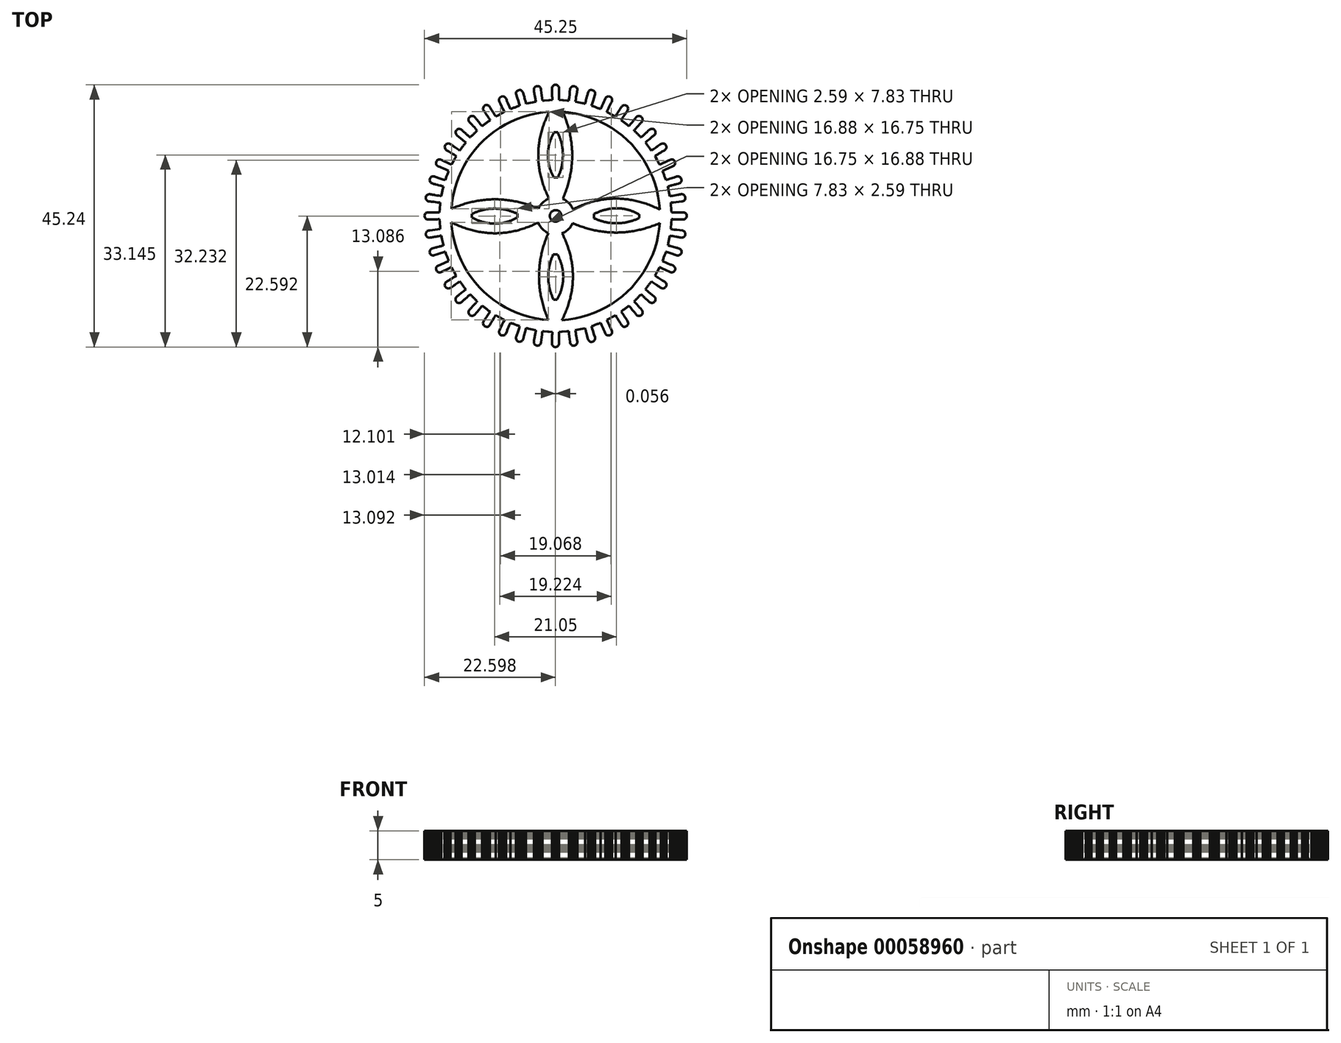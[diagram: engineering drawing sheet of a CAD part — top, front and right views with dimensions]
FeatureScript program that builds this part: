
annotation { "Feature Type Name" : "Feature", "Feature Type Description" : "" }
export const myFeature = defineFeature(function(context is Context, id is Id, definition is map)
    precondition{}
    {
        {
            var Q0;
            Q0=qCreatedBy(makeId("Top.planeOp"),FACE);
            var sketch = newSketch(context, id + "F0", { "sketchPlane" : qUnion([Q0])});
            skLineSegment(sketch, "E0", {"start": v(19.24, -0.57) * mm, "end": v(19.37, -0.57) * mm});
            skLineSegment(sketch, "E1", {"start": v(19.37, -0.57) * mm, "end": v(19.52, -0.58) * mm});
            skLineSegment(sketch, "E2", {"start": v(19.52, -0.58) * mm, "end": v(19.68, -0.58) * mm});
            skLineSegment(sketch, "E3", {"start": v(19.68, -0.58) * mm, "end": v(19.83, -0.59) * mm});
            skLineSegment(sketch, "E4", {"start": v(19.83, -0.59) * mm, "end": v(19.99, -0.6) * mm});
            skLineSegment(sketch, "E5", {"start": v(19.99, -0.6) * mm, "end": v(20.14, -0.6) * mm});
            skLineSegment(sketch, "E6", {"start": v(20.14, -0.6) * mm, "end": v(20.3, -0.6) * mm});
            skLineSegment(sketch, "E7", {"start": v(20.3, -0.6) * mm, "end": v(20.45, -0.6) * mm});
            skLineSegment(sketch, "E8", {"start": v(20.45, -0.6) * mm, "end": v(20.6, -0.6) * mm});
            skLineSegment(sketch, "E9", {"start": v(20.6, -0.6) * mm, "end": v(20.76, -0.61) * mm});
            skLineSegment(sketch, "E10", {"start": v(20.76, -0.61) * mm, "end": v(20.9, -0.62) * mm});
            skLineSegment(sketch, "E11", {"start": v(20.9, -0.62) * mm, "end": v(21.06, -0.62) * mm});
            skLineSegment(sketch, "E12", {"start": v(21.06, -0.62) * mm, "end": v(21.22, -0.63) * mm});
            skLineSegment(sketch, "E13", {"start": v(21.22, -0.63) * mm, "end": v(21.38, -0.6) * mm});
            skLineSegment(sketch, "E14", {"start": v(21.38, -0.6) * mm, "end": v(21.53, -0.54) * mm});
            skLineSegment(sketch, "E15", {"start": v(21.53, -0.54) * mm, "end": v(21.66, -0.45) * mm});
            skLineSegment(sketch, "E16", {"start": v(21.66, -0.45) * mm, "end": v(21.77, -0.32) * mm});
            skLineSegment(sketch, "E17", {"start": v(21.77, -0.32) * mm, "end": v(21.83, -0.16) * mm});
            skLineSegment(sketch, "E18", {"start": v(21.83, -0.16) * mm, "end": v(21.85, 0) * mm});
            skLineSegment(sketch, "E19", {"start": v(21.85, 0) * mm, "end": v(21.83, 0.16) * mm});
            skLineSegment(sketch, "E20", {"start": v(21.83, 0.16) * mm, "end": v(21.77, 0.31) * mm});
            skLineSegment(sketch, "E21", {"start": v(21.77, 0.31) * mm, "end": v(21.66, 0.44) * mm});
            skLineSegment(sketch, "E22", {"start": v(21.66, 0.44) * mm, "end": v(21.53, 0.54) * mm});
            skLineSegment(sketch, "E23", {"start": v(21.53, 0.54) * mm, "end": v(21.38, 0.6) * mm});
            skLineSegment(sketch, "E24", {"start": v(21.38, 0.6) * mm, "end": v(21.22, 0.62) * mm});
            skLineSegment(sketch, "E25", {"start": v(21.22, 0.62) * mm, "end": v(21.06, 0.62) * mm});
            skLineSegment(sketch, "E26", {"start": v(21.06, 0.62) * mm, "end": v(20.91, 0.62) * mm});
            skLineSegment(sketch, "E27", {"start": v(20.91, 0.62) * mm, "end": v(20.76, 0.61) * mm});
            skLineSegment(sketch, "E28", {"start": v(20.76, 0.61) * mm, "end": v(20.6, 0.6) * mm});
            skLineSegment(sketch, "E29", {"start": v(20.6, 0.6) * mm, "end": v(20.45, 0.6) * mm});
            skLineSegment(sketch, "E30", {"start": v(20.45, 0.6) * mm, "end": v(20.3, 0.6) * mm});
            skLineSegment(sketch, "E31", {"start": v(20.3, 0.6) * mm, "end": v(20.14, 0.6) * mm});
            skLineSegment(sketch, "E32", {"start": v(20.14, 0.6) * mm, "end": v(19.99, 0.59) * mm});
            skLineSegment(sketch, "E33", {"start": v(19.99, 0.59) * mm, "end": v(19.83, 0.59) * mm});
            skLineSegment(sketch, "E34", {"start": v(19.83, 0.59) * mm, "end": v(19.68, 0.58) * mm});
            skLineSegment(sketch, "E35", {"start": v(19.68, 0.58) * mm, "end": v(19.53, 0.58) * mm});
            skLineSegment(sketch, "E36", {"start": v(19.53, 0.58) * mm, "end": v(19.37, 0.57) * mm});
            skLineSegment(sketch, "E37", {"start": v(19.37, 0.57) * mm, "end": v(19.24, 0.57) * mm});
            skLineSegment(sketch, "E38", {"start": v(19.24, 0.57) * mm, "end": v(19.23, 0.72) * mm});
            skLineSegment(sketch, "E39", {"start": v(19.23, 0.72) * mm, "end": v(19.22, 0.87) * mm});
            skLineSegment(sketch, "E40", {"start": v(19.22, 0.87) * mm, "end": v(19.2, 1.03) * mm});
            skLineSegment(sketch, "E41", {"start": v(19.2, 1.03) * mm, "end": v(19.2, 1.18) * mm});
            skLineSegment(sketch, "E42", {"start": v(19.2, 1.18) * mm, "end": v(19.19, 1.33) * mm});
            skLineSegment(sketch, "E43", {"start": v(19.19, 1.33) * mm, "end": v(19.17, 1.49) * mm});
            skLineSegment(sketch, "E44", {"start": v(19.17, 1.49) * mm, "end": v(19.16, 1.64) * mm});
            skLineSegment(sketch, "E45", {"start": v(19.16, 1.64) * mm, "end": v(19.15, 1.8) * mm});
            skLineSegment(sketch, "E46", {"start": v(19.15, 1.8) * mm, "end": v(19.14, 1.94) * mm});
            skLineSegment(sketch, "E47", {"start": v(19.14, 1.94) * mm, "end": v(19.13, 2.1) * mm});
            skLineSegment(sketch, "E48", {"start": v(19.13, 2.1) * mm, "end": v(19.12, 2.25) * mm});
            skLineSegment(sketch, "E49", {"start": v(19.12, 2.25) * mm, "end": v(19.12, 2.28) * mm});
            skLineSegment(sketch, "E50", {"start": v(19.12, 2.28) * mm, "end": v(19.27, 2.3) * mm});
            skLineSegment(sketch, "E51", {"start": v(19.27, 2.3) * mm, "end": v(19.42, 2.32) * mm});
            skLineSegment(sketch, "E52", {"start": v(19.42, 2.32) * mm, "end": v(19.58, 2.34) * mm});
            skLineSegment(sketch, "E53", {"start": v(19.58, 2.34) * mm, "end": v(19.73, 2.35) * mm});
            skLineSegment(sketch, "E54", {"start": v(19.73, 2.35) * mm, "end": v(19.88, 2.37) * mm});
            skLineSegment(sketch, "E55", {"start": v(19.88, 2.37) * mm, "end": v(20.03, 2.39) * mm});
            skLineSegment(sketch, "E56", {"start": v(20.03, 2.39) * mm, "end": v(20.19, 2.4) * mm});
            skLineSegment(sketch, "E57", {"start": v(20.19, 2.4) * mm, "end": v(20.34, 2.42) * mm});
            skLineSegment(sketch, "E58", {"start": v(20.34, 2.42) * mm, "end": v(20.5, 2.44) * mm});
            skLineSegment(sketch, "E59", {"start": v(20.5, 2.44) * mm, "end": v(20.64, 2.46) * mm});
            skLineSegment(sketch, "E60", {"start": v(20.64, 2.46) * mm, "end": v(20.8, 2.48) * mm});
            skLineSegment(sketch, "E61", {"start": v(20.8, 2.48) * mm, "end": v(20.95, 2.5) * mm});
            skLineSegment(sketch, "E62", {"start": v(20.95, 2.5) * mm, "end": v(21.11, 2.52) * mm});
            skLineSegment(sketch, "E63", {"start": v(21.11, 2.52) * mm, "end": v(21.27, 2.57) * mm});
            skLineSegment(sketch, "E64", {"start": v(21.27, 2.57) * mm, "end": v(21.4, 2.66) * mm});
            skLineSegment(sketch, "E65", {"start": v(21.4, 2.66) * mm, "end": v(21.52, 2.78) * mm});
            skLineSegment(sketch, "E66", {"start": v(21.52, 2.78) * mm, "end": v(21.6, 2.93) * mm});
            skLineSegment(sketch, "E67", {"start": v(21.6, 2.93) * mm, "end": v(21.63, 3.09) * mm});
            skLineSegment(sketch, "E68", {"start": v(21.63, 3.09) * mm, "end": v(21.62, 3.25) * mm});
            skLineSegment(sketch, "E69", {"start": v(21.62, 3.25) * mm, "end": v(21.56, 3.4) * mm});
            skLineSegment(sketch, "E70", {"start": v(21.56, 3.4) * mm, "end": v(21.47, 3.54) * mm});
            skLineSegment(sketch, "E71", {"start": v(21.47, 3.54) * mm, "end": v(21.35, 3.65) * mm});
            skLineSegment(sketch, "E72", {"start": v(21.35, 3.65) * mm, "end": v(21.2, 3.72) * mm});
            skLineSegment(sketch, "E73", {"start": v(21.2, 3.72) * mm, "end": v(21.04, 3.75) * mm});
            skLineSegment(sketch, "E74", {"start": v(21.04, 3.75) * mm, "end": v(21, 3.76) * mm});
            skLineSegment(sketch, "E75", {"start": v(21, 3.76) * mm, "end": v(20.9, 3.75) * mm});
            skLineSegment(sketch, "E76", {"start": v(20.9, 3.75) * mm, "end": v(20.75, 3.72) * mm});
            skLineSegment(sketch, "E77", {"start": v(20.75, 3.72) * mm, "end": v(20.6, 3.7) * mm});
            skLineSegment(sketch, "E78", {"start": v(20.6, 3.7) * mm, "end": v(20.45, 3.67) * mm});
            skLineSegment(sketch, "E79", {"start": v(20.45, 3.67) * mm, "end": v(20.3, 3.64) * mm});
            skLineSegment(sketch, "E80", {"start": v(20.3, 3.64) * mm, "end": v(20.15, 3.62) * mm});
            skLineSegment(sketch, "E81", {"start": v(20.15, 3.62) * mm, "end": v(20, 3.6) * mm});
            skLineSegment(sketch, "E82", {"start": v(20, 3.6) * mm, "end": v(19.84, 3.56) * mm});
            skLineSegment(sketch, "E83", {"start": v(19.84, 3.56) * mm, "end": v(19.7, 3.54) * mm});
            skLineSegment(sketch, "E84", {"start": v(19.7, 3.54) * mm, "end": v(19.54, 3.51) * mm});
            skLineSegment(sketch, "E85", {"start": v(19.54, 3.51) * mm, "end": v(19.39, 3.49) * mm});
            skLineSegment(sketch, "E86", {"start": v(19.39, 3.49) * mm, "end": v(19.24, 3.46) * mm});
            skLineSegment(sketch, "E87", {"start": v(19.24, 3.46) * mm, "end": v(19.09, 3.43) * mm});
            skLineSegment(sketch, "E88", {"start": v(19.09, 3.43) * mm, "end": v(18.96, 3.41) * mm});
            skLineSegment(sketch, "E89", {"start": v(18.96, 3.41) * mm, "end": v(18.92, 3.56) * mm});
            skLineSegment(sketch, "E90", {"start": v(18.92, 3.56) * mm, "end": v(18.9, 3.71) * mm});
            skLineSegment(sketch, "E91", {"start": v(18.9, 3.71) * mm, "end": v(18.86, 3.86) * mm});
            skLineSegment(sketch, "E92", {"start": v(18.86, 3.86) * mm, "end": v(18.83, 4) * mm});
            skLineSegment(sketch, "E93", {"start": v(18.83, 4) * mm, "end": v(18.8, 4.16) * mm});
            skLineSegment(sketch, "E94", {"start": v(18.8, 4.16) * mm, "end": v(18.76, 4.3) * mm});
            skLineSegment(sketch, "E95", {"start": v(18.76, 4.3) * mm, "end": v(18.73, 4.46) * mm});
            skLineSegment(sketch, "E96", {"start": v(18.73, 4.46) * mm, "end": v(18.7, 4.6) * mm});
            skLineSegment(sketch, "E97", {"start": v(18.7, 4.6) * mm, "end": v(18.66, 4.76) * mm});
            skLineSegment(sketch, "E98", {"start": v(18.66, 4.76) * mm, "end": v(18.63, 4.9) * mm});
            skLineSegment(sketch, "E99", {"start": v(18.63, 4.9) * mm, "end": v(18.6, 5.06) * mm});
            skLineSegment(sketch, "E100", {"start": v(18.6, 5.06) * mm, "end": v(18.59, 5.1) * mm});
            skLineSegment(sketch, "E101", {"start": v(18.59, 5.1) * mm, "end": v(18.74, 5.13) * mm});
            skLineSegment(sketch, "E102", {"start": v(18.74, 5.13) * mm, "end": v(18.89, 5.17) * mm});
            skLineSegment(sketch, "E103", {"start": v(18.89, 5.17) * mm, "end": v(19.04, 5.2) * mm});
            skLineSegment(sketch, "E104", {"start": v(19.04, 5.2) * mm, "end": v(19.18, 5.25) * mm});
            skLineSegment(sketch, "E105", {"start": v(19.18, 5.25) * mm, "end": v(19.33, 5.29) * mm});
            skLineSegment(sketch, "E106", {"start": v(19.33, 5.29) * mm, "end": v(19.48, 5.33) * mm});
            skLineSegment(sketch, "E107", {"start": v(19.48, 5.33) * mm, "end": v(19.63, 5.37) * mm});
            skLineSegment(sketch, "E108", {"start": v(19.63, 5.37) * mm, "end": v(19.78, 5.4) * mm});
            skLineSegment(sketch, "E109", {"start": v(19.78, 5.4) * mm, "end": v(19.93, 5.44) * mm});
            skLineSegment(sketch, "E110", {"start": v(19.93, 5.44) * mm, "end": v(20.08, 5.48) * mm});
            skLineSegment(sketch, "E111", {"start": v(20.08, 5.48) * mm, "end": v(20.22, 5.52) * mm});
            skLineSegment(sketch, "E112", {"start": v(20.22, 5.52) * mm, "end": v(20.37, 5.56) * mm});
            skLineSegment(sketch, "E113", {"start": v(20.37, 5.56) * mm, "end": v(20.53, 5.6) * mm});
            skLineSegment(sketch, "E114", {"start": v(20.53, 5.6) * mm, "end": v(20.68, 5.68) * mm});
            skLineSegment(sketch, "E115", {"start": v(20.68, 5.68) * mm, "end": v(20.8, 5.79) * mm});
            skLineSegment(sketch, "E116", {"start": v(20.8, 5.79) * mm, "end": v(20.9, 5.92) * mm});
            skLineSegment(sketch, "E117", {"start": v(20.9, 5.92) * mm, "end": v(20.95, 6.08) * mm});
            skLineSegment(sketch, "E118", {"start": v(20.95, 6.08) * mm, "end": v(20.96, 6.24) * mm});
            skLineSegment(sketch, "E119", {"start": v(20.96, 6.24) * mm, "end": v(20.92, 6.4) * mm});
            skLineSegment(sketch, "E120", {"start": v(20.92, 6.4) * mm, "end": v(20.85, 6.55) * mm});
            skLineSegment(sketch, "E121", {"start": v(20.85, 6.55) * mm, "end": v(20.74, 6.67) * mm});
            skLineSegment(sketch, "E122", {"start": v(20.74, 6.67) * mm, "end": v(20.6, 6.76) * mm});
            skLineSegment(sketch, "E123", {"start": v(20.6, 6.76) * mm, "end": v(20.44, 6.81) * mm});
            skLineSegment(sketch, "E124", {"start": v(20.44, 6.81) * mm, "end": v(20.35, 6.82) * mm});
            skLineSegment(sketch, "E125", {"start": v(20.35, 6.82) * mm, "end": v(20.18, 6.8) * mm});
            skLineSegment(sketch, "E126", {"start": v(20.18, 6.8) * mm, "end": v(20.15, 6.8) * mm});
            skLineSegment(sketch, "E127", {"start": v(20.15, 6.8) * mm, "end": v(20, 6.75) * mm});
            skLineSegment(sketch, "E128", {"start": v(20, 6.75) * mm, "end": v(19.86, 6.7) * mm});
            skLineSegment(sketch, "E129", {"start": v(19.86, 6.7) * mm, "end": v(19.71, 6.65) * mm});
            skLineSegment(sketch, "E130", {"start": v(19.71, 6.65) * mm, "end": v(19.57, 6.6) * mm});
            skLineSegment(sketch, "E131", {"start": v(19.57, 6.6) * mm, "end": v(19.42, 6.56) * mm});
            skLineSegment(sketch, "E132", {"start": v(19.42, 6.56) * mm, "end": v(19.27, 6.5) * mm});
            skLineSegment(sketch, "E133", {"start": v(19.27, 6.5) * mm, "end": v(19.13, 6.46) * mm});
            skLineSegment(sketch, "E134", {"start": v(19.13, 6.46) * mm, "end": v(18.98, 6.42) * mm});
            skLineSegment(sketch, "E135", {"start": v(18.98, 6.42) * mm, "end": v(18.83, 6.37) * mm});
            skLineSegment(sketch, "E136", {"start": v(18.83, 6.37) * mm, "end": v(18.69, 6.32) * mm});
            skLineSegment(sketch, "E137", {"start": v(18.69, 6.32) * mm, "end": v(18.54, 6.27) * mm});
            skLineSegment(sketch, "E138", {"start": v(18.54, 6.27) * mm, "end": v(18.4, 6.22) * mm});
            skLineSegment(sketch, "E139", {"start": v(18.4, 6.22) * mm, "end": v(18.27, 6.18) * mm});
            skLineSegment(sketch, "E140", {"start": v(18.27, 6.18) * mm, "end": v(18.22, 6.33) * mm});
            skLineSegment(sketch, "E141", {"start": v(18.22, 6.33) * mm, "end": v(18.16, 6.47) * mm});
            skLineSegment(sketch, "E142", {"start": v(18.16, 6.47) * mm, "end": v(18.1, 6.61) * mm});
            skLineSegment(sketch, "E143", {"start": v(18.1, 6.61) * mm, "end": v(18.05, 6.76) * mm});
            skLineSegment(sketch, "E144", {"start": v(18.05, 6.76) * mm, "end": v(18, 6.9) * mm});
            skLineSegment(sketch, "E145", {"start": v(18, 6.9) * mm, "end": v(17.95, 7.05) * mm});
            skLineSegment(sketch, "E146", {"start": v(17.95, 7.05) * mm, "end": v(17.9, 7.19) * mm});
            skLineSegment(sketch, "E147", {"start": v(17.9, 7.19) * mm, "end": v(17.84, 7.33) * mm});
            skLineSegment(sketch, "E148", {"start": v(17.84, 7.33) * mm, "end": v(17.79, 7.48) * mm});
            skLineSegment(sketch, "E149", {"start": v(17.79, 7.48) * mm, "end": v(17.73, 7.62) * mm});
            skLineSegment(sketch, "E150", {"start": v(17.73, 7.62) * mm, "end": v(17.68, 7.76) * mm});
            skLineSegment(sketch, "E151", {"start": v(17.68, 7.76) * mm, "end": v(17.67, 7.8) * mm});
            skLineSegment(sketch, "E152", {"start": v(17.67, 7.8) * mm, "end": v(17.8, 7.86) * mm});
            skLineSegment(sketch, "E153", {"start": v(17.8, 7.86) * mm, "end": v(17.95, 7.92) * mm});
            skLineSegment(sketch, "E154", {"start": v(17.95, 7.92) * mm, "end": v(18.1, 7.98) * mm});
            skLineSegment(sketch, "E155", {"start": v(18.1, 7.98) * mm, "end": v(18.23, 8.04) * mm});
            skLineSegment(sketch, "E156", {"start": v(18.23, 8.04) * mm, "end": v(18.38, 8.1) * mm});
            skLineSegment(sketch, "E157", {"start": v(18.38, 8.1) * mm, "end": v(18.52, 8.16) * mm});
            skLineSegment(sketch, "E158", {"start": v(18.52, 8.16) * mm, "end": v(18.66, 8.22) * mm});
            skLineSegment(sketch, "E159", {"start": v(18.66, 8.22) * mm, "end": v(18.8, 8.27) * mm});
            skLineSegment(sketch, "E160", {"start": v(18.8, 8.27) * mm, "end": v(18.94, 8.34) * mm});
            skLineSegment(sketch, "E161", {"start": v(18.94, 8.34) * mm, "end": v(19.08, 8.4) * mm});
            skLineSegment(sketch, "E162", {"start": v(19.08, 8.4) * mm, "end": v(19.23, 8.45) * mm});
            skLineSegment(sketch, "E163", {"start": v(19.23, 8.45) * mm, "end": v(19.37, 8.51) * mm});
            skLineSegment(sketch, "E164", {"start": v(19.37, 8.51) * mm, "end": v(19.52, 8.58) * mm});
            skLineSegment(sketch, "E165", {"start": v(19.52, 8.58) * mm, "end": v(19.66, 8.67) * mm});
            skLineSegment(sketch, "E166", {"start": v(19.66, 8.67) * mm, "end": v(19.76, 8.8) * mm});
            skLineSegment(sketch, "E167", {"start": v(19.76, 8.8) * mm, "end": v(19.83, 8.95) * mm});
            skLineSegment(sketch, "E168", {"start": v(19.83, 8.95) * mm, "end": v(19.86, 9.1) * mm});
            skLineSegment(sketch, "E169", {"start": v(19.86, 9.1) * mm, "end": v(19.85, 9.27) * mm});
            skLineSegment(sketch, "E170", {"start": v(19.85, 9.27) * mm, "end": v(19.8, 9.4) * mm});
            skLineSegment(sketch, "E171", {"start": v(19.8, 9.4) * mm, "end": v(19.72, 9.54) * mm});
            skLineSegment(sketch, "E172", {"start": v(19.72, 9.54) * mm, "end": v(19.6, 9.65) * mm});
            skLineSegment(sketch, "E173", {"start": v(19.6, 9.65) * mm, "end": v(19.45, 9.73) * mm});
            skLineSegment(sketch, "E174", {"start": v(19.45, 9.73) * mm, "end": v(19.3, 9.76) * mm});
            skLineSegment(sketch, "E175", {"start": v(19.3, 9.76) * mm, "end": v(19.23, 9.76) * mm});
            skLineSegment(sketch, "E176", {"start": v(19.23, 9.76) * mm, "end": v(19.06, 9.74) * mm});
            skLineSegment(sketch, "E177", {"start": v(19.06, 9.74) * mm, "end": v(18.97, 9.7) * mm});
            skLineSegment(sketch, "E178", {"start": v(18.97, 9.7) * mm, "end": v(18.83, 9.64) * mm});
            skLineSegment(sketch, "E179", {"start": v(18.83, 9.64) * mm, "end": v(18.7, 9.57) * mm});
            skLineSegment(sketch, "E180", {"start": v(18.7, 9.57) * mm, "end": v(18.56, 9.5) * mm});
            skLineSegment(sketch, "E181", {"start": v(18.56, 9.5) * mm, "end": v(18.42, 9.43) * mm});
            skLineSegment(sketch, "E182", {"start": v(18.42, 9.43) * mm, "end": v(18.28, 9.37) * mm});
            skLineSegment(sketch, "E183", {"start": v(18.28, 9.37) * mm, "end": v(18.14, 9.3) * mm});
            skLineSegment(sketch, "E184", {"start": v(18.14, 9.3) * mm, "end": v(18, 9.23) * mm});
            skLineSegment(sketch, "E185", {"start": v(18, 9.23) * mm, "end": v(17.87, 9.16) * mm});
            skLineSegment(sketch, "E186", {"start": v(17.87, 9.16) * mm, "end": v(17.73, 9.1) * mm});
            skLineSegment(sketch, "E187", {"start": v(17.73, 9.1) * mm, "end": v(17.6, 9.03) * mm});
            skLineSegment(sketch, "E188", {"start": v(17.6, 9.03) * mm, "end": v(17.45, 8.96) * mm});
            skLineSegment(sketch, "E189", {"start": v(17.45, 8.96) * mm, "end": v(17.31, 8.89) * mm});
            skLineSegment(sketch, "E190", {"start": v(17.31, 8.89) * mm, "end": v(17.2, 8.83) * mm});
            skLineSegment(sketch, "E191", {"start": v(17.2, 8.83) * mm, "end": v(17.12, 8.97) * mm});
            skLineSegment(sketch, "E192", {"start": v(17.12, 8.97) * mm, "end": v(17.05, 9.1) * mm});
            skLineSegment(sketch, "E193", {"start": v(17.05, 9.1) * mm, "end": v(16.97, 9.23) * mm});
            skLineSegment(sketch, "E194", {"start": v(16.97, 9.23) * mm, "end": v(16.9, 9.37) * mm});
            skLineSegment(sketch, "E195", {"start": v(16.9, 9.37) * mm, "end": v(16.83, 9.5) * mm});
            skLineSegment(sketch, "E196", {"start": v(16.83, 9.5) * mm, "end": v(16.75, 9.64) * mm});
            skLineSegment(sketch, "E197", {"start": v(16.75, 9.64) * mm, "end": v(16.68, 9.77) * mm});
            skLineSegment(sketch, "E198", {"start": v(16.68, 9.77) * mm, "end": v(16.6, 9.9) * mm});
            skLineSegment(sketch, "E199", {"start": v(16.6, 9.9) * mm, "end": v(16.53, 10.04) * mm});
            skLineSegment(sketch, "E200", {"start": v(16.53, 10.04) * mm, "end": v(16.46, 10.18) * mm});
            skLineSegment(sketch, "E201", {"start": v(16.46, 10.18) * mm, "end": v(16.39, 10.3) * mm});
            skLineSegment(sketch, "E202", {"start": v(16.39, 10.3) * mm, "end": v(16.37, 10.34) * mm});
            skLineSegment(sketch, "E203", {"start": v(16.37, 10.34) * mm, "end": v(16.5, 10.42) * mm});
            skLineSegment(sketch, "E204", {"start": v(16.5, 10.42) * mm, "end": v(16.63, 10.5) * mm});
            skLineSegment(sketch, "E205", {"start": v(16.63, 10.5) * mm, "end": v(16.77, 10.58) * mm});
            skLineSegment(sketch, "E206", {"start": v(16.77, 10.58) * mm, "end": v(16.9, 10.66) * mm});
            skLineSegment(sketch, "E207", {"start": v(16.9, 10.66) * mm, "end": v(17.03, 10.74) * mm});
            skLineSegment(sketch, "E208", {"start": v(17.03, 10.74) * mm, "end": v(17.16, 10.82) * mm});
            skLineSegment(sketch, "E209", {"start": v(17.16, 10.82) * mm, "end": v(17.3, 10.9) * mm});
            skLineSegment(sketch, "E210", {"start": v(17.3, 10.9) * mm, "end": v(17.42, 10.98) * mm});
            skLineSegment(sketch, "E211", {"start": v(17.42, 10.98) * mm, "end": v(17.56, 11.06) * mm});
            skLineSegment(sketch, "E212", {"start": v(17.56, 11.06) * mm, "end": v(17.69, 11.14) * mm});
            skLineSegment(sketch, "E213", {"start": v(17.69, 11.14) * mm, "end": v(17.82, 11.21) * mm});
            skLineSegment(sketch, "E214", {"start": v(17.82, 11.21) * mm, "end": v(17.95, 11.3) * mm});
            skLineSegment(sketch, "E215", {"start": v(17.95, 11.3) * mm, "end": v(18.1, 11.38) * mm});
            skLineSegment(sketch, "E216", {"start": v(18.1, 11.38) * mm, "end": v(18.21, 11.5) * mm});
            skLineSegment(sketch, "E217", {"start": v(18.21, 11.5) * mm, "end": v(18.3, 11.63) * mm});
            skLineSegment(sketch, "E218", {"start": v(18.3, 11.63) * mm, "end": v(18.35, 11.79) * mm});
            skLineSegment(sketch, "E219", {"start": v(18.35, 11.79) * mm, "end": v(18.36, 11.95) * mm});
            skLineSegment(sketch, "E220", {"start": v(18.36, 11.95) * mm, "end": v(18.32, 12.11) * mm});
            skLineSegment(sketch, "E221", {"start": v(18.32, 12.11) * mm, "end": v(18.26, 12.23) * mm});
            skLineSegment(sketch, "E222", {"start": v(18.26, 12.23) * mm, "end": v(18.15, 12.36) * mm});
            skLineSegment(sketch, "E223", {"start": v(18.15, 12.36) * mm, "end": v(18.02, 12.45) * mm});
            skLineSegment(sketch, "E224", {"start": v(18.02, 12.45) * mm, "end": v(17.86, 12.5) * mm});
            skLineSegment(sketch, "E225", {"start": v(17.86, 12.5) * mm, "end": v(17.73, 12.52) * mm});
            skLineSegment(sketch, "E226", {"start": v(17.73, 12.52) * mm, "end": v(17.57, 12.5) * mm});
            skLineSegment(sketch, "E227", {"start": v(17.57, 12.5) * mm, "end": v(17.42, 12.43) * mm});
            skLineSegment(sketch, "E228", {"start": v(17.42, 12.43) * mm, "end": v(17.39, 12.41) * mm});
            skLineSegment(sketch, "E229", {"start": v(17.39, 12.41) * mm, "end": v(17.26, 12.33) * mm});
            skLineSegment(sketch, "E230", {"start": v(17.26, 12.33) * mm, "end": v(17.14, 12.24) * mm});
            skLineSegment(sketch, "E231", {"start": v(17.14, 12.24) * mm, "end": v(17, 12.15) * mm});
            skLineSegment(sketch, "E232", {"start": v(17, 12.15) * mm, "end": v(16.88, 12.07) * mm});
            skLineSegment(sketch, "E233", {"start": v(16.88, 12.07) * mm, "end": v(16.75, 11.98) * mm});
            skLineSegment(sketch, "E234", {"start": v(16.75, 11.98) * mm, "end": v(16.63, 11.9) * mm});
            skLineSegment(sketch, "E235", {"start": v(16.63, 11.9) * mm, "end": v(16.5, 11.8) * mm});
            skLineSegment(sketch, "E236", {"start": v(16.5, 11.8) * mm, "end": v(16.37, 11.72) * mm});
            skLineSegment(sketch, "E237", {"start": v(16.37, 11.72) * mm, "end": v(16.25, 11.63) * mm});
            skLineSegment(sketch, "E238", {"start": v(16.25, 11.63) * mm, "end": v(16.12, 11.55) * mm});
            skLineSegment(sketch, "E239", {"start": v(16.12, 11.55) * mm, "end": v(16, 11.46) * mm});
            skLineSegment(sketch, "E240", {"start": v(16, 11.46) * mm, "end": v(15.86, 11.37) * mm});
            skLineSegment(sketch, "E241", {"start": v(15.86, 11.37) * mm, "end": v(15.76, 11.3) * mm});
            skLineSegment(sketch, "E242", {"start": v(15.76, 11.3) * mm, "end": v(15.66, 11.42) * mm});
            skLineSegment(sketch, "E243", {"start": v(15.66, 11.42) * mm, "end": v(15.57, 11.54) * mm});
            skLineSegment(sketch, "E244", {"start": v(15.57, 11.54) * mm, "end": v(15.48, 11.67) * mm});
            skLineSegment(sketch, "E245", {"start": v(15.48, 11.67) * mm, "end": v(15.39, 11.79) * mm});
            skLineSegment(sketch, "E246", {"start": v(15.39, 11.79) * mm, "end": v(15.3, 11.91) * mm});
            skLineSegment(sketch, "E247", {"start": v(15.3, 11.91) * mm, "end": v(15.2, 12.03) * mm});
            skLineSegment(sketch, "E248", {"start": v(15.2, 12.03) * mm, "end": v(15.11, 12.16) * mm});
            skLineSegment(sketch, "E249", {"start": v(15.11, 12.16) * mm, "end": v(15.02, 12.28) * mm});
            skLineSegment(sketch, "E250", {"start": v(15.02, 12.28) * mm, "end": v(14.93, 12.4) * mm});
            skLineSegment(sketch, "E251", {"start": v(14.93, 12.4) * mm, "end": v(14.84, 12.52) * mm});
            skLineSegment(sketch, "E252", {"start": v(14.84, 12.52) * mm, "end": v(14.75, 12.65) * mm});
            skLineSegment(sketch, "E253", {"start": v(14.75, 12.65) * mm, "end": v(14.72, 12.68) * mm});
            skLineSegment(sketch, "E254", {"start": v(14.72, 12.68) * mm, "end": v(14.84, 12.77) * mm});
            skLineSegment(sketch, "E255", {"start": v(14.84, 12.77) * mm, "end": v(14.96, 12.87) * mm});
            skLineSegment(sketch, "E256", {"start": v(14.96, 12.87) * mm, "end": v(15.08, 12.97) * mm});
            skLineSegment(sketch, "E257", {"start": v(15.08, 12.97) * mm, "end": v(15.2, 13.07) * mm});
            skLineSegment(sketch, "E258", {"start": v(15.2, 13.07) * mm, "end": v(15.32, 13.16) * mm});
            skLineSegment(sketch, "E259", {"start": v(15.32, 13.16) * mm, "end": v(15.44, 13.26) * mm});
            skLineSegment(sketch, "E260", {"start": v(15.44, 13.26) * mm, "end": v(15.56, 13.36) * mm});
            skLineSegment(sketch, "E261", {"start": v(15.56, 13.36) * mm, "end": v(15.68, 13.45) * mm});
            skLineSegment(sketch, "E262", {"start": v(15.68, 13.45) * mm, "end": v(15.8, 13.55) * mm});
            skLineSegment(sketch, "E263", {"start": v(15.8, 13.55) * mm, "end": v(15.91, 13.65) * mm});
            skLineSegment(sketch, "E264", {"start": v(15.91, 13.65) * mm, "end": v(16.03, 13.75) * mm});
            skLineSegment(sketch, "E265", {"start": v(16.03, 13.75) * mm, "end": v(16.15, 13.84) * mm});
            skLineSegment(sketch, "E266", {"start": v(16.15, 13.84) * mm, "end": v(16.28, 13.95) * mm});
            skLineSegment(sketch, "E267", {"start": v(16.28, 13.95) * mm, "end": v(16.38, 14.08) * mm});
            skLineSegment(sketch, "E268", {"start": v(16.38, 14.08) * mm, "end": v(16.45, 14.23) * mm});
            skLineSegment(sketch, "E269", {"start": v(16.45, 14.23) * mm, "end": v(16.48, 14.4) * mm});
            skLineSegment(sketch, "E270", {"start": v(16.48, 14.4) * mm, "end": v(16.46, 14.55) * mm});
            skLineSegment(sketch, "E271", {"start": v(16.46, 14.55) * mm, "end": v(16.4, 14.7) * mm});
            skLineSegment(sketch, "E272", {"start": v(16.4, 14.7) * mm, "end": v(16.32, 14.82) * mm});
            skLineSegment(sketch, "E273", {"start": v(16.32, 14.82) * mm, "end": v(16.2, 14.93) * mm});
            skLineSegment(sketch, "E274", {"start": v(16.2, 14.93) * mm, "end": v(16.05, 15) * mm});
            skLineSegment(sketch, "E275", {"start": v(16.05, 15) * mm, "end": v(15.9, 15.03) * mm});
            skLineSegment(sketch, "E276", {"start": v(15.9, 15.03) * mm, "end": v(15.86, 15.03) * mm});
            skLineSegment(sketch, "E277", {"start": v(15.86, 15.03) * mm, "end": v(15.7, 15.01) * mm});
            skLineSegment(sketch, "E278", {"start": v(15.7, 15.01) * mm, "end": v(15.54, 14.95) * mm});
            skLineSegment(sketch, "E279", {"start": v(15.54, 14.95) * mm, "end": v(15.44, 14.87) * mm});
            skLineSegment(sketch, "E280", {"start": v(15.44, 14.87) * mm, "end": v(15.32, 14.77) * mm});
            skLineSegment(sketch, "E281", {"start": v(15.32, 14.77) * mm, "end": v(15.21, 14.67) * mm});
            skLineSegment(sketch, "E282", {"start": v(15.21, 14.67) * mm, "end": v(15.1, 14.56) * mm});
            skLineSegment(sketch, "E283", {"start": v(15.1, 14.56) * mm, "end": v(14.98, 14.46) * mm});
            skLineSegment(sketch, "E284", {"start": v(14.98, 14.46) * mm, "end": v(14.87, 14.35) * mm});
            skLineSegment(sketch, "E285", {"start": v(14.87, 14.35) * mm, "end": v(14.76, 14.25) * mm});
            skLineSegment(sketch, "E286", {"start": v(14.76, 14.25) * mm, "end": v(14.64, 14.15) * mm});
            skLineSegment(sketch, "E287", {"start": v(14.64, 14.15) * mm, "end": v(14.53, 14.04) * mm});
            skLineSegment(sketch, "E288", {"start": v(14.53, 14.04) * mm, "end": v(14.42, 13.94) * mm});
            skLineSegment(sketch, "E289", {"start": v(14.42, 13.94) * mm, "end": v(14.3, 13.83) * mm});
            skLineSegment(sketch, "E290", {"start": v(14.3, 13.83) * mm, "end": v(14.2, 13.73) * mm});
            skLineSegment(sketch, "E291", {"start": v(14.2, 13.73) * mm, "end": v(14.08, 13.63) * mm});
            skLineSegment(sketch, "E292", {"start": v(14.08, 13.63) * mm, "end": v(13.98, 13.54) * mm});
            skLineSegment(sketch, "E293", {"start": v(13.98, 13.54) * mm, "end": v(13.87, 13.64) * mm});
            skLineSegment(sketch, "E294", {"start": v(13.87, 13.64) * mm, "end": v(13.76, 13.75) * mm});
            skLineSegment(sketch, "E295", {"start": v(13.76, 13.75) * mm, "end": v(13.65, 13.86) * mm});
            skLineSegment(sketch, "E296", {"start": v(13.65, 13.86) * mm, "end": v(13.55, 13.97) * mm});
            skLineSegment(sketch, "E297", {"start": v(13.55, 13.97) * mm, "end": v(13.44, 14.08) * mm});
            skLineSegment(sketch, "E298", {"start": v(13.44, 14.08) * mm, "end": v(13.33, 14.19) * mm});
            skLineSegment(sketch, "E299", {"start": v(13.33, 14.19) * mm, "end": v(13.22, 14.3) * mm});
            skLineSegment(sketch, "E300", {"start": v(13.22, 14.3) * mm, "end": v(13.11, 14.4) * mm});
            skLineSegment(sketch, "E301", {"start": v(13.11, 14.4) * mm, "end": v(13, 14.51) * mm});
            skLineSegment(sketch, "E302", {"start": v(13, 14.51) * mm, "end": v(12.9, 14.62) * mm});
            skLineSegment(sketch, "E303", {"start": v(12.9, 14.62) * mm, "end": v(12.79, 14.73) * mm});
            skLineSegment(sketch, "E304", {"start": v(12.79, 14.73) * mm, "end": v(12.76, 14.75) * mm});
            skLineSegment(sketch, "E305", {"start": v(12.76, 14.75) * mm, "end": v(12.87, 14.87) * mm});
            skLineSegment(sketch, "E306", {"start": v(12.87, 14.87) * mm, "end": v(12.97, 14.98) * mm});
            skLineSegment(sketch, "E307", {"start": v(12.97, 14.98) * mm, "end": v(13.07, 15.1) * mm});
            skLineSegment(sketch, "E308", {"start": v(13.07, 15.1) * mm, "end": v(13.18, 15.2) * mm});
            skLineSegment(sketch, "E309", {"start": v(13.18, 15.2) * mm, "end": v(13.28, 15.32) * mm});
            skLineSegment(sketch, "E310", {"start": v(13.28, 15.32) * mm, "end": v(13.39, 15.43) * mm});
            skLineSegment(sketch, "E311", {"start": v(13.39, 15.43) * mm, "end": v(13.5, 15.55) * mm});
            skLineSegment(sketch, "E312", {"start": v(13.5, 15.55) * mm, "end": v(13.6, 15.66) * mm});
            skLineSegment(sketch, "E313", {"start": v(13.6, 15.66) * mm, "end": v(13.7, 15.77) * mm});
            skLineSegment(sketch, "E314", {"start": v(13.7, 15.77) * mm, "end": v(13.8, 15.89) * mm});
            skLineSegment(sketch, "E315", {"start": v(13.8, 15.89) * mm, "end": v(13.9, 16) * mm});
            skLineSegment(sketch, "E316", {"start": v(13.9, 16) * mm, "end": v(14.01, 16.11) * mm});
            skLineSegment(sketch, "E317", {"start": v(14.01, 16.11) * mm, "end": v(14.12, 16.24) * mm});
            skLineSegment(sketch, "E318", {"start": v(14.12, 16.24) * mm, "end": v(14.2, 16.38) * mm});
            skLineSegment(sketch, "E319", {"start": v(14.2, 16.38) * mm, "end": v(14.25, 16.53) * mm});
            skLineSegment(sketch, "E320", {"start": v(14.25, 16.53) * mm, "end": v(14.25, 16.7) * mm});
            skLineSegment(sketch, "E321", {"start": v(14.25, 16.7) * mm, "end": v(14.21, 16.86) * mm});
            skLineSegment(sketch, "E322", {"start": v(14.21, 16.86) * mm, "end": v(14.13, 17) * mm});
            skLineSegment(sketch, "E323", {"start": v(14.13, 17) * mm, "end": v(14.04, 17.1) * mm});
            skLineSegment(sketch, "E324", {"start": v(14.04, 17.1) * mm, "end": v(13.9, 17.19) * mm});
            skLineSegment(sketch, "E325", {"start": v(13.9, 17.19) * mm, "end": v(13.75, 17.24) * mm});
            skLineSegment(sketch, "E326", {"start": v(13.75, 17.24) * mm, "end": v(13.62, 17.25) * mm});
            skLineSegment(sketch, "E327", {"start": v(13.62, 17.25) * mm, "end": v(13.45, 17.23) * mm});
            skLineSegment(sketch, "E328", {"start": v(13.45, 17.23) * mm, "end": v(13.3, 17.16) * mm});
            skLineSegment(sketch, "E329", {"start": v(13.3, 17.16) * mm, "end": v(13.18, 17.05) * mm});
            skLineSegment(sketch, "E330", {"start": v(13.18, 17.05) * mm, "end": v(13.15, 17.03) * mm});
            skLineSegment(sketch, "E331", {"start": v(13.15, 17.03) * mm, "end": v(13.06, 16.91) * mm});
            skLineSegment(sketch, "E332", {"start": v(13.06, 16.91) * mm, "end": v(12.96, 16.8) * mm});
            skLineSegment(sketch, "E333", {"start": v(12.96, 16.8) * mm, "end": v(12.86, 16.67) * mm});
            skLineSegment(sketch, "E334", {"start": v(12.86, 16.67) * mm, "end": v(12.77, 16.55) * mm});
            skLineSegment(sketch, "E335", {"start": v(12.77, 16.55) * mm, "end": v(12.67, 16.43) * mm});
            skLineSegment(sketch, "E336", {"start": v(12.67, 16.43) * mm, "end": v(12.57, 16.31) * mm});
            skLineSegment(sketch, "E337", {"start": v(12.57, 16.31) * mm, "end": v(12.47, 16.2) * mm});
            skLineSegment(sketch, "E338", {"start": v(12.47, 16.2) * mm, "end": v(12.38, 16.08) * mm});
            skLineSegment(sketch, "E339", {"start": v(12.38, 16.08) * mm, "end": v(12.28, 15.96) * mm});
            skLineSegment(sketch, "E340", {"start": v(12.28, 15.96) * mm, "end": v(12.18, 15.84) * mm});
            skLineSegment(sketch, "E341", {"start": v(12.18, 15.84) * mm, "end": v(12.08, 15.72) * mm});
            skLineSegment(sketch, "E342", {"start": v(12.08, 15.72) * mm, "end": v(11.99, 15.6) * mm});
            skLineSegment(sketch, "E343", {"start": v(11.99, 15.6) * mm, "end": v(11.9, 15.5) * mm});
            skLineSegment(sketch, "E344", {"start": v(11.9, 15.5) * mm, "end": v(11.78, 15.59) * mm});
            skLineSegment(sketch, "E345", {"start": v(11.78, 15.59) * mm, "end": v(11.66, 15.68) * mm});
            skLineSegment(sketch, "E346", {"start": v(11.66, 15.68) * mm, "end": v(11.53, 15.77) * mm});
            skLineSegment(sketch, "E347", {"start": v(11.53, 15.77) * mm, "end": v(11.41, 15.86) * mm});
            skLineSegment(sketch, "E348", {"start": v(11.41, 15.86) * mm, "end": v(11.29, 15.96) * mm});
            skLineSegment(sketch, "E349", {"start": v(11.29, 15.96) * mm, "end": v(11.17, 16.05) * mm});
            skLineSegment(sketch, "E350", {"start": v(11.17, 16.05) * mm, "end": v(11.04, 16.14) * mm});
            skLineSegment(sketch, "E351", {"start": v(11.04, 16.14) * mm, "end": v(10.92, 16.23) * mm});
            skLineSegment(sketch, "E352", {"start": v(10.92, 16.23) * mm, "end": v(10.8, 16.32) * mm});
            skLineSegment(sketch, "E353", {"start": v(10.8, 16.32) * mm, "end": v(10.68, 16.42) * mm});
            skLineSegment(sketch, "E354", {"start": v(10.68, 16.42) * mm, "end": v(10.55, 16.5) * mm});
            skLineSegment(sketch, "E355", {"start": v(10.55, 16.5) * mm, "end": v(10.53, 16.53) * mm});
            skLineSegment(sketch, "E356", {"start": v(10.53, 16.53) * mm, "end": v(10.61, 16.66) * mm});
            skLineSegment(sketch, "E357", {"start": v(10.61, 16.66) * mm, "end": v(10.7, 16.78) * mm});
            skLineSegment(sketch, "E358", {"start": v(10.7, 16.78) * mm, "end": v(10.79, 16.9) * mm});
            skLineSegment(sketch, "E359", {"start": v(10.79, 16.9) * mm, "end": v(10.87, 17.04) * mm});
            skLineSegment(sketch, "E360", {"start": v(10.87, 17.04) * mm, "end": v(10.96, 17.16) * mm});
            skLineSegment(sketch, "E361", {"start": v(10.96, 17.16) * mm, "end": v(11.05, 17.3) * mm});
            skLineSegment(sketch, "E362", {"start": v(11.05, 17.3) * mm, "end": v(11.13, 17.42) * mm});
            skLineSegment(sketch, "E363", {"start": v(11.13, 17.42) * mm, "end": v(11.22, 17.54) * mm});
            skLineSegment(sketch, "E364", {"start": v(11.22, 17.54) * mm, "end": v(11.3, 17.67) * mm});
            skLineSegment(sketch, "E365", {"start": v(11.3, 17.67) * mm, "end": v(11.4, 17.8) * mm});
            skLineSegment(sketch, "E366", {"start": v(11.4, 17.8) * mm, "end": v(11.48, 17.92) * mm});
            skLineSegment(sketch, "E367", {"start": v(11.48, 17.92) * mm, "end": v(11.57, 18.05) * mm});
            skLineSegment(sketch, "E368", {"start": v(11.57, 18.05) * mm, "end": v(11.66, 18.19) * mm});
            skLineSegment(sketch, "E369", {"start": v(11.66, 18.19) * mm, "end": v(11.72, 18.34) * mm});
            skLineSegment(sketch, "E370", {"start": v(11.72, 18.34) * mm, "end": v(11.75, 18.5) * mm});
            skLineSegment(sketch, "E371", {"start": v(11.75, 18.5) * mm, "end": v(11.72, 18.67) * mm});
            skLineSegment(sketch, "E372", {"start": v(11.72, 18.67) * mm, "end": v(11.66, 18.82) * mm});
            skLineSegment(sketch, "E373", {"start": v(11.66, 18.82) * mm, "end": v(11.56, 18.95) * mm});
            skLineSegment(sketch, "E374", {"start": v(11.56, 18.95) * mm, "end": v(11.46, 19.03) * mm});
            skLineSegment(sketch, "E375", {"start": v(11.46, 19.03) * mm, "end": v(11.3, 19.1) * mm});
            skLineSegment(sketch, "E376", {"start": v(11.3, 19.1) * mm, "end": v(11.15, 19.13) * mm});
            skLineSegment(sketch, "E377", {"start": v(11.15, 19.13) * mm, "end": v(11.11, 19.13) * mm});
            skLineSegment(sketch, "E378", {"start": v(11.11, 19.13) * mm, "end": v(10.95, 19.1) * mm});
            skLineSegment(sketch, "E379", {"start": v(10.95, 19.1) * mm, "end": v(10.8, 19.04) * mm});
            skLineSegment(sketch, "E380", {"start": v(10.8, 19.04) * mm, "end": v(10.67, 18.94) * mm});
            skLineSegment(sketch, "E381", {"start": v(10.67, 18.94) * mm, "end": v(10.59, 18.84) * mm});
            skLineSegment(sketch, "E382", {"start": v(10.59, 18.84) * mm, "end": v(10.51, 18.7) * mm});
            skLineSegment(sketch, "E383", {"start": v(10.51, 18.7) * mm, "end": v(10.43, 18.58) * mm});
            skLineSegment(sketch, "E384", {"start": v(10.43, 18.58) * mm, "end": v(10.35, 18.44) * mm});
            skLineSegment(sketch, "E385", {"start": v(10.35, 18.44) * mm, "end": v(10.27, 18.31) * mm});
            skLineSegment(sketch, "E386", {"start": v(10.27, 18.31) * mm, "end": v(10.2, 18.18) * mm});
            skLineSegment(sketch, "E387", {"start": v(10.2, 18.18) * mm, "end": v(10.11, 18.05) * mm});
            skLineSegment(sketch, "E388", {"start": v(10.11, 18.05) * mm, "end": v(10.03, 17.92) * mm});
            skLineSegment(sketch, "E389", {"start": v(10.03, 17.92) * mm, "end": v(9.95, 17.79) * mm});
            skLineSegment(sketch, "E390", {"start": v(9.95, 17.79) * mm, "end": v(9.87, 17.65) * mm});
            skLineSegment(sketch, "E391", {"start": v(9.87, 17.65) * mm, "end": v(9.8, 17.52) * mm});
            skLineSegment(sketch, "E392", {"start": v(9.8, 17.52) * mm, "end": v(9.72, 17.39) * mm});
            skLineSegment(sketch, "E393", {"start": v(9.72, 17.39) * mm, "end": v(9.64, 17.26) * mm});
            skLineSegment(sketch, "E394", {"start": v(9.64, 17.26) * mm, "end": v(9.57, 17.14) * mm});
            skLineSegment(sketch, "E395", {"start": v(9.57, 17.14) * mm, "end": v(9.43, 17.22) * mm});
            skLineSegment(sketch, "E396", {"start": v(9.43, 17.22) * mm, "end": v(9.3, 17.3) * mm});
            skLineSegment(sketch, "E397", {"start": v(9.3, 17.3) * mm, "end": v(9.16, 17.36) * mm});
            skLineSegment(sketch, "E398", {"start": v(9.16, 17.36) * mm, "end": v(9.03, 17.44) * mm});
            skLineSegment(sketch, "E399", {"start": v(9.03, 17.44) * mm, "end": v(8.9, 17.51) * mm});
            skLineSegment(sketch, "E400", {"start": v(8.9, 17.51) * mm, "end": v(8.76, 17.58) * mm});
            skLineSegment(sketch, "E401", {"start": v(8.76, 17.58) * mm, "end": v(8.63, 17.66) * mm});
            skLineSegment(sketch, "E402", {"start": v(8.63, 17.66) * mm, "end": v(8.5, 17.73) * mm});
            skLineSegment(sketch, "E403", {"start": v(8.5, 17.73) * mm, "end": v(8.36, 17.8) * mm});
            skLineSegment(sketch, "E404", {"start": v(8.36, 17.8) * mm, "end": v(8.22, 17.88) * mm});
            skLineSegment(sketch, "E405", {"start": v(8.22, 17.88) * mm, "end": v(8.09, 17.95) * mm});
            skLineSegment(sketch, "E406", {"start": v(8.09, 17.95) * mm, "end": v(8.06, 17.97) * mm});
            skLineSegment(sketch, "E407", {"start": v(8.06, 17.97) * mm, "end": v(8.13, 18.1) * mm});
            skLineSegment(sketch, "E408", {"start": v(8.13, 18.1) * mm, "end": v(8.2, 18.24) * mm});
            skLineSegment(sketch, "E409", {"start": v(8.2, 18.24) * mm, "end": v(8.26, 18.38) * mm});
            skLineSegment(sketch, "E410", {"start": v(8.26, 18.38) * mm, "end": v(8.33, 18.52) * mm});
            skLineSegment(sketch, "E411", {"start": v(8.33, 18.52) * mm, "end": v(8.4, 18.66) * mm});
            skLineSegment(sketch, "E412", {"start": v(8.4, 18.66) * mm, "end": v(8.46, 18.8) * mm});
            skLineSegment(sketch, "E413", {"start": v(8.46, 18.8) * mm, "end": v(8.53, 18.93) * mm});
            skLineSegment(sketch, "E414", {"start": v(8.53, 18.93) * mm, "end": v(8.6, 19.07) * mm});
            skLineSegment(sketch, "E415", {"start": v(8.6, 19.07) * mm, "end": v(8.67, 19.21) * mm});
            skLineSegment(sketch, "E416", {"start": v(8.67, 19.21) * mm, "end": v(8.74, 19.35) * mm});
            skLineSegment(sketch, "E417", {"start": v(8.74, 19.35) * mm, "end": v(8.8, 19.49) * mm});
            skLineSegment(sketch, "E418", {"start": v(8.8, 19.49) * mm, "end": v(8.87, 19.63) * mm});
            skLineSegment(sketch, "E419", {"start": v(8.87, 19.63) * mm, "end": v(8.94, 19.77) * mm});
            skLineSegment(sketch, "E420", {"start": v(8.94, 19.77) * mm, "end": v(8.99, 19.93) * mm});
            skLineSegment(sketch, "E421", {"start": v(8.99, 19.93) * mm, "end": v(8.98, 20.1) * mm});
            skLineSegment(sketch, "E422", {"start": v(8.98, 20.1) * mm, "end": v(8.94, 20.26) * mm});
            skLineSegment(sketch, "E423", {"start": v(8.94, 20.26) * mm, "end": v(8.86, 20.4) * mm});
            skLineSegment(sketch, "E424", {"start": v(8.86, 20.4) * mm, "end": v(8.74, 20.51) * mm});
            skLineSegment(sketch, "E425", {"start": v(8.74, 20.51) * mm, "end": v(8.62, 20.58) * mm});
            skLineSegment(sketch, "E426", {"start": v(8.62, 20.58) * mm, "end": v(8.47, 20.63) * mm});
            skLineSegment(sketch, "E427", {"start": v(8.47, 20.63) * mm, "end": v(8.37, 20.64) * mm});
            skLineSegment(sketch, "E428", {"start": v(8.37, 20.64) * mm, "end": v(8.2, 20.62) * mm});
            skLineSegment(sketch, "E429", {"start": v(8.2, 20.62) * mm, "end": v(8.05, 20.55) * mm});
            skLineSegment(sketch, "E430", {"start": v(8.05, 20.55) * mm, "end": v(7.92, 20.45) * mm});
            skLineSegment(sketch, "E431", {"start": v(7.92, 20.45) * mm, "end": v(7.82, 20.32) * mm});
            skLineSegment(sketch, "E432", {"start": v(7.82, 20.32) * mm, "end": v(7.8, 20.26) * mm});
            skLineSegment(sketch, "E433", {"start": v(7.8, 20.26) * mm, "end": v(7.73, 20.12) * mm});
            skLineSegment(sketch, "E434", {"start": v(7.73, 20.12) * mm, "end": v(7.67, 19.98) * mm});
            skLineSegment(sketch, "E435", {"start": v(7.67, 19.98) * mm, "end": v(7.61, 19.84) * mm});
            skLineSegment(sketch, "E436", {"start": v(7.61, 19.84) * mm, "end": v(7.55, 19.7) * mm});
            skLineSegment(sketch, "E437", {"start": v(7.55, 19.7) * mm, "end": v(7.5, 19.56) * mm});
            skLineSegment(sketch, "E438", {"start": v(7.5, 19.56) * mm, "end": v(7.43, 19.41) * mm});
            skLineSegment(sketch, "E439", {"start": v(7.43, 19.41) * mm, "end": v(7.37, 19.27) * mm});
            skLineSegment(sketch, "E440", {"start": v(7.37, 19.27) * mm, "end": v(7.31, 19.13) * mm});
            skLineSegment(sketch, "E441", {"start": v(7.31, 19.13) * mm, "end": v(7.25, 18.99) * mm});
            skLineSegment(sketch, "E442", {"start": v(7.25, 18.99) * mm, "end": v(7.2, 18.85) * mm});
            skLineSegment(sketch, "E443", {"start": v(7.2, 18.85) * mm, "end": v(7.13, 18.7) * mm});
            skLineSegment(sketch, "E444", {"start": v(7.13, 18.7) * mm, "end": v(7.07, 18.56) * mm});
            skLineSegment(sketch, "E445", {"start": v(7.07, 18.56) * mm, "end": v(7.02, 18.44) * mm});
            skLineSegment(sketch, "E446", {"start": v(7.02, 18.44) * mm, "end": v(6.88, 18.5) * mm});
            skLineSegment(sketch, "E447", {"start": v(6.88, 18.5) * mm, "end": v(6.74, 18.55) * mm});
            skLineSegment(sketch, "E448", {"start": v(6.74, 18.55) * mm, "end": v(6.6, 18.6) * mm});
            skLineSegment(sketch, "E449", {"start": v(6.6, 18.6) * mm, "end": v(6.45, 18.66) * mm});
            skLineSegment(sketch, "E450", {"start": v(6.45, 18.66) * mm, "end": v(6.3, 18.7) * mm});
            skLineSegment(sketch, "E451", {"start": v(6.3, 18.7) * mm, "end": v(6.16, 18.76) * mm});
            skLineSegment(sketch, "E452", {"start": v(6.16, 18.76) * mm, "end": v(6.02, 18.82) * mm});
            skLineSegment(sketch, "E453", {"start": v(6.02, 18.82) * mm, "end": v(5.87, 18.87) * mm});
            skLineSegment(sketch, "E454", {"start": v(5.87, 18.87) * mm, "end": v(5.73, 18.92) * mm});
            skLineSegment(sketch, "E455", {"start": v(5.73, 18.92) * mm, "end": v(5.59, 18.98) * mm});
            skLineSegment(sketch, "E456", {"start": v(5.59, 18.98) * mm, "end": v(5.44, 19.03) * mm});
            skLineSegment(sketch, "E457", {"start": v(5.44, 19.03) * mm, "end": v(5.41, 19.04) * mm});
            skLineSegment(sketch, "E458", {"start": v(5.41, 19.04) * mm, "end": v(5.46, 19.19) * mm});
            skLineSegment(sketch, "E459", {"start": v(5.46, 19.19) * mm, "end": v(5.5, 19.33) * mm});
            skLineSegment(sketch, "E460", {"start": v(5.5, 19.33) * mm, "end": v(5.55, 19.48) * mm});
            skLineSegment(sketch, "E461", {"start": v(5.55, 19.48) * mm, "end": v(5.6, 19.63) * mm});
            skLineSegment(sketch, "E462", {"start": v(5.6, 19.63) * mm, "end": v(5.65, 19.77) * mm});
            skLineSegment(sketch, "E463", {"start": v(5.65, 19.77) * mm, "end": v(5.7, 19.92) * mm});
            skLineSegment(sketch, "E464", {"start": v(5.7, 19.92) * mm, "end": v(5.74, 20.07) * mm});
            skLineSegment(sketch, "E465", {"start": v(5.74, 20.07) * mm, "end": v(5.8, 20.21) * mm});
            skLineSegment(sketch, "E466", {"start": v(5.8, 20.21) * mm, "end": v(5.84, 20.36) * mm});
            skLineSegment(sketch, "E467", {"start": v(5.84, 20.36) * mm, "end": v(5.89, 20.5) * mm});
            skLineSegment(sketch, "E468", {"start": v(5.89, 20.5) * mm, "end": v(5.93, 20.65) * mm});
            skLineSegment(sketch, "E469", {"start": v(5.93, 20.65) * mm, "end": v(5.98, 20.8) * mm});
            skLineSegment(sketch, "E470", {"start": v(5.98, 20.8) * mm, "end": v(6.03, 20.96) * mm});
            skLineSegment(sketch, "E471", {"start": v(6.03, 20.96) * mm, "end": v(6.05, 21.12) * mm});
            skLineSegment(sketch, "E472", {"start": v(6.05, 21.12) * mm, "end": v(6.02, 21.28) * mm});
            skLineSegment(sketch, "E473", {"start": v(6.02, 21.28) * mm, "end": v(5.96, 21.43) * mm});
            skLineSegment(sketch, "E474", {"start": v(5.96, 21.43) * mm, "end": v(5.86, 21.56) * mm});
            skLineSegment(sketch, "E475", {"start": v(5.86, 21.56) * mm, "end": v(5.72, 21.66) * mm});
            skLineSegment(sketch, "E476", {"start": v(5.72, 21.66) * mm, "end": v(5.6, 21.7) * mm});
            skLineSegment(sketch, "E477", {"start": v(5.6, 21.7) * mm, "end": v(5.44, 21.73) * mm});
            skLineSegment(sketch, "E478", {"start": v(5.44, 21.73) * mm, "end": v(5.27, 21.72) * mm});
            skLineSegment(sketch, "E479", {"start": v(5.27, 21.72) * mm, "end": v(5.12, 21.65) * mm});
            skLineSegment(sketch, "E480", {"start": v(5.12, 21.65) * mm, "end": v(4.99, 21.56) * mm});
            skLineSegment(sketch, "E481", {"start": v(4.99, 21.56) * mm, "end": v(4.89, 21.43) * mm});
            skLineSegment(sketch, "E482", {"start": v(4.89, 21.43) * mm, "end": v(4.82, 21.28) * mm});
            skLineSegment(sketch, "E483", {"start": v(4.82, 21.28) * mm, "end": v(4.78, 21.13) * mm});
            skLineSegment(sketch, "E484", {"start": v(4.78, 21.13) * mm, "end": v(4.74, 20.98) * mm});
            skLineSegment(sketch, "E485", {"start": v(4.74, 20.98) * mm, "end": v(4.7, 20.83) * mm});
            skLineSegment(sketch, "E486", {"start": v(4.7, 20.83) * mm, "end": v(4.67, 20.68) * mm});
            skLineSegment(sketch, "E487", {"start": v(4.67, 20.68) * mm, "end": v(4.63, 20.53) * mm});
            skLineSegment(sketch, "E488", {"start": v(4.63, 20.53) * mm, "end": v(4.59, 20.38) * mm});
            skLineSegment(sketch, "E489", {"start": v(4.59, 20.38) * mm, "end": v(4.55, 20.24) * mm});
            skLineSegment(sketch, "E490", {"start": v(4.55, 20.24) * mm, "end": v(4.5, 20.09) * mm});
            skLineSegment(sketch, "E491", {"start": v(4.5, 20.09) * mm, "end": v(4.47, 19.94) * mm});
            skLineSegment(sketch, "E492", {"start": v(4.47, 19.94) * mm, "end": v(4.43, 19.79) * mm});
            skLineSegment(sketch, "E493", {"start": v(4.43, 19.79) * mm, "end": v(4.4, 19.64) * mm});
            skLineSegment(sketch, "E494", {"start": v(4.4, 19.64) * mm, "end": v(4.35, 19.5) * mm});
            skLineSegment(sketch, "E495", {"start": v(4.35, 19.5) * mm, "end": v(4.32, 19.36) * mm});
            skLineSegment(sketch, "E496", {"start": v(4.32, 19.36) * mm, "end": v(4.17, 19.4) * mm});
            skLineSegment(sketch, "E497", {"start": v(4.17, 19.4) * mm, "end": v(4.02, 19.43) * mm});
            skLineSegment(sketch, "E498", {"start": v(4.02, 19.43) * mm, "end": v(3.87, 19.46) * mm});
            skLineSegment(sketch, "E499", {"start": v(3.87, 19.46) * mm, "end": v(3.72, 19.5) * mm});
            skLineSegment(sketch, "E500", {"start": v(3.72, 19.5) * mm, "end": v(3.57, 19.53) * mm});
            skLineSegment(sketch, "E501", {"start": v(3.57, 19.53) * mm, "end": v(3.42, 19.56) * mm});
            skLineSegment(sketch, "E502", {"start": v(3.42, 19.56) * mm, "end": v(3.27, 19.6) * mm});
            skLineSegment(sketch, "E503", {"start": v(3.27, 19.6) * mm, "end": v(3.12, 19.62) * mm});
            skLineSegment(sketch, "E504", {"start": v(3.12, 19.62) * mm, "end": v(2.97, 19.66) * mm});
            skLineSegment(sketch, "E505", {"start": v(2.97, 19.66) * mm, "end": v(2.82, 19.69) * mm});
            skLineSegment(sketch, "E506", {"start": v(2.82, 19.69) * mm, "end": v(2.67, 19.72) * mm});
            skLineSegment(sketch, "E507", {"start": v(2.67, 19.72) * mm, "end": v(2.64, 19.73) * mm});
            skLineSegment(sketch, "E508", {"start": v(2.64, 19.73) * mm, "end": v(2.66, 19.88) * mm});
            skLineSegment(sketch, "E509", {"start": v(2.66, 19.88) * mm, "end": v(2.69, 20.03) * mm});
            skLineSegment(sketch, "E510", {"start": v(2.69, 20.03) * mm, "end": v(2.72, 20.18) * mm});
            skLineSegment(sketch, "E511", {"start": v(2.72, 20.18) * mm, "end": v(2.74, 20.33) * mm});
            skLineSegment(sketch, "E512", {"start": v(2.74, 20.33) * mm, "end": v(2.77, 20.49) * mm});
            skLineSegment(sketch, "E513", {"start": v(2.77, 20.49) * mm, "end": v(2.8, 20.64) * mm});
            skLineSegment(sketch, "E514", {"start": v(2.8, 20.64) * mm, "end": v(2.82, 20.79) * mm});
            skLineSegment(sketch, "E515", {"start": v(2.82, 20.79) * mm, "end": v(2.85, 20.94) * mm});
            skLineSegment(sketch, "E516", {"start": v(2.85, 20.94) * mm, "end": v(2.87, 21.1) * mm});
            skLineSegment(sketch, "E517", {"start": v(2.87, 21.1) * mm, "end": v(2.9, 21.24) * mm});
            skLineSegment(sketch, "E518", {"start": v(2.9, 21.24) * mm, "end": v(2.93, 21.4) * mm});
            skLineSegment(sketch, "E519", {"start": v(2.93, 21.4) * mm, "end": v(2.95, 21.55) * mm});
            skLineSegment(sketch, "E520", {"start": v(2.95, 21.55) * mm, "end": v(2.98, 21.71) * mm});
            skLineSegment(sketch, "E521", {"start": v(2.98, 21.71) * mm, "end": v(2.97, 21.88) * mm});
            skLineSegment(sketch, "E522", {"start": v(2.97, 21.88) * mm, "end": v(2.93, 22.03) * mm});
            skLineSegment(sketch, "E523", {"start": v(2.93, 22.03) * mm, "end": v(2.84, 22.17) * mm});
            skLineSegment(sketch, "E524", {"start": v(2.84, 22.17) * mm, "end": v(2.72, 22.29) * mm});
            skLineSegment(sketch, "E525", {"start": v(2.72, 22.29) * mm, "end": v(2.57, 22.36) * mm});
            skLineSegment(sketch, "E526", {"start": v(2.57, 22.36) * mm, "end": v(2.41, 22.4) * mm});
            skLineSegment(sketch, "E527", {"start": v(2.41, 22.4) * mm, "end": v(2.35, 22.4) * mm});
            skLineSegment(sketch, "E528", {"start": v(2.35, 22.4) * mm, "end": v(2.18, 22.38) * mm});
            skLineSegment(sketch, "E529", {"start": v(2.18, 22.38) * mm, "end": v(2.03, 22.31) * mm});
            skLineSegment(sketch, "E530", {"start": v(2.03, 22.31) * mm, "end": v(1.9, 22.2) * mm});
            skLineSegment(sketch, "E531", {"start": v(1.9, 22.2) * mm, "end": v(1.8, 22.07) * mm});
            skLineSegment(sketch, "E532", {"start": v(1.8, 22.07) * mm, "end": v(1.75, 21.92) * mm});
            skLineSegment(sketch, "E533", {"start": v(1.75, 21.92) * mm, "end": v(1.74, 21.86) * mm});
            skLineSegment(sketch, "E534", {"start": v(1.74, 21.86) * mm, "end": v(1.72, 21.7) * mm});
            skLineSegment(sketch, "E535", {"start": v(1.72, 21.7) * mm, "end": v(1.7, 21.55) * mm});
            skLineSegment(sketch, "E536", {"start": v(1.7, 21.55) * mm, "end": v(1.68, 21.4) * mm});
            skLineSegment(sketch, "E537", {"start": v(1.68, 21.4) * mm, "end": v(1.67, 21.25) * mm});
            skLineSegment(sketch, "E538", {"start": v(1.67, 21.25) * mm, "end": v(1.65, 21.1) * mm});
            skLineSegment(sketch, "E539", {"start": v(1.65, 21.1) * mm, "end": v(1.63, 20.94) * mm});
            skLineSegment(sketch, "E540", {"start": v(1.63, 20.94) * mm, "end": v(1.61, 20.79) * mm});
            skLineSegment(sketch, "E541", {"start": v(1.61, 20.79) * mm, "end": v(1.6, 20.63) * mm});
            skLineSegment(sketch, "E542", {"start": v(1.6, 20.63) * mm, "end": v(1.58, 20.48) * mm});
            skLineSegment(sketch, "E543", {"start": v(1.58, 20.48) * mm, "end": v(1.56, 20.33) * mm});
            skLineSegment(sketch, "E544", {"start": v(1.56, 20.33) * mm, "end": v(1.54, 20.18) * mm});
            skLineSegment(sketch, "E545", {"start": v(1.54, 20.18) * mm, "end": v(1.53, 20.02) * mm});
            skLineSegment(sketch, "E546", {"start": v(1.53, 20.02) * mm, "end": v(1.51, 19.9) * mm});
            skLineSegment(sketch, "E547", {"start": v(1.51, 19.9) * mm, "end": v(1.36, 19.9) * mm});
            skLineSegment(sketch, "E548", {"start": v(1.36, 19.9) * mm, "end": v(1.2, 19.91) * mm});
            skLineSegment(sketch, "E549", {"start": v(1.2, 19.91) * mm, "end": v(1.05, 19.92) * mm});
            skLineSegment(sketch, "E550", {"start": v(1.05, 19.92) * mm, "end": v(0.9, 19.93) * mm});
            skLineSegment(sketch, "E551", {"start": v(0.9, 19.93) * mm, "end": v(0.75, 19.95) * mm});
            skLineSegment(sketch, "E552", {"start": v(0.75, 19.95) * mm, "end": v(0.6, 19.96) * mm});
            skLineSegment(sketch, "E553", {"start": v(0.6, 19.96) * mm, "end": v(0.44, 19.97) * mm});
            skLineSegment(sketch, "E554", {"start": v(0.44, 19.97) * mm, "end": v(0.29, 19.98) * mm});
            skLineSegment(sketch, "E555", {"start": v(0.29, 19.98) * mm, "end": v(0.14, 19.99) * mm});
            skLineSegment(sketch, "E556", {"start": v(0.14, 19.99) * mm, "end": v(-0.02, 20) * mm});
            skLineSegment(sketch, "E557", {"start": v(-0.02, 20) * mm, "end": v(-0.17, 20.01) * mm});
            skLineSegment(sketch, "E558", {"start": v(-0.17, 20.01) * mm, "end": v(-0.2, 20.01) * mm});
            skLineSegment(sketch, "E559", {"start": v(-0.2, 20.01) * mm, "end": v(-0.2, 20.17) * mm});
            skLineSegment(sketch, "E560", {"start": v(-0.2, 20.17) * mm, "end": v(-0.2, 20.32) * mm});
            skLineSegment(sketch, "E561", {"start": v(-0.2, 20.32) * mm, "end": v(-0.2, 20.47) * mm});
            skLineSegment(sketch, "E562", {"start": v(-0.2, 20.47) * mm, "end": v(-0.19, 20.63) * mm});
            skLineSegment(sketch, "E563", {"start": v(-0.19, 20.63) * mm, "end": v(-0.18, 20.78) * mm});
            skLineSegment(sketch, "E564", {"start": v(-0.18, 20.78) * mm, "end": v(-0.18, 20.94) * mm});
            skLineSegment(sketch, "E565", {"start": v(-0.18, 20.94) * mm, "end": v(-0.17, 21.09) * mm});
            skLineSegment(sketch, "E566", {"start": v(-0.17, 21.09) * mm, "end": v(-0.17, 21.24) * mm});
            skLineSegment(sketch, "E567", {"start": v(-0.17, 21.24) * mm, "end": v(-0.17, 21.4) * mm});
            skLineSegment(sketch, "E568", {"start": v(-0.17, 21.4) * mm, "end": v(-0.16, 21.55) * mm});
            skLineSegment(sketch, "E569", {"start": v(-0.16, 21.55) * mm, "end": v(-0.16, 21.7) * mm});
            skLineSegment(sketch, "E570", {"start": v(-0.16, 21.7) * mm, "end": v(-0.15, 21.86) * mm});
            skLineSegment(sketch, "E571", {"start": v(-0.15, 21.86) * mm, "end": v(-0.15, 22.02) * mm});
            skLineSegment(sketch, "E572", {"start": v(-0.15, 22.02) * mm, "end": v(-0.18, 22.19) * mm});
            skLineSegment(sketch, "E573", {"start": v(-0.18, 22.19) * mm, "end": v(-0.25, 22.34) * mm});
            skLineSegment(sketch, "E574", {"start": v(-0.25, 22.34) * mm, "end": v(-0.35, 22.46) * mm});
            skLineSegment(sketch, "E575", {"start": v(-0.35, 22.46) * mm, "end": v(-0.49, 22.56) * mm});
            skLineSegment(sketch, "E576", {"start": v(-0.49, 22.56) * mm, "end": v(-0.64, 22.61) * mm});
            skLineSegment(sketch, "E577", {"start": v(-0.64, 22.61) * mm, "end": v(-0.77, 22.62) * mm});
            skLineSegment(sketch, "E578", {"start": v(-0.77, 22.62) * mm, "end": v(-0.94, 22.6) * mm});
            skLineSegment(sketch, "E579", {"start": v(-0.94, 22.6) * mm, "end": v(-1.09, 22.54) * mm});
            skLineSegment(sketch, "E580", {"start": v(-1.09, 22.54) * mm, "end": v(-1.22, 22.44) * mm});
            skLineSegment(sketch, "E581", {"start": v(-1.22, 22.44) * mm, "end": v(-1.32, 22.3) * mm});
            skLineSegment(sketch, "E582", {"start": v(-1.32, 22.3) * mm, "end": v(-1.38, 22.15) * mm});
            skLineSegment(sketch, "E583", {"start": v(-1.38, 22.15) * mm, "end": v(-1.4, 22) * mm});
            skLineSegment(sketch, "E584", {"start": v(-1.4, 22) * mm, "end": v(-1.4, 21.84) * mm});
            skLineSegment(sketch, "E585", {"start": v(-1.4, 21.84) * mm, "end": v(-1.4, 21.68) * mm});
            skLineSegment(sketch, "E586", {"start": v(-1.4, 21.68) * mm, "end": v(-1.39, 21.53) * mm});
            skLineSegment(sketch, "E587", {"start": v(-1.39, 21.53) * mm, "end": v(-1.38, 21.38) * mm});
            skLineSegment(sketch, "E588", {"start": v(-1.38, 21.38) * mm, "end": v(-1.38, 21.22) * mm});
            skLineSegment(sketch, "E589", {"start": v(-1.38, 21.22) * mm, "end": v(-1.37, 21.07) * mm});
            skLineSegment(sketch, "E590", {"start": v(-1.37, 21.07) * mm, "end": v(-1.37, 20.91) * mm});
            skLineSegment(sketch, "E591", {"start": v(-1.37, 20.91) * mm, "end": v(-1.36, 20.76) * mm});
            skLineSegment(sketch, "E592", {"start": v(-1.36, 20.76) * mm, "end": v(-1.36, 20.6) * mm});
            skLineSegment(sketch, "E593", {"start": v(-1.36, 20.6) * mm, "end": v(-1.36, 20.45) * mm});
            skLineSegment(sketch, "E594", {"start": v(-1.36, 20.45) * mm, "end": v(-1.35, 20.3) * mm});
            skLineSegment(sketch, "E595", {"start": v(-1.35, 20.3) * mm, "end": v(-1.35, 20.15) * mm});
            skLineSegment(sketch, "E596", {"start": v(-1.35, 20.15) * mm, "end": v(-1.34, 20.01) * mm});
            skLineSegment(sketch, "E597", {"start": v(-1.34, 20.01) * mm, "end": v(-1.5, 20) * mm});
            skLineSegment(sketch, "E598", {"start": v(-1.5, 20) * mm, "end": v(-1.65, 20) * mm});
            skLineSegment(sketch, "E599", {"start": v(-1.65, 20) * mm, "end": v(-1.8, 19.98) * mm});
            skLineSegment(sketch, "E600", {"start": v(-1.8, 19.98) * mm, "end": v(-1.95, 19.97) * mm});
            skLineSegment(sketch, "E601", {"start": v(-1.95, 19.97) * mm, "end": v(-2.1, 19.96) * mm});
            skLineSegment(sketch, "E602", {"start": v(-2.1, 19.96) * mm, "end": v(-2.26, 19.95) * mm});
            skLineSegment(sketch, "E603", {"start": v(-2.26, 19.95) * mm, "end": v(-2.41, 19.94) * mm});
            skLineSegment(sketch, "E604", {"start": v(-2.41, 19.94) * mm, "end": v(-2.57, 19.93) * mm});
            skLineSegment(sketch, "E605", {"start": v(-2.57, 19.93) * mm, "end": v(-2.72, 19.92) * mm});
            skLineSegment(sketch, "E606", {"start": v(-2.72, 19.92) * mm, "end": v(-2.87, 19.9) * mm});
            skLineSegment(sketch, "E607", {"start": v(-2.87, 19.9) * mm, "end": v(-3.02, 19.9) * mm});
            skLineSegment(sketch, "E608", {"start": v(-3.02, 19.9) * mm, "end": v(-3.06, 19.9) * mm});
            skLineSegment(sketch, "E609", {"start": v(-3.06, 19.9) * mm, "end": v(-3.08, 20.04) * mm});
            skLineSegment(sketch, "E610", {"start": v(-3.08, 20.04) * mm, "end": v(-3.1, 20.2) * mm});
            skLineSegment(sketch, "E611", {"start": v(-3.1, 20.2) * mm, "end": v(-3.11, 20.35) * mm});
            skLineSegment(sketch, "E612", {"start": v(-3.11, 20.35) * mm, "end": v(-3.13, 20.5) * mm});
            skLineSegment(sketch, "E613", {"start": v(-3.13, 20.5) * mm, "end": v(-3.15, 20.65) * mm});
            skLineSegment(sketch, "E614", {"start": v(-3.15, 20.65) * mm, "end": v(-3.16, 20.8) * mm});
            skLineSegment(sketch, "E615", {"start": v(-3.16, 20.8) * mm, "end": v(-3.18, 20.96) * mm});
            skLineSegment(sketch, "E616", {"start": v(-3.18, 20.96) * mm, "end": v(-3.2, 21.11) * mm});
            skLineSegment(sketch, "E617", {"start": v(-3.2, 21.11) * mm, "end": v(-3.22, 21.27) * mm});
            skLineSegment(sketch, "E618", {"start": v(-3.22, 21.27) * mm, "end": v(-3.23, 21.42) * mm});
            skLineSegment(sketch, "E619", {"start": v(-3.23, 21.42) * mm, "end": v(-3.25, 21.57) * mm});
            skLineSegment(sketch, "E620", {"start": v(-3.25, 21.57) * mm, "end": v(-3.27, 21.72) * mm});
            skLineSegment(sketch, "E621", {"start": v(-3.27, 21.72) * mm, "end": v(-3.29, 21.89) * mm});
            skLineSegment(sketch, "E622", {"start": v(-3.29, 21.89) * mm, "end": v(-3.34, 22.05) * mm});
            skLineSegment(sketch, "E623", {"start": v(-3.34, 22.05) * mm, "end": v(-3.43, 22.18) * mm});
            skLineSegment(sketch, "E624", {"start": v(-3.43, 22.18) * mm, "end": v(-3.55, 22.3) * mm});
            skLineSegment(sketch, "E625", {"start": v(-3.55, 22.3) * mm, "end": v(-3.7, 22.37) * mm});
            skLineSegment(sketch, "E626", {"start": v(-3.7, 22.37) * mm, "end": v(-3.86, 22.4) * mm});
            skLineSegment(sketch, "E627", {"start": v(-3.86, 22.4) * mm, "end": v(-3.9, 22.4) * mm});
            skLineSegment(sketch, "E628", {"start": v(-3.9, 22.4) * mm, "end": v(-4, 22.4) * mm});
            skLineSegment(sketch, "E629", {"start": v(-4, 22.4) * mm, "end": v(-4.15, 22.35) * mm});
            skLineSegment(sketch, "E630", {"start": v(-4.15, 22.35) * mm, "end": v(-4.3, 22.27) * mm});
            skLineSegment(sketch, "E631", {"start": v(-4.3, 22.27) * mm, "end": v(-4.4, 22.15) * mm});
            skLineSegment(sketch, "E632", {"start": v(-4.4, 22.15) * mm, "end": v(-4.49, 22) * mm});
            skLineSegment(sketch, "E633", {"start": v(-4.49, 22) * mm, "end": v(-4.53, 21.84) * mm});
            skLineSegment(sketch, "E634", {"start": v(-4.53, 21.84) * mm, "end": v(-4.52, 21.68) * mm});
            skLineSegment(sketch, "E635", {"start": v(-4.52, 21.68) * mm, "end": v(-4.5, 21.53) * mm});
            skLineSegment(sketch, "E636", {"start": v(-4.5, 21.53) * mm, "end": v(-4.47, 21.38) * mm});
            skLineSegment(sketch, "E637", {"start": v(-4.47, 21.38) * mm, "end": v(-4.44, 21.22) * mm});
            skLineSegment(sketch, "E638", {"start": v(-4.44, 21.22) * mm, "end": v(-4.42, 21.07) * mm});
            skLineSegment(sketch, "E639", {"start": v(-4.42, 21.07) * mm, "end": v(-4.4, 20.92) * mm});
            skLineSegment(sketch, "E640", {"start": v(-4.4, 20.92) * mm, "end": v(-4.37, 20.77) * mm});
            skLineSegment(sketch, "E641", {"start": v(-4.37, 20.77) * mm, "end": v(-4.34, 20.62) * mm});
            skLineSegment(sketch, "E642", {"start": v(-4.34, 20.62) * mm, "end": v(-4.31, 20.47) * mm});
            skLineSegment(sketch, "E643", {"start": v(-4.31, 20.47) * mm, "end": v(-4.29, 20.31) * mm});
            skLineSegment(sketch, "E644", {"start": v(-4.29, 20.31) * mm, "end": v(-4.26, 20.16) * mm});
            skLineSegment(sketch, "E645", {"start": v(-4.26, 20.16) * mm, "end": v(-4.23, 20.01) * mm});
            skLineSegment(sketch, "E646", {"start": v(-4.23, 20.01) * mm, "end": v(-4.2, 19.86) * mm});
            skLineSegment(sketch, "E647", {"start": v(-4.2, 19.86) * mm, "end": v(-4.19, 19.73) * mm});
            skLineSegment(sketch, "E648", {"start": v(-4.19, 19.73) * mm, "end": v(-4.34, 19.7) * mm});
            skLineSegment(sketch, "E649", {"start": v(-4.34, 19.7) * mm, "end": v(-4.48, 19.66) * mm});
            skLineSegment(sketch, "E650", {"start": v(-4.48, 19.66) * mm, "end": v(-4.63, 19.63) * mm});
            skLineSegment(sketch, "E651", {"start": v(-4.63, 19.63) * mm, "end": v(-4.78, 19.6) * mm});
            skLineSegment(sketch, "E652", {"start": v(-4.78, 19.6) * mm, "end": v(-4.93, 19.57) * mm});
            skLineSegment(sketch, "E653", {"start": v(-4.93, 19.57) * mm, "end": v(-5.08, 19.53) * mm});
            skLineSegment(sketch, "E654", {"start": v(-5.08, 19.53) * mm, "end": v(-5.23, 19.5) * mm});
            skLineSegment(sketch, "E655", {"start": v(-5.23, 19.5) * mm, "end": v(-5.38, 19.47) * mm});
            skLineSegment(sketch, "E656", {"start": v(-5.38, 19.47) * mm, "end": v(-5.53, 19.44) * mm});
            skLineSegment(sketch, "E657", {"start": v(-5.53, 19.44) * mm, "end": v(-5.68, 19.4) * mm});
            skLineSegment(sketch, "E658", {"start": v(-5.68, 19.4) * mm, "end": v(-5.83, 19.37) * mm});
            skLineSegment(sketch, "E659", {"start": v(-5.83, 19.37) * mm, "end": v(-5.87, 19.36) * mm});
            skLineSegment(sketch, "E660", {"start": v(-5.87, 19.36) * mm, "end": v(-5.9, 19.51) * mm});
            skLineSegment(sketch, "E661", {"start": v(-5.9, 19.51) * mm, "end": v(-5.94, 19.66) * mm});
            skLineSegment(sketch, "E662", {"start": v(-5.94, 19.66) * mm, "end": v(-5.98, 19.8) * mm});
            skLineSegment(sketch, "E663", {"start": v(-5.98, 19.8) * mm, "end": v(-6.02, 19.96) * mm});
            skLineSegment(sketch, "E664", {"start": v(-6.02, 19.96) * mm, "end": v(-6.06, 20.1) * mm});
            skLineSegment(sketch, "E665", {"start": v(-6.06, 20.1) * mm, "end": v(-6.1, 20.26) * mm});
            skLineSegment(sketch, "E666", {"start": v(-6.1, 20.26) * mm, "end": v(-6.14, 20.4) * mm});
            skLineSegment(sketch, "E667", {"start": v(-6.14, 20.4) * mm, "end": v(-6.18, 20.55) * mm});
            skLineSegment(sketch, "E668", {"start": v(-6.18, 20.55) * mm, "end": v(-6.22, 20.7) * mm});
            skLineSegment(sketch, "E669", {"start": v(-6.22, 20.7) * mm, "end": v(-6.26, 20.85) * mm});
            skLineSegment(sketch, "E670", {"start": v(-6.26, 20.85) * mm, "end": v(-6.3, 21) * mm});
            skLineSegment(sketch, "E671", {"start": v(-6.3, 21) * mm, "end": v(-6.34, 21.15) * mm});
            skLineSegment(sketch, "E672", {"start": v(-6.34, 21.15) * mm, "end": v(-6.38, 21.3) * mm});
            skLineSegment(sketch, "E673", {"start": v(-6.38, 21.3) * mm, "end": v(-6.45, 21.46) * mm});
            skLineSegment(sketch, "E674", {"start": v(-6.45, 21.46) * mm, "end": v(-6.56, 21.58) * mm});
            skLineSegment(sketch, "E675", {"start": v(-6.56, 21.58) * mm, "end": v(-6.7, 21.67) * mm});
            skLineSegment(sketch, "E676", {"start": v(-6.7, 21.67) * mm, "end": v(-6.85, 21.72) * mm});
            skLineSegment(sketch, "E677", {"start": v(-6.85, 21.72) * mm, "end": v(-6.99, 21.73) * mm});
            skLineSegment(sketch, "E678", {"start": v(-6.99, 21.73) * mm, "end": v(-7.15, 21.7) * mm});
            skLineSegment(sketch, "E679", {"start": v(-7.15, 21.7) * mm, "end": v(-7.3, 21.64) * mm});
            skLineSegment(sketch, "E680", {"start": v(-7.3, 21.64) * mm, "end": v(-7.43, 21.54) * mm});
            skLineSegment(sketch, "E681", {"start": v(-7.43, 21.54) * mm, "end": v(-7.52, 21.4) * mm});
            skLineSegment(sketch, "E682", {"start": v(-7.52, 21.4) * mm, "end": v(-7.58, 21.25) * mm});
            skLineSegment(sketch, "E683", {"start": v(-7.58, 21.25) * mm, "end": v(-7.6, 21.09) * mm});
            skLineSegment(sketch, "E684", {"start": v(-7.6, 21.09) * mm, "end": v(-7.57, 20.92) * mm});
            skLineSegment(sketch, "E685", {"start": v(-7.57, 20.92) * mm, "end": v(-7.52, 20.78) * mm});
            skLineSegment(sketch, "E686", {"start": v(-7.52, 20.78) * mm, "end": v(-7.47, 20.63) * mm});
            skLineSegment(sketch, "E687", {"start": v(-7.47, 20.63) * mm, "end": v(-7.43, 20.48) * mm});
            skLineSegment(sketch, "E688", {"start": v(-7.43, 20.48) * mm, "end": v(-7.38, 20.34) * mm});
            skLineSegment(sketch, "E689", {"start": v(-7.38, 20.34) * mm, "end": v(-7.33, 20.2) * mm});
            skLineSegment(sketch, "E690", {"start": v(-7.33, 20.2) * mm, "end": v(-7.28, 20.05) * mm});
            skLineSegment(sketch, "E691", {"start": v(-7.28, 20.05) * mm, "end": v(-7.24, 19.9) * mm});
            skLineSegment(sketch, "E692", {"start": v(-7.24, 19.9) * mm, "end": v(-7.19, 19.75) * mm});
            skLineSegment(sketch, "E693", {"start": v(-7.19, 19.75) * mm, "end": v(-7.14, 19.6) * mm});
            skLineSegment(sketch, "E694", {"start": v(-7.14, 19.6) * mm, "end": v(-7.1, 19.46) * mm});
            skLineSegment(sketch, "E695", {"start": v(-7.1, 19.46) * mm, "end": v(-7.05, 19.32) * mm});
            skLineSegment(sketch, "E696", {"start": v(-7.05, 19.32) * mm, "end": v(-7, 19.17) * mm});
            skLineSegment(sketch, "E697", {"start": v(-7, 19.17) * mm, "end": v(-6.96, 19.04) * mm});
            skLineSegment(sketch, "E698", {"start": v(-6.96, 19.04) * mm, "end": v(-7.1, 18.99) * mm});
            skLineSegment(sketch, "E699", {"start": v(-7.1, 18.99) * mm, "end": v(-7.25, 18.94) * mm});
            skLineSegment(sketch, "E700", {"start": v(-7.25, 18.94) * mm, "end": v(-7.39, 18.88) * mm});
            skLineSegment(sketch, "E701", {"start": v(-7.39, 18.88) * mm, "end": v(-7.53, 18.83) * mm});
            skLineSegment(sketch, "E702", {"start": v(-7.53, 18.83) * mm, "end": v(-7.68, 18.78) * mm});
            skLineSegment(sketch, "E703", {"start": v(-7.68, 18.78) * mm, "end": v(-7.82, 18.72) * mm});
            skLineSegment(sketch, "E704", {"start": v(-7.82, 18.72) * mm, "end": v(-7.96, 18.67) * mm});
            skLineSegment(sketch, "E705", {"start": v(-7.96, 18.67) * mm, "end": v(-8.1, 18.61) * mm});
            skLineSegment(sketch, "E706", {"start": v(-8.1, 18.61) * mm, "end": v(-8.25, 18.56) * mm});
            skLineSegment(sketch, "E707", {"start": v(-8.25, 18.56) * mm, "end": v(-8.4, 18.5) * mm});
            skLineSegment(sketch, "E708", {"start": v(-8.4, 18.5) * mm, "end": v(-8.54, 18.45) * mm});
            skLineSegment(sketch, "E709", {"start": v(-8.54, 18.45) * mm, "end": v(-8.57, 18.44) * mm});
            skLineSegment(sketch, "E710", {"start": v(-8.57, 18.44) * mm, "end": v(-8.63, 18.58) * mm});
            skLineSegment(sketch, "E711", {"start": v(-8.63, 18.58) * mm, "end": v(-8.69, 18.72) * mm});
            skLineSegment(sketch, "E712", {"start": v(-8.69, 18.72) * mm, "end": v(-8.75, 18.87) * mm});
            skLineSegment(sketch, "E713", {"start": v(-8.75, 18.87) * mm, "end": v(-8.8, 19) * mm});
            skLineSegment(sketch, "E714", {"start": v(-8.8, 19) * mm, "end": v(-8.87, 19.15) * mm});
            skLineSegment(sketch, "E715", {"start": v(-8.87, 19.15) * mm, "end": v(-8.93, 19.3) * mm});
            skLineSegment(sketch, "E716", {"start": v(-8.93, 19.3) * mm, "end": v(-8.99, 19.43) * mm});
            skLineSegment(sketch, "E717", {"start": v(-8.99, 19.43) * mm, "end": v(-9.05, 19.57) * mm});
            skLineSegment(sketch, "E718", {"start": v(-9.05, 19.57) * mm, "end": v(-9.1, 19.72) * mm});
            skLineSegment(sketch, "E719", {"start": v(-9.1, 19.72) * mm, "end": v(-9.17, 19.86) * mm});
            skLineSegment(sketch, "E720", {"start": v(-9.17, 19.86) * mm, "end": v(-9.23, 20) * mm});
            skLineSegment(sketch, "E721", {"start": v(-9.23, 20) * mm, "end": v(-9.29, 20.14) * mm});
            skLineSegment(sketch, "E722", {"start": v(-9.29, 20.14) * mm, "end": v(-9.35, 20.3) * mm});
            skLineSegment(sketch, "E723", {"start": v(-9.35, 20.3) * mm, "end": v(-9.45, 20.43) * mm});
            skLineSegment(sketch, "E724", {"start": v(-9.45, 20.43) * mm, "end": v(-9.57, 20.54) * mm});
            skLineSegment(sketch, "E725", {"start": v(-9.57, 20.54) * mm, "end": v(-9.72, 20.6) * mm});
            skLineSegment(sketch, "E726", {"start": v(-9.72, 20.6) * mm, "end": v(-9.88, 20.64) * mm});
            skLineSegment(sketch, "E727", {"start": v(-9.88, 20.64) * mm, "end": v(-9.92, 20.64) * mm});
            skLineSegment(sketch, "E728", {"start": v(-9.92, 20.64) * mm, "end": v(-10.08, 20.61) * mm});
            skLineSegment(sketch, "E729", {"start": v(-10.08, 20.61) * mm, "end": v(-10.17, 20.58) * mm});
            skLineSegment(sketch, "E730", {"start": v(-10.17, 20.58) * mm, "end": v(-10.31, 20.5) * mm});
            skLineSegment(sketch, "E731", {"start": v(-10.31, 20.5) * mm, "end": v(-10.42, 20.37) * mm});
            skLineSegment(sketch, "E732", {"start": v(-10.42, 20.37) * mm, "end": v(-10.5, 20.23) * mm});
            skLineSegment(sketch, "E733", {"start": v(-10.5, 20.23) * mm, "end": v(-10.54, 20.06) * mm});
            skLineSegment(sketch, "E734", {"start": v(-10.54, 20.06) * mm, "end": v(-10.53, 19.9) * mm});
            skLineSegment(sketch, "E735", {"start": v(-10.53, 19.9) * mm, "end": v(-10.48, 19.74) * mm});
            skLineSegment(sketch, "E736", {"start": v(-10.48, 19.74) * mm, "end": v(-10.41, 19.6) * mm});
            skLineSegment(sketch, "E737", {"start": v(-10.41, 19.6) * mm, "end": v(-10.34, 19.47) * mm});
            skLineSegment(sketch, "E738", {"start": v(-10.34, 19.47) * mm, "end": v(-10.27, 19.33) * mm});
            skLineSegment(sketch, "E739", {"start": v(-10.27, 19.33) * mm, "end": v(-10.2, 19.2) * mm});
            skLineSegment(sketch, "E740", {"start": v(-10.2, 19.2) * mm, "end": v(-10.14, 19.05) * mm});
            skLineSegment(sketch, "E741", {"start": v(-10.14, 19.05) * mm, "end": v(-10.07, 18.92) * mm});
            skLineSegment(sketch, "E742", {"start": v(-10.07, 18.92) * mm, "end": v(-10, 18.78) * mm});
            skLineSegment(sketch, "E743", {"start": v(-10, 18.78) * mm, "end": v(-9.94, 18.64) * mm});
            skLineSegment(sketch, "E744", {"start": v(-9.94, 18.64) * mm, "end": v(-9.87, 18.5) * mm});
            skLineSegment(sketch, "E745", {"start": v(-9.87, 18.5) * mm, "end": v(-9.8, 18.36) * mm});
            skLineSegment(sketch, "E746", {"start": v(-9.8, 18.36) * mm, "end": v(-9.73, 18.23) * mm});
            skLineSegment(sketch, "E747", {"start": v(-9.73, 18.23) * mm, "end": v(-9.66, 18.09) * mm});
            skLineSegment(sketch, "E748", {"start": v(-9.66, 18.09) * mm, "end": v(-9.6, 17.97) * mm});
            skLineSegment(sketch, "E749", {"start": v(-9.6, 17.97) * mm, "end": v(-9.74, 17.9) * mm});
            skLineSegment(sketch, "E750", {"start": v(-9.74, 17.9) * mm, "end": v(-9.87, 17.82) * mm});
            skLineSegment(sketch, "E751", {"start": v(-9.87, 17.82) * mm, "end": v(-10, 17.75) * mm});
            skLineSegment(sketch, "E752", {"start": v(-10, 17.75) * mm, "end": v(-10.14, 17.68) * mm});
            skLineSegment(sketch, "E753", {"start": v(-10.14, 17.68) * mm, "end": v(-10.28, 17.6) * mm});
            skLineSegment(sketch, "E754", {"start": v(-10.28, 17.6) * mm, "end": v(-10.41, 17.53) * mm});
            skLineSegment(sketch, "E755", {"start": v(-10.41, 17.53) * mm, "end": v(-10.55, 17.45) * mm});
            skLineSegment(sketch, "E756", {"start": v(-10.55, 17.45) * mm, "end": v(-10.68, 17.38) * mm});
            skLineSegment(sketch, "E757", {"start": v(-10.68, 17.38) * mm, "end": v(-10.82, 17.3) * mm});
            skLineSegment(sketch, "E758", {"start": v(-10.82, 17.3) * mm, "end": v(-10.95, 17.23) * mm});
            skLineSegment(sketch, "E759", {"start": v(-10.95, 17.23) * mm, "end": v(-11.08, 17.16) * mm});
            skLineSegment(sketch, "E760", {"start": v(-11.08, 17.16) * mm, "end": v(-11.12, 17.14) * mm});
            skLineSegment(sketch, "E761", {"start": v(-11.12, 17.14) * mm, "end": v(-11.2, 17.28) * mm});
            skLineSegment(sketch, "E762", {"start": v(-11.2, 17.28) * mm, "end": v(-11.27, 17.4) * mm});
            skLineSegment(sketch, "E763", {"start": v(-11.27, 17.4) * mm, "end": v(-11.35, 17.54) * mm});
            skLineSegment(sketch, "E764", {"start": v(-11.35, 17.54) * mm, "end": v(-11.43, 17.67) * mm});
            skLineSegment(sketch, "E765", {"start": v(-11.43, 17.67) * mm, "end": v(-11.51, 17.8) * mm});
            skLineSegment(sketch, "E766", {"start": v(-11.51, 17.8) * mm, "end": v(-11.6, 17.93) * mm});
            skLineSegment(sketch, "E767", {"start": v(-11.6, 17.93) * mm, "end": v(-11.67, 18.07) * mm});
            skLineSegment(sketch, "E768", {"start": v(-11.67, 18.07) * mm, "end": v(-11.75, 18.2) * mm});
            skLineSegment(sketch, "E769", {"start": v(-11.75, 18.2) * mm, "end": v(-11.83, 18.33) * mm});
            skLineSegment(sketch, "E770", {"start": v(-11.83, 18.33) * mm, "end": v(-11.9, 18.46) * mm});
            skLineSegment(sketch, "E771", {"start": v(-11.9, 18.46) * mm, "end": v(-11.99, 18.6) * mm});
            skLineSegment(sketch, "E772", {"start": v(-11.99, 18.6) * mm, "end": v(-12.07, 18.72) * mm});
            skLineSegment(sketch, "E773", {"start": v(-12.07, 18.72) * mm, "end": v(-12.16, 18.87) * mm});
            skLineSegment(sketch, "E774", {"start": v(-12.16, 18.87) * mm, "end": v(-12.27, 18.99) * mm});
            skLineSegment(sketch, "E775", {"start": v(-12.27, 18.99) * mm, "end": v(-12.4, 19.07) * mm});
            skLineSegment(sketch, "E776", {"start": v(-12.4, 19.07) * mm, "end": v(-12.56, 19.12) * mm});
            skLineSegment(sketch, "E777", {"start": v(-12.56, 19.12) * mm, "end": v(-12.66, 19.13) * mm});
            skLineSegment(sketch, "E778", {"start": v(-12.66, 19.13) * mm, "end": v(-12.83, 19.11) * mm});
            skLineSegment(sketch, "E779", {"start": v(-12.83, 19.11) * mm, "end": v(-12.98, 19.05) * mm});
            skLineSegment(sketch, "E780", {"start": v(-12.98, 19.05) * mm, "end": v(-13, 19.03) * mm});
            skLineSegment(sketch, "E781", {"start": v(-13, 19.03) * mm, "end": v(-13.13, 18.93) * mm});
            skLineSegment(sketch, "E782", {"start": v(-13.13, 18.93) * mm, "end": v(-13.23, 18.8) * mm});
            skLineSegment(sketch, "E783", {"start": v(-13.23, 18.8) * mm, "end": v(-13.28, 18.64) * mm});
            skLineSegment(sketch, "E784", {"start": v(-13.28, 18.64) * mm, "end": v(-13.3, 18.47) * mm});
            skLineSegment(sketch, "E785", {"start": v(-13.3, 18.47) * mm, "end": v(-13.26, 18.3) * mm});
            skLineSegment(sketch, "E786", {"start": v(-13.26, 18.3) * mm, "end": v(-13.19, 18.16) * mm});
            skLineSegment(sketch, "E787", {"start": v(-13.19, 18.16) * mm, "end": v(-13.1, 18.04) * mm});
            skLineSegment(sketch, "E788", {"start": v(-13.1, 18.04) * mm, "end": v(-13.02, 17.9) * mm});
            skLineSegment(sketch, "E789", {"start": v(-13.02, 17.9) * mm, "end": v(-12.93, 17.78) * mm});
            skLineSegment(sketch, "E790", {"start": v(-12.93, 17.78) * mm, "end": v(-12.84, 17.65) * mm});
            skLineSegment(sketch, "E791", {"start": v(-12.84, 17.65) * mm, "end": v(-12.76, 17.53) * mm});
            skLineSegment(sketch, "E792", {"start": v(-12.76, 17.53) * mm, "end": v(-12.67, 17.4) * mm});
            skLineSegment(sketch, "E793", {"start": v(-12.67, 17.4) * mm, "end": v(-12.58, 17.27) * mm});
            skLineSegment(sketch, "E794", {"start": v(-12.58, 17.27) * mm, "end": v(-12.5, 17.15) * mm});
            skLineSegment(sketch, "E795", {"start": v(-12.5, 17.15) * mm, "end": v(-12.4, 17.02) * mm});
            skLineSegment(sketch, "E796", {"start": v(-12.4, 17.02) * mm, "end": v(-12.32, 16.9) * mm});
            skLineSegment(sketch, "E797", {"start": v(-12.32, 16.9) * mm, "end": v(-12.24, 16.77) * mm});
            skLineSegment(sketch, "E798", {"start": v(-12.24, 16.77) * mm, "end": v(-12.15, 16.64) * mm});
            skLineSegment(sketch, "E799", {"start": v(-12.15, 16.64) * mm, "end": v(-12.07, 16.53) * mm});
            skLineSegment(sketch, "E800", {"start": v(-12.07, 16.53) * mm, "end": v(-12.2, 16.44) * mm});
            skLineSegment(sketch, "E801", {"start": v(-12.2, 16.44) * mm, "end": v(-12.32, 16.35) * mm});
            skLineSegment(sketch, "E802", {"start": v(-12.32, 16.35) * mm, "end": v(-12.44, 16.25) * mm});
            skLineSegment(sketch, "E803", {"start": v(-12.44, 16.25) * mm, "end": v(-12.56, 16.16) * mm});
            skLineSegment(sketch, "E804", {"start": v(-12.56, 16.16) * mm, "end": v(-12.69, 16.07) * mm});
            skLineSegment(sketch, "E805", {"start": v(-12.69, 16.07) * mm, "end": v(-12.8, 15.98) * mm});
            skLineSegment(sketch, "E806", {"start": v(-12.8, 15.98) * mm, "end": v(-12.93, 15.89) * mm});
            skLineSegment(sketch, "E807", {"start": v(-12.93, 15.89) * mm, "end": v(-13.05, 15.8) * mm});
            skLineSegment(sketch, "E808", {"start": v(-13.05, 15.8) * mm, "end": v(-13.18, 15.7) * mm});
            skLineSegment(sketch, "E809", {"start": v(-13.18, 15.7) * mm, "end": v(-13.3, 15.61) * mm});
            skLineSegment(sketch, "E810", {"start": v(-13.3, 15.61) * mm, "end": v(-13.42, 15.52) * mm});
            skLineSegment(sketch, "E811", {"start": v(-13.42, 15.52) * mm, "end": v(-13.45, 15.5) * mm});
            skLineSegment(sketch, "E812", {"start": v(-13.45, 15.5) * mm, "end": v(-13.55, 15.62) * mm});
            skLineSegment(sketch, "E813", {"start": v(-13.55, 15.62) * mm, "end": v(-13.64, 15.73) * mm});
            skLineSegment(sketch, "E814", {"start": v(-13.64, 15.73) * mm, "end": v(-13.74, 15.86) * mm});
            skLineSegment(sketch, "E815", {"start": v(-13.74, 15.86) * mm, "end": v(-13.84, 15.97) * mm});
            skLineSegment(sketch, "E816", {"start": v(-13.84, 15.97) * mm, "end": v(-13.94, 16.1) * mm});
            skLineSegment(sketch, "E817", {"start": v(-13.94, 16.1) * mm, "end": v(-14.03, 16.21) * mm});
            skLineSegment(sketch, "E818", {"start": v(-14.03, 16.21) * mm, "end": v(-14.13, 16.33) * mm});
            skLineSegment(sketch, "E819", {"start": v(-14.13, 16.33) * mm, "end": v(-14.23, 16.45) * mm});
            skLineSegment(sketch, "E820", {"start": v(-14.23, 16.45) * mm, "end": v(-14.33, 16.57) * mm});
            skLineSegment(sketch, "E821", {"start": v(-14.33, 16.57) * mm, "end": v(-14.42, 16.69) * mm});
            skLineSegment(sketch, "E822", {"start": v(-14.42, 16.69) * mm, "end": v(-14.52, 16.8) * mm});
            skLineSegment(sketch, "E823", {"start": v(-14.52, 16.8) * mm, "end": v(-14.62, 16.93) * mm});
            skLineSegment(sketch, "E824", {"start": v(-14.62, 16.93) * mm, "end": v(-14.72, 17.05) * mm});
            skLineSegment(sketch, "E825", {"start": v(-14.72, 17.05) * mm, "end": v(-14.85, 17.16) * mm});
            skLineSegment(sketch, "E826", {"start": v(-14.85, 17.16) * mm, "end": v(-15, 17.23) * mm});
            skLineSegment(sketch, "E827", {"start": v(-15, 17.23) * mm, "end": v(-15.16, 17.25) * mm});
            skLineSegment(sketch, "E828", {"start": v(-15.16, 17.25) * mm, "end": v(-15.33, 17.23) * mm});
            skLineSegment(sketch, "E829", {"start": v(-15.33, 17.23) * mm, "end": v(-15.48, 17.17) * mm});
            skLineSegment(sketch, "E830", {"start": v(-15.48, 17.17) * mm, "end": v(-15.6, 17.1) * mm});
            skLineSegment(sketch, "E831", {"start": v(-15.6, 17.1) * mm, "end": v(-15.7, 16.98) * mm});
            skLineSegment(sketch, "E832", {"start": v(-15.7, 16.98) * mm, "end": v(-15.77, 16.83) * mm});
            skLineSegment(sketch, "E833", {"start": v(-15.77, 16.83) * mm, "end": v(-15.8, 16.67) * mm});
            skLineSegment(sketch, "E834", {"start": v(-15.8, 16.67) * mm, "end": v(-15.8, 16.5) * mm});
            skLineSegment(sketch, "E835", {"start": v(-15.8, 16.5) * mm, "end": v(-15.74, 16.35) * mm});
            skLineSegment(sketch, "E836", {"start": v(-15.74, 16.35) * mm, "end": v(-15.65, 16.2) * mm});
            skLineSegment(sketch, "E837", {"start": v(-15.65, 16.2) * mm, "end": v(-15.54, 16.1) * mm});
            skLineSegment(sketch, "E838", {"start": v(-15.54, 16.1) * mm, "end": v(-15.44, 15.98) * mm});
            skLineSegment(sketch, "E839", {"start": v(-15.44, 15.98) * mm, "end": v(-15.34, 15.87) * mm});
            skLineSegment(sketch, "E840", {"start": v(-15.34, 15.87) * mm, "end": v(-15.23, 15.76) * mm});
            skLineSegment(sketch, "E841", {"start": v(-15.23, 15.76) * mm, "end": v(-15.13, 15.64) * mm});
            skLineSegment(sketch, "E842", {"start": v(-15.13, 15.64) * mm, "end": v(-15.02, 15.53) * mm});
            skLineSegment(sketch, "E843", {"start": v(-15.02, 15.53) * mm, "end": v(-14.92, 15.42) * mm});
            skLineSegment(sketch, "E844", {"start": v(-14.92, 15.42) * mm, "end": v(-14.82, 15.3) * mm});
            skLineSegment(sketch, "E845", {"start": v(-14.82, 15.3) * mm, "end": v(-14.71, 15.19) * mm});
            skLineSegment(sketch, "E846", {"start": v(-14.71, 15.19) * mm, "end": v(-14.6, 15.08) * mm});
            skLineSegment(sketch, "E847", {"start": v(-14.6, 15.08) * mm, "end": v(-14.5, 14.96) * mm});
            skLineSegment(sketch, "E848", {"start": v(-14.5, 14.96) * mm, "end": v(-14.4, 14.85) * mm});
            skLineSegment(sketch, "E849", {"start": v(-14.4, 14.85) * mm, "end": v(-14.31, 14.75) * mm});
            skLineSegment(sketch, "E850", {"start": v(-14.31, 14.75) * mm, "end": v(-14.42, 14.64) * mm});
            skLineSegment(sketch, "E851", {"start": v(-14.42, 14.64) * mm, "end": v(-14.53, 14.54) * mm});
            skLineSegment(sketch, "E852", {"start": v(-14.53, 14.54) * mm, "end": v(-14.64, 14.43) * mm});
            skLineSegment(sketch, "E853", {"start": v(-14.64, 14.43) * mm, "end": v(-14.74, 14.32) * mm});
            skLineSegment(sketch, "E854", {"start": v(-14.74, 14.32) * mm, "end": v(-14.85, 14.21) * mm});
            skLineSegment(sketch, "E855", {"start": v(-14.85, 14.21) * mm, "end": v(-14.96, 14.1) * mm});
            skLineSegment(sketch, "E856", {"start": v(-14.96, 14.1) * mm, "end": v(-15.07, 14) * mm});
            skLineSegment(sketch, "E857", {"start": v(-15.07, 14) * mm, "end": v(-15.18, 13.89) * mm});
            skLineSegment(sketch, "E858", {"start": v(-15.18, 13.89) * mm, "end": v(-15.29, 13.78) * mm});
            skLineSegment(sketch, "E859", {"start": v(-15.29, 13.78) * mm, "end": v(-15.4, 13.67) * mm});
            skLineSegment(sketch, "E860", {"start": v(-15.4, 13.67) * mm, "end": v(-15.5, 13.56) * mm});
            skLineSegment(sketch, "E861", {"start": v(-15.5, 13.56) * mm, "end": v(-15.53, 13.54) * mm});
            skLineSegment(sketch, "E862", {"start": v(-15.53, 13.54) * mm, "end": v(-15.64, 13.64) * mm});
            skLineSegment(sketch, "E863", {"start": v(-15.64, 13.64) * mm, "end": v(-15.75, 13.74) * mm});
            skLineSegment(sketch, "E864", {"start": v(-15.75, 13.74) * mm, "end": v(-15.87, 13.85) * mm});
            skLineSegment(sketch, "E865", {"start": v(-15.87, 13.85) * mm, "end": v(-15.98, 13.95) * mm});
            skLineSegment(sketch, "E866", {"start": v(-15.98, 13.95) * mm, "end": v(-16.1, 14.06) * mm});
            skLineSegment(sketch, "E867", {"start": v(-16.1, 14.06) * mm, "end": v(-16.2, 14.16) * mm});
            skLineSegment(sketch, "E868", {"start": v(-16.2, 14.16) * mm, "end": v(-16.32, 14.26) * mm});
            skLineSegment(sketch, "E869", {"start": v(-16.32, 14.26) * mm, "end": v(-16.43, 14.37) * mm});
            skLineSegment(sketch, "E870", {"start": v(-16.43, 14.37) * mm, "end": v(-16.55, 14.47) * mm});
            skLineSegment(sketch, "E871", {"start": v(-16.55, 14.47) * mm, "end": v(-16.66, 14.58) * mm});
            skLineSegment(sketch, "E872", {"start": v(-16.66, 14.58) * mm, "end": v(-16.77, 14.68) * mm});
            skLineSegment(sketch, "E873", {"start": v(-16.77, 14.68) * mm, "end": v(-16.89, 14.78) * mm});
            skLineSegment(sketch, "E874", {"start": v(-16.89, 14.78) * mm, "end": v(-17, 14.9) * mm});
            skLineSegment(sketch, "E875", {"start": v(-17, 14.9) * mm, "end": v(-17.15, 14.98) * mm});
            skLineSegment(sketch, "E876", {"start": v(-17.15, 14.98) * mm, "end": v(-17.3, 15.03) * mm});
            skLineSegment(sketch, "E877", {"start": v(-17.3, 15.03) * mm, "end": v(-17.4, 15.03) * mm});
            skLineSegment(sketch, "E878", {"start": v(-17.4, 15.03) * mm, "end": v(-17.57, 15) * mm});
            skLineSegment(sketch, "E879", {"start": v(-17.57, 15) * mm, "end": v(-17.72, 14.94) * mm});
            skLineSegment(sketch, "E880", {"start": v(-17.72, 14.94) * mm, "end": v(-17.85, 14.84) * mm});
            skLineSegment(sketch, "E881", {"start": v(-17.85, 14.84) * mm, "end": v(-17.87, 14.82) * mm});
            skLineSegment(sketch, "E882", {"start": v(-17.87, 14.82) * mm, "end": v(-17.96, 14.68) * mm});
            skLineSegment(sketch, "E883", {"start": v(-17.96, 14.68) * mm, "end": v(-18.01, 14.52) * mm});
            skLineSegment(sketch, "E884", {"start": v(-18.01, 14.52) * mm, "end": v(-18.02, 14.36) * mm});
            skLineSegment(sketch, "E885", {"start": v(-18.02, 14.36) * mm, "end": v(-17.99, 14.2) * mm});
            skLineSegment(sketch, "E886", {"start": v(-17.99, 14.2) * mm, "end": v(-17.91, 14.05) * mm});
            skLineSegment(sketch, "E887", {"start": v(-17.91, 14.05) * mm, "end": v(-17.8, 13.93) * mm});
            skLineSegment(sketch, "E888", {"start": v(-17.8, 13.93) * mm, "end": v(-17.68, 13.83) * mm});
            skLineSegment(sketch, "E889", {"start": v(-17.68, 13.83) * mm, "end": v(-17.57, 13.73) * mm});
            skLineSegment(sketch, "E890", {"start": v(-17.57, 13.73) * mm, "end": v(-17.45, 13.64) * mm});
            skLineSegment(sketch, "E891", {"start": v(-17.45, 13.64) * mm, "end": v(-17.33, 13.54) * mm});
            skLineSegment(sketch, "E892", {"start": v(-17.33, 13.54) * mm, "end": v(-17.2, 13.44) * mm});
            skLineSegment(sketch, "E893", {"start": v(-17.2, 13.44) * mm, "end": v(-17.09, 13.34) * mm});
            skLineSegment(sketch, "E894", {"start": v(-17.09, 13.34) * mm, "end": v(-16.97, 13.25) * mm});
            skLineSegment(sketch, "E895", {"start": v(-16.97, 13.25) * mm, "end": v(-16.85, 13.15) * mm});
            skLineSegment(sketch, "E896", {"start": v(-16.85, 13.15) * mm, "end": v(-16.73, 13.05) * mm});
            skLineSegment(sketch, "E897", {"start": v(-16.73, 13.05) * mm, "end": v(-16.61, 12.95) * mm});
            skLineSegment(sketch, "E898", {"start": v(-16.61, 12.95) * mm, "end": v(-16.5, 12.86) * mm});
            skLineSegment(sketch, "E899", {"start": v(-16.5, 12.86) * mm, "end": v(-16.37, 12.76) * mm});
            skLineSegment(sketch, "E900", {"start": v(-16.37, 12.76) * mm, "end": v(-16.27, 12.68) * mm});
            skLineSegment(sketch, "E901", {"start": v(-16.27, 12.68) * mm, "end": v(-16.36, 12.55) * mm});
            skLineSegment(sketch, "E902", {"start": v(-16.36, 12.55) * mm, "end": v(-16.46, 12.43) * mm});
            skLineSegment(sketch, "E903", {"start": v(-16.46, 12.43) * mm, "end": v(-16.55, 12.3) * mm});
            skLineSegment(sketch, "E904", {"start": v(-16.55, 12.3) * mm, "end": v(-16.64, 12.19) * mm});
            skLineSegment(sketch, "E905", {"start": v(-16.64, 12.19) * mm, "end": v(-16.73, 12.06) * mm});
            skLineSegment(sketch, "E906", {"start": v(-16.73, 12.06) * mm, "end": v(-16.82, 11.94) * mm});
            skLineSegment(sketch, "E907", {"start": v(-16.82, 11.94) * mm, "end": v(-16.91, 11.82) * mm});
            skLineSegment(sketch, "E908", {"start": v(-16.91, 11.82) * mm, "end": v(-17, 11.7) * mm});
            skLineSegment(sketch, "E909", {"start": v(-17, 11.7) * mm, "end": v(-17.1, 11.57) * mm});
            skLineSegment(sketch, "E910", {"start": v(-17.1, 11.57) * mm, "end": v(-17.2, 11.45) * mm});
            skLineSegment(sketch, "E911", {"start": v(-17.2, 11.45) * mm, "end": v(-17.28, 11.33) * mm});
            skLineSegment(sketch, "E912", {"start": v(-17.28, 11.33) * mm, "end": v(-17.3, 11.3) * mm});
            skLineSegment(sketch, "E913", {"start": v(-17.3, 11.3) * mm, "end": v(-17.43, 11.39) * mm});
            skLineSegment(sketch, "E914", {"start": v(-17.43, 11.39) * mm, "end": v(-17.56, 11.47) * mm});
            skLineSegment(sketch, "E915", {"start": v(-17.56, 11.47) * mm, "end": v(-17.68, 11.56) * mm});
            skLineSegment(sketch, "E916", {"start": v(-17.68, 11.56) * mm, "end": v(-17.81, 11.65) * mm});
            skLineSegment(sketch, "E917", {"start": v(-17.81, 11.65) * mm, "end": v(-17.94, 11.73) * mm});
            skLineSegment(sketch, "E918", {"start": v(-17.94, 11.73) * mm, "end": v(-18.07, 11.82) * mm});
            skLineSegment(sketch, "E919", {"start": v(-18.07, 11.82) * mm, "end": v(-18.2, 11.9) * mm});
            skLineSegment(sketch, "E920", {"start": v(-18.2, 11.9) * mm, "end": v(-18.32, 12) * mm});
            skLineSegment(sketch, "E921", {"start": v(-18.32, 12) * mm, "end": v(-18.45, 12.08) * mm});
            skLineSegment(sketch, "E922", {"start": v(-18.45, 12.08) * mm, "end": v(-18.57, 12.17) * mm});
            skLineSegment(sketch, "E923", {"start": v(-18.57, 12.17) * mm, "end": v(-18.7, 12.25) * mm});
            skLineSegment(sketch, "E924", {"start": v(-18.7, 12.25) * mm, "end": v(-18.83, 12.34) * mm});
            skLineSegment(sketch, "E925", {"start": v(-18.83, 12.34) * mm, "end": v(-18.96, 12.43) * mm});
            skLineSegment(sketch, "E926", {"start": v(-18.96, 12.43) * mm, "end": v(-19.12, 12.5) * mm});
            skLineSegment(sketch, "E927", {"start": v(-19.12, 12.5) * mm, "end": v(-19.28, 12.52) * mm});
            skLineSegment(sketch, "E928", {"start": v(-19.28, 12.52) * mm, "end": v(-19.44, 12.5) * mm});
            skLineSegment(sketch, "E929", {"start": v(-19.44, 12.5) * mm, "end": v(-19.6, 12.43) * mm});
            skLineSegment(sketch, "E930", {"start": v(-19.6, 12.43) * mm, "end": v(-19.72, 12.33) * mm});
            skLineSegment(sketch, "E931", {"start": v(-19.72, 12.33) * mm, "end": v(-19.8, 12.23) * mm});
            skLineSegment(sketch, "E932", {"start": v(-19.8, 12.23) * mm, "end": v(-19.88, 12.08) * mm});
            skLineSegment(sketch, "E933", {"start": v(-19.88, 12.08) * mm, "end": v(-19.9, 11.92) * mm});
            skLineSegment(sketch, "E934", {"start": v(-19.9, 11.92) * mm, "end": v(-19.9, 11.76) * mm});
            skLineSegment(sketch, "E935", {"start": v(-19.9, 11.76) * mm, "end": v(-19.83, 11.6) * mm});
            skLineSegment(sketch, "E936", {"start": v(-19.83, 11.6) * mm, "end": v(-19.74, 11.47) * mm});
            skLineSegment(sketch, "E937", {"start": v(-19.74, 11.47) * mm, "end": v(-19.61, 11.36) * mm});
            skLineSegment(sketch, "E938", {"start": v(-19.61, 11.36) * mm, "end": v(-19.48, 11.28) * mm});
            skLineSegment(sketch, "E939", {"start": v(-19.48, 11.28) * mm, "end": v(-19.35, 11.2) * mm});
            skLineSegment(sketch, "E940", {"start": v(-19.35, 11.2) * mm, "end": v(-19.22, 11.12) * mm});
            skLineSegment(sketch, "E941", {"start": v(-19.22, 11.12) * mm, "end": v(-19.09, 11.05) * mm});
            skLineSegment(sketch, "E942", {"start": v(-19.09, 11.05) * mm, "end": v(-18.95, 10.97) * mm});
            skLineSegment(sketch, "E943", {"start": v(-18.95, 10.97) * mm, "end": v(-18.82, 10.89) * mm});
            skLineSegment(sketch, "E944", {"start": v(-18.82, 10.89) * mm, "end": v(-18.7, 10.8) * mm});
            skLineSegment(sketch, "E945", {"start": v(-18.7, 10.8) * mm, "end": v(-18.56, 10.73) * mm});
            skLineSegment(sketch, "E946", {"start": v(-18.56, 10.73) * mm, "end": v(-18.43, 10.65) * mm});
            skLineSegment(sketch, "E947", {"start": v(-18.43, 10.65) * mm, "end": v(-18.3, 10.57) * mm});
            skLineSegment(sketch, "E948", {"start": v(-18.3, 10.57) * mm, "end": v(-18.16, 10.49) * mm});
            skLineSegment(sketch, "E949", {"start": v(-18.16, 10.49) * mm, "end": v(-18.03, 10.4) * mm});
            skLineSegment(sketch, "E950", {"start": v(-18.03, 10.4) * mm, "end": v(-17.92, 10.34) * mm});
            skLineSegment(sketch, "E951", {"start": v(-17.92, 10.34) * mm, "end": v(-18, 10.2) * mm});
            skLineSegment(sketch, "E952", {"start": v(-18, 10.2) * mm, "end": v(-18.07, 10.07) * mm});
            skLineSegment(sketch, "E953", {"start": v(-18.07, 10.07) * mm, "end": v(-18.14, 9.94) * mm});
            skLineSegment(sketch, "E954", {"start": v(-18.14, 9.94) * mm, "end": v(-18.21, 9.8) * mm});
            skLineSegment(sketch, "E955", {"start": v(-18.21, 9.8) * mm, "end": v(-18.29, 9.67) * mm});
            skLineSegment(sketch, "E956", {"start": v(-18.29, 9.67) * mm, "end": v(-18.36, 9.53) * mm});
            skLineSegment(sketch, "E957", {"start": v(-18.36, 9.53) * mm, "end": v(-18.43, 9.4) * mm});
            skLineSegment(sketch, "E958", {"start": v(-18.43, 9.4) * mm, "end": v(-18.5, 9.27) * mm});
            skLineSegment(sketch, "E959", {"start": v(-18.5, 9.27) * mm, "end": v(-18.58, 9.13) * mm});
            skLineSegment(sketch, "E960", {"start": v(-18.58, 9.13) * mm, "end": v(-18.65, 9) * mm});
            skLineSegment(sketch, "E961", {"start": v(-18.65, 9) * mm, "end": v(-18.73, 8.86) * mm});
            skLineSegment(sketch, "E962", {"start": v(-18.73, 8.86) * mm, "end": v(-18.74, 8.83) * mm});
            skLineSegment(sketch, "E963", {"start": v(-18.74, 8.83) * mm, "end": v(-18.88, 8.9) * mm});
            skLineSegment(sketch, "E964", {"start": v(-18.88, 8.9) * mm, "end": v(-19.02, 8.97) * mm});
            skLineSegment(sketch, "E965", {"start": v(-19.02, 8.97) * mm, "end": v(-19.16, 9.03) * mm});
            skLineSegment(sketch, "E966", {"start": v(-19.16, 9.03) * mm, "end": v(-19.3, 9.1) * mm});
            skLineSegment(sketch, "E967", {"start": v(-19.3, 9.1) * mm, "end": v(-19.43, 9.17) * mm});
            skLineSegment(sketch, "E968", {"start": v(-19.43, 9.17) * mm, "end": v(-19.57, 9.24) * mm});
            skLineSegment(sketch, "E969", {"start": v(-19.57, 9.24) * mm, "end": v(-19.7, 9.3) * mm});
            skLineSegment(sketch, "E970", {"start": v(-19.7, 9.3) * mm, "end": v(-19.85, 9.37) * mm});
            skLineSegment(sketch, "E971", {"start": v(-19.85, 9.37) * mm, "end": v(-19.99, 9.44) * mm});
            skLineSegment(sketch, "E972", {"start": v(-19.99, 9.44) * mm, "end": v(-20.12, 9.5) * mm});
            skLineSegment(sketch, "E973", {"start": v(-20.12, 9.5) * mm, "end": v(-20.26, 9.58) * mm});
            skLineSegment(sketch, "E974", {"start": v(-20.26, 9.58) * mm, "end": v(-20.4, 9.65) * mm});
            skLineSegment(sketch, "E975", {"start": v(-20.4, 9.65) * mm, "end": v(-20.55, 9.72) * mm});
            skLineSegment(sketch, "E976", {"start": v(-20.55, 9.72) * mm, "end": v(-20.7, 9.76) * mm});
            skLineSegment(sketch, "E977", {"start": v(-20.7, 9.76) * mm, "end": v(-20.77, 9.76) * mm});
            skLineSegment(sketch, "E978", {"start": v(-20.77, 9.76) * mm, "end": v(-20.94, 9.75) * mm});
            skLineSegment(sketch, "E979", {"start": v(-20.94, 9.75) * mm, "end": v(-21.1, 9.68) * mm});
            skLineSegment(sketch, "E980", {"start": v(-21.1, 9.68) * mm, "end": v(-21.22, 9.59) * mm});
            skLineSegment(sketch, "E981", {"start": v(-21.22, 9.59) * mm, "end": v(-21.32, 9.46) * mm});
            skLineSegment(sketch, "E982", {"start": v(-21.32, 9.46) * mm, "end": v(-21.35, 9.4) * mm});
            skLineSegment(sketch, "E983", {"start": v(-21.35, 9.4) * mm, "end": v(-21.4, 9.24) * mm});
            skLineSegment(sketch, "E984", {"start": v(-21.4, 9.24) * mm, "end": v(-21.4, 9.08) * mm});
            skLineSegment(sketch, "E985", {"start": v(-21.4, 9.08) * mm, "end": v(-21.37, 8.92) * mm});
            skLineSegment(sketch, "E986", {"start": v(-21.37, 8.92) * mm, "end": v(-21.3, 8.77) * mm});
            skLineSegment(sketch, "E987", {"start": v(-21.3, 8.77) * mm, "end": v(-21.18, 8.65) * mm});
            skLineSegment(sketch, "E988", {"start": v(-21.18, 8.65) * mm, "end": v(-21.04, 8.57) * mm});
            skLineSegment(sketch, "E989", {"start": v(-21.04, 8.57) * mm, "end": v(-20.9, 8.5) * mm});
            skLineSegment(sketch, "E990", {"start": v(-20.9, 8.5) * mm, "end": v(-20.76, 8.45) * mm});
            skLineSegment(sketch, "E991", {"start": v(-20.76, 8.45) * mm, "end": v(-20.61, 8.39) * mm});
            skLineSegment(sketch, "E992", {"start": v(-20.61, 8.39) * mm, "end": v(-20.47, 8.33) * mm});
            skLineSegment(sketch, "E993", {"start": v(-20.47, 8.33) * mm, "end": v(-20.33, 8.27) * mm});
            skLineSegment(sketch, "E994", {"start": v(-20.33, 8.27) * mm, "end": v(-20.19, 8.2) * mm});
            skLineSegment(sketch, "E995", {"start": v(-20.19, 8.2) * mm, "end": v(-20.05, 8.15) * mm});
            skLineSegment(sketch, "E996", {"start": v(-20.05, 8.15) * mm, "end": v(-19.9, 8.09) * mm});
            skLineSegment(sketch, "E997", {"start": v(-19.9, 8.09) * mm, "end": v(-19.76, 8.03) * mm});
            skLineSegment(sketch, "E998", {"start": v(-19.76, 8.03) * mm, "end": v(-19.62, 7.97) * mm});
            skLineSegment(sketch, "E999", {"start": v(-19.62, 7.97) * mm, "end": v(-19.48, 7.9) * mm});
            skLineSegment(sketch, "E1000", {"start": v(-19.48, 7.9) * mm, "end": v(-19.34, 7.85) * mm});
            skLineSegment(sketch, "E1001", {"start": v(-19.34, 7.85) * mm, "end": v(-19.22, 7.8) * mm});
            skLineSegment(sketch, "E1002", {"start": v(-19.22, 7.8) * mm, "end": v(-19.27, 7.65) * mm});
            skLineSegment(sketch, "E1003", {"start": v(-19.27, 7.65) * mm, "end": v(-19.32, 7.5) * mm});
            skLineSegment(sketch, "E1004", {"start": v(-19.32, 7.5) * mm, "end": v(-19.38, 7.37) * mm});
            skLineSegment(sketch, "E1005", {"start": v(-19.38, 7.37) * mm, "end": v(-19.43, 7.22) * mm});
            skLineSegment(sketch, "E1006", {"start": v(-19.43, 7.22) * mm, "end": v(-19.48, 7.08) * mm});
            skLineSegment(sketch, "E1007", {"start": v(-19.48, 7.08) * mm, "end": v(-19.54, 6.94) * mm});
            skLineSegment(sketch, "E1008", {"start": v(-19.54, 6.94) * mm, "end": v(-19.6, 6.8) * mm});
            skLineSegment(sketch, "E1009", {"start": v(-19.6, 6.8) * mm, "end": v(-19.64, 6.65) * mm});
            skLineSegment(sketch, "E1010", {"start": v(-19.64, 6.65) * mm, "end": v(-19.7, 6.5) * mm});
            skLineSegment(sketch, "E1011", {"start": v(-19.7, 6.5) * mm, "end": v(-19.75, 6.36) * mm});
            skLineSegment(sketch, "E1012", {"start": v(-19.75, 6.36) * mm, "end": v(-19.8, 6.22) * mm});
            skLineSegment(sketch, "E1013", {"start": v(-19.8, 6.22) * mm, "end": v(-19.82, 6.18) * mm});
            skLineSegment(sketch, "E1014", {"start": v(-19.82, 6.18) * mm, "end": v(-19.96, 6.23) * mm});
            skLineSegment(sketch, "E1015", {"start": v(-19.96, 6.23) * mm, "end": v(-20.1, 6.28) * mm});
            skLineSegment(sketch, "E1016", {"start": v(-20.1, 6.28) * mm, "end": v(-20.26, 6.33) * mm});
            skLineSegment(sketch, "E1017", {"start": v(-20.26, 6.33) * mm, "end": v(-20.4, 6.37) * mm});
            skLineSegment(sketch, "E1018", {"start": v(-20.4, 6.37) * mm, "end": v(-20.55, 6.42) * mm});
            skLineSegment(sketch, "E1019", {"start": v(-20.55, 6.42) * mm, "end": v(-20.7, 6.47) * mm});
            skLineSegment(sketch, "E1020", {"start": v(-20.7, 6.47) * mm, "end": v(-20.84, 6.52) * mm});
            skLineSegment(sketch, "E1021", {"start": v(-20.84, 6.52) * mm, "end": v(-20.99, 6.56) * mm});
            skLineSegment(sketch, "E1022", {"start": v(-20.99, 6.56) * mm, "end": v(-21.13, 6.61) * mm});
            skLineSegment(sketch, "E1023", {"start": v(-21.13, 6.61) * mm, "end": v(-21.28, 6.66) * mm});
            skLineSegment(sketch, "E1024", {"start": v(-21.28, 6.66) * mm, "end": v(-21.43, 6.7) * mm});
            skLineSegment(sketch, "E1025", {"start": v(-21.43, 6.7) * mm, "end": v(-21.57, 6.75) * mm});
            skLineSegment(sketch, "E1026", {"start": v(-21.57, 6.75) * mm, "end": v(-21.73, 6.8) * mm});
            skLineSegment(sketch, "E1027", {"start": v(-21.73, 6.8) * mm, "end": v(-21.9, 6.82) * mm});
            skLineSegment(sketch, "E1028", {"start": v(-21.9, 6.82) * mm, "end": v(-22.06, 6.8) * mm});
            skLineSegment(sketch, "E1029", {"start": v(-22.06, 6.8) * mm, "end": v(-22.2, 6.73) * mm});
            skLineSegment(sketch, "E1030", {"start": v(-22.2, 6.73) * mm, "end": v(-22.34, 6.63) * mm});
            skLineSegment(sketch, "E1031", {"start": v(-22.34, 6.63) * mm, "end": v(-22.43, 6.5) * mm});
            skLineSegment(sketch, "E1032", {"start": v(-22.43, 6.5) * mm, "end": v(-22.48, 6.37) * mm});
            skLineSegment(sketch, "E1033", {"start": v(-22.48, 6.37) * mm, "end": v(-22.5, 6.21) * mm});
            skLineSegment(sketch, "E1034", {"start": v(-22.5, 6.21) * mm, "end": v(-22.49, 6.05) * mm});
            skLineSegment(sketch, "E1035", {"start": v(-22.49, 6.05) * mm, "end": v(-22.43, 5.9) * mm});
            skLineSegment(sketch, "E1036", {"start": v(-22.43, 5.9) * mm, "end": v(-22.33, 5.76) * mm});
            skLineSegment(sketch, "E1037", {"start": v(-22.33, 5.76) * mm, "end": v(-22.2, 5.66) * mm});
            skLineSegment(sketch, "E1038", {"start": v(-22.2, 5.66) * mm, "end": v(-22.05, 5.6) * mm});
            skLineSegment(sketch, "E1039", {"start": v(-22.05, 5.6) * mm, "end": v(-21.9, 5.56) * mm});
            skLineSegment(sketch, "E1040", {"start": v(-21.9, 5.56) * mm, "end": v(-21.75, 5.52) * mm});
            skLineSegment(sketch, "E1041", {"start": v(-21.75, 5.52) * mm, "end": v(-21.6, 5.48) * mm});
            skLineSegment(sketch, "E1042", {"start": v(-21.6, 5.48) * mm, "end": v(-21.46, 5.44) * mm});
            skLineSegment(sketch, "E1043", {"start": v(-21.46, 5.44) * mm, "end": v(-21.3, 5.4) * mm});
            skLineSegment(sketch, "E1044", {"start": v(-21.3, 5.4) * mm, "end": v(-21.16, 5.36) * mm});
            skLineSegment(sketch, "E1045", {"start": v(-21.16, 5.36) * mm, "end": v(-21, 5.32) * mm});
            skLineSegment(sketch, "E1046", {"start": v(-21, 5.32) * mm, "end": v(-20.86, 5.28) * mm});
            skLineSegment(sketch, "E1047", {"start": v(-20.86, 5.28) * mm, "end": v(-20.71, 5.24) * mm});
            skLineSegment(sketch, "E1048", {"start": v(-20.71, 5.24) * mm, "end": v(-20.56, 5.2) * mm});
            skLineSegment(sketch, "E1049", {"start": v(-20.56, 5.2) * mm, "end": v(-20.42, 5.17) * mm});
            skLineSegment(sketch, "E1050", {"start": v(-20.42, 5.17) * mm, "end": v(-20.27, 5.13) * mm});
            skLineSegment(sketch, "E1051", {"start": v(-20.27, 5.13) * mm, "end": v(-20.14, 5.1) * mm});
            skLineSegment(sketch, "E1052", {"start": v(-20.14, 5.1) * mm, "end": v(-20.17, 4.94) * mm});
            skLineSegment(sketch, "E1053", {"start": v(-20.17, 4.94) * mm, "end": v(-20.2, 4.8) * mm});
            skLineSegment(sketch, "E1054", {"start": v(-20.2, 4.8) * mm, "end": v(-20.24, 4.64) * mm});
            skLineSegment(sketch, "E1055", {"start": v(-20.24, 4.64) * mm, "end": v(-20.27, 4.5) * mm});
            skLineSegment(sketch, "E1056", {"start": v(-20.27, 4.5) * mm, "end": v(-20.3, 4.34) * mm});
            skLineSegment(sketch, "E1057", {"start": v(-20.3, 4.34) * mm, "end": v(-20.33, 4.2) * mm});
            skLineSegment(sketch, "E1058", {"start": v(-20.33, 4.2) * mm, "end": v(-20.37, 4.04) * mm});
            skLineSegment(sketch, "E1059", {"start": v(-20.37, 4.04) * mm, "end": v(-20.4, 3.9) * mm});
            skLineSegment(sketch, "E1060", {"start": v(-20.4, 3.9) * mm, "end": v(-20.43, 3.75) * mm});
            skLineSegment(sketch, "E1061", {"start": v(-20.43, 3.75) * mm, "end": v(-20.46, 3.6) * mm});
            skLineSegment(sketch, "E1062", {"start": v(-20.46, 3.6) * mm, "end": v(-20.5, 3.45) * mm});
            skLineSegment(sketch, "E1063", {"start": v(-20.5, 3.45) * mm, "end": v(-20.5, 3.41) * mm});
            skLineSegment(sketch, "E1064", {"start": v(-20.5, 3.41) * mm, "end": v(-20.65, 3.44) * mm});
            skLineSegment(sketch, "E1065", {"start": v(-20.65, 3.44) * mm, "end": v(-20.8, 3.46) * mm});
            skLineSegment(sketch, "E1066", {"start": v(-20.8, 3.46) * mm, "end": v(-20.96, 3.49) * mm});
            skLineSegment(sketch, "E1067", {"start": v(-20.96, 3.49) * mm, "end": v(-21.1, 3.52) * mm});
            skLineSegment(sketch, "E1068", {"start": v(-21.1, 3.52) * mm, "end": v(-21.26, 3.54) * mm});
            skLineSegment(sketch, "E1069", {"start": v(-21.26, 3.54) * mm, "end": v(-21.41, 3.57) * mm});
            skLineSegment(sketch, "E1070", {"start": v(-21.41, 3.57) * mm, "end": v(-21.56, 3.6) * mm});
            skLineSegment(sketch, "E1071", {"start": v(-21.56, 3.6) * mm, "end": v(-21.71, 3.62) * mm});
            skLineSegment(sketch, "E1072", {"start": v(-21.71, 3.62) * mm, "end": v(-21.87, 3.65) * mm});
            skLineSegment(sketch, "E1073", {"start": v(-21.87, 3.65) * mm, "end": v(-22.02, 3.67) * mm});
            skLineSegment(sketch, "E1074", {"start": v(-22.02, 3.67) * mm, "end": v(-22.17, 3.7) * mm});
            skLineSegment(sketch, "E1075", {"start": v(-22.17, 3.7) * mm, "end": v(-22.32, 3.73) * mm});
            skLineSegment(sketch, "E1076", {"start": v(-22.32, 3.73) * mm, "end": v(-22.49, 3.75) * mm});
            skLineSegment(sketch, "E1077", {"start": v(-22.49, 3.75) * mm, "end": v(-22.55, 3.76) * mm});
            skLineSegment(sketch, "E1078", {"start": v(-22.55, 3.76) * mm, "end": v(-22.71, 3.73) * mm});
            skLineSegment(sketch, "E1079", {"start": v(-22.71, 3.73) * mm, "end": v(-22.87, 3.67) * mm});
            skLineSegment(sketch, "E1080", {"start": v(-22.87, 3.67) * mm, "end": v(-23, 3.57) * mm});
            skLineSegment(sketch, "E1081", {"start": v(-23, 3.57) * mm, "end": v(-23.1, 3.44) * mm});
            skLineSegment(sketch, "E1082", {"start": v(-23.1, 3.44) * mm, "end": v(-23.16, 3.28) * mm});
            skLineSegment(sketch, "E1083", {"start": v(-23.16, 3.28) * mm, "end": v(-23.18, 3.12) * mm});
            skLineSegment(sketch, "E1084", {"start": v(-23.18, 3.12) * mm, "end": v(-23.15, 2.96) * mm});
            skLineSegment(sketch, "E1085", {"start": v(-23.15, 2.96) * mm, "end": v(-23.08, 2.8) * mm});
            skLineSegment(sketch, "E1086", {"start": v(-23.08, 2.8) * mm, "end": v(-22.98, 2.68) * mm});
            skLineSegment(sketch, "E1087", {"start": v(-22.98, 2.68) * mm, "end": v(-22.85, 2.58) * mm});
            skLineSegment(sketch, "E1088", {"start": v(-22.85, 2.58) * mm, "end": v(-22.7, 2.52) * mm});
            skLineSegment(sketch, "E1089", {"start": v(-22.7, 2.52) * mm, "end": v(-22.54, 2.5) * mm});
            skLineSegment(sketch, "E1090", {"start": v(-22.54, 2.5) * mm, "end": v(-22.4, 2.48) * mm});
            skLineSegment(sketch, "E1091", {"start": v(-22.4, 2.48) * mm, "end": v(-22.24, 2.47) * mm});
            skLineSegment(sketch, "E1092", {"start": v(-22.24, 2.47) * mm, "end": v(-22.09, 2.45) * mm});
            skLineSegment(sketch, "E1093", {"start": v(-22.09, 2.45) * mm, "end": v(-21.93, 2.43) * mm});
            skLineSegment(sketch, "E1094", {"start": v(-21.93, 2.43) * mm, "end": v(-21.78, 2.41) * mm});
            skLineSegment(sketch, "E1095", {"start": v(-21.78, 2.41) * mm, "end": v(-21.63, 2.4) * mm});
            skLineSegment(sketch, "E1096", {"start": v(-21.63, 2.4) * mm, "end": v(-21.47, 2.38) * mm});
            skLineSegment(sketch, "E1097", {"start": v(-21.47, 2.38) * mm, "end": v(-21.32, 2.36) * mm});
            skLineSegment(sketch, "E1098", {"start": v(-21.32, 2.36) * mm, "end": v(-21.17, 2.34) * mm});
            skLineSegment(sketch, "E1099", {"start": v(-21.17, 2.34) * mm, "end": v(-21.02, 2.32) * mm});
            skLineSegment(sketch, "E1100", {"start": v(-21.02, 2.32) * mm, "end": v(-20.86, 2.3) * mm});
            skLineSegment(sketch, "E1101", {"start": v(-20.86, 2.3) * mm, "end": v(-20.7, 2.29) * mm});
            skLineSegment(sketch, "E1102", {"start": v(-20.7, 2.29) * mm, "end": v(-20.67, 2.28) * mm});
            skLineSegment(sketch, "E1103", {"start": v(-20.67, 2.28) * mm, "end": v(-20.68, 2.13) * mm});
            skLineSegment(sketch, "E1104", {"start": v(-20.68, 2.13) * mm, "end": v(-20.69, 1.98) * mm});
            skLineSegment(sketch, "E1105", {"start": v(-20.69, 1.98) * mm, "end": v(-20.7, 1.83) * mm});
            skLineSegment(sketch, "E1106", {"start": v(-20.7, 1.83) * mm, "end": v(-20.7, 1.67) * mm});
            skLineSegment(sketch, "E1107", {"start": v(-20.7, 1.67) * mm, "end": v(-20.72, 1.52) * mm});
            skLineSegment(sketch, "E1108", {"start": v(-20.72, 1.52) * mm, "end": v(-20.73, 1.37) * mm});
            skLineSegment(sketch, "E1109", {"start": v(-20.73, 1.37) * mm, "end": v(-20.74, 1.22) * mm});
            skLineSegment(sketch, "E1110", {"start": v(-20.74, 1.22) * mm, "end": v(-20.75, 1.06) * mm});
            skLineSegment(sketch, "E1111", {"start": v(-20.75, 1.06) * mm, "end": v(-20.76, 0.9) * mm});
            skLineSegment(sketch, "E1112", {"start": v(-20.76, 0.9) * mm, "end": v(-20.77, 0.76) * mm});
            skLineSegment(sketch, "E1113", {"start": v(-20.77, 0.76) * mm, "end": v(-20.79, 0.6) * mm});
            skLineSegment(sketch, "E1114", {"start": v(-20.79, 0.6) * mm, "end": v(-20.79, 0.57) * mm});
            skLineSegment(sketch, "E1115", {"start": v(-20.79, 0.57) * mm, "end": v(-20.94, 0.57) * mm});
            skLineSegment(sketch, "E1116", {"start": v(-20.94, 0.57) * mm, "end": v(-21.1, 0.58) * mm});
            skLineSegment(sketch, "E1117", {"start": v(-21.1, 0.58) * mm, "end": v(-21.25, 0.58) * mm});
            skLineSegment(sketch, "E1118", {"start": v(-21.25, 0.58) * mm, "end": v(-21.4, 0.59) * mm});
            skLineSegment(sketch, "E1119", {"start": v(-21.4, 0.59) * mm, "end": v(-21.56, 0.6) * mm});
            skLineSegment(sketch, "E1120", {"start": v(-21.56, 0.6) * mm, "end": v(-21.71, 0.6) * mm});
            skLineSegment(sketch, "E1121", {"start": v(-21.71, 0.6) * mm, "end": v(-21.86, 0.6) * mm});
            skLineSegment(sketch, "E1122", {"start": v(-21.86, 0.6) * mm, "end": v(-22.02, 0.6) * mm});
            skLineSegment(sketch, "E1123", {"start": v(-22.02, 0.6) * mm, "end": v(-22.17, 0.6) * mm});
            skLineSegment(sketch, "E1124", {"start": v(-22.17, 0.6) * mm, "end": v(-22.33, 0.61) * mm});
            skLineSegment(sketch, "E1125", {"start": v(-22.33, 0.61) * mm, "end": v(-22.48, 0.62) * mm});
            skLineSegment(sketch, "E1126", {"start": v(-22.48, 0.62) * mm, "end": v(-22.63, 0.62) * mm});
            skLineSegment(sketch, "E1127", {"start": v(-22.63, 0.62) * mm, "end": v(-22.77, 0.62) * mm});
            skLineSegment(sketch, "E1128", {"start": v(-22.77, 0.62) * mm, "end": v(-22.93, 0.6) * mm});
            skLineSegment(sketch, "E1129", {"start": v(-22.93, 0.6) * mm, "end": v(-23.08, 0.54) * mm});
            skLineSegment(sketch, "E1130", {"start": v(-23.08, 0.54) * mm, "end": v(-23.21, 0.44) * mm});
            skLineSegment(sketch, "E1131", {"start": v(-23.21, 0.44) * mm, "end": v(-23.31, 0.31) * mm});
            skLineSegment(sketch, "E1132", {"start": v(-23.31, 0.31) * mm, "end": v(-23.38, 0.16) * mm});
            skLineSegment(sketch, "E1133", {"start": v(-23.38, 0.16) * mm, "end": v(-23.4, 0) * mm});
            skLineSegment(sketch, "E1134", {"start": v(-23.4, 0) * mm, "end": v(-23.38, -0.16) * mm});
            skLineSegment(sketch, "E1135", {"start": v(-23.38, -0.16) * mm, "end": v(-23.31, -0.32) * mm});
            skLineSegment(sketch, "E1136", {"start": v(-23.31, -0.32) * mm, "end": v(-23.21, -0.45) * mm});
            skLineSegment(sketch, "E1137", {"start": v(-23.21, -0.45) * mm, "end": v(-23.08, -0.54) * mm});
            skLineSegment(sketch, "E1138", {"start": v(-23.08, -0.54) * mm, "end": v(-22.93, -0.6) * mm});
            skLineSegment(sketch, "E1139", {"start": v(-22.93, -0.6) * mm, "end": v(-22.77, -0.63) * mm});
            skLineSegment(sketch, "E1140", {"start": v(-22.77, -0.63) * mm, "end": v(-22.61, -0.62) * mm});
            skLineSegment(sketch, "E1141", {"start": v(-22.61, -0.62) * mm, "end": v(-22.46, -0.62) * mm});
            skLineSegment(sketch, "E1142", {"start": v(-22.46, -0.62) * mm, "end": v(-22.3, -0.61) * mm});
            skLineSegment(sketch, "E1143", {"start": v(-22.3, -0.61) * mm, "end": v(-22.15, -0.6) * mm});
            skLineSegment(sketch, "E1144", {"start": v(-22.15, -0.6) * mm, "end": v(-22, -0.6) * mm});
            skLineSegment(sketch, "E1145", {"start": v(-22, -0.6) * mm, "end": v(-21.84, -0.6) * mm});
            skLineSegment(sketch, "E1146", {"start": v(-21.84, -0.6) * mm, "end": v(-21.69, -0.6) * mm});
            skLineSegment(sketch, "E1147", {"start": v(-21.69, -0.6) * mm, "end": v(-21.54, -0.6) * mm});
            skLineSegment(sketch, "E1148", {"start": v(-21.54, -0.6) * mm, "end": v(-21.38, -0.59) * mm});
            skLineSegment(sketch, "E1149", {"start": v(-21.38, -0.59) * mm, "end": v(-21.23, -0.58) * mm});
            skLineSegment(sketch, "E1150", {"start": v(-21.23, -0.58) * mm, "end": v(-21.08, -0.58) * mm});
            skLineSegment(sketch, "E1151", {"start": v(-21.08, -0.58) * mm, "end": v(-20.92, -0.57) * mm});
            skLineSegment(sketch, "E1152", {"start": v(-20.92, -0.57) * mm, "end": v(-20.79, -0.57) * mm});
            skLineSegment(sketch, "E1153", {"start": v(-20.79, -0.57) * mm, "end": v(-20.78, -0.72) * mm});
            skLineSegment(sketch, "E1154", {"start": v(-20.78, -0.72) * mm, "end": v(-20.77, -0.87) * mm});
            skLineSegment(sketch, "E1155", {"start": v(-20.77, -0.87) * mm, "end": v(-20.76, -1.03) * mm});
            skLineSegment(sketch, "E1156", {"start": v(-20.76, -1.03) * mm, "end": v(-20.74, -1.18) * mm});
            skLineSegment(sketch, "E1157", {"start": v(-20.74, -1.18) * mm, "end": v(-20.73, -1.33) * mm});
            skLineSegment(sketch, "E1158", {"start": v(-20.73, -1.33) * mm, "end": v(-20.72, -1.49) * mm});
            skLineSegment(sketch, "E1159", {"start": v(-20.72, -1.49) * mm, "end": v(-20.71, -1.64) * mm});
            skLineSegment(sketch, "E1160", {"start": v(-20.71, -1.64) * mm, "end": v(-20.7, -1.8) * mm});
            skLineSegment(sketch, "E1161", {"start": v(-20.7, -1.8) * mm, "end": v(-20.69, -1.94) * mm});
            skLineSegment(sketch, "E1162", {"start": v(-20.69, -1.94) * mm, "end": v(-20.68, -2.1) * mm});
            skLineSegment(sketch, "E1163", {"start": v(-20.68, -2.1) * mm, "end": v(-20.67, -2.25) * mm});
            skLineSegment(sketch, "E1164", {"start": v(-20.67, -2.25) * mm, "end": v(-20.67, -2.29) * mm});
            skLineSegment(sketch, "E1165", {"start": v(-20.67, -2.29) * mm, "end": v(-20.82, -2.3) * mm});
            skLineSegment(sketch, "E1166", {"start": v(-20.82, -2.3) * mm, "end": v(-20.97, -2.32) * mm});
            skLineSegment(sketch, "E1167", {"start": v(-20.97, -2.32) * mm, "end": v(-21.12, -2.34) * mm});
            skLineSegment(sketch, "E1168", {"start": v(-21.12, -2.34) * mm, "end": v(-21.28, -2.36) * mm});
            skLineSegment(sketch, "E1169", {"start": v(-21.28, -2.36) * mm, "end": v(-21.43, -2.37) * mm});
            skLineSegment(sketch, "E1170", {"start": v(-21.43, -2.37) * mm, "end": v(-21.58, -2.4) * mm});
            skLineSegment(sketch, "E1171", {"start": v(-21.58, -2.4) * mm, "end": v(-21.73, -2.4) * mm});
            skLineSegment(sketch, "E1172", {"start": v(-21.73, -2.4) * mm, "end": v(-21.89, -2.43) * mm});
            skLineSegment(sketch, "E1173", {"start": v(-21.89, -2.43) * mm, "end": v(-22.04, -2.44) * mm});
            skLineSegment(sketch, "E1174", {"start": v(-22.04, -2.44) * mm, "end": v(-22.2, -2.46) * mm});
            skLineSegment(sketch, "E1175", {"start": v(-22.2, -2.46) * mm, "end": v(-22.35, -2.48) * mm});
            skLineSegment(sketch, "E1176", {"start": v(-22.35, -2.48) * mm, "end": v(-22.5, -2.5) * mm});
            skLineSegment(sketch, "E1177", {"start": v(-22.5, -2.5) * mm, "end": v(-22.66, -2.52) * mm});
            skLineSegment(sketch, "E1178", {"start": v(-22.66, -2.52) * mm, "end": v(-22.82, -2.57) * mm});
            skLineSegment(sketch, "E1179", {"start": v(-22.82, -2.57) * mm, "end": v(-22.96, -2.66) * mm});
            skLineSegment(sketch, "E1180", {"start": v(-22.96, -2.66) * mm, "end": v(-23.07, -2.78) * mm});
            skLineSegment(sketch, "E1181", {"start": v(-23.07, -2.78) * mm, "end": v(-23.14, -2.93) * mm});
            skLineSegment(sketch, "E1182", {"start": v(-23.14, -2.93) * mm, "end": v(-23.17, -3.09) * mm});
            skLineSegment(sketch, "E1183", {"start": v(-23.17, -3.09) * mm, "end": v(-23.16, -3.25) * mm});
            skLineSegment(sketch, "E1184", {"start": v(-23.16, -3.25) * mm, "end": v(-23.11, -3.4) * mm});
            skLineSegment(sketch, "E1185", {"start": v(-23.11, -3.4) * mm, "end": v(-23.02, -3.55) * mm});
            skLineSegment(sketch, "E1186", {"start": v(-23.02, -3.55) * mm, "end": v(-22.9, -3.65) * mm});
            skLineSegment(sketch, "E1187", {"start": v(-22.9, -3.65) * mm, "end": v(-22.75, -3.73) * mm});
            skLineSegment(sketch, "E1188", {"start": v(-22.75, -3.73) * mm, "end": v(-22.58, -3.76) * mm});
            skLineSegment(sketch, "E1189", {"start": v(-22.58, -3.76) * mm, "end": v(-22.43, -3.74) * mm});
            skLineSegment(sketch, "E1190", {"start": v(-22.43, -3.74) * mm, "end": v(-22.28, -3.72) * mm});
            skLineSegment(sketch, "E1191", {"start": v(-22.28, -3.72) * mm, "end": v(-22.13, -3.7) * mm});
            skLineSegment(sketch, "E1192", {"start": v(-22.13, -3.7) * mm, "end": v(-21.98, -3.67) * mm});
            skLineSegment(sketch, "E1193", {"start": v(-21.98, -3.67) * mm, "end": v(-21.83, -3.64) * mm});
            skLineSegment(sketch, "E1194", {"start": v(-21.83, -3.64) * mm, "end": v(-21.67, -3.61) * mm});
            skLineSegment(sketch, "E1195", {"start": v(-21.67, -3.61) * mm, "end": v(-21.52, -3.59) * mm});
            skLineSegment(sketch, "E1196", {"start": v(-21.52, -3.59) * mm, "end": v(-21.37, -3.56) * mm});
            skLineSegment(sketch, "E1197", {"start": v(-21.37, -3.56) * mm, "end": v(-21.22, -3.54) * mm});
            skLineSegment(sketch, "E1198", {"start": v(-21.22, -3.54) * mm, "end": v(-21.07, -3.5) * mm});
            skLineSegment(sketch, "E1199", {"start": v(-21.07, -3.5) * mm, "end": v(-20.92, -3.48) * mm});
            skLineSegment(sketch, "E1200", {"start": v(-20.92, -3.48) * mm, "end": v(-20.76, -3.46) * mm});
            skLineSegment(sketch, "E1201", {"start": v(-20.76, -3.46) * mm, "end": v(-20.61, -3.43) * mm});
            skLineSegment(sketch, "E1202", {"start": v(-20.61, -3.43) * mm, "end": v(-20.5, -3.41) * mm});
            skLineSegment(sketch, "E1203", {"start": v(-20.5, -3.41) * mm, "end": v(-20.47, -3.56) * mm});
            skLineSegment(sketch, "E1204", {"start": v(-20.47, -3.56) * mm, "end": v(-20.44, -3.71) * mm});
            skLineSegment(sketch, "E1205", {"start": v(-20.44, -3.71) * mm, "end": v(-20.4, -3.86) * mm});
            skLineSegment(sketch, "E1206", {"start": v(-20.4, -3.86) * mm, "end": v(-20.37, -4.01) * mm});
            skLineSegment(sketch, "E1207", {"start": v(-20.37, -4.01) * mm, "end": v(-20.34, -4.16) * mm});
            skLineSegment(sketch, "E1208", {"start": v(-20.34, -4.16) * mm, "end": v(-20.3, -4.3) * mm});
            skLineSegment(sketch, "E1209", {"start": v(-20.3, -4.3) * mm, "end": v(-20.28, -4.46) * mm});
            skLineSegment(sketch, "E1210", {"start": v(-20.28, -4.46) * mm, "end": v(-20.24, -4.6) * mm});
            skLineSegment(sketch, "E1211", {"start": v(-20.24, -4.6) * mm, "end": v(-20.21, -4.76) * mm});
            skLineSegment(sketch, "E1212", {"start": v(-20.21, -4.76) * mm, "end": v(-20.18, -4.9) * mm});
            skLineSegment(sketch, "E1213", {"start": v(-20.18, -4.9) * mm, "end": v(-20.15, -5.06) * mm});
            skLineSegment(sketch, "E1214", {"start": v(-20.15, -5.06) * mm, "end": v(-20.14, -5.1) * mm});
            skLineSegment(sketch, "E1215", {"start": v(-20.14, -5.1) * mm, "end": v(-20.29, -5.13) * mm});
            skLineSegment(sketch, "E1216", {"start": v(-20.29, -5.13) * mm, "end": v(-20.43, -5.17) * mm});
            skLineSegment(sketch, "E1217", {"start": v(-20.43, -5.17) * mm, "end": v(-20.58, -5.21) * mm});
            skLineSegment(sketch, "E1218", {"start": v(-20.58, -5.21) * mm, "end": v(-20.73, -5.25) * mm});
            skLineSegment(sketch, "E1219", {"start": v(-20.73, -5.25) * mm, "end": v(-20.88, -5.29) * mm});
            skLineSegment(sketch, "E1220", {"start": v(-20.88, -5.29) * mm, "end": v(-21.03, -5.33) * mm});
            skLineSegment(sketch, "E1221", {"start": v(-21.03, -5.33) * mm, "end": v(-21.18, -5.37) * mm});
            skLineSegment(sketch, "E1222", {"start": v(-21.18, -5.37) * mm, "end": v(-21.33, -5.4) * mm});
            skLineSegment(sketch, "E1223", {"start": v(-21.33, -5.4) * mm, "end": v(-21.48, -5.45) * mm});
            skLineSegment(sketch, "E1224", {"start": v(-21.48, -5.45) * mm, "end": v(-21.62, -5.48) * mm});
            skLineSegment(sketch, "E1225", {"start": v(-21.62, -5.48) * mm, "end": v(-21.77, -5.52) * mm});
            skLineSegment(sketch, "E1226", {"start": v(-21.77, -5.52) * mm, "end": v(-21.92, -5.56) * mm});
            skLineSegment(sketch, "E1227", {"start": v(-21.92, -5.56) * mm, "end": v(-22.08, -5.6) * mm});
            skLineSegment(sketch, "E1228", {"start": v(-22.08, -5.6) * mm, "end": v(-22.23, -5.68) * mm});
            skLineSegment(sketch, "E1229", {"start": v(-22.23, -5.68) * mm, "end": v(-22.35, -5.79) * mm});
            skLineSegment(sketch, "E1230", {"start": v(-22.35, -5.79) * mm, "end": v(-22.44, -5.92) * mm});
            skLineSegment(sketch, "E1231", {"start": v(-22.44, -5.92) * mm, "end": v(-22.5, -6.08) * mm});
            skLineSegment(sketch, "E1232", {"start": v(-22.5, -6.08) * mm, "end": v(-22.5, -6.24) * mm});
            skLineSegment(sketch, "E1233", {"start": v(-22.5, -6.24) * mm, "end": v(-22.47, -6.4) * mm});
            skLineSegment(sketch, "E1234", {"start": v(-22.47, -6.4) * mm, "end": v(-22.4, -6.55) * mm});
            skLineSegment(sketch, "E1235", {"start": v(-22.4, -6.55) * mm, "end": v(-22.29, -6.68) * mm});
            skLineSegment(sketch, "E1236", {"start": v(-22.29, -6.68) * mm, "end": v(-22.15, -6.76) * mm});
            skLineSegment(sketch, "E1237", {"start": v(-22.15, -6.76) * mm, "end": v(-22, -6.81) * mm});
            skLineSegment(sketch, "E1238", {"start": v(-22, -6.81) * mm, "end": v(-21.83, -6.82) * mm});
            skLineSegment(sketch, "E1239", {"start": v(-21.83, -6.82) * mm, "end": v(-21.7, -6.8) * mm});
            skLineSegment(sketch, "E1240", {"start": v(-21.7, -6.8) * mm, "end": v(-21.55, -6.75) * mm});
            skLineSegment(sketch, "E1241", {"start": v(-21.55, -6.75) * mm, "end": v(-21.4, -6.7) * mm});
            skLineSegment(sketch, "E1242", {"start": v(-21.4, -6.7) * mm, "end": v(-21.26, -6.65) * mm});
            skLineSegment(sketch, "E1243", {"start": v(-21.26, -6.65) * mm, "end": v(-21.11, -6.6) * mm});
            skLineSegment(sketch, "E1244", {"start": v(-21.11, -6.6) * mm, "end": v(-20.97, -6.56) * mm});
            skLineSegment(sketch, "E1245", {"start": v(-20.97, -6.56) * mm, "end": v(-20.82, -6.51) * mm});
            skLineSegment(sketch, "E1246", {"start": v(-20.82, -6.51) * mm, "end": v(-20.67, -6.46) * mm});
            skLineSegment(sketch, "E1247", {"start": v(-20.67, -6.46) * mm, "end": v(-20.53, -6.42) * mm});
            skLineSegment(sketch, "E1248", {"start": v(-20.53, -6.42) * mm, "end": v(-20.38, -6.37) * mm});
            skLineSegment(sketch, "E1249", {"start": v(-20.38, -6.37) * mm, "end": v(-20.24, -6.32) * mm});
            skLineSegment(sketch, "E1250", {"start": v(-20.24, -6.32) * mm, "end": v(-20.1, -6.27) * mm});
            skLineSegment(sketch, "E1251", {"start": v(-20.1, -6.27) * mm, "end": v(-19.94, -6.23) * mm});
            skLineSegment(sketch, "E1252", {"start": v(-19.94, -6.23) * mm, "end": v(-19.82, -6.19) * mm});
            skLineSegment(sketch, "E1253", {"start": v(-19.82, -6.19) * mm, "end": v(-19.76, -6.33) * mm});
            skLineSegment(sketch, "E1254", {"start": v(-19.76, -6.33) * mm, "end": v(-19.71, -6.47) * mm});
            skLineSegment(sketch, "E1255", {"start": v(-19.71, -6.47) * mm, "end": v(-19.66, -6.62) * mm});
            skLineSegment(sketch, "E1256", {"start": v(-19.66, -6.62) * mm, "end": v(-19.6, -6.76) * mm});
            skLineSegment(sketch, "E1257", {"start": v(-19.6, -6.76) * mm, "end": v(-19.55, -6.9) * mm});
            skLineSegment(sketch, "E1258", {"start": v(-19.55, -6.9) * mm, "end": v(-19.5, -7.05) * mm});
            skLineSegment(sketch, "E1259", {"start": v(-19.5, -7.05) * mm, "end": v(-19.44, -7.19) * mm});
            skLineSegment(sketch, "E1260", {"start": v(-19.44, -7.19) * mm, "end": v(-19.39, -7.33) * mm});
            skLineSegment(sketch, "E1261", {"start": v(-19.39, -7.33) * mm, "end": v(-19.34, -7.48) * mm});
            skLineSegment(sketch, "E1262", {"start": v(-19.34, -7.48) * mm, "end": v(-19.28, -7.62) * mm});
            skLineSegment(sketch, "E1263", {"start": v(-19.28, -7.62) * mm, "end": v(-19.23, -7.76) * mm});
            skLineSegment(sketch, "E1264", {"start": v(-19.23, -7.76) * mm, "end": v(-19.22, -7.8) * mm});
            skLineSegment(sketch, "E1265", {"start": v(-19.22, -7.8) * mm, "end": v(-19.36, -7.86) * mm});
            skLineSegment(sketch, "E1266", {"start": v(-19.36, -7.86) * mm, "end": v(-19.5, -7.92) * mm});
            skLineSegment(sketch, "E1267", {"start": v(-19.5, -7.92) * mm, "end": v(-19.64, -7.98) * mm});
            skLineSegment(sketch, "E1268", {"start": v(-19.64, -7.98) * mm, "end": v(-19.78, -8.04) * mm});
            skLineSegment(sketch, "E1269", {"start": v(-19.78, -8.04) * mm, "end": v(-19.92, -8.1) * mm});
            skLineSegment(sketch, "E1270", {"start": v(-19.92, -8.1) * mm, "end": v(-20.07, -8.16) * mm});
            skLineSegment(sketch, "E1271", {"start": v(-20.07, -8.16) * mm, "end": v(-20.2, -8.22) * mm});
            skLineSegment(sketch, "E1272", {"start": v(-20.2, -8.22) * mm, "end": v(-20.35, -8.28) * mm});
            skLineSegment(sketch, "E1273", {"start": v(-20.35, -8.28) * mm, "end": v(-20.5, -8.34) * mm});
            skLineSegment(sketch, "E1274", {"start": v(-20.5, -8.34) * mm, "end": v(-20.63, -8.4) * mm});
            skLineSegment(sketch, "E1275", {"start": v(-20.63, -8.4) * mm, "end": v(-20.77, -8.46) * mm});
            skLineSegment(sketch, "E1276", {"start": v(-20.77, -8.46) * mm, "end": v(-20.92, -8.52) * mm});
            skLineSegment(sketch, "E1277", {"start": v(-20.92, -8.52) * mm, "end": v(-21.07, -8.58) * mm});
            skLineSegment(sketch, "E1278", {"start": v(-21.07, -8.58) * mm, "end": v(-21.2, -8.67) * mm});
            skLineSegment(sketch, "E1279", {"start": v(-21.2, -8.67) * mm, "end": v(-21.31, -8.8) * mm});
            skLineSegment(sketch, "E1280", {"start": v(-21.31, -8.8) * mm, "end": v(-21.38, -8.95) * mm});
            skLineSegment(sketch, "E1281", {"start": v(-21.38, -8.95) * mm, "end": v(-21.41, -9.11) * mm});
            skLineSegment(sketch, "E1282", {"start": v(-21.41, -9.11) * mm, "end": v(-21.4, -9.27) * mm});
            skLineSegment(sketch, "E1283", {"start": v(-21.4, -9.27) * mm, "end": v(-21.35, -9.4) * mm});
            skLineSegment(sketch, "E1284", {"start": v(-21.35, -9.4) * mm, "end": v(-21.27, -9.54) * mm});
            skLineSegment(sketch, "E1285", {"start": v(-21.27, -9.54) * mm, "end": v(-21.15, -9.65) * mm});
            skLineSegment(sketch, "E1286", {"start": v(-21.15, -9.65) * mm, "end": v(-21, -9.73) * mm});
            skLineSegment(sketch, "E1287", {"start": v(-21, -9.73) * mm, "end": v(-20.84, -9.76) * mm});
            skLineSegment(sketch, "E1288", {"start": v(-20.84, -9.76) * mm, "end": v(-20.67, -9.75) * mm});
            skLineSegment(sketch, "E1289", {"start": v(-20.67, -9.75) * mm, "end": v(-20.52, -9.7) * mm});
            skLineSegment(sketch, "E1290", {"start": v(-20.52, -9.7) * mm, "end": v(-20.38, -9.64) * mm});
            skLineSegment(sketch, "E1291", {"start": v(-20.38, -9.64) * mm, "end": v(-20.24, -9.57) * mm});
            skLineSegment(sketch, "E1292", {"start": v(-20.24, -9.57) * mm, "end": v(-20.1, -9.5) * mm});
            skLineSegment(sketch, "E1293", {"start": v(-20.1, -9.5) * mm, "end": v(-19.97, -9.43) * mm});
            skLineSegment(sketch, "E1294", {"start": v(-19.97, -9.43) * mm, "end": v(-19.83, -9.37) * mm});
            skLineSegment(sketch, "E1295", {"start": v(-19.83, -9.37) * mm, "end": v(-19.69, -9.3) * mm});
            skLineSegment(sketch, "E1296", {"start": v(-19.69, -9.3) * mm, "end": v(-19.55, -9.23) * mm});
            skLineSegment(sketch, "E1297", {"start": v(-19.55, -9.23) * mm, "end": v(-19.41, -9.16) * mm});
            skLineSegment(sketch, "E1298", {"start": v(-19.41, -9.16) * mm, "end": v(-19.28, -9.1) * mm});
            skLineSegment(sketch, "E1299", {"start": v(-19.28, -9.1) * mm, "end": v(-19.14, -9.03) * mm});
            skLineSegment(sketch, "E1300", {"start": v(-19.14, -9.03) * mm, "end": v(-19, -8.96) * mm});
            skLineSegment(sketch, "E1301", {"start": v(-19, -8.96) * mm, "end": v(-18.86, -8.9) * mm});
            skLineSegment(sketch, "E1302", {"start": v(-18.86, -8.9) * mm, "end": v(-18.74, -8.83) * mm});
            skLineSegment(sketch, "E1303", {"start": v(-18.74, -8.83) * mm, "end": v(-18.67, -8.97) * mm});
            skLineSegment(sketch, "E1304", {"start": v(-18.67, -8.97) * mm, "end": v(-18.6, -9.1) * mm});
            skLineSegment(sketch, "E1305", {"start": v(-18.6, -9.1) * mm, "end": v(-18.52, -9.24) * mm});
            skLineSegment(sketch, "E1306", {"start": v(-18.52, -9.24) * mm, "end": v(-18.45, -9.37) * mm});
            skLineSegment(sketch, "E1307", {"start": v(-18.45, -9.37) * mm, "end": v(-18.38, -9.5) * mm});
            skLineSegment(sketch, "E1308", {"start": v(-18.38, -9.5) * mm, "end": v(-18.3, -9.64) * mm});
            skLineSegment(sketch, "E1309", {"start": v(-18.3, -9.64) * mm, "end": v(-18.23, -9.77) * mm});
            skLineSegment(sketch, "E1310", {"start": v(-18.23, -9.77) * mm, "end": v(-18.16, -9.9) * mm});
            skLineSegment(sketch, "E1311", {"start": v(-18.16, -9.9) * mm, "end": v(-18.08, -10.04) * mm});
            skLineSegment(sketch, "E1312", {"start": v(-18.08, -10.04) * mm, "end": v(-18, -10.18) * mm});
            skLineSegment(sketch, "E1313", {"start": v(-18, -10.18) * mm, "end": v(-17.94, -10.31) * mm});
            skLineSegment(sketch, "E1314", {"start": v(-17.94, -10.31) * mm, "end": v(-17.92, -10.34) * mm});
            skLineSegment(sketch, "E1315", {"start": v(-17.92, -10.34) * mm, "end": v(-18.05, -10.42) * mm});
            skLineSegment(sketch, "E1316", {"start": v(-18.05, -10.42) * mm, "end": v(-18.18, -10.5) * mm});
            skLineSegment(sketch, "E1317", {"start": v(-18.18, -10.5) * mm, "end": v(-18.31, -10.58) * mm});
            skLineSegment(sketch, "E1318", {"start": v(-18.31, -10.58) * mm, "end": v(-18.44, -10.66) * mm});
            skLineSegment(sketch, "E1319", {"start": v(-18.44, -10.66) * mm, "end": v(-18.58, -10.74) * mm});
            skLineSegment(sketch, "E1320", {"start": v(-18.58, -10.74) * mm, "end": v(-18.7, -10.82) * mm});
            skLineSegment(sketch, "E1321", {"start": v(-18.7, -10.82) * mm, "end": v(-18.84, -10.9) * mm});
            skLineSegment(sketch, "E1322", {"start": v(-18.84, -10.9) * mm, "end": v(-18.97, -10.98) * mm});
            skLineSegment(sketch, "E1323", {"start": v(-18.97, -10.98) * mm, "end": v(-19.1, -11.06) * mm});
            skLineSegment(sketch, "E1324", {"start": v(-19.1, -11.06) * mm, "end": v(-19.24, -11.14) * mm});
            skLineSegment(sketch, "E1325", {"start": v(-19.24, -11.14) * mm, "end": v(-19.37, -11.22) * mm});
            skLineSegment(sketch, "E1326", {"start": v(-19.37, -11.22) * mm, "end": v(-19.5, -11.3) * mm});
            skLineSegment(sketch, "E1327", {"start": v(-19.5, -11.3) * mm, "end": v(-19.64, -11.38) * mm});
            skLineSegment(sketch, "E1328", {"start": v(-19.64, -11.38) * mm, "end": v(-19.76, -11.5) * mm});
            skLineSegment(sketch, "E1329", {"start": v(-19.76, -11.5) * mm, "end": v(-19.85, -11.63) * mm});
            skLineSegment(sketch, "E1330", {"start": v(-19.85, -11.63) * mm, "end": v(-19.9, -11.79) * mm});
            skLineSegment(sketch, "E1331", {"start": v(-19.9, -11.79) * mm, "end": v(-19.9, -11.95) * mm});
            skLineSegment(sketch, "E1332", {"start": v(-19.9, -11.95) * mm, "end": v(-19.87, -12.11) * mm});
            skLineSegment(sketch, "E1333", {"start": v(-19.87, -12.11) * mm, "end": v(-19.8, -12.23) * mm});
            skLineSegment(sketch, "E1334", {"start": v(-19.8, -12.23) * mm, "end": v(-19.7, -12.36) * mm});
            skLineSegment(sketch, "E1335", {"start": v(-19.7, -12.36) * mm, "end": v(-19.57, -12.45) * mm});
            skLineSegment(sketch, "E1336", {"start": v(-19.57, -12.45) * mm, "end": v(-19.41, -12.5) * mm});
            skLineSegment(sketch, "E1337", {"start": v(-19.41, -12.5) * mm, "end": v(-19.25, -12.52) * mm});
            skLineSegment(sketch, "E1338", {"start": v(-19.25, -12.52) * mm, "end": v(-19.08, -12.49) * mm});
            skLineSegment(sketch, "E1339", {"start": v(-19.08, -12.49) * mm, "end": v(-18.94, -12.42) * mm});
            skLineSegment(sketch, "E1340", {"start": v(-18.94, -12.42) * mm, "end": v(-18.8, -12.33) * mm});
            skLineSegment(sketch, "E1341", {"start": v(-18.8, -12.33) * mm, "end": v(-18.68, -12.24) * mm});
            skLineSegment(sketch, "E1342", {"start": v(-18.68, -12.24) * mm, "end": v(-18.56, -12.16) * mm});
            skLineSegment(sketch, "E1343", {"start": v(-18.56, -12.16) * mm, "end": v(-18.43, -12.07) * mm});
            skLineSegment(sketch, "E1344", {"start": v(-18.43, -12.07) * mm, "end": v(-18.3, -11.98) * mm});
            skLineSegment(sketch, "E1345", {"start": v(-18.3, -11.98) * mm, "end": v(-18.17, -11.9) * mm});
            skLineSegment(sketch, "E1346", {"start": v(-18.17, -11.9) * mm, "end": v(-18.05, -11.8) * mm});
            skLineSegment(sketch, "E1347", {"start": v(-18.05, -11.8) * mm, "end": v(-17.92, -11.72) * mm});
            skLineSegment(sketch, "E1348", {"start": v(-17.92, -11.72) * mm, "end": v(-17.8, -11.63) * mm});
            skLineSegment(sketch, "E1349", {"start": v(-17.8, -11.63) * mm, "end": v(-17.67, -11.55) * mm});
            skLineSegment(sketch, "E1350", {"start": v(-17.67, -11.55) * mm, "end": v(-17.54, -11.46) * mm});
            skLineSegment(sketch, "E1351", {"start": v(-17.54, -11.46) * mm, "end": v(-17.41, -11.37) * mm});
            skLineSegment(sketch, "E1352", {"start": v(-17.41, -11.37) * mm, "end": v(-17.3, -11.3) * mm});
            skLineSegment(sketch, "E1353", {"start": v(-17.3, -11.3) * mm, "end": v(-17.21, -11.42) * mm});
            skLineSegment(sketch, "E1354", {"start": v(-17.21, -11.42) * mm, "end": v(-17.12, -11.54) * mm});
            skLineSegment(sketch, "E1355", {"start": v(-17.12, -11.54) * mm, "end": v(-17.03, -11.67) * mm});
            skLineSegment(sketch, "E1356", {"start": v(-17.03, -11.67) * mm, "end": v(-16.94, -11.79) * mm});
            skLineSegment(sketch, "E1357", {"start": v(-16.94, -11.79) * mm, "end": v(-16.84, -11.91) * mm});
            skLineSegment(sketch, "E1358", {"start": v(-16.84, -11.91) * mm, "end": v(-16.75, -12.04) * mm});
            skLineSegment(sketch, "E1359", {"start": v(-16.75, -12.04) * mm, "end": v(-16.66, -12.16) * mm});
            skLineSegment(sketch, "E1360", {"start": v(-16.66, -12.16) * mm, "end": v(-16.57, -12.28) * mm});
            skLineSegment(sketch, "E1361", {"start": v(-16.57, -12.28) * mm, "end": v(-16.48, -12.4) * mm});
            skLineSegment(sketch, "E1362", {"start": v(-16.48, -12.4) * mm, "end": v(-16.39, -12.53) * mm});
            skLineSegment(sketch, "E1363", {"start": v(-16.39, -12.53) * mm, "end": v(-16.3, -12.65) * mm});
            skLineSegment(sketch, "E1364", {"start": v(-16.3, -12.65) * mm, "end": v(-16.27, -12.68) * mm});
            skLineSegment(sketch, "E1365", {"start": v(-16.27, -12.68) * mm, "end": v(-16.4, -12.77) * mm});
            skLineSegment(sketch, "E1366", {"start": v(-16.4, -12.77) * mm, "end": v(-16.5, -12.87) * mm});
            skLineSegment(sketch, "E1367", {"start": v(-16.5, -12.87) * mm, "end": v(-16.63, -12.97) * mm});
            skLineSegment(sketch, "E1368", {"start": v(-16.63, -12.97) * mm, "end": v(-16.75, -13.07) * mm});
            skLineSegment(sketch, "E1369", {"start": v(-16.75, -13.07) * mm, "end": v(-16.87, -13.16) * mm});
            skLineSegment(sketch, "E1370", {"start": v(-16.87, -13.16) * mm, "end": v(-16.99, -13.26) * mm});
            skLineSegment(sketch, "E1371", {"start": v(-16.99, -13.26) * mm, "end": v(-17.1, -13.36) * mm});
            skLineSegment(sketch, "E1372", {"start": v(-17.1, -13.36) * mm, "end": v(-17.22, -13.46) * mm});
            skLineSegment(sketch, "E1373", {"start": v(-17.22, -13.46) * mm, "end": v(-17.34, -13.55) * mm});
            skLineSegment(sketch, "E1374", {"start": v(-17.34, -13.55) * mm, "end": v(-17.46, -13.65) * mm});
            skLineSegment(sketch, "E1375", {"start": v(-17.46, -13.65) * mm, "end": v(-17.58, -13.75) * mm});
            skLineSegment(sketch, "E1376", {"start": v(-17.58, -13.75) * mm, "end": v(-17.7, -13.85) * mm});
            skLineSegment(sketch, "E1377", {"start": v(-17.7, -13.85) * mm, "end": v(-17.83, -13.95) * mm});
            skLineSegment(sketch, "E1378", {"start": v(-17.83, -13.95) * mm, "end": v(-17.93, -14.08) * mm});
            skLineSegment(sketch, "E1379", {"start": v(-17.93, -14.08) * mm, "end": v(-18, -14.23) * mm});
            skLineSegment(sketch, "E1380", {"start": v(-18, -14.23) * mm, "end": v(-18.03, -14.4) * mm});
            skLineSegment(sketch, "E1381", {"start": v(-18.03, -14.4) * mm, "end": v(-18, -14.55) * mm});
            skLineSegment(sketch, "E1382", {"start": v(-18, -14.55) * mm, "end": v(-17.95, -14.7) * mm});
            skLineSegment(sketch, "E1383", {"start": v(-17.95, -14.7) * mm, "end": v(-17.87, -14.82) * mm});
            skLineSegment(sketch, "E1384", {"start": v(-17.87, -14.82) * mm, "end": v(-17.75, -14.93) * mm});
            skLineSegment(sketch, "E1385", {"start": v(-17.75, -14.93) * mm, "end": v(-17.6, -15) * mm});
            skLineSegment(sketch, "E1386", {"start": v(-17.6, -15) * mm, "end": v(-17.44, -15.03) * mm});
            skLineSegment(sketch, "E1387", {"start": v(-17.44, -15.03) * mm, "end": v(-17.28, -15.02) * mm});
            skLineSegment(sketch, "E1388", {"start": v(-17.28, -15.02) * mm, "end": v(-17.12, -14.97) * mm});
            skLineSegment(sketch, "E1389", {"start": v(-17.12, -14.97) * mm, "end": v(-16.98, -14.87) * mm});
            skLineSegment(sketch, "E1390", {"start": v(-16.98, -14.87) * mm, "end": v(-16.87, -14.77) * mm});
            skLineSegment(sketch, "E1391", {"start": v(-16.87, -14.77) * mm, "end": v(-16.76, -14.67) * mm});
            skLineSegment(sketch, "E1392", {"start": v(-16.76, -14.67) * mm, "end": v(-16.64, -14.56) * mm});
            skLineSegment(sketch, "E1393", {"start": v(-16.64, -14.56) * mm, "end": v(-16.53, -14.46) * mm});
            skLineSegment(sketch, "E1394", {"start": v(-16.53, -14.46) * mm, "end": v(-16.42, -14.35) * mm});
            skLineSegment(sketch, "E1395", {"start": v(-16.42, -14.35) * mm, "end": v(-16.3, -14.25) * mm});
            skLineSegment(sketch, "E1396", {"start": v(-16.3, -14.25) * mm, "end": v(-16.2, -14.15) * mm});
            skLineSegment(sketch, "E1397", {"start": v(-16.2, -14.15) * mm, "end": v(-16.08, -14.04) * mm});
            skLineSegment(sketch, "E1398", {"start": v(-16.08, -14.04) * mm, "end": v(-15.96, -13.94) * mm});
            skLineSegment(sketch, "E1399", {"start": v(-15.96, -13.94) * mm, "end": v(-15.85, -13.83) * mm});
            skLineSegment(sketch, "E1400", {"start": v(-15.85, -13.83) * mm, "end": v(-15.74, -13.73) * mm});
            skLineSegment(sketch, "E1401", {"start": v(-15.74, -13.73) * mm, "end": v(-15.62, -13.63) * mm});
            skLineSegment(sketch, "E1402", {"start": v(-15.62, -13.63) * mm, "end": v(-15.53, -13.54) * mm});
            skLineSegment(sketch, "E1403", {"start": v(-15.53, -13.54) * mm, "end": v(-15.42, -13.65) * mm});
            skLineSegment(sketch, "E1404", {"start": v(-15.42, -13.65) * mm, "end": v(-15.31, -13.75) * mm});
            skLineSegment(sketch, "E1405", {"start": v(-15.31, -13.75) * mm, "end": v(-15.2, -13.86) * mm});
            skLineSegment(sketch, "E1406", {"start": v(-15.2, -13.86) * mm, "end": v(-15.1, -13.97) * mm});
            skLineSegment(sketch, "E1407", {"start": v(-15.1, -13.97) * mm, "end": v(-14.99, -14.08) * mm});
            skLineSegment(sketch, "E1408", {"start": v(-14.99, -14.08) * mm, "end": v(-14.88, -14.19) * mm});
            skLineSegment(sketch, "E1409", {"start": v(-14.88, -14.19) * mm, "end": v(-14.77, -14.3) * mm});
            skLineSegment(sketch, "E1410", {"start": v(-14.77, -14.3) * mm, "end": v(-14.66, -14.4) * mm});
            skLineSegment(sketch, "E1411", {"start": v(-14.66, -14.4) * mm, "end": v(-14.55, -14.51) * mm});
            skLineSegment(sketch, "E1412", {"start": v(-14.55, -14.51) * mm, "end": v(-14.44, -14.62) * mm});
            skLineSegment(sketch, "E1413", {"start": v(-14.44, -14.62) * mm, "end": v(-14.34, -14.73) * mm});
            skLineSegment(sketch, "E1414", {"start": v(-14.34, -14.73) * mm, "end": v(-14.31, -14.75) * mm});
            skLineSegment(sketch, "E1415", {"start": v(-14.31, -14.75) * mm, "end": v(-14.41, -14.87) * mm});
            skLineSegment(sketch, "E1416", {"start": v(-14.41, -14.87) * mm, "end": v(-14.52, -14.98) * mm});
            skLineSegment(sketch, "E1417", {"start": v(-14.52, -14.98) * mm, "end": v(-14.62, -15.1) * mm});
            skLineSegment(sketch, "E1418", {"start": v(-14.62, -15.1) * mm, "end": v(-14.73, -15.2) * mm});
            skLineSegment(sketch, "E1419", {"start": v(-14.73, -15.2) * mm, "end": v(-14.83, -15.32) * mm});
            skLineSegment(sketch, "E1420", {"start": v(-14.83, -15.32) * mm, "end": v(-14.93, -15.43) * mm});
            skLineSegment(sketch, "E1421", {"start": v(-14.93, -15.43) * mm, "end": v(-15.04, -15.55) * mm});
            skLineSegment(sketch, "E1422", {"start": v(-15.04, -15.55) * mm, "end": v(-15.14, -15.66) * mm});
            skLineSegment(sketch, "E1423", {"start": v(-15.14, -15.66) * mm, "end": v(-15.25, -15.77) * mm});
            skLineSegment(sketch, "E1424", {"start": v(-15.25, -15.77) * mm, "end": v(-15.35, -15.89) * mm});
            skLineSegment(sketch, "E1425", {"start": v(-15.35, -15.89) * mm, "end": v(-15.45, -16) * mm});
            skLineSegment(sketch, "E1426", {"start": v(-15.45, -16) * mm, "end": v(-15.56, -16.11) * mm});
            skLineSegment(sketch, "E1427", {"start": v(-15.56, -16.11) * mm, "end": v(-15.67, -16.24) * mm});
            skLineSegment(sketch, "E1428", {"start": v(-15.67, -16.24) * mm, "end": v(-15.75, -16.38) * mm});
            skLineSegment(sketch, "E1429", {"start": v(-15.75, -16.38) * mm, "end": v(-15.8, -16.54) * mm});
            skLineSegment(sketch, "E1430", {"start": v(-15.8, -16.54) * mm, "end": v(-15.8, -16.7) * mm});
            skLineSegment(sketch, "E1431", {"start": v(-15.8, -16.7) * mm, "end": v(-15.76, -16.86) * mm});
            skLineSegment(sketch, "E1432", {"start": v(-15.76, -16.86) * mm, "end": v(-15.68, -17) * mm});
            skLineSegment(sketch, "E1433", {"start": v(-15.68, -17) * mm, "end": v(-15.6, -17.1) * mm});
            skLineSegment(sketch, "E1434", {"start": v(-15.6, -17.1) * mm, "end": v(-15.45, -17.19) * mm});
            skLineSegment(sketch, "E1435", {"start": v(-15.45, -17.19) * mm, "end": v(-15.3, -17.24) * mm});
            skLineSegment(sketch, "E1436", {"start": v(-15.3, -17.24) * mm, "end": v(-15.13, -17.25) * mm});
            skLineSegment(sketch, "E1437", {"start": v(-15.13, -17.25) * mm, "end": v(-14.97, -17.22) * mm});
            skLineSegment(sketch, "E1438", {"start": v(-14.97, -17.22) * mm, "end": v(-14.82, -17.14) * mm});
            skLineSegment(sketch, "E1439", {"start": v(-14.82, -17.14) * mm, "end": v(-14.7, -17.03) * mm});
            skLineSegment(sketch, "E1440", {"start": v(-14.7, -17.03) * mm, "end": v(-14.6, -16.91) * mm});
            skLineSegment(sketch, "E1441", {"start": v(-14.6, -16.91) * mm, "end": v(-14.5, -16.8) * mm});
            skLineSegment(sketch, "E1442", {"start": v(-14.5, -16.8) * mm, "end": v(-14.41, -16.67) * mm});
            skLineSegment(sketch, "E1443", {"start": v(-14.41, -16.67) * mm, "end": v(-14.31, -16.55) * mm});
            skLineSegment(sketch, "E1444", {"start": v(-14.31, -16.55) * mm, "end": v(-14.22, -16.44) * mm});
            skLineSegment(sketch, "E1445", {"start": v(-14.22, -16.44) * mm, "end": v(-14.12, -16.32) * mm});
            skLineSegment(sketch, "E1446", {"start": v(-14.12, -16.32) * mm, "end": v(-14.02, -16.2) * mm});
            skLineSegment(sketch, "E1447", {"start": v(-14.02, -16.2) * mm, "end": v(-13.92, -16.08) * mm});
            skLineSegment(sketch, "E1448", {"start": v(-13.92, -16.08) * mm, "end": v(-13.83, -15.96) * mm});
            skLineSegment(sketch, "E1449", {"start": v(-13.83, -15.96) * mm, "end": v(-13.73, -15.84) * mm});
            skLineSegment(sketch, "E1450", {"start": v(-13.73, -15.84) * mm, "end": v(-13.63, -15.72) * mm});
            skLineSegment(sketch, "E1451", {"start": v(-13.63, -15.72) * mm, "end": v(-13.53, -15.6) * mm});
            skLineSegment(sketch, "E1452", {"start": v(-13.53, -15.6) * mm, "end": v(-13.45, -15.5) * mm});
            skLineSegment(sketch, "E1453", {"start": v(-13.45, -15.5) * mm, "end": v(-13.33, -15.6) * mm});
            skLineSegment(sketch, "E1454", {"start": v(-13.33, -15.6) * mm, "end": v(-13.2, -15.68) * mm});
            skLineSegment(sketch, "E1455", {"start": v(-13.2, -15.68) * mm, "end": v(-13.08, -15.77) * mm});
            skLineSegment(sketch, "E1456", {"start": v(-13.08, -15.77) * mm, "end": v(-12.96, -15.87) * mm});
            skLineSegment(sketch, "E1457", {"start": v(-12.96, -15.87) * mm, "end": v(-12.84, -15.96) * mm});
            skLineSegment(sketch, "E1458", {"start": v(-12.84, -15.96) * mm, "end": v(-12.71, -16.05) * mm});
            skLineSegment(sketch, "E1459", {"start": v(-12.71, -16.05) * mm, "end": v(-12.6, -16.14) * mm});
            skLineSegment(sketch, "E1460", {"start": v(-12.6, -16.14) * mm, "end": v(-12.47, -16.23) * mm});
            skLineSegment(sketch, "E1461", {"start": v(-12.47, -16.23) * mm, "end": v(-12.35, -16.32) * mm});
            skLineSegment(sketch, "E1462", {"start": v(-12.35, -16.32) * mm, "end": v(-12.22, -16.42) * mm});
            skLineSegment(sketch, "E1463", {"start": v(-12.22, -16.42) * mm, "end": v(-12.1, -16.5) * mm});
            skLineSegment(sketch, "E1464", {"start": v(-12.1, -16.5) * mm, "end": v(-12.07, -16.53) * mm});
            skLineSegment(sketch, "E1465", {"start": v(-12.07, -16.53) * mm, "end": v(-12.16, -16.66) * mm});
            skLineSegment(sketch, "E1466", {"start": v(-12.16, -16.66) * mm, "end": v(-12.25, -16.78) * mm});
            skLineSegment(sketch, "E1467", {"start": v(-12.25, -16.78) * mm, "end": v(-12.33, -16.91) * mm});
            skLineSegment(sketch, "E1468", {"start": v(-12.33, -16.91) * mm, "end": v(-12.42, -17.04) * mm});
            skLineSegment(sketch, "E1469", {"start": v(-12.42, -17.04) * mm, "end": v(-12.5, -17.16) * mm});
            skLineSegment(sketch, "E1470", {"start": v(-12.5, -17.16) * mm, "end": v(-12.6, -17.3) * mm});
            skLineSegment(sketch, "E1471", {"start": v(-12.6, -17.3) * mm, "end": v(-12.68, -17.42) * mm});
            skLineSegment(sketch, "E1472", {"start": v(-12.68, -17.42) * mm, "end": v(-12.77, -17.54) * mm});
            skLineSegment(sketch, "E1473", {"start": v(-12.77, -17.54) * mm, "end": v(-12.85, -17.67) * mm});
            skLineSegment(sketch, "E1474", {"start": v(-12.85, -17.67) * mm, "end": v(-12.94, -17.8) * mm});
            skLineSegment(sketch, "E1475", {"start": v(-12.94, -17.8) * mm, "end": v(-13.03, -17.93) * mm});
            skLineSegment(sketch, "E1476", {"start": v(-13.03, -17.93) * mm, "end": v(-13.11, -18.05) * mm});
            skLineSegment(sketch, "E1477", {"start": v(-13.11, -18.05) * mm, "end": v(-13.2, -18.2) * mm});
            skLineSegment(sketch, "E1478", {"start": v(-13.2, -18.2) * mm, "end": v(-13.27, -18.34) * mm});
            skLineSegment(sketch, "E1479", {"start": v(-13.27, -18.34) * mm, "end": v(-13.3, -18.5) * mm});
            skLineSegment(sketch, "E1480", {"start": v(-13.3, -18.5) * mm, "end": v(-13.27, -18.67) * mm});
            skLineSegment(sketch, "E1481", {"start": v(-13.27, -18.67) * mm, "end": v(-13.2, -18.82) * mm});
            skLineSegment(sketch, "E1482", {"start": v(-13.2, -18.82) * mm, "end": v(-13.1, -18.95) * mm});
            skLineSegment(sketch, "E1483", {"start": v(-13.1, -18.95) * mm, "end": v(-13, -19.03) * mm});
            skLineSegment(sketch, "E1484", {"start": v(-13, -19.03) * mm, "end": v(-12.86, -19.1) * mm});
            skLineSegment(sketch, "E1485", {"start": v(-12.86, -19.1) * mm, "end": v(-12.7, -19.13) * mm});
            skLineSegment(sketch, "E1486", {"start": v(-12.7, -19.13) * mm, "end": v(-12.53, -19.12) * mm});
            skLineSegment(sketch, "E1487", {"start": v(-12.53, -19.12) * mm, "end": v(-12.38, -19.06) * mm});
            skLineSegment(sketch, "E1488", {"start": v(-12.38, -19.06) * mm, "end": v(-12.24, -18.97) * mm});
            skLineSegment(sketch, "E1489", {"start": v(-12.24, -18.97) * mm, "end": v(-12.14, -18.84) * mm});
            skLineSegment(sketch, "E1490", {"start": v(-12.14, -18.84) * mm, "end": v(-12.06, -18.7) * mm});
            skLineSegment(sketch, "E1491", {"start": v(-12.06, -18.7) * mm, "end": v(-11.98, -18.58) * mm});
            skLineSegment(sketch, "E1492", {"start": v(-11.98, -18.58) * mm, "end": v(-11.9, -18.44) * mm});
            skLineSegment(sketch, "E1493", {"start": v(-11.9, -18.44) * mm, "end": v(-11.82, -18.31) * mm});
            skLineSegment(sketch, "E1494", {"start": v(-11.82, -18.31) * mm, "end": v(-11.74, -18.18) * mm});
            skLineSegment(sketch, "E1495", {"start": v(-11.74, -18.18) * mm, "end": v(-11.66, -18.05) * mm});
            skLineSegment(sketch, "E1496", {"start": v(-11.66, -18.05) * mm, "end": v(-11.58, -17.92) * mm});
            skLineSegment(sketch, "E1497", {"start": v(-11.58, -17.92) * mm, "end": v(-11.5, -17.79) * mm});
            skLineSegment(sketch, "E1498", {"start": v(-11.5, -17.79) * mm, "end": v(-11.42, -17.65) * mm});
            skLineSegment(sketch, "E1499", {"start": v(-11.42, -17.65) * mm, "end": v(-11.34, -17.52) * mm});
            skLineSegment(sketch, "E1500", {"start": v(-11.34, -17.52) * mm, "end": v(-11.26, -17.4) * mm});
            skLineSegment(sketch, "E1501", {"start": v(-11.26, -17.4) * mm, "end": v(-11.18, -17.26) * mm});
            skLineSegment(sketch, "E1502", {"start": v(-11.18, -17.26) * mm, "end": v(-11.12, -17.15) * mm});
            skLineSegment(sketch, "E1503", {"start": v(-11.12, -17.15) * mm, "end": v(-10.98, -17.22) * mm});
            skLineSegment(sketch, "E1504", {"start": v(-10.98, -17.22) * mm, "end": v(-10.85, -17.3) * mm});
            skLineSegment(sketch, "E1505", {"start": v(-10.85, -17.3) * mm, "end": v(-10.71, -17.37) * mm});
            skLineSegment(sketch, "E1506", {"start": v(-10.71, -17.37) * mm, "end": v(-10.58, -17.44) * mm});
            skLineSegment(sketch, "E1507", {"start": v(-10.58, -17.44) * mm, "end": v(-10.44, -17.51) * mm});
            skLineSegment(sketch, "E1508", {"start": v(-10.44, -17.51) * mm, "end": v(-10.3, -17.59) * mm});
            skLineSegment(sketch, "E1509", {"start": v(-10.3, -17.59) * mm, "end": v(-10.17, -17.66) * mm});
            skLineSegment(sketch, "E1510", {"start": v(-10.17, -17.66) * mm, "end": v(-10.04, -17.73) * mm});
            skLineSegment(sketch, "E1511", {"start": v(-10.04, -17.73) * mm, "end": v(-9.9, -17.8) * mm});
            skLineSegment(sketch, "E1512", {"start": v(-9.9, -17.8) * mm, "end": v(-9.77, -17.88) * mm});
            skLineSegment(sketch, "E1513", {"start": v(-9.77, -17.88) * mm, "end": v(-9.64, -17.95) * mm});
            skLineSegment(sketch, "E1514", {"start": v(-9.64, -17.95) * mm, "end": v(-9.6, -17.97) * mm});
            skLineSegment(sketch, "E1515", {"start": v(-9.6, -17.97) * mm, "end": v(-9.67, -18.1) * mm});
            skLineSegment(sketch, "E1516", {"start": v(-9.67, -18.1) * mm, "end": v(-9.74, -18.24) * mm});
            skLineSegment(sketch, "E1517", {"start": v(-9.74, -18.24) * mm, "end": v(-9.8, -18.38) * mm});
            skLineSegment(sketch, "E1518", {"start": v(-9.8, -18.38) * mm, "end": v(-9.88, -18.52) * mm});
            skLineSegment(sketch, "E1519", {"start": v(-9.88, -18.52) * mm, "end": v(-9.94, -18.66) * mm});
            skLineSegment(sketch, "E1520", {"start": v(-9.94, -18.66) * mm, "end": v(-10.01, -18.8) * mm});
            skLineSegment(sketch, "E1521", {"start": v(-10.01, -18.8) * mm, "end": v(-10.08, -18.94) * mm});
            skLineSegment(sketch, "E1522", {"start": v(-10.08, -18.94) * mm, "end": v(-10.15, -19.07) * mm});
            skLineSegment(sketch, "E1523", {"start": v(-10.15, -19.07) * mm, "end": v(-10.22, -19.21) * mm});
            skLineSegment(sketch, "E1524", {"start": v(-10.22, -19.21) * mm, "end": v(-10.28, -19.35) * mm});
            skLineSegment(sketch, "E1525", {"start": v(-10.28, -19.35) * mm, "end": v(-10.35, -19.49) * mm});
            skLineSegment(sketch, "E1526", {"start": v(-10.35, -19.49) * mm, "end": v(-10.42, -19.63) * mm});
            skLineSegment(sketch, "E1527", {"start": v(-10.42, -19.63) * mm, "end": v(-10.5, -19.77) * mm});
            skLineSegment(sketch, "E1528", {"start": v(-10.5, -19.77) * mm, "end": v(-10.53, -19.93) * mm});
            skLineSegment(sketch, "E1529", {"start": v(-10.53, -19.93) * mm, "end": v(-10.53, -20.1) * mm});
            skLineSegment(sketch, "E1530", {"start": v(-10.53, -20.1) * mm, "end": v(-10.49, -20.26) * mm});
            skLineSegment(sketch, "E1531", {"start": v(-10.49, -20.26) * mm, "end": v(-10.4, -20.4) * mm});
            skLineSegment(sketch, "E1532", {"start": v(-10.4, -20.4) * mm, "end": v(-10.29, -20.51) * mm});
            skLineSegment(sketch, "E1533", {"start": v(-10.29, -20.51) * mm, "end": v(-10.17, -20.58) * mm});
            skLineSegment(sketch, "E1534", {"start": v(-10.17, -20.58) * mm, "end": v(-10.02, -20.63) * mm});
            skLineSegment(sketch, "E1535", {"start": v(-10.02, -20.63) * mm, "end": v(-9.85, -20.63) * mm});
            skLineSegment(sketch, "E1536", {"start": v(-9.85, -20.63) * mm, "end": v(-9.7, -20.6) * mm});
            skLineSegment(sketch, "E1537", {"start": v(-9.7, -20.6) * mm, "end": v(-9.55, -20.52) * mm});
            skLineSegment(sketch, "E1538", {"start": v(-9.55, -20.52) * mm, "end": v(-9.43, -20.4) * mm});
            skLineSegment(sketch, "E1539", {"start": v(-9.43, -20.4) * mm, "end": v(-9.34, -20.26) * mm});
            skLineSegment(sketch, "E1540", {"start": v(-9.34, -20.26) * mm, "end": v(-9.28, -20.12) * mm});
            skLineSegment(sketch, "E1541", {"start": v(-9.28, -20.12) * mm, "end": v(-9.22, -19.98) * mm});
            skLineSegment(sketch, "E1542", {"start": v(-9.22, -19.98) * mm, "end": v(-9.16, -19.84) * mm});
            skLineSegment(sketch, "E1543", {"start": v(-9.16, -19.84) * mm, "end": v(-9.1, -19.7) * mm});
            skLineSegment(sketch, "E1544", {"start": v(-9.1, -19.7) * mm, "end": v(-9.04, -19.56) * mm});
            skLineSegment(sketch, "E1545", {"start": v(-9.04, -19.56) * mm, "end": v(-8.98, -19.41) * mm});
            skLineSegment(sketch, "E1546", {"start": v(-8.98, -19.41) * mm, "end": v(-8.92, -19.27) * mm});
            skLineSegment(sketch, "E1547", {"start": v(-8.92, -19.27) * mm, "end": v(-8.86, -19.13) * mm});
            skLineSegment(sketch, "E1548", {"start": v(-8.86, -19.13) * mm, "end": v(-8.8, -18.99) * mm});
            skLineSegment(sketch, "E1549", {"start": v(-8.8, -18.99) * mm, "end": v(-8.74, -18.85) * mm});
            skLineSegment(sketch, "E1550", {"start": v(-8.74, -18.85) * mm, "end": v(-8.68, -18.7) * mm});
            skLineSegment(sketch, "E1551", {"start": v(-8.68, -18.7) * mm, "end": v(-8.62, -18.56) * mm});
            skLineSegment(sketch, "E1552", {"start": v(-8.62, -18.56) * mm, "end": v(-8.57, -18.44) * mm});
            skLineSegment(sketch, "E1553", {"start": v(-8.57, -18.44) * mm, "end": v(-8.43, -18.5) * mm});
            skLineSegment(sketch, "E1554", {"start": v(-8.43, -18.5) * mm, "end": v(-8.28, -18.55) * mm});
            skLineSegment(sketch, "E1555", {"start": v(-8.28, -18.55) * mm, "end": v(-8.14, -18.6) * mm});
            skLineSegment(sketch, "E1556", {"start": v(-8.14, -18.6) * mm, "end": v(-8, -18.66) * mm});
            skLineSegment(sketch, "E1557", {"start": v(-8, -18.66) * mm, "end": v(-7.85, -18.7) * mm});
            skLineSegment(sketch, "E1558", {"start": v(-7.85, -18.7) * mm, "end": v(-7.7, -18.76) * mm});
            skLineSegment(sketch, "E1559", {"start": v(-7.7, -18.76) * mm, "end": v(-7.57, -18.82) * mm});
            skLineSegment(sketch, "E1560", {"start": v(-7.57, -18.82) * mm, "end": v(-7.42, -18.87) * mm});
            skLineSegment(sketch, "E1561", {"start": v(-7.42, -18.87) * mm, "end": v(-7.28, -18.92) * mm});
            skLineSegment(sketch, "E1562", {"start": v(-7.28, -18.92) * mm, "end": v(-7.14, -18.98) * mm});
            skLineSegment(sketch, "E1563", {"start": v(-7.14, -18.98) * mm, "end": v(-7, -19.03) * mm});
            skLineSegment(sketch, "E1564", {"start": v(-7, -19.03) * mm, "end": v(-6.96, -19.04) * mm});
            skLineSegment(sketch, "E1565", {"start": v(-6.96, -19.04) * mm, "end": v(-7, -19.19) * mm});
            skLineSegment(sketch, "E1566", {"start": v(-7, -19.19) * mm, "end": v(-7.05, -19.33) * mm});
            skLineSegment(sketch, "E1567", {"start": v(-7.05, -19.33) * mm, "end": v(-7.1, -19.48) * mm});
            skLineSegment(sketch, "E1568", {"start": v(-7.1, -19.48) * mm, "end": v(-7.15, -19.63) * mm});
            skLineSegment(sketch, "E1569", {"start": v(-7.15, -19.63) * mm, "end": v(-7.2, -19.77) * mm});
            skLineSegment(sketch, "E1570", {"start": v(-7.2, -19.77) * mm, "end": v(-7.24, -19.92) * mm});
            skLineSegment(sketch, "E1571", {"start": v(-7.24, -19.92) * mm, "end": v(-7.3, -20.07) * mm});
            skLineSegment(sketch, "E1572", {"start": v(-7.3, -20.07) * mm, "end": v(-7.34, -20.21) * mm});
            skLineSegment(sketch, "E1573", {"start": v(-7.34, -20.21) * mm, "end": v(-7.39, -20.36) * mm});
            skLineSegment(sketch, "E1574", {"start": v(-7.39, -20.36) * mm, "end": v(-7.43, -20.5) * mm});
            skLineSegment(sketch, "E1575", {"start": v(-7.43, -20.5) * mm, "end": v(-7.48, -20.65) * mm});
            skLineSegment(sketch, "E1576", {"start": v(-7.48, -20.65) * mm, "end": v(-7.53, -20.8) * mm});
            skLineSegment(sketch, "E1577", {"start": v(-7.53, -20.8) * mm, "end": v(-7.58, -20.96) * mm});
            skLineSegment(sketch, "E1578", {"start": v(-7.58, -20.96) * mm, "end": v(-7.6, -21.12) * mm});
            skLineSegment(sketch, "E1579", {"start": v(-7.6, -21.12) * mm, "end": v(-7.57, -21.28) * mm});
            skLineSegment(sketch, "E1580", {"start": v(-7.57, -21.28) * mm, "end": v(-7.5, -21.43) * mm});
            skLineSegment(sketch, "E1581", {"start": v(-7.5, -21.43) * mm, "end": v(-7.4, -21.56) * mm});
            skLineSegment(sketch, "E1582", {"start": v(-7.4, -21.56) * mm, "end": v(-7.27, -21.66) * mm});
            skLineSegment(sketch, "E1583", {"start": v(-7.27, -21.66) * mm, "end": v(-7.15, -21.7) * mm});
            skLineSegment(sketch, "E1584", {"start": v(-7.15, -21.7) * mm, "end": v(-6.99, -21.73) * mm});
            skLineSegment(sketch, "E1585", {"start": v(-6.99, -21.73) * mm, "end": v(-6.82, -21.72) * mm});
            skLineSegment(sketch, "E1586", {"start": v(-6.82, -21.72) * mm, "end": v(-6.67, -21.66) * mm});
            skLineSegment(sketch, "E1587", {"start": v(-6.67, -21.66) * mm, "end": v(-6.54, -21.56) * mm});
            skLineSegment(sketch, "E1588", {"start": v(-6.54, -21.56) * mm, "end": v(-6.43, -21.43) * mm});
            skLineSegment(sketch, "E1589", {"start": v(-6.43, -21.43) * mm, "end": v(-6.37, -21.28) * mm});
            skLineSegment(sketch, "E1590", {"start": v(-6.37, -21.28) * mm, "end": v(-6.33, -21.13) * mm});
            skLineSegment(sketch, "E1591", {"start": v(-6.33, -21.13) * mm, "end": v(-6.3, -20.98) * mm});
            skLineSegment(sketch, "E1592", {"start": v(-6.3, -20.98) * mm, "end": v(-6.25, -20.83) * mm});
            skLineSegment(sketch, "E1593", {"start": v(-6.25, -20.83) * mm, "end": v(-6.21, -20.68) * mm});
            skLineSegment(sketch, "E1594", {"start": v(-6.21, -20.68) * mm, "end": v(-6.17, -20.53) * mm});
            skLineSegment(sketch, "E1595", {"start": v(-6.17, -20.53) * mm, "end": v(-6.13, -20.38) * mm});
            skLineSegment(sketch, "E1596", {"start": v(-6.13, -20.38) * mm, "end": v(-6.1, -20.24) * mm});
            skLineSegment(sketch, "E1597", {"start": v(-6.1, -20.24) * mm, "end": v(-6.06, -20.09) * mm});
            skLineSegment(sketch, "E1598", {"start": v(-6.06, -20.09) * mm, "end": v(-6.02, -19.94) * mm});
            skLineSegment(sketch, "E1599", {"start": v(-6.02, -19.94) * mm, "end": v(-5.98, -19.79) * mm});
            skLineSegment(sketch, "E1600", {"start": v(-5.98, -19.79) * mm, "end": v(-5.94, -19.64) * mm});
            skLineSegment(sketch, "E1601", {"start": v(-5.94, -19.64) * mm, "end": v(-5.9, -19.5) * mm});
            skLineSegment(sketch, "E1602", {"start": v(-5.9, -19.5) * mm, "end": v(-5.87, -19.36) * mm});
            skLineSegment(sketch, "E1603", {"start": v(-5.87, -19.36) * mm, "end": v(-5.72, -19.4) * mm});
            skLineSegment(sketch, "E1604", {"start": v(-5.72, -19.4) * mm, "end": v(-5.57, -19.43) * mm});
            skLineSegment(sketch, "E1605", {"start": v(-5.57, -19.43) * mm, "end": v(-5.42, -19.46) * mm});
            skLineSegment(sketch, "E1606", {"start": v(-5.42, -19.46) * mm, "end": v(-5.27, -19.5) * mm});
            skLineSegment(sketch, "E1607", {"start": v(-5.27, -19.5) * mm, "end": v(-5.12, -19.53) * mm});
            skLineSegment(sketch, "E1608", {"start": v(-5.12, -19.53) * mm, "end": v(-4.97, -19.56) * mm});
            skLineSegment(sketch, "E1609", {"start": v(-4.97, -19.56) * mm, "end": v(-4.82, -19.6) * mm});
            skLineSegment(sketch, "E1610", {"start": v(-4.82, -19.6) * mm, "end": v(-4.67, -19.62) * mm});
            skLineSegment(sketch, "E1611", {"start": v(-4.67, -19.62) * mm, "end": v(-4.52, -19.66) * mm});
            skLineSegment(sketch, "E1612", {"start": v(-4.52, -19.66) * mm, "end": v(-4.37, -19.69) * mm});
            skLineSegment(sketch, "E1613", {"start": v(-4.37, -19.69) * mm, "end": v(-4.22, -19.72) * mm});
            skLineSegment(sketch, "E1614", {"start": v(-4.22, -19.72) * mm, "end": v(-4.19, -19.73) * mm});
            skLineSegment(sketch, "E1615", {"start": v(-4.19, -19.73) * mm, "end": v(-4.21, -19.88) * mm});
            skLineSegment(sketch, "E1616", {"start": v(-4.21, -19.88) * mm, "end": v(-4.24, -20.03) * mm});
            skLineSegment(sketch, "E1617", {"start": v(-4.24, -20.03) * mm, "end": v(-4.26, -20.18) * mm});
            skLineSegment(sketch, "E1618", {"start": v(-4.26, -20.18) * mm, "end": v(-4.3, -20.34) * mm});
            skLineSegment(sketch, "E1619", {"start": v(-4.3, -20.34) * mm, "end": v(-4.32, -20.49) * mm});
            skLineSegment(sketch, "E1620", {"start": v(-4.32, -20.49) * mm, "end": v(-4.34, -20.64) * mm});
            skLineSegment(sketch, "E1621", {"start": v(-4.34, -20.64) * mm, "end": v(-4.37, -20.8) * mm});
            skLineSegment(sketch, "E1622", {"start": v(-4.37, -20.8) * mm, "end": v(-4.4, -20.94) * mm});
            skLineSegment(sketch, "E1623", {"start": v(-4.4, -20.94) * mm, "end": v(-4.42, -21.1) * mm});
            skLineSegment(sketch, "E1624", {"start": v(-4.42, -21.1) * mm, "end": v(-4.45, -21.24) * mm});
            skLineSegment(sketch, "E1625", {"start": v(-4.45, -21.24) * mm, "end": v(-4.47, -21.4) * mm});
            skLineSegment(sketch, "E1626", {"start": v(-4.47, -21.4) * mm, "end": v(-4.5, -21.55) * mm});
            skLineSegment(sketch, "E1627", {"start": v(-4.5, -21.55) * mm, "end": v(-4.53, -21.71) * mm});
            skLineSegment(sketch, "E1628", {"start": v(-4.53, -21.71) * mm, "end": v(-4.52, -21.88) * mm});
            skLineSegment(sketch, "E1629", {"start": v(-4.52, -21.88) * mm, "end": v(-4.47, -22.03) * mm});
            skLineSegment(sketch, "E1630", {"start": v(-4.47, -22.03) * mm, "end": v(-4.39, -22.17) * mm});
            skLineSegment(sketch, "E1631", {"start": v(-4.39, -22.17) * mm, "end": v(-4.27, -22.29) * mm});
            skLineSegment(sketch, "E1632", {"start": v(-4.27, -22.29) * mm, "end": v(-4.12, -22.36) * mm});
            skLineSegment(sketch, "E1633", {"start": v(-4.12, -22.36) * mm, "end": v(-3.96, -22.4) * mm});
            skLineSegment(sketch, "E1634", {"start": v(-3.96, -22.4) * mm, "end": v(-3.8, -22.4) * mm});
            skLineSegment(sketch, "E1635", {"start": v(-3.8, -22.4) * mm, "end": v(-3.64, -22.34) * mm});
            skLineSegment(sketch, "E1636", {"start": v(-3.64, -22.34) * mm, "end": v(-3.5, -22.25) * mm});
            skLineSegment(sketch, "E1637", {"start": v(-3.5, -22.25) * mm, "end": v(-3.4, -22.13) * mm});
            skLineSegment(sketch, "E1638", {"start": v(-3.4, -22.13) * mm, "end": v(-3.32, -21.98) * mm});
            skLineSegment(sketch, "E1639", {"start": v(-3.32, -21.98) * mm, "end": v(-3.28, -21.86) * mm});
            skLineSegment(sketch, "E1640", {"start": v(-3.28, -21.86) * mm, "end": v(-3.27, -21.7) * mm});
            skLineSegment(sketch, "E1641", {"start": v(-3.27, -21.7) * mm, "end": v(-3.25, -21.55) * mm});
            skLineSegment(sketch, "E1642", {"start": v(-3.25, -21.55) * mm, "end": v(-3.23, -21.4) * mm});
            skLineSegment(sketch, "E1643", {"start": v(-3.23, -21.4) * mm, "end": v(-3.21, -21.25) * mm});
            skLineSegment(sketch, "E1644", {"start": v(-3.21, -21.25) * mm, "end": v(-3.2, -21.1) * mm});
            skLineSegment(sketch, "E1645", {"start": v(-3.2, -21.1) * mm, "end": v(-3.18, -20.94) * mm});
            skLineSegment(sketch, "E1646", {"start": v(-3.18, -20.94) * mm, "end": v(-3.16, -20.79) * mm});
            skLineSegment(sketch, "E1647", {"start": v(-3.16, -20.79) * mm, "end": v(-3.14, -20.64) * mm});
            skLineSegment(sketch, "E1648", {"start": v(-3.14, -20.64) * mm, "end": v(-3.13, -20.48) * mm});
            skLineSegment(sketch, "E1649", {"start": v(-3.13, -20.48) * mm, "end": v(-3.1, -20.33) * mm});
            skLineSegment(sketch, "E1650", {"start": v(-3.1, -20.33) * mm, "end": v(-3.1, -20.18) * mm});
            skLineSegment(sketch, "E1651", {"start": v(-3.1, -20.18) * mm, "end": v(-3.07, -20.02) * mm});
            skLineSegment(sketch, "E1652", {"start": v(-3.07, -20.02) * mm, "end": v(-3.06, -19.9) * mm});
            skLineSegment(sketch, "E1653", {"start": v(-3.06, -19.9) * mm, "end": v(-2.9, -19.9) * mm});
            skLineSegment(sketch, "E1654", {"start": v(-2.9, -19.9) * mm, "end": v(-2.75, -19.91) * mm});
            skLineSegment(sketch, "E1655", {"start": v(-2.75, -19.91) * mm, "end": v(-2.6, -19.92) * mm});
            skLineSegment(sketch, "E1656", {"start": v(-2.6, -19.92) * mm, "end": v(-2.45, -19.94) * mm});
            skLineSegment(sketch, "E1657", {"start": v(-2.45, -19.94) * mm, "end": v(-2.3, -19.95) * mm});
            skLineSegment(sketch, "E1658", {"start": v(-2.3, -19.95) * mm, "end": v(-2.14, -19.96) * mm});
            skLineSegment(sketch, "E1659", {"start": v(-2.14, -19.96) * mm, "end": v(-1.99, -19.97) * mm});
            skLineSegment(sketch, "E1660", {"start": v(-1.99, -19.97) * mm, "end": v(-1.84, -19.98) * mm});
            skLineSegment(sketch, "E1661", {"start": v(-1.84, -19.98) * mm, "end": v(-1.68, -20) * mm});
            skLineSegment(sketch, "E1662", {"start": v(-1.68, -20) * mm, "end": v(-1.53, -20) * mm});
            skLineSegment(sketch, "E1663", {"start": v(-1.53, -20) * mm, "end": v(-1.38, -20.01) * mm});
            skLineSegment(sketch, "E1664", {"start": v(-1.38, -20.01) * mm, "end": v(-1.34, -20.01) * mm});
            skLineSegment(sketch, "E1665", {"start": v(-1.34, -20.01) * mm, "end": v(-1.35, -20.17) * mm});
            skLineSegment(sketch, "E1666", {"start": v(-1.35, -20.17) * mm, "end": v(-1.35, -20.32) * mm});
            skLineSegment(sketch, "E1667", {"start": v(-1.35, -20.32) * mm, "end": v(-1.36, -20.48) * mm});
            skLineSegment(sketch, "E1668", {"start": v(-1.36, -20.48) * mm, "end": v(-1.36, -20.63) * mm});
            skLineSegment(sketch, "E1669", {"start": v(-1.36, -20.63) * mm, "end": v(-1.36, -20.78) * mm});
            skLineSegment(sketch, "E1670", {"start": v(-1.36, -20.78) * mm, "end": v(-1.37, -20.94) * mm});
            skLineSegment(sketch, "E1671", {"start": v(-1.37, -20.94) * mm, "end": v(-1.37, -21.1) * mm});
            skLineSegment(sketch, "E1672", {"start": v(-1.37, -21.1) * mm, "end": v(-1.38, -21.24) * mm});
            skLineSegment(sketch, "E1673", {"start": v(-1.38, -21.24) * mm, "end": v(-1.38, -21.4) * mm});
            skLineSegment(sketch, "E1674", {"start": v(-1.38, -21.4) * mm, "end": v(-1.39, -21.55) * mm});
            skLineSegment(sketch, "E1675", {"start": v(-1.39, -21.55) * mm, "end": v(-1.4, -21.7) * mm});
            skLineSegment(sketch, "E1676", {"start": v(-1.4, -21.7) * mm, "end": v(-1.4, -21.86) * mm});
            skLineSegment(sketch, "E1677", {"start": v(-1.4, -21.86) * mm, "end": v(-1.4, -22.02) * mm});
            skLineSegment(sketch, "E1678", {"start": v(-1.4, -22.02) * mm, "end": v(-1.37, -22.19) * mm});
            skLineSegment(sketch, "E1679", {"start": v(-1.37, -22.19) * mm, "end": v(-1.3, -22.34) * mm});
            skLineSegment(sketch, "E1680", {"start": v(-1.3, -22.34) * mm, "end": v(-1.2, -22.46) * mm});
            skLineSegment(sketch, "E1681", {"start": v(-1.2, -22.46) * mm, "end": v(-1.06, -22.56) * mm});
            skLineSegment(sketch, "E1682", {"start": v(-1.06, -22.56) * mm, "end": v(-0.9, -22.61) * mm});
            skLineSegment(sketch, "E1683", {"start": v(-0.9, -22.61) * mm, "end": v(-0.74, -22.62) * mm});
            skLineSegment(sketch, "E1684", {"start": v(-0.74, -22.62) * mm, "end": v(-0.58, -22.6) * mm});
            skLineSegment(sketch, "E1685", {"start": v(-0.58, -22.6) * mm, "end": v(-0.43, -22.52) * mm});
            skLineSegment(sketch, "E1686", {"start": v(-0.43, -22.52) * mm, "end": v(-0.3, -22.42) * mm});
            skLineSegment(sketch, "E1687", {"start": v(-0.3, -22.42) * mm, "end": v(-0.21, -22.28) * mm});
            skLineSegment(sketch, "E1688", {"start": v(-0.21, -22.28) * mm, "end": v(-0.16, -22.12) * mm});
            skLineSegment(sketch, "E1689", {"start": v(-0.16, -22.12) * mm, "end": v(-0.15, -22) * mm});
            skLineSegment(sketch, "E1690", {"start": v(-0.15, -22) * mm, "end": v(-0.15, -21.84) * mm});
            skLineSegment(sketch, "E1691", {"start": v(-0.15, -21.84) * mm, "end": v(-0.16, -21.69) * mm});
            skLineSegment(sketch, "E1692", {"start": v(-0.16, -21.69) * mm, "end": v(-0.16, -21.53) * mm});
            skLineSegment(sketch, "E1693", {"start": v(-0.16, -21.53) * mm, "end": v(-0.17, -21.38) * mm});
            skLineSegment(sketch, "E1694", {"start": v(-0.17, -21.38) * mm, "end": v(-0.17, -21.22) * mm});
            skLineSegment(sketch, "E1695", {"start": v(-0.17, -21.22) * mm, "end": v(-0.18, -21.07) * mm});
            skLineSegment(sketch, "E1696", {"start": v(-0.18, -21.07) * mm, "end": v(-0.18, -20.92) * mm});
            skLineSegment(sketch, "E1697", {"start": v(-0.18, -20.92) * mm, "end": v(-0.18, -20.76) * mm});
            skLineSegment(sketch, "E1698", {"start": v(-0.18, -20.76) * mm, "end": v(-0.19, -20.6) * mm});
            skLineSegment(sketch, "E1699", {"start": v(-0.19, -20.6) * mm, "end": v(-0.2, -20.45) * mm});
            skLineSegment(sketch, "E1700", {"start": v(-0.2, -20.45) * mm, "end": v(-0.2, -20.3) * mm});
            skLineSegment(sketch, "E1701", {"start": v(-0.2, -20.3) * mm, "end": v(-0.2, -20.15) * mm});
            skLineSegment(sketch, "E1702", {"start": v(-0.2, -20.15) * mm, "end": v(-0.2, -20.01) * mm});
            skLineSegment(sketch, "E1703", {"start": v(-0.2, -20.01) * mm, "end": v(-0.05, -20) * mm});
            skLineSegment(sketch, "E1704", {"start": v(-0.05, -20) * mm, "end": v(0.1, -20) * mm});
            skLineSegment(sketch, "E1705", {"start": v(0.1, -20) * mm, "end": v(0.25, -19.98) * mm});
            skLineSegment(sketch, "E1706", {"start": v(0.25, -19.98) * mm, "end": v(0.4, -19.97) * mm});
            skLineSegment(sketch, "E1707", {"start": v(0.4, -19.97) * mm, "end": v(0.56, -19.96) * mm});
            skLineSegment(sketch, "E1708", {"start": v(0.56, -19.96) * mm, "end": v(0.71, -19.95) * mm});
            skLineSegment(sketch, "E1709", {"start": v(0.71, -19.95) * mm, "end": v(0.86, -19.94) * mm});
            skLineSegment(sketch, "E1710", {"start": v(0.86, -19.94) * mm, "end": v(1.02, -19.93) * mm});
            skLineSegment(sketch, "E1711", {"start": v(1.02, -19.93) * mm, "end": v(1.17, -19.92) * mm});
            skLineSegment(sketch, "E1712", {"start": v(1.17, -19.92) * mm, "end": v(1.32, -19.9) * mm});
            skLineSegment(sketch, "E1713", {"start": v(1.32, -19.9) * mm, "end": v(1.48, -19.9) * mm});
            skLineSegment(sketch, "E1714", {"start": v(1.48, -19.9) * mm, "end": v(1.51, -19.9) * mm});
            skLineSegment(sketch, "E1715", {"start": v(1.51, -19.9) * mm, "end": v(1.53, -20.04) * mm});
            skLineSegment(sketch, "E1716", {"start": v(1.53, -20.04) * mm, "end": v(1.55, -20.2) * mm});
            skLineSegment(sketch, "E1717", {"start": v(1.55, -20.2) * mm, "end": v(1.56, -20.35) * mm});
            skLineSegment(sketch, "E1718", {"start": v(1.56, -20.35) * mm, "end": v(1.58, -20.5) * mm});
            skLineSegment(sketch, "E1719", {"start": v(1.58, -20.5) * mm, "end": v(1.6, -20.65) * mm});
            skLineSegment(sketch, "E1720", {"start": v(1.6, -20.65) * mm, "end": v(1.62, -20.8) * mm});
            skLineSegment(sketch, "E1721", {"start": v(1.62, -20.8) * mm, "end": v(1.63, -20.96) * mm});
            skLineSegment(sketch, "E1722", {"start": v(1.63, -20.96) * mm, "end": v(1.65, -21.11) * mm});
            skLineSegment(sketch, "E1723", {"start": v(1.65, -21.11) * mm, "end": v(1.67, -21.27) * mm});
            skLineSegment(sketch, "E1724", {"start": v(1.67, -21.27) * mm, "end": v(1.69, -21.42) * mm});
            skLineSegment(sketch, "E1725", {"start": v(1.69, -21.42) * mm, "end": v(1.7, -21.57) * mm});
            skLineSegment(sketch, "E1726", {"start": v(1.7, -21.57) * mm, "end": v(1.72, -21.73) * mm});
            skLineSegment(sketch, "E1727", {"start": v(1.72, -21.73) * mm, "end": v(1.74, -21.89) * mm});
            skLineSegment(sketch, "E1728", {"start": v(1.74, -21.89) * mm, "end": v(1.8, -22.05) * mm});
            skLineSegment(sketch, "E1729", {"start": v(1.8, -22.05) * mm, "end": v(1.88, -22.18) * mm});
            skLineSegment(sketch, "E1730", {"start": v(1.88, -22.18) * mm, "end": v(2, -22.3) * mm});
            skLineSegment(sketch, "E1731", {"start": v(2, -22.3) * mm, "end": v(2.15, -22.37) * mm});
            skLineSegment(sketch, "E1732", {"start": v(2.15, -22.37) * mm, "end": v(2.31, -22.4) * mm});
            skLineSegment(sketch, "E1733", {"start": v(2.31, -22.4) * mm, "end": v(2.48, -22.39) * mm});
            skLineSegment(sketch, "E1734", {"start": v(2.48, -22.39) * mm, "end": v(2.63, -22.34) * mm});
            skLineSegment(sketch, "E1735", {"start": v(2.63, -22.34) * mm, "end": v(2.77, -22.24) * mm});
            skLineSegment(sketch, "E1736", {"start": v(2.77, -22.24) * mm, "end": v(2.88, -22.12) * mm});
            skLineSegment(sketch, "E1737", {"start": v(2.88, -22.12) * mm, "end": v(2.95, -21.97) * mm});
            skLineSegment(sketch, "E1738", {"start": v(2.95, -21.97) * mm, "end": v(2.98, -21.81) * mm});
            skLineSegment(sketch, "E1739", {"start": v(2.98, -21.81) * mm, "end": v(2.97, -21.68) * mm});
            skLineSegment(sketch, "E1740", {"start": v(2.97, -21.68) * mm, "end": v(2.95, -21.53) * mm});
            skLineSegment(sketch, "E1741", {"start": v(2.95, -21.53) * mm, "end": v(2.92, -21.38) * mm});
            skLineSegment(sketch, "E1742", {"start": v(2.92, -21.38) * mm, "end": v(2.9, -21.22) * mm});
            skLineSegment(sketch, "E1743", {"start": v(2.9, -21.22) * mm, "end": v(2.87, -21.07) * mm});
            skLineSegment(sketch, "E1744", {"start": v(2.87, -21.07) * mm, "end": v(2.84, -20.92) * mm});
            skLineSegment(sketch, "E1745", {"start": v(2.84, -20.92) * mm, "end": v(2.82, -20.77) * mm});
            skLineSegment(sketch, "E1746", {"start": v(2.82, -20.77) * mm, "end": v(2.8, -20.62) * mm});
            skLineSegment(sketch, "E1747", {"start": v(2.8, -20.62) * mm, "end": v(2.77, -20.47) * mm});
            skLineSegment(sketch, "E1748", {"start": v(2.77, -20.47) * mm, "end": v(2.74, -20.31) * mm});
            skLineSegment(sketch, "E1749", {"start": v(2.74, -20.31) * mm, "end": v(2.71, -20.16) * mm});
            skLineSegment(sketch, "E1750", {"start": v(2.71, -20.16) * mm, "end": v(2.69, -20.01) * mm});
            skLineSegment(sketch, "E1751", {"start": v(2.69, -20.01) * mm, "end": v(2.66, -19.86) * mm});
            skLineSegment(sketch, "E1752", {"start": v(2.66, -19.86) * mm, "end": v(2.64, -19.73) * mm});
            skLineSegment(sketch, "E1753", {"start": v(2.64, -19.73) * mm, "end": v(2.79, -19.7) * mm});
            skLineSegment(sketch, "E1754", {"start": v(2.79, -19.7) * mm, "end": v(2.94, -19.66) * mm});
            skLineSegment(sketch, "E1755", {"start": v(2.94, -19.66) * mm, "end": v(3.09, -19.63) * mm});
            skLineSegment(sketch, "E1756", {"start": v(3.09, -19.63) * mm, "end": v(3.24, -19.6) * mm});
            skLineSegment(sketch, "E1757", {"start": v(3.24, -19.6) * mm, "end": v(3.39, -19.57) * mm});
            skLineSegment(sketch, "E1758", {"start": v(3.39, -19.57) * mm, "end": v(3.54, -19.53) * mm});
            skLineSegment(sketch, "E1759", {"start": v(3.54, -19.53) * mm, "end": v(3.69, -19.5) * mm});
            skLineSegment(sketch, "E1760", {"start": v(3.69, -19.5) * mm, "end": v(3.83, -19.47) * mm});
            skLineSegment(sketch, "E1761", {"start": v(3.83, -19.47) * mm, "end": v(3.98, -19.44) * mm});
            skLineSegment(sketch, "E1762", {"start": v(3.98, -19.44) * mm, "end": v(4.13, -19.4) * mm});
            skLineSegment(sketch, "E1763", {"start": v(4.13, -19.4) * mm, "end": v(4.28, -19.37) * mm});
            skLineSegment(sketch, "E1764", {"start": v(4.28, -19.37) * mm, "end": v(4.32, -19.36) * mm});
            skLineSegment(sketch, "E1765", {"start": v(4.32, -19.36) * mm, "end": v(4.36, -19.51) * mm});
            skLineSegment(sketch, "E1766", {"start": v(4.36, -19.51) * mm, "end": v(4.4, -19.66) * mm});
            skLineSegment(sketch, "E1767", {"start": v(4.4, -19.66) * mm, "end": v(4.44, -19.81) * mm});
            skLineSegment(sketch, "E1768", {"start": v(4.44, -19.81) * mm, "end": v(4.47, -19.96) * mm});
            skLineSegment(sketch, "E1769", {"start": v(4.47, -19.96) * mm, "end": v(4.51, -20.1) * mm});
            skLineSegment(sketch, "E1770", {"start": v(4.51, -20.1) * mm, "end": v(4.55, -20.26) * mm});
            skLineSegment(sketch, "E1771", {"start": v(4.55, -20.26) * mm, "end": v(4.6, -20.4) * mm});
            skLineSegment(sketch, "E1772", {"start": v(4.6, -20.4) * mm, "end": v(4.63, -20.55) * mm});
            skLineSegment(sketch, "E1773", {"start": v(4.63, -20.55) * mm, "end": v(4.67, -20.7) * mm});
            skLineSegment(sketch, "E1774", {"start": v(4.67, -20.7) * mm, "end": v(4.7, -20.85) * mm});
            skLineSegment(sketch, "E1775", {"start": v(4.7, -20.85) * mm, "end": v(4.75, -21) * mm});
            skLineSegment(sketch, "E1776", {"start": v(4.75, -21) * mm, "end": v(4.79, -21.15) * mm});
            skLineSegment(sketch, "E1777", {"start": v(4.79, -21.15) * mm, "end": v(4.83, -21.3) * mm});
            skLineSegment(sketch, "E1778", {"start": v(4.83, -21.3) * mm, "end": v(4.9, -21.46) * mm});
            skLineSegment(sketch, "E1779", {"start": v(4.9, -21.46) * mm, "end": v(5.01, -21.58) * mm});
            skLineSegment(sketch, "E1780", {"start": v(5.01, -21.58) * mm, "end": v(5.15, -21.67) * mm});
            skLineSegment(sketch, "E1781", {"start": v(5.15, -21.67) * mm, "end": v(5.3, -21.72) * mm});
            skLineSegment(sketch, "E1782", {"start": v(5.3, -21.72) * mm, "end": v(5.47, -21.73) * mm});
            skLineSegment(sketch, "E1783", {"start": v(5.47, -21.73) * mm, "end": v(5.63, -21.7) * mm});
            skLineSegment(sketch, "E1784", {"start": v(5.63, -21.7) * mm, "end": v(5.78, -21.62) * mm});
            skLineSegment(sketch, "E1785", {"start": v(5.78, -21.62) * mm, "end": v(5.9, -21.51) * mm});
            skLineSegment(sketch, "E1786", {"start": v(5.9, -21.51) * mm, "end": v(5.99, -21.38) * mm});
            skLineSegment(sketch, "E1787", {"start": v(5.99, -21.38) * mm, "end": v(6.04, -21.22) * mm});
            skLineSegment(sketch, "E1788", {"start": v(6.04, -21.22) * mm, "end": v(6.05, -21.05) * mm});
            skLineSegment(sketch, "E1789", {"start": v(6.05, -21.05) * mm, "end": v(6.02, -20.92) * mm});
            skLineSegment(sketch, "E1790", {"start": v(6.02, -20.92) * mm, "end": v(5.97, -20.78) * mm});
            skLineSegment(sketch, "E1791", {"start": v(5.97, -20.78) * mm, "end": v(5.93, -20.63) * mm});
            skLineSegment(sketch, "E1792", {"start": v(5.93, -20.63) * mm, "end": v(5.88, -20.49) * mm});
            skLineSegment(sketch, "E1793", {"start": v(5.88, -20.49) * mm, "end": v(5.83, -20.34) * mm});
            skLineSegment(sketch, "E1794", {"start": v(5.83, -20.34) * mm, "end": v(5.78, -20.2) * mm});
            skLineSegment(sketch, "E1795", {"start": v(5.78, -20.2) * mm, "end": v(5.74, -20.05) * mm});
            skLineSegment(sketch, "E1796", {"start": v(5.74, -20.05) * mm, "end": v(5.69, -19.9) * mm});
            skLineSegment(sketch, "E1797", {"start": v(5.69, -19.9) * mm, "end": v(5.64, -19.76) * mm});
            skLineSegment(sketch, "E1798", {"start": v(5.64, -19.76) * mm, "end": v(5.6, -19.6) * mm});
            skLineSegment(sketch, "E1799", {"start": v(5.6, -19.6) * mm, "end": v(5.55, -19.46) * mm});
            skLineSegment(sketch, "E1800", {"start": v(5.55, -19.46) * mm, "end": v(5.5, -19.32) * mm});
            skLineSegment(sketch, "E1801", {"start": v(5.5, -19.32) * mm, "end": v(5.45, -19.17) * mm});
            skLineSegment(sketch, "E1802", {"start": v(5.45, -19.17) * mm, "end": v(5.41, -19.04) * mm});
            skLineSegment(sketch, "E1803", {"start": v(5.41, -19.04) * mm, "end": v(5.55, -18.99) * mm});
            skLineSegment(sketch, "E1804", {"start": v(5.55, -18.99) * mm, "end": v(5.7, -18.94) * mm});
            skLineSegment(sketch, "E1805", {"start": v(5.7, -18.94) * mm, "end": v(5.84, -18.88) * mm});
            skLineSegment(sketch, "E1806", {"start": v(5.84, -18.88) * mm, "end": v(5.98, -18.83) * mm});
            skLineSegment(sketch, "E1807", {"start": v(5.98, -18.83) * mm, "end": v(6.13, -18.78) * mm});
            skLineSegment(sketch, "E1808", {"start": v(6.13, -18.78) * mm, "end": v(6.27, -18.72) * mm});
            skLineSegment(sketch, "E1809", {"start": v(6.27, -18.72) * mm, "end": v(6.42, -18.67) * mm});
            skLineSegment(sketch, "E1810", {"start": v(6.42, -18.67) * mm, "end": v(6.56, -18.62) * mm});
            skLineSegment(sketch, "E1811", {"start": v(6.56, -18.62) * mm, "end": v(6.7, -18.56) * mm});
            skLineSegment(sketch, "E1812", {"start": v(6.7, -18.56) * mm, "end": v(6.85, -18.5) * mm});
            skLineSegment(sketch, "E1813", {"start": v(6.85, -18.5) * mm, "end": v(6.99, -18.45) * mm});
            skLineSegment(sketch, "E1814", {"start": v(6.99, -18.45) * mm, "end": v(7.02, -18.44) * mm});
            skLineSegment(sketch, "E1815", {"start": v(7.02, -18.44) * mm, "end": v(7.08, -18.58) * mm});
            skLineSegment(sketch, "E1816", {"start": v(7.08, -18.58) * mm, "end": v(7.14, -18.72) * mm});
            skLineSegment(sketch, "E1817", {"start": v(7.14, -18.72) * mm, "end": v(7.2, -18.87) * mm});
            skLineSegment(sketch, "E1818", {"start": v(7.2, -18.87) * mm, "end": v(7.26, -19) * mm});
            skLineSegment(sketch, "E1819", {"start": v(7.26, -19) * mm, "end": v(7.32, -19.15) * mm});
            skLineSegment(sketch, "E1820", {"start": v(7.32, -19.15) * mm, "end": v(7.38, -19.3) * mm});
            skLineSegment(sketch, "E1821", {"start": v(7.38, -19.3) * mm, "end": v(7.44, -19.43) * mm});
            skLineSegment(sketch, "E1822", {"start": v(7.44, -19.43) * mm, "end": v(7.5, -19.57) * mm});
            skLineSegment(sketch, "E1823", {"start": v(7.5, -19.57) * mm, "end": v(7.56, -19.72) * mm});
            skLineSegment(sketch, "E1824", {"start": v(7.56, -19.72) * mm, "end": v(7.62, -19.86) * mm});
            skLineSegment(sketch, "E1825", {"start": v(7.62, -19.86) * mm, "end": v(7.68, -20) * mm});
            skLineSegment(sketch, "E1826", {"start": v(7.68, -20) * mm, "end": v(7.74, -20.14) * mm});
            skLineSegment(sketch, "E1827", {"start": v(7.74, -20.14) * mm, "end": v(7.8, -20.3) * mm});
            skLineSegment(sketch, "E1828", {"start": v(7.8, -20.3) * mm, "end": v(7.9, -20.43) * mm});
            skLineSegment(sketch, "E1829", {"start": v(7.9, -20.43) * mm, "end": v(8.02, -20.54) * mm});
            skLineSegment(sketch, "E1830", {"start": v(8.02, -20.54) * mm, "end": v(8.17, -20.6) * mm});
            skLineSegment(sketch, "E1831", {"start": v(8.17, -20.6) * mm, "end": v(8.34, -20.64) * mm});
            skLineSegment(sketch, "E1832", {"start": v(8.34, -20.64) * mm, "end": v(8.5, -20.62) * mm});
            skLineSegment(sketch, "E1833", {"start": v(8.5, -20.62) * mm, "end": v(8.62, -20.58) * mm});
            skLineSegment(sketch, "E1834", {"start": v(8.62, -20.58) * mm, "end": v(8.76, -20.5) * mm});
            skLineSegment(sketch, "E1835", {"start": v(8.76, -20.5) * mm, "end": v(8.88, -20.37) * mm});
            skLineSegment(sketch, "E1836", {"start": v(8.88, -20.37) * mm, "end": v(8.95, -20.23) * mm});
            skLineSegment(sketch, "E1837", {"start": v(8.95, -20.23) * mm, "end": v(8.99, -20.07) * mm});
            skLineSegment(sketch, "E1838", {"start": v(8.99, -20.07) * mm, "end": v(8.98, -19.9) * mm});
            skLineSegment(sketch, "E1839", {"start": v(8.98, -19.9) * mm, "end": v(8.93, -19.74) * mm});
            skLineSegment(sketch, "E1840", {"start": v(8.93, -19.74) * mm, "end": v(8.86, -19.6) * mm});
            skLineSegment(sketch, "E1841", {"start": v(8.86, -19.6) * mm, "end": v(8.8, -19.47) * mm});
            skLineSegment(sketch, "E1842", {"start": v(8.8, -19.47) * mm, "end": v(8.73, -19.33) * mm});
            skLineSegment(sketch, "E1843", {"start": v(8.73, -19.33) * mm, "end": v(8.66, -19.2) * mm});
            skLineSegment(sketch, "E1844", {"start": v(8.66, -19.2) * mm, "end": v(8.6, -19.06) * mm});
            skLineSegment(sketch, "E1845", {"start": v(8.6, -19.06) * mm, "end": v(8.52, -18.92) * mm});
            skLineSegment(sketch, "E1846", {"start": v(8.52, -18.92) * mm, "end": v(8.46, -18.78) * mm});
            skLineSegment(sketch, "E1847", {"start": v(8.46, -18.78) * mm, "end": v(8.39, -18.64) * mm});
            skLineSegment(sketch, "E1848", {"start": v(8.39, -18.64) * mm, "end": v(8.32, -18.5) * mm});
            skLineSegment(sketch, "E1849", {"start": v(8.32, -18.5) * mm, "end": v(8.25, -18.36) * mm});
            skLineSegment(sketch, "E1850", {"start": v(8.25, -18.36) * mm, "end": v(8.18, -18.23) * mm});
            skLineSegment(sketch, "E1851", {"start": v(8.18, -18.23) * mm, "end": v(8.12, -18.09) * mm});
            skLineSegment(sketch, "E1852", {"start": v(8.12, -18.09) * mm, "end": v(8.06, -17.97) * mm});
            skLineSegment(sketch, "E1853", {"start": v(8.06, -17.97) * mm, "end": v(8.2, -17.9) * mm});
            skLineSegment(sketch, "E1854", {"start": v(8.2, -17.9) * mm, "end": v(8.33, -17.82) * mm});
            skLineSegment(sketch, "E1855", {"start": v(8.33, -17.82) * mm, "end": v(8.46, -17.75) * mm});
            skLineSegment(sketch, "E1856", {"start": v(8.46, -17.75) * mm, "end": v(8.6, -17.68) * mm});
            skLineSegment(sketch, "E1857", {"start": v(8.6, -17.68) * mm, "end": v(8.73, -17.6) * mm});
            skLineSegment(sketch, "E1858", {"start": v(8.73, -17.6) * mm, "end": v(8.86, -17.53) * mm});
            skLineSegment(sketch, "E1859", {"start": v(8.86, -17.53) * mm, "end": v(9, -17.46) * mm});
            skLineSegment(sketch, "E1860", {"start": v(9, -17.46) * mm, "end": v(9.13, -17.38) * mm});
            skLineSegment(sketch, "E1861", {"start": v(9.13, -17.38) * mm, "end": v(9.27, -17.3) * mm});
            skLineSegment(sketch, "E1862", {"start": v(9.27, -17.3) * mm, "end": v(9.4, -17.24) * mm});
            skLineSegment(sketch, "E1863", {"start": v(9.4, -17.24) * mm, "end": v(9.54, -17.16) * mm});
            skLineSegment(sketch, "E1864", {"start": v(9.54, -17.16) * mm, "end": v(9.57, -17.15) * mm});
            skLineSegment(sketch, "E1865", {"start": v(9.57, -17.15) * mm, "end": v(9.65, -17.28) * mm});
            skLineSegment(sketch, "E1866", {"start": v(9.65, -17.28) * mm, "end": v(9.73, -17.4) * mm});
            skLineSegment(sketch, "E1867", {"start": v(9.73, -17.4) * mm, "end": v(9.8, -17.54) * mm});
            skLineSegment(sketch, "E1868", {"start": v(9.8, -17.54) * mm, "end": v(9.89, -17.67) * mm});
            skLineSegment(sketch, "E1869", {"start": v(9.89, -17.67) * mm, "end": v(9.96, -17.8) * mm});
            skLineSegment(sketch, "E1870", {"start": v(9.96, -17.8) * mm, "end": v(10.04, -17.94) * mm});
            skLineSegment(sketch, "E1871", {"start": v(10.04, -17.94) * mm, "end": v(10.12, -18.07) * mm});
            skLineSegment(sketch, "E1872", {"start": v(10.12, -18.07) * mm, "end": v(10.2, -18.2) * mm});
            skLineSegment(sketch, "E1873", {"start": v(10.2, -18.2) * mm, "end": v(10.28, -18.33) * mm});
            skLineSegment(sketch, "E1874", {"start": v(10.28, -18.33) * mm, "end": v(10.36, -18.46) * mm});
            skLineSegment(sketch, "E1875", {"start": v(10.36, -18.46) * mm, "end": v(10.44, -18.6) * mm});
            skLineSegment(sketch, "E1876", {"start": v(10.44, -18.6) * mm, "end": v(10.52, -18.73) * mm});
            skLineSegment(sketch, "E1877", {"start": v(10.52, -18.73) * mm, "end": v(10.6, -18.87) * mm});
            skLineSegment(sketch, "E1878", {"start": v(10.6, -18.87) * mm, "end": v(10.72, -18.99) * mm});
            skLineSegment(sketch, "E1879", {"start": v(10.72, -18.99) * mm, "end": v(10.86, -19.08) * mm});
            skLineSegment(sketch, "E1880", {"start": v(10.86, -19.08) * mm, "end": v(11.02, -19.12) * mm});
            skLineSegment(sketch, "E1881", {"start": v(11.02, -19.12) * mm, "end": v(11.18, -19.13) * mm});
            skLineSegment(sketch, "E1882", {"start": v(11.18, -19.13) * mm, "end": v(11.34, -19.1) * mm});
            skLineSegment(sketch, "E1883", {"start": v(11.34, -19.1) * mm, "end": v(11.46, -19.03) * mm});
            skLineSegment(sketch, "E1884", {"start": v(11.46, -19.03) * mm, "end": v(11.58, -18.93) * mm});
            skLineSegment(sketch, "E1885", {"start": v(11.58, -18.93) * mm, "end": v(11.68, -18.8) * mm});
            skLineSegment(sketch, "E1886", {"start": v(11.68, -18.8) * mm, "end": v(11.73, -18.64) * mm});
            skLineSegment(sketch, "E1887", {"start": v(11.73, -18.64) * mm, "end": v(11.74, -18.47) * mm});
            skLineSegment(sketch, "E1888", {"start": v(11.74, -18.47) * mm, "end": v(11.71, -18.31) * mm});
            skLineSegment(sketch, "E1889", {"start": v(11.71, -18.31) * mm, "end": v(11.64, -18.16) * mm});
            skLineSegment(sketch, "E1890", {"start": v(11.64, -18.16) * mm, "end": v(11.55, -18.04) * mm});
            skLineSegment(sketch, "E1891", {"start": v(11.55, -18.04) * mm, "end": v(11.47, -17.9) * mm});
            skLineSegment(sketch, "E1892", {"start": v(11.47, -17.9) * mm, "end": v(11.38, -17.78) * mm});
            skLineSegment(sketch, "E1893", {"start": v(11.38, -17.78) * mm, "end": v(11.3, -17.66) * mm});
            skLineSegment(sketch, "E1894", {"start": v(11.3, -17.66) * mm, "end": v(11.2, -17.53) * mm});
            skLineSegment(sketch, "E1895", {"start": v(11.2, -17.53) * mm, "end": v(11.12, -17.4) * mm});
            skLineSegment(sketch, "E1896", {"start": v(11.12, -17.4) * mm, "end": v(11.03, -17.27) * mm});
            skLineSegment(sketch, "E1897", {"start": v(11.03, -17.27) * mm, "end": v(10.95, -17.15) * mm});
            skLineSegment(sketch, "E1898", {"start": v(10.95, -17.15) * mm, "end": v(10.86, -17.02) * mm});
            skLineSegment(sketch, "E1899", {"start": v(10.86, -17.02) * mm, "end": v(10.77, -16.9) * mm});
            skLineSegment(sketch, "E1900", {"start": v(10.77, -16.9) * mm, "end": v(10.69, -16.77) * mm});
            skLineSegment(sketch, "E1901", {"start": v(10.69, -16.77) * mm, "end": v(10.6, -16.64) * mm});
            skLineSegment(sketch, "E1902", {"start": v(10.6, -16.64) * mm, "end": v(10.53, -16.53) * mm});
            skLineSegment(sketch, "E1903", {"start": v(10.53, -16.53) * mm, "end": v(10.65, -16.44) * mm});
            skLineSegment(sketch, "E1904", {"start": v(10.65, -16.44) * mm, "end": v(10.77, -16.35) * mm});
            skLineSegment(sketch, "E1905", {"start": v(10.77, -16.35) * mm, "end": v(10.9, -16.25) * mm});
            skLineSegment(sketch, "E1906", {"start": v(10.9, -16.25) * mm, "end": v(11.02, -16.16) * mm});
            skLineSegment(sketch, "E1907", {"start": v(11.02, -16.16) * mm, "end": v(11.14, -16.07) * mm});
            skLineSegment(sketch, "E1908", {"start": v(11.14, -16.07) * mm, "end": v(11.26, -15.98) * mm});
            skLineSegment(sketch, "E1909", {"start": v(11.26, -15.98) * mm, "end": v(11.38, -15.89) * mm});
            skLineSegment(sketch, "E1910", {"start": v(11.38, -15.89) * mm, "end": v(11.5, -15.8) * mm});
            skLineSegment(sketch, "E1911", {"start": v(11.5, -15.8) * mm, "end": v(11.63, -15.7) * mm});
            skLineSegment(sketch, "E1912", {"start": v(11.63, -15.7) * mm, "end": v(11.75, -15.61) * mm});
            skLineSegment(sketch, "E1913", {"start": v(11.75, -15.61) * mm, "end": v(11.87, -15.52) * mm});
            skLineSegment(sketch, "E1914", {"start": v(11.87, -15.52) * mm, "end": v(11.9, -15.5) * mm});
            skLineSegment(sketch, "E1915", {"start": v(11.9, -15.5) * mm, "end": v(12, -15.62) * mm});
            skLineSegment(sketch, "E1916", {"start": v(12, -15.62) * mm, "end": v(12.1, -15.74) * mm});
            skLineSegment(sketch, "E1917", {"start": v(12.1, -15.74) * mm, "end": v(12.2, -15.86) * mm});
            skLineSegment(sketch, "E1918", {"start": v(12.2, -15.86) * mm, "end": v(12.3, -15.97) * mm});
            skLineSegment(sketch, "E1919", {"start": v(12.3, -15.97) * mm, "end": v(12.39, -16.1) * mm});
            skLineSegment(sketch, "E1920", {"start": v(12.39, -16.1) * mm, "end": v(12.49, -16.21) * mm});
            skLineSegment(sketch, "E1921", {"start": v(12.49, -16.21) * mm, "end": v(12.58, -16.33) * mm});
            skLineSegment(sketch, "E1922", {"start": v(12.58, -16.33) * mm, "end": v(12.68, -16.45) * mm});
            skLineSegment(sketch, "E1923", {"start": v(12.68, -16.45) * mm, "end": v(12.78, -16.57) * mm});
            skLineSegment(sketch, "E1924", {"start": v(12.78, -16.57) * mm, "end": v(12.88, -16.69) * mm});
            skLineSegment(sketch, "E1925", {"start": v(12.88, -16.69) * mm, "end": v(12.97, -16.8) * mm});
            skLineSegment(sketch, "E1926", {"start": v(12.97, -16.8) * mm, "end": v(13.07, -16.93) * mm});
            skLineSegment(sketch, "E1927", {"start": v(13.07, -16.93) * mm, "end": v(13.18, -17.05) * mm});
            skLineSegment(sketch, "E1928", {"start": v(13.18, -17.05) * mm, "end": v(13.3, -17.16) * mm});
            skLineSegment(sketch, "E1929", {"start": v(13.3, -17.16) * mm, "end": v(13.45, -17.23) * mm});
            skLineSegment(sketch, "E1930", {"start": v(13.45, -17.23) * mm, "end": v(13.62, -17.25) * mm});
            skLineSegment(sketch, "E1931", {"start": v(13.62, -17.25) * mm, "end": v(13.78, -17.23) * mm});
            skLineSegment(sketch, "E1932", {"start": v(13.78, -17.23) * mm, "end": v(13.93, -17.17) * mm});
            skLineSegment(sketch, "E1933", {"start": v(13.93, -17.17) * mm, "end": v(14.04, -17.1) * mm});
            skLineSegment(sketch, "E1934", {"start": v(14.04, -17.1) * mm, "end": v(14.15, -16.98) * mm});
            skLineSegment(sketch, "E1935", {"start": v(14.15, -16.98) * mm, "end": v(14.22, -16.83) * mm});
            skLineSegment(sketch, "E1936", {"start": v(14.22, -16.83) * mm, "end": v(14.26, -16.67) * mm});
            skLineSegment(sketch, "E1937", {"start": v(14.26, -16.67) * mm, "end": v(14.25, -16.5) * mm});
            skLineSegment(sketch, "E1938", {"start": v(14.25, -16.5) * mm, "end": v(14.2, -16.35) * mm});
            skLineSegment(sketch, "E1939", {"start": v(14.2, -16.35) * mm, "end": v(14.1, -16.21) * mm});
            skLineSegment(sketch, "E1940", {"start": v(14.1, -16.21) * mm, "end": v(14, -16.1) * mm});
            skLineSegment(sketch, "E1941", {"start": v(14, -16.1) * mm, "end": v(13.9, -15.99) * mm});
            skLineSegment(sketch, "E1942", {"start": v(13.9, -15.99) * mm, "end": v(13.79, -15.87) * mm});
            skLineSegment(sketch, "E1943", {"start": v(13.79, -15.87) * mm, "end": v(13.68, -15.76) * mm});
            skLineSegment(sketch, "E1944", {"start": v(13.68, -15.76) * mm, "end": v(13.58, -15.65) * mm});
            skLineSegment(sketch, "E1945", {"start": v(13.58, -15.65) * mm, "end": v(13.48, -15.53) * mm});
            skLineSegment(sketch, "E1946", {"start": v(13.48, -15.53) * mm, "end": v(13.37, -15.42) * mm});
            skLineSegment(sketch, "E1947", {"start": v(13.37, -15.42) * mm, "end": v(13.27, -15.3) * mm});
            skLineSegment(sketch, "E1948", {"start": v(13.27, -15.3) * mm, "end": v(13.16, -15.2) * mm});
            skLineSegment(sketch, "E1949", {"start": v(13.16, -15.2) * mm, "end": v(13.06, -15.08) * mm});
            skLineSegment(sketch, "E1950", {"start": v(13.06, -15.08) * mm, "end": v(12.96, -14.96) * mm});
            skLineSegment(sketch, "E1951", {"start": v(12.96, -14.96) * mm, "end": v(12.85, -14.85) * mm});
            skLineSegment(sketch, "E1952", {"start": v(12.85, -14.85) * mm, "end": v(12.76, -14.75) * mm});
            skLineSegment(sketch, "E1953", {"start": v(12.76, -14.75) * mm, "end": v(12.87, -14.65) * mm});
            skLineSegment(sketch, "E1954", {"start": v(12.87, -14.65) * mm, "end": v(12.98, -14.54) * mm});
            skLineSegment(sketch, "E1955", {"start": v(12.98, -14.54) * mm, "end": v(13.09, -14.43) * mm});
            skLineSegment(sketch, "E1956", {"start": v(13.09, -14.43) * mm, "end": v(13.2, -14.32) * mm});
            skLineSegment(sketch, "E1957", {"start": v(13.2, -14.32) * mm, "end": v(13.3, -14.21) * mm});
            skLineSegment(sketch, "E1958", {"start": v(13.3, -14.21) * mm, "end": v(13.41, -14.1) * mm});
            skLineSegment(sketch, "E1959", {"start": v(13.41, -14.1) * mm, "end": v(13.52, -14) * mm});
            skLineSegment(sketch, "E1960", {"start": v(13.52, -14) * mm, "end": v(13.63, -13.89) * mm});
            skLineSegment(sketch, "E1961", {"start": v(13.63, -13.89) * mm, "end": v(13.74, -13.78) * mm});
            skLineSegment(sketch, "E1962", {"start": v(13.74, -13.78) * mm, "end": v(13.85, -13.67) * mm});
            skLineSegment(sketch, "E1963", {"start": v(13.85, -13.67) * mm, "end": v(13.95, -13.56) * mm});
            skLineSegment(sketch, "E1964", {"start": v(13.95, -13.56) * mm, "end": v(13.98, -13.54) * mm});
            skLineSegment(sketch, "E1965", {"start": v(13.98, -13.54) * mm, "end": v(14.1, -13.64) * mm});
            skLineSegment(sketch, "E1966", {"start": v(14.1, -13.64) * mm, "end": v(14.2, -13.74) * mm});
            skLineSegment(sketch, "E1967", {"start": v(14.2, -13.74) * mm, "end": v(14.32, -13.85) * mm});
            skLineSegment(sketch, "E1968", {"start": v(14.32, -13.85) * mm, "end": v(14.43, -13.95) * mm});
            skLineSegment(sketch, "E1969", {"start": v(14.43, -13.95) * mm, "end": v(14.54, -14.06) * mm});
            skLineSegment(sketch, "E1970", {"start": v(14.54, -14.06) * mm, "end": v(14.66, -14.16) * mm});
            skLineSegment(sketch, "E1971", {"start": v(14.66, -14.16) * mm, "end": v(14.77, -14.26) * mm});
            skLineSegment(sketch, "E1972", {"start": v(14.77, -14.26) * mm, "end": v(14.88, -14.37) * mm});
            skLineSegment(sketch, "E1973", {"start": v(14.88, -14.37) * mm, "end": v(15, -14.47) * mm});
            skLineSegment(sketch, "E1974", {"start": v(15, -14.47) * mm, "end": v(15.11, -14.58) * mm});
            skLineSegment(sketch, "E1975", {"start": v(15.11, -14.58) * mm, "end": v(15.22, -14.68) * mm});
            skLineSegment(sketch, "E1976", {"start": v(15.22, -14.68) * mm, "end": v(15.34, -14.78) * mm});
            skLineSegment(sketch, "E1977", {"start": v(15.34, -14.78) * mm, "end": v(15.46, -14.9) * mm});
            skLineSegment(sketch, "E1978", {"start": v(15.46, -14.9) * mm, "end": v(15.6, -14.98) * mm});
            skLineSegment(sketch, "E1979", {"start": v(15.6, -14.98) * mm, "end": v(15.76, -15.03) * mm});
            skLineSegment(sketch, "E1980", {"start": v(15.76, -15.03) * mm, "end": v(15.93, -15.03) * mm});
            skLineSegment(sketch, "E1981", {"start": v(15.93, -15.03) * mm, "end": v(16.09, -14.99) * mm});
            skLineSegment(sketch, "E1982", {"start": v(16.09, -14.99) * mm, "end": v(16.23, -14.9) * mm});
            skLineSegment(sketch, "E1983", {"start": v(16.23, -14.9) * mm, "end": v(16.32, -14.82) * mm});
            skLineSegment(sketch, "E1984", {"start": v(16.32, -14.82) * mm, "end": v(16.42, -14.68) * mm});
            skLineSegment(sketch, "E1985", {"start": v(16.42, -14.68) * mm, "end": v(16.47, -14.52) * mm});
            skLineSegment(sketch, "E1986", {"start": v(16.47, -14.52) * mm, "end": v(16.48, -14.36) * mm});
            skLineSegment(sketch, "E1987", {"start": v(16.48, -14.36) * mm, "end": v(16.44, -14.2) * mm});
            skLineSegment(sketch, "E1988", {"start": v(16.44, -14.2) * mm, "end": v(16.37, -14.05) * mm});
            skLineSegment(sketch, "E1989", {"start": v(16.37, -14.05) * mm, "end": v(16.26, -13.93) * mm});
            skLineSegment(sketch, "E1990", {"start": v(16.26, -13.93) * mm, "end": v(16.14, -13.83) * mm});
            skLineSegment(sketch, "E1991", {"start": v(16.14, -13.83) * mm, "end": v(16.02, -13.74) * mm});
            skLineSegment(sketch, "E1992", {"start": v(16.02, -13.74) * mm, "end": v(15.9, -13.64) * mm});
            skLineSegment(sketch, "E1993", {"start": v(15.9, -13.64) * mm, "end": v(15.78, -13.54) * mm});
            skLineSegment(sketch, "E1994", {"start": v(15.78, -13.54) * mm, "end": v(15.66, -13.44) * mm});
            skLineSegment(sketch, "E1995", {"start": v(15.66, -13.44) * mm, "end": v(15.54, -13.34) * mm});
            skLineSegment(sketch, "E1996", {"start": v(15.54, -13.34) * mm, "end": v(15.42, -13.25) * mm});
            skLineSegment(sketch, "E1997", {"start": v(15.42, -13.25) * mm, "end": v(15.3, -13.15) * mm});
            skLineSegment(sketch, "E1998", {"start": v(15.3, -13.15) * mm, "end": v(15.18, -13.05) * mm});
            skLineSegment(sketch, "E1999", {"start": v(15.18, -13.05) * mm, "end": v(15.07, -12.96) * mm});
            skLineSegment(sketch, "E2000", {"start": v(15.07, -12.96) * mm, "end": v(14.95, -12.86) * mm});
            skLineSegment(sketch, "E2001", {"start": v(14.95, -12.86) * mm, "end": v(14.83, -12.76) * mm});
            skLineSegment(sketch, "E2002", {"start": v(14.83, -12.76) * mm, "end": v(14.72, -12.68) * mm});
            skLineSegment(sketch, "E2003", {"start": v(14.72, -12.68) * mm, "end": v(14.82, -12.55) * mm});
            skLineSegment(sketch, "E2004", {"start": v(14.82, -12.55) * mm, "end": v(14.9, -12.43) * mm});
            skLineSegment(sketch, "E2005", {"start": v(14.9, -12.43) * mm, "end": v(15, -12.3) * mm});
            skLineSegment(sketch, "E2006", {"start": v(15, -12.3) * mm, "end": v(15.1, -12.19) * mm});
            skLineSegment(sketch, "E2007", {"start": v(15.1, -12.19) * mm, "end": v(15.18, -12.06) * mm});
            skLineSegment(sketch, "E2008", {"start": v(15.18, -12.06) * mm, "end": v(15.27, -11.94) * mm});
            skLineSegment(sketch, "E2009", {"start": v(15.27, -11.94) * mm, "end": v(15.37, -11.82) * mm});
            skLineSegment(sketch, "E2010", {"start": v(15.37, -11.82) * mm, "end": v(15.46, -11.7) * mm});
            skLineSegment(sketch, "E2011", {"start": v(15.46, -11.7) * mm, "end": v(15.55, -11.57) * mm});
            skLineSegment(sketch, "E2012", {"start": v(15.55, -11.57) * mm, "end": v(15.64, -11.45) * mm});
            skLineSegment(sketch, "E2013", {"start": v(15.64, -11.45) * mm, "end": v(15.73, -11.33) * mm});
            skLineSegment(sketch, "E2014", {"start": v(15.73, -11.33) * mm, "end": v(15.76, -11.3) * mm});
            skLineSegment(sketch, "E2015", {"start": v(15.76, -11.3) * mm, "end": v(15.88, -11.39) * mm});
            skLineSegment(sketch, "E2016", {"start": v(15.88, -11.39) * mm, "end": v(16, -11.47) * mm});
            skLineSegment(sketch, "E2017", {"start": v(16, -11.47) * mm, "end": v(16.14, -11.56) * mm});
            skLineSegment(sketch, "E2018", {"start": v(16.14, -11.56) * mm, "end": v(16.26, -11.65) * mm});
            skLineSegment(sketch, "E2019", {"start": v(16.26, -11.65) * mm, "end": v(16.39, -11.73) * mm});
            skLineSegment(sketch, "E2020", {"start": v(16.39, -11.73) * mm, "end": v(16.52, -11.82) * mm});
            skLineSegment(sketch, "E2021", {"start": v(16.52, -11.82) * mm, "end": v(16.64, -11.9) * mm});
            skLineSegment(sketch, "E2022", {"start": v(16.64, -11.9) * mm, "end": v(16.77, -12) * mm});
            skLineSegment(sketch, "E2023", {"start": v(16.77, -12) * mm, "end": v(16.9, -12.08) * mm});
            skLineSegment(sketch, "E2024", {"start": v(16.9, -12.08) * mm, "end": v(17.02, -12.17) * mm});
            skLineSegment(sketch, "E2025", {"start": v(17.02, -12.17) * mm, "end": v(17.15, -12.25) * mm});
            skLineSegment(sketch, "E2026", {"start": v(17.15, -12.25) * mm, "end": v(17.28, -12.34) * mm});
            skLineSegment(sketch, "E2027", {"start": v(17.28, -12.34) * mm, "end": v(17.42, -12.43) * mm});
            skLineSegment(sketch, "E2028", {"start": v(17.42, -12.43) * mm, "end": v(17.57, -12.5) * mm});
            skLineSegment(sketch, "E2029", {"start": v(17.57, -12.5) * mm, "end": v(17.73, -12.52) * mm});
            skLineSegment(sketch, "E2030", {"start": v(17.73, -12.52) * mm, "end": v(17.9, -12.5) * mm});
            skLineSegment(sketch, "E2031", {"start": v(17.9, -12.5) * mm, "end": v(18.05, -12.44) * mm});
            skLineSegment(sketch, "E2032", {"start": v(18.05, -12.44) * mm, "end": v(18.18, -12.34) * mm});
            skLineSegment(sketch, "E2033", {"start": v(18.18, -12.34) * mm, "end": v(18.26, -12.23) * mm});
            skLineSegment(sketch, "E2034", {"start": v(18.26, -12.23) * mm, "end": v(18.33, -12.08) * mm});
            skLineSegment(sketch, "E2035", {"start": v(18.33, -12.08) * mm, "end": v(18.36, -11.92) * mm});
            skLineSegment(sketch, "E2036", {"start": v(18.36, -11.92) * mm, "end": v(18.34, -11.76) * mm});
            skLineSegment(sketch, "E2037", {"start": v(18.34, -11.76) * mm, "end": v(18.29, -11.6) * mm});
            skLineSegment(sketch, "E2038", {"start": v(18.29, -11.6) * mm, "end": v(18.2, -11.47) * mm});
            skLineSegment(sketch, "E2039", {"start": v(18.2, -11.47) * mm, "end": v(18.06, -11.36) * mm});
            skLineSegment(sketch, "E2040", {"start": v(18.06, -11.36) * mm, "end": v(17.93, -11.28) * mm});
            skLineSegment(sketch, "E2041", {"start": v(17.93, -11.28) * mm, "end": v(17.8, -11.2) * mm});
            skLineSegment(sketch, "E2042", {"start": v(17.8, -11.2) * mm, "end": v(17.67, -11.13) * mm});
            skLineSegment(sketch, "E2043", {"start": v(17.67, -11.13) * mm, "end": v(17.54, -11.05) * mm});
            skLineSegment(sketch, "E2044", {"start": v(17.54, -11.05) * mm, "end": v(17.4, -10.97) * mm});
            skLineSegment(sketch, "E2045", {"start": v(17.4, -10.97) * mm, "end": v(17.27, -10.89) * mm});
            skLineSegment(sketch, "E2046", {"start": v(17.27, -10.89) * mm, "end": v(17.14, -10.8) * mm});
            skLineSegment(sketch, "E2047", {"start": v(17.14, -10.8) * mm, "end": v(17.01, -10.73) * mm});
            skLineSegment(sketch, "E2048", {"start": v(17.01, -10.73) * mm, "end": v(16.88, -10.65) * mm});
            skLineSegment(sketch, "E2049", {"start": v(16.88, -10.65) * mm, "end": v(16.75, -10.57) * mm});
            skLineSegment(sketch, "E2050", {"start": v(16.75, -10.57) * mm, "end": v(16.62, -10.5) * mm});
            skLineSegment(sketch, "E2051", {"start": v(16.62, -10.5) * mm, "end": v(16.48, -10.41) * mm});
            skLineSegment(sketch, "E2052", {"start": v(16.48, -10.41) * mm, "end": v(16.37, -10.34) * mm});
            skLineSegment(sketch, "E2053", {"start": v(16.37, -10.34) * mm, "end": v(16.44, -10.2) * mm});
            skLineSegment(sketch, "E2054", {"start": v(16.44, -10.2) * mm, "end": v(16.52, -10.07) * mm});
            skLineSegment(sketch, "E2055", {"start": v(16.52, -10.07) * mm, "end": v(16.6, -9.94) * mm});
            skLineSegment(sketch, "E2056", {"start": v(16.6, -9.94) * mm, "end": v(16.66, -9.8) * mm});
            skLineSegment(sketch, "E2057", {"start": v(16.66, -9.8) * mm, "end": v(16.74, -9.67) * mm});
            skLineSegment(sketch, "E2058", {"start": v(16.74, -9.67) * mm, "end": v(16.81, -9.54) * mm});
            skLineSegment(sketch, "E2059", {"start": v(16.81, -9.54) * mm, "end": v(16.88, -9.4) * mm});
            skLineSegment(sketch, "E2060", {"start": v(16.88, -9.4) * mm, "end": v(16.96, -9.27) * mm});
            skLineSegment(sketch, "E2061", {"start": v(16.96, -9.27) * mm, "end": v(17.03, -9.13) * mm});
            skLineSegment(sketch, "E2062", {"start": v(17.03, -9.13) * mm, "end": v(17.1, -9) * mm});
            skLineSegment(sketch, "E2063", {"start": v(17.1, -9) * mm, "end": v(17.18, -8.86) * mm});
            skLineSegment(sketch, "E2064", {"start": v(17.18, -8.86) * mm, "end": v(17.2, -8.83) * mm});
            skLineSegment(sketch, "E2065", {"start": v(17.2, -8.83) * mm, "end": v(17.33, -8.9) * mm});
            skLineSegment(sketch, "E2066", {"start": v(17.33, -8.9) * mm, "end": v(17.47, -8.97) * mm});
            skLineSegment(sketch, "E2067", {"start": v(17.47, -8.97) * mm, "end": v(17.6, -9.04) * mm});
            skLineSegment(sketch, "E2068", {"start": v(17.6, -9.04) * mm, "end": v(17.75, -9.1) * mm});
            skLineSegment(sketch, "E2069", {"start": v(17.75, -9.1) * mm, "end": v(17.88, -9.17) * mm});
            skLineSegment(sketch, "E2070", {"start": v(17.88, -9.17) * mm, "end": v(18.02, -9.24) * mm});
            skLineSegment(sketch, "E2071", {"start": v(18.02, -9.24) * mm, "end": v(18.16, -9.3) * mm});
            skLineSegment(sketch, "E2072", {"start": v(18.16, -9.3) * mm, "end": v(18.3, -9.37) * mm});
            skLineSegment(sketch, "E2073", {"start": v(18.3, -9.37) * mm, "end": v(18.44, -9.44) * mm});
            skLineSegment(sketch, "E2074", {"start": v(18.44, -9.44) * mm, "end": v(18.58, -9.51) * mm});
            skLineSegment(sketch, "E2075", {"start": v(18.58, -9.51) * mm, "end": v(18.71, -9.58) * mm});
            skLineSegment(sketch, "E2076", {"start": v(18.71, -9.58) * mm, "end": v(18.85, -9.65) * mm});
            skLineSegment(sketch, "E2077", {"start": v(18.85, -9.65) * mm, "end": v(19, -9.72) * mm});
            skLineSegment(sketch, "E2078", {"start": v(19, -9.72) * mm, "end": v(19.16, -9.76) * mm});
            skLineSegment(sketch, "E2079", {"start": v(19.16, -9.76) * mm, "end": v(19.32, -9.76) * mm});
            skLineSegment(sketch, "E2080", {"start": v(19.32, -9.76) * mm, "end": v(19.48, -9.71) * mm});
            skLineSegment(sketch, "E2081", {"start": v(19.48, -9.71) * mm, "end": v(19.62, -9.63) * mm});
            skLineSegment(sketch, "E2082", {"start": v(19.62, -9.63) * mm, "end": v(19.74, -9.51) * mm});
            skLineSegment(sketch, "E2083", {"start": v(19.74, -9.51) * mm, "end": v(19.8, -9.4) * mm});
            skLineSegment(sketch, "E2084", {"start": v(19.8, -9.4) * mm, "end": v(19.85, -9.24) * mm});
            skLineSegment(sketch, "E2085", {"start": v(19.85, -9.24) * mm, "end": v(19.86, -9.08) * mm});
            skLineSegment(sketch, "E2086", {"start": v(19.86, -9.08) * mm, "end": v(19.82, -8.92) * mm});
            skLineSegment(sketch, "E2087", {"start": v(19.82, -8.92) * mm, "end": v(19.74, -8.77) * mm});
            skLineSegment(sketch, "E2088", {"start": v(19.74, -8.77) * mm, "end": v(19.63, -8.65) * mm});
            skLineSegment(sketch, "E2089", {"start": v(19.63, -8.65) * mm, "end": v(19.49, -8.57) * mm});
            skLineSegment(sketch, "E2090", {"start": v(19.49, -8.57) * mm, "end": v(19.35, -8.5) * mm});
            skLineSegment(sketch, "E2091", {"start": v(19.35, -8.5) * mm, "end": v(19.2, -8.45) * mm});
            skLineSegment(sketch, "E2092", {"start": v(19.2, -8.45) * mm, "end": v(19.06, -8.39) * mm});
            skLineSegment(sketch, "E2093", {"start": v(19.06, -8.39) * mm, "end": v(18.92, -8.33) * mm});
            skLineSegment(sketch, "E2094", {"start": v(18.92, -8.33) * mm, "end": v(18.78, -8.27) * mm});
            skLineSegment(sketch, "E2095", {"start": v(18.78, -8.27) * mm, "end": v(18.64, -8.2) * mm});
            skLineSegment(sketch, "E2096", {"start": v(18.64, -8.2) * mm, "end": v(18.5, -8.15) * mm});
            skLineSegment(sketch, "E2097", {"start": v(18.5, -8.15) * mm, "end": v(18.36, -8.09) * mm});
            skLineSegment(sketch, "E2098", {"start": v(18.36, -8.09) * mm, "end": v(18.21, -8.03) * mm});
            skLineSegment(sketch, "E2099", {"start": v(18.21, -8.03) * mm, "end": v(18.07, -7.97) * mm});
            skLineSegment(sketch, "E2100", {"start": v(18.07, -7.97) * mm, "end": v(17.93, -7.9) * mm});
            skLineSegment(sketch, "E2101", {"start": v(17.93, -7.9) * mm, "end": v(17.79, -7.85) * mm});
            skLineSegment(sketch, "E2102", {"start": v(17.79, -7.85) * mm, "end": v(17.67, -7.8) * mm});
            skLineSegment(sketch, "E2103", {"start": v(17.67, -7.8) * mm, "end": v(17.72, -7.65) * mm});
            skLineSegment(sketch, "E2104", {"start": v(17.72, -7.65) * mm, "end": v(17.77, -7.5) * mm});
            skLineSegment(sketch, "E2105", {"start": v(17.77, -7.5) * mm, "end": v(17.83, -7.37) * mm});
            skLineSegment(sketch, "E2106", {"start": v(17.83, -7.37) * mm, "end": v(17.88, -7.22) * mm});
            skLineSegment(sketch, "E2107", {"start": v(17.88, -7.22) * mm, "end": v(17.94, -7.08) * mm});
            skLineSegment(sketch, "E2108", {"start": v(17.94, -7.08) * mm, "end": v(17.99, -6.94) * mm});
            skLineSegment(sketch, "E2109", {"start": v(17.99, -6.94) * mm, "end": v(18.04, -6.8) * mm});
            skLineSegment(sketch, "E2110", {"start": v(18.04, -6.8) * mm, "end": v(18.1, -6.65) * mm});
            skLineSegment(sketch, "E2111", {"start": v(18.1, -6.65) * mm, "end": v(18.15, -6.5) * mm});
            skLineSegment(sketch, "E2112", {"start": v(18.15, -6.5) * mm, "end": v(18.2, -6.36) * mm});
            skLineSegment(sketch, "E2113", {"start": v(18.2, -6.36) * mm, "end": v(18.26, -6.22) * mm});
            skLineSegment(sketch, "E2114", {"start": v(18.26, -6.22) * mm, "end": v(18.27, -6.19) * mm});
            skLineSegment(sketch, "E2115", {"start": v(18.27, -6.19) * mm, "end": v(18.41, -6.23) * mm});
            skLineSegment(sketch, "E2116", {"start": v(18.41, -6.23) * mm, "end": v(18.56, -6.28) * mm});
            skLineSegment(sketch, "E2117", {"start": v(18.56, -6.28) * mm, "end": v(18.7, -6.33) * mm});
            skLineSegment(sketch, "E2118", {"start": v(18.7, -6.33) * mm, "end": v(18.85, -6.37) * mm});
            skLineSegment(sketch, "E2119", {"start": v(18.85, -6.37) * mm, "end": v(19, -6.42) * mm});
            skLineSegment(sketch, "E2120", {"start": v(19, -6.42) * mm, "end": v(19.15, -6.47) * mm});
            skLineSegment(sketch, "E2121", {"start": v(19.15, -6.47) * mm, "end": v(19.3, -6.52) * mm});
            skLineSegment(sketch, "E2122", {"start": v(19.3, -6.52) * mm, "end": v(19.44, -6.56) * mm});
            skLineSegment(sketch, "E2123", {"start": v(19.44, -6.56) * mm, "end": v(19.59, -6.61) * mm});
            skLineSegment(sketch, "E2124", {"start": v(19.59, -6.61) * mm, "end": v(19.73, -6.66) * mm});
            skLineSegment(sketch, "E2125", {"start": v(19.73, -6.66) * mm, "end": v(19.88, -6.7) * mm});
            skLineSegment(sketch, "E2126", {"start": v(19.88, -6.7) * mm, "end": v(20.02, -6.76) * mm});
            skLineSegment(sketch, "E2127", {"start": v(20.02, -6.76) * mm, "end": v(20.18, -6.8) * mm});
            skLineSegment(sketch, "E2128", {"start": v(20.18, -6.8) * mm, "end": v(20.35, -6.82) * mm});
            skLineSegment(sketch, "E2129", {"start": v(20.35, -6.82) * mm, "end": v(20.5, -6.8) * mm});
            skLineSegment(sketch, "E2130", {"start": v(20.5, -6.8) * mm, "end": v(20.66, -6.73) * mm});
            skLineSegment(sketch, "E2131", {"start": v(20.66, -6.73) * mm, "end": v(20.79, -6.63) * mm});
            skLineSegment(sketch, "E2132", {"start": v(20.79, -6.63) * mm, "end": v(20.88, -6.5) * mm});
            skLineSegment(sketch, "E2133", {"start": v(20.88, -6.5) * mm, "end": v(20.93, -6.37) * mm});
            skLineSegment(sketch, "E2134", {"start": v(20.93, -6.37) * mm, "end": v(20.96, -6.21) * mm});
            skLineSegment(sketch, "E2135", {"start": v(20.96, -6.21) * mm, "end": v(20.94, -6.05) * mm});
            skLineSegment(sketch, "E2136", {"start": v(20.94, -6.05) * mm, "end": v(20.88, -5.9) * mm});
            skLineSegment(sketch, "E2137", {"start": v(20.88, -5.9) * mm, "end": v(20.78, -5.76) * mm});
            skLineSegment(sketch, "E2138", {"start": v(20.78, -5.76) * mm, "end": v(20.65, -5.66) * mm});
            skLineSegment(sketch, "E2139", {"start": v(20.65, -5.66) * mm, "end": v(20.5, -5.6) * mm});
            skLineSegment(sketch, "E2140", {"start": v(20.5, -5.6) * mm, "end": v(20.35, -5.56) * mm});
            skLineSegment(sketch, "E2141", {"start": v(20.35, -5.56) * mm, "end": v(20.2, -5.52) * mm});
            skLineSegment(sketch, "E2142", {"start": v(20.2, -5.52) * mm, "end": v(20.06, -5.48) * mm});
            skLineSegment(sketch, "E2143", {"start": v(20.06, -5.48) * mm, "end": v(19.9, -5.44) * mm});
            skLineSegment(sketch, "E2144", {"start": v(19.9, -5.44) * mm, "end": v(19.76, -5.4) * mm});
            skLineSegment(sketch, "E2145", {"start": v(19.76, -5.4) * mm, "end": v(19.6, -5.36) * mm});
            skLineSegment(sketch, "E2146", {"start": v(19.6, -5.36) * mm, "end": v(19.46, -5.32) * mm});
            skLineSegment(sketch, "E2147", {"start": v(19.46, -5.32) * mm, "end": v(19.31, -5.28) * mm});
            skLineSegment(sketch, "E2148", {"start": v(19.31, -5.28) * mm, "end": v(19.16, -5.24) * mm});
            skLineSegment(sketch, "E2149", {"start": v(19.16, -5.24) * mm, "end": v(19.02, -5.2) * mm});
            skLineSegment(sketch, "E2150", {"start": v(19.02, -5.2) * mm, "end": v(18.87, -5.17) * mm});
            skLineSegment(sketch, "E2151", {"start": v(18.87, -5.17) * mm, "end": v(18.72, -5.13) * mm});
            skLineSegment(sketch, "E2152", {"start": v(18.72, -5.13) * mm, "end": v(18.59, -5.1) * mm});
            skLineSegment(sketch, "E2153", {"start": v(18.59, -5.1) * mm, "end": v(18.62, -4.94) * mm});
            skLineSegment(sketch, "E2154", {"start": v(18.62, -4.94) * mm, "end": v(18.65, -4.8) * mm});
            skLineSegment(sketch, "E2155", {"start": v(18.65, -4.8) * mm, "end": v(18.69, -4.64) * mm});
            skLineSegment(sketch, "E2156", {"start": v(18.69, -4.64) * mm, "end": v(18.72, -4.5) * mm});
            skLineSegment(sketch, "E2157", {"start": v(18.72, -4.5) * mm, "end": v(18.75, -4.34) * mm});
            skLineSegment(sketch, "E2158", {"start": v(18.75, -4.34) * mm, "end": v(18.79, -4.2) * mm});
            skLineSegment(sketch, "E2159", {"start": v(18.79, -4.2) * mm, "end": v(18.82, -4.05) * mm});
            skLineSegment(sketch, "E2160", {"start": v(18.82, -4.05) * mm, "end": v(18.85, -3.9) * mm});
            skLineSegment(sketch, "E2161", {"start": v(18.85, -3.9) * mm, "end": v(18.88, -3.75) * mm});
            skLineSegment(sketch, "E2162", {"start": v(18.88, -3.75) * mm, "end": v(18.92, -3.6) * mm});
            skLineSegment(sketch, "E2163", {"start": v(18.92, -3.6) * mm, "end": v(18.95, -3.45) * mm});
            skLineSegment(sketch, "E2164", {"start": v(18.95, -3.45) * mm, "end": v(18.96, -3.41) * mm});
            skLineSegment(sketch, "E2165", {"start": v(18.96, -3.41) * mm, "end": v(19.1, -3.44) * mm});
            skLineSegment(sketch, "E2166", {"start": v(19.1, -3.44) * mm, "end": v(19.26, -3.46) * mm});
            skLineSegment(sketch, "E2167", {"start": v(19.26, -3.46) * mm, "end": v(19.41, -3.5) * mm});
            skLineSegment(sketch, "E2168", {"start": v(19.41, -3.5) * mm, "end": v(19.56, -3.52) * mm});
            skLineSegment(sketch, "E2169", {"start": v(19.56, -3.52) * mm, "end": v(19.71, -3.54) * mm});
            skLineSegment(sketch, "E2170", {"start": v(19.71, -3.54) * mm, "end": v(19.86, -3.57) * mm});
            skLineSegment(sketch, "E2171", {"start": v(19.86, -3.57) * mm, "end": v(20.02, -3.6) * mm});
            skLineSegment(sketch, "E2172", {"start": v(20.02, -3.6) * mm, "end": v(20.17, -3.62) * mm});
            skLineSegment(sketch, "E2173", {"start": v(20.17, -3.62) * mm, "end": v(20.32, -3.65) * mm});
            skLineSegment(sketch, "E2174", {"start": v(20.32, -3.65) * mm, "end": v(20.47, -3.67) * mm});
            skLineSegment(sketch, "E2175", {"start": v(20.47, -3.67) * mm, "end": v(20.62, -3.7) * mm});
            skLineSegment(sketch, "E2176", {"start": v(20.62, -3.7) * mm, "end": v(20.77, -3.73) * mm});
            skLineSegment(sketch, "E2177", {"start": v(20.77, -3.73) * mm, "end": v(20.94, -3.75) * mm});
            skLineSegment(sketch, "E2178", {"start": v(20.94, -3.75) * mm, "end": v(21.1, -3.75) * mm});
            skLineSegment(sketch, "E2179", {"start": v(21.1, -3.75) * mm, "end": v(21.26, -3.7) * mm});
            skLineSegment(sketch, "E2180", {"start": v(21.26, -3.7) * mm, "end": v(21.4, -3.61) * mm});
            skLineSegment(sketch, "E2181", {"start": v(21.4, -3.61) * mm, "end": v(21.51, -3.5) * mm});
            skLineSegment(sketch, "E2182", {"start": v(21.51, -3.5) * mm, "end": v(21.59, -3.35) * mm});
            skLineSegment(sketch, "E2183", {"start": v(21.59, -3.35) * mm, "end": v(21.62, -3.19) * mm});
            skLineSegment(sketch, "E2184", {"start": v(21.62, -3.19) * mm, "end": v(21.62, -3.02) * mm});
            skLineSegment(sketch, "E2185", {"start": v(21.62, -3.02) * mm, "end": v(21.57, -2.87) * mm});
            skLineSegment(sketch, "E2186", {"start": v(21.57, -2.87) * mm, "end": v(21.48, -2.73) * mm});
            skLineSegment(sketch, "E2187", {"start": v(21.48, -2.73) * mm, "end": v(21.36, -2.62) * mm});
            skLineSegment(sketch, "E2188", {"start": v(21.36, -2.62) * mm, "end": v(21.21, -2.54) * mm});
            skLineSegment(sketch, "E2189", {"start": v(21.21, -2.54) * mm, "end": v(21.08, -2.51) * mm});
            skLineSegment(sketch, "E2190", {"start": v(21.08, -2.51) * mm, "end": v(20.93, -2.5) * mm});
            skLineSegment(sketch, "E2191", {"start": v(20.93, -2.5) * mm, "end": v(20.78, -2.48) * mm});
            skLineSegment(sketch, "E2192", {"start": v(20.78, -2.48) * mm, "end": v(20.62, -2.46) * mm});
            skLineSegment(sketch, "E2193", {"start": v(20.62, -2.46) * mm, "end": v(20.47, -2.44) * mm});
            skLineSegment(sketch, "E2194", {"start": v(20.47, -2.44) * mm, "end": v(20.32, -2.42) * mm});
            skLineSegment(sketch, "E2195", {"start": v(20.32, -2.42) * mm, "end": v(20.17, -2.4) * mm});
            skLineSegment(sketch, "E2196", {"start": v(20.17, -2.4) * mm, "end": v(20.01, -2.39) * mm});
            skLineSegment(sketch, "E2197", {"start": v(20.01, -2.39) * mm, "end": v(19.86, -2.37) * mm});
            skLineSegment(sketch, "E2198", {"start": v(19.86, -2.37) * mm, "end": v(19.7, -2.35) * mm});
            skLineSegment(sketch, "E2199", {"start": v(19.7, -2.35) * mm, "end": v(19.55, -2.34) * mm});
            skLineSegment(sketch, "E2200", {"start": v(19.55, -2.34) * mm, "end": v(19.4, -2.32) * mm});
            skLineSegment(sketch, "E2201", {"start": v(19.4, -2.32) * mm, "end": v(19.25, -2.3) * mm});
            skLineSegment(sketch, "E2202", {"start": v(19.25, -2.3) * mm, "end": v(19.12, -2.29) * mm});
            skLineSegment(sketch, "E2203", {"start": v(19.12, -2.29) * mm, "end": v(19.13, -2.13) * mm});
            skLineSegment(sketch, "E2204", {"start": v(19.13, -2.13) * mm, "end": v(19.14, -1.98) * mm});
            skLineSegment(sketch, "E2205", {"start": v(19.14, -1.98) * mm, "end": v(19.15, -1.83) * mm});
            skLineSegment(sketch, "E2206", {"start": v(19.15, -1.83) * mm, "end": v(19.16, -1.67) * mm});
            skLineSegment(sketch, "E2207", {"start": v(19.16, -1.67) * mm, "end": v(19.17, -1.52) * mm});
            skLineSegment(sketch, "E2208", {"start": v(19.17, -1.52) * mm, "end": v(19.18, -1.37) * mm});
            skLineSegment(sketch, "E2209", {"start": v(19.18, -1.37) * mm, "end": v(19.2, -1.22) * mm});
            skLineSegment(sketch, "E2210", {"start": v(19.2, -1.22) * mm, "end": v(19.2, -1.06) * mm});
            skLineSegment(sketch, "E2211", {"start": v(19.2, -1.06) * mm, "end": v(19.22, -0.91) * mm});
            skLineSegment(sketch, "E2212", {"start": v(19.22, -0.91) * mm, "end": v(19.23, -0.76) * mm});
            skLineSegment(sketch, "E2213", {"start": v(19.23, -0.76) * mm, "end": v(19.24, -0.6) * mm});
            skLineSegment(sketch, "E2214", {"start": v(19.24, -0.6) * mm, "end": v(19.24, -0.57) * mm});
            skLineSegment(sketch, "E2215", {"start": v(-18.61, 1.3) * mm, "end": v(-18.37, 1.4) * mm});
            skLineSegment(sketch, "E2216", {"start": v(-18.37, 1.4) * mm, "end": v(-18.12, 1.5) * mm});
            skLineSegment(sketch, "E2217", {"start": v(-18.12, 1.5) * mm, "end": v(-17.88, 1.6) * mm});
            skLineSegment(sketch, "E2218", {"start": v(-17.88, 1.6) * mm, "end": v(-17.64, 1.69) * mm});
            skLineSegment(sketch, "E2219", {"start": v(-17.64, 1.69) * mm, "end": v(-17.4, 1.77) * mm});
            skLineSegment(sketch, "E2220", {"start": v(-17.4, 1.77) * mm, "end": v(-17.15, 1.86) * mm});
            skLineSegment(sketch, "E2221", {"start": v(-17.15, 1.86) * mm, "end": v(-16.9, 1.94) * mm});
            skLineSegment(sketch, "E2222", {"start": v(-16.9, 1.94) * mm, "end": v(-16.66, 2.02) * mm});
            skLineSegment(sketch, "E2223", {"start": v(-16.66, 2.02) * mm, "end": v(-16.42, 2.1) * mm});
            skLineSegment(sketch, "E2224", {"start": v(-16.42, 2.1) * mm, "end": v(-16.17, 2.16) * mm});
            skLineSegment(sketch, "E2225", {"start": v(-16.17, 2.16) * mm, "end": v(-15.93, 2.23) * mm});
            skLineSegment(sketch, "E2226", {"start": v(-15.93, 2.23) * mm, "end": v(-15.68, 2.3) * mm});
            skLineSegment(sketch, "E2227", {"start": v(-15.68, 2.3) * mm, "end": v(-15.44, 2.36) * mm});
            skLineSegment(sketch, "E2228", {"start": v(-15.44, 2.36) * mm, "end": v(-15.2, 2.41) * mm});
            skLineSegment(sketch, "E2229", {"start": v(-15.2, 2.41) * mm, "end": v(-14.94, 2.47) * mm});
            skLineSegment(sketch, "E2230", {"start": v(-14.94, 2.47) * mm, "end": v(-14.7, 2.52) * mm});
            skLineSegment(sketch, "E2231", {"start": v(-14.7, 2.52) * mm, "end": v(-14.45, 2.57) * mm});
            skLineSegment(sketch, "E2232", {"start": v(-14.45, 2.57) * mm, "end": v(-14.2, 2.61) * mm});
            skLineSegment(sketch, "E2233", {"start": v(-14.2, 2.61) * mm, "end": v(-13.96, 2.65) * mm});
            skLineSegment(sketch, "E2234", {"start": v(-13.96, 2.65) * mm, "end": v(-13.7, 2.69) * mm});
            skLineSegment(sketch, "E2235", {"start": v(-13.7, 2.69) * mm, "end": v(-13.46, 2.72) * mm});
            skLineSegment(sketch, "E2236", {"start": v(-13.46, 2.72) * mm, "end": v(-13.21, 2.75) * mm});
            skLineSegment(sketch, "E2237", {"start": v(-13.21, 2.75) * mm, "end": v(-12.97, 2.78) * mm});
            skLineSegment(sketch, "E2238", {"start": v(-12.97, 2.78) * mm, "end": v(-12.72, 2.8) * mm});
            skLineSegment(sketch, "E2239", {"start": v(-12.72, 2.8) * mm, "end": v(-12.47, 2.82) * mm});
            skLineSegment(sketch, "E2240", {"start": v(-12.47, 2.82) * mm, "end": v(-12.22, 2.83) * mm});
            skLineSegment(sketch, "E2241", {"start": v(-12.22, 2.83) * mm, "end": v(-11.97, 2.85) * mm});
            skLineSegment(sketch, "E2242", {"start": v(-11.97, 2.85) * mm, "end": v(-11.72, 2.86) * mm});
            skLineSegment(sketch, "E2243", {"start": v(-11.72, 2.86) * mm, "end": v(-11.47, 2.86) * mm});
            skLineSegment(sketch, "E2244", {"start": v(-11.47, 2.86) * mm, "end": v(-11.22, 2.86) * mm});
            skLineSegment(sketch, "E2245", {"start": v(-11.22, 2.86) * mm, "end": v(-10.98, 2.86) * mm});
            skLineSegment(sketch, "E2246", {"start": v(-10.98, 2.86) * mm, "end": v(-10.73, 2.86) * mm});
            skLineSegment(sketch, "E2247", {"start": v(-10.73, 2.86) * mm, "end": v(-10.49, 2.85) * mm});
            skLineSegment(sketch, "E2248", {"start": v(-10.49, 2.85) * mm, "end": v(-10.24, 2.84) * mm});
            skLineSegment(sketch, "E2249", {"start": v(-10.24, 2.84) * mm, "end": v(-10, 2.82) * mm});
            skLineSegment(sketch, "E2250", {"start": v(-10, 2.82) * mm, "end": v(-9.75, 2.8) * mm});
            skLineSegment(sketch, "E2251", {"start": v(-9.75, 2.8) * mm, "end": v(-9.5, 2.78) * mm});
            skLineSegment(sketch, "E2252", {"start": v(-9.5, 2.78) * mm, "end": v(-9.26, 2.75) * mm});
            skLineSegment(sketch, "E2253", {"start": v(-9.26, 2.75) * mm, "end": v(-9.02, 2.72) * mm});
            skLineSegment(sketch, "E2254", {"start": v(-9.02, 2.72) * mm, "end": v(-8.77, 2.7) * mm});
            skLineSegment(sketch, "E2255", {"start": v(-8.77, 2.7) * mm, "end": v(-8.53, 2.66) * mm});
            skLineSegment(sketch, "E2256", {"start": v(-8.53, 2.66) * mm, "end": v(-8.29, 2.62) * mm});
            skLineSegment(sketch, "E2257", {"start": v(-8.29, 2.62) * mm, "end": v(-8.04, 2.57) * mm});
            skLineSegment(sketch, "E2258", {"start": v(-8.04, 2.57) * mm, "end": v(-7.8, 2.53) * mm});
            skLineSegment(sketch, "E2259", {"start": v(-7.8, 2.53) * mm, "end": v(-7.56, 2.48) * mm});
            skLineSegment(sketch, "E2260", {"start": v(-7.56, 2.48) * mm, "end": v(-7.31, 2.43) * mm});
            skLineSegment(sketch, "E2261", {"start": v(-7.31, 2.43) * mm, "end": v(-7.07, 2.37) * mm});
            skLineSegment(sketch, "E2262", {"start": v(-7.07, 2.37) * mm, "end": v(-6.83, 2.31) * mm});
            skLineSegment(sketch, "E2263", {"start": v(-6.83, 2.31) * mm, "end": v(-6.59, 2.25) * mm});
            skLineSegment(sketch, "E2264", {"start": v(-6.59, 2.25) * mm, "end": v(-6.35, 2.18) * mm});
            skLineSegment(sketch, "E2265", {"start": v(-6.35, 2.18) * mm, "end": v(-6.1, 2.11) * mm});
            skLineSegment(sketch, "E2266", {"start": v(-6.1, 2.11) * mm, "end": v(-5.86, 2.04) * mm});
            skLineSegment(sketch, "E2267", {"start": v(-5.86, 2.04) * mm, "end": v(-5.62, 1.97) * mm});
            skLineSegment(sketch, "E2268", {"start": v(-5.62, 1.97) * mm, "end": v(-5.38, 1.89) * mm});
            skLineSegment(sketch, "E2269", {"start": v(-5.38, 1.89) * mm, "end": v(-5.14, 1.8) * mm});
            skLineSegment(sketch, "E2270", {"start": v(-5.14, 1.8) * mm, "end": v(-4.9, 1.72) * mm});
            skLineSegment(sketch, "E2271", {"start": v(-4.9, 1.72) * mm, "end": v(-4.66, 1.63) * mm});
            skLineSegment(sketch, "E2272", {"start": v(-4.66, 1.63) * mm, "end": v(-4.42, 1.54) * mm});
            skLineSegment(sketch, "E2273", {"start": v(-4.42, 1.54) * mm, "end": v(-4.18, 1.44) * mm});
            skLineSegment(sketch, "E2274", {"start": v(-4.18, 1.44) * mm, "end": v(-3.94, 1.34) * mm});
            skLineSegment(sketch, "E2275", {"start": v(-3.94, 1.34) * mm, "end": v(-3.72, 1.25) * mm});
            skLineSegment(sketch, "E2276", {"start": v(-3.72, 1.25) * mm, "end": v(-3.67, 1.36) * mm});
            skLineSegment(sketch, "E2277", {"start": v(-3.67, 1.36) * mm, "end": v(-3.58, 1.54) * mm});
            skLineSegment(sketch, "E2278", {"start": v(-3.58, 1.54) * mm, "end": v(-3.48, 1.72) * mm});
            skLineSegment(sketch, "E2279", {"start": v(-3.48, 1.72) * mm, "end": v(-3.36, 1.88) * mm});
            skLineSegment(sketch, "E2280", {"start": v(-3.36, 1.88) * mm, "end": v(-3.24, 2.04) * mm});
            skLineSegment(sketch, "E2281", {"start": v(-3.24, 2.04) * mm, "end": v(-3.1, 2.2) * mm});
            skLineSegment(sketch, "E2282", {"start": v(-3.1, 2.2) * mm, "end": v(-2.97, 2.33) * mm});
            skLineSegment(sketch, "E2283", {"start": v(-2.97, 2.33) * mm, "end": v(-2.82, 2.47) * mm});
            skLineSegment(sketch, "E2284", {"start": v(-2.82, 2.47) * mm, "end": v(-2.66, 2.6) * mm});
            skLineSegment(sketch, "E2285", {"start": v(-2.66, 2.6) * mm, "end": v(-2.49, 2.7) * mm});
            skLineSegment(sketch, "E2286", {"start": v(-2.49, 2.7) * mm, "end": v(-2.32, 2.8) * mm});
            skLineSegment(sketch, "E2287", {"start": v(-2.32, 2.8) * mm, "end": v(-2.14, 2.9) * mm});
            skLineSegment(sketch, "E2288", {"start": v(-2.14, 2.9) * mm, "end": v(-1.95, 2.98) * mm});
            skLineSegment(sketch, "E2289", {"start": v(-1.95, 2.98) * mm, "end": v(-1.9, 3) * mm});
            skLineSegment(sketch, "E2290", {"start": v(-1.9, 3) * mm, "end": v(-2, 3.17) * mm});
            skLineSegment(sketch, "E2291", {"start": v(-2, 3.17) * mm, "end": v(-2.1, 3.4) * mm});
            skLineSegment(sketch, "E2292", {"start": v(-2.1, 3.4) * mm, "end": v(-2.22, 3.65) * mm});
            skLineSegment(sketch, "E2293", {"start": v(-2.22, 3.65) * mm, "end": v(-2.33, 3.89) * mm});
            skLineSegment(sketch, "E2294", {"start": v(-2.33, 3.89) * mm, "end": v(-2.43, 4.13) * mm});
            skLineSegment(sketch, "E2295", {"start": v(-2.43, 4.13) * mm, "end": v(-2.53, 4.37) * mm});
            skLineSegment(sketch, "E2296", {"start": v(-2.53, 4.37) * mm, "end": v(-2.63, 4.6) * mm});
            skLineSegment(sketch, "E2297", {"start": v(-2.63, 4.6) * mm, "end": v(-2.72, 4.85) * mm});
            skLineSegment(sketch, "E2298", {"start": v(-2.72, 4.85) * mm, "end": v(-2.8, 5.09) * mm});
            skLineSegment(sketch, "E2299", {"start": v(-2.8, 5.09) * mm, "end": v(-2.9, 5.33) * mm});
            skLineSegment(sketch, "E2300", {"start": v(-2.9, 5.33) * mm, "end": v(-2.97, 5.57) * mm});
            skLineSegment(sketch, "E2301", {"start": v(-2.97, 5.57) * mm, "end": v(-3.05, 5.81) * mm});
            skLineSegment(sketch, "E2302", {"start": v(-3.05, 5.81) * mm, "end": v(-3.12, 6.06) * mm});
            skLineSegment(sketch, "E2303", {"start": v(-3.12, 6.06) * mm, "end": v(-3.2, 6.3) * mm});
            skLineSegment(sketch, "E2304", {"start": v(-3.2, 6.3) * mm, "end": v(-3.26, 6.54) * mm});
            skLineSegment(sketch, "E2305", {"start": v(-3.26, 6.54) * mm, "end": v(-3.32, 6.78) * mm});
            skLineSegment(sketch, "E2306", {"start": v(-3.32, 6.78) * mm, "end": v(-3.38, 7.03) * mm});
            skLineSegment(sketch, "E2307", {"start": v(-3.38, 7.03) * mm, "end": v(-3.43, 7.27) * mm});
            skLineSegment(sketch, "E2308", {"start": v(-3.43, 7.27) * mm, "end": v(-3.48, 7.51) * mm});
            skLineSegment(sketch, "E2309", {"start": v(-3.48, 7.51) * mm, "end": v(-3.52, 7.76) * mm});
            skLineSegment(sketch, "E2310", {"start": v(-3.52, 7.76) * mm, "end": v(-3.57, 8) * mm});
            skLineSegment(sketch, "E2311", {"start": v(-3.57, 8) * mm, "end": v(-3.6, 8.24) * mm});
            skLineSegment(sketch, "E2312", {"start": v(-3.6, 8.24) * mm, "end": v(-3.64, 8.49) * mm});
            skLineSegment(sketch, "E2313", {"start": v(-3.64, 8.49) * mm, "end": v(-3.67, 8.73) * mm});
            skLineSegment(sketch, "E2314", {"start": v(-3.67, 8.73) * mm, "end": v(-3.7, 8.98) * mm});
            skLineSegment(sketch, "E2315", {"start": v(-3.7, 8.98) * mm, "end": v(-3.71, 9.22) * mm});
            skLineSegment(sketch, "E2316", {"start": v(-3.71, 9.22) * mm, "end": v(-3.73, 9.47) * mm});
            skLineSegment(sketch, "E2317", {"start": v(-3.73, 9.47) * mm, "end": v(-3.75, 9.71) * mm});
            skLineSegment(sketch, "E2318", {"start": v(-3.75, 9.71) * mm, "end": v(-3.76, 9.96) * mm});
            skLineSegment(sketch, "E2319", {"start": v(-3.76, 9.96) * mm, "end": v(-3.76, 10.2) * mm});
            skLineSegment(sketch, "E2320", {"start": v(-3.76, 10.2) * mm, "end": v(-3.76, 10.45) * mm});
            skLineSegment(sketch, "E2321", {"start": v(-3.76, 10.45) * mm, "end": v(-3.76, 10.7) * mm});
            skLineSegment(sketch, "E2322", {"start": v(-3.76, 10.7) * mm, "end": v(-3.76, 10.95) * mm});
            skLineSegment(sketch, "E2323", {"start": v(-3.76, 10.95) * mm, "end": v(-3.75, 11.2) * mm});
            skLineSegment(sketch, "E2324", {"start": v(-3.75, 11.2) * mm, "end": v(-3.73, 11.45) * mm});
            skLineSegment(sketch, "E2325", {"start": v(-3.73, 11.45) * mm, "end": v(-3.71, 11.7) * mm});
            skLineSegment(sketch, "E2326", {"start": v(-3.71, 11.7) * mm, "end": v(-3.7, 11.94) * mm});
            skLineSegment(sketch, "E2327", {"start": v(-3.7, 11.94) * mm, "end": v(-3.66, 12.2) * mm});
            skLineSegment(sketch, "E2328", {"start": v(-3.66, 12.2) * mm, "end": v(-3.63, 12.44) * mm});
            skLineSegment(sketch, "E2329", {"start": v(-3.63, 12.44) * mm, "end": v(-3.6, 12.69) * mm});
            skLineSegment(sketch, "E2330", {"start": v(-3.6, 12.69) * mm, "end": v(-3.56, 12.94) * mm});
            skLineSegment(sketch, "E2331", {"start": v(-3.56, 12.94) * mm, "end": v(-3.52, 13.18) * mm});
            skLineSegment(sketch, "E2332", {"start": v(-3.52, 13.18) * mm, "end": v(-3.47, 13.43) * mm});
            skLineSegment(sketch, "E2333", {"start": v(-3.47, 13.43) * mm, "end": v(-3.42, 13.68) * mm});
            skLineSegment(sketch, "E2334", {"start": v(-3.42, 13.68) * mm, "end": v(-3.36, 13.92) * mm});
            skLineSegment(sketch, "E2335", {"start": v(-3.36, 13.92) * mm, "end": v(-3.3, 14.17) * mm});
            skLineSegment(sketch, "E2336", {"start": v(-3.3, 14.17) * mm, "end": v(-3.24, 14.42) * mm});
            skLineSegment(sketch, "E2337", {"start": v(-3.24, 14.42) * mm, "end": v(-3.18, 14.66) * mm});
            skLineSegment(sketch, "E2338", {"start": v(-3.18, 14.66) * mm, "end": v(-3.1, 14.9) * mm});
            skLineSegment(sketch, "E2339", {"start": v(-3.1, 14.9) * mm, "end": v(-3.03, 15.15) * mm});
            skLineSegment(sketch, "E2340", {"start": v(-3.03, 15.15) * mm, "end": v(-2.95, 15.4) * mm});
            skLineSegment(sketch, "E2341", {"start": v(-2.95, 15.4) * mm, "end": v(-2.87, 15.64) * mm});
            skLineSegment(sketch, "E2342", {"start": v(-2.87, 15.64) * mm, "end": v(-2.78, 15.89) * mm});
            skLineSegment(sketch, "E2343", {"start": v(-2.78, 15.89) * mm, "end": v(-2.69, 16.13) * mm});
            skLineSegment(sketch, "E2344", {"start": v(-2.69, 16.13) * mm, "end": v(-2.6, 16.38) * mm});
            skLineSegment(sketch, "E2345", {"start": v(-2.6, 16.38) * mm, "end": v(-2.5, 16.62) * mm});
            skLineSegment(sketch, "E2346", {"start": v(-2.5, 16.62) * mm, "end": v(-2.4, 16.86) * mm});
            skLineSegment(sketch, "E2347", {"start": v(-2.4, 16.86) * mm, "end": v(-2.29, 17.1) * mm});
            skLineSegment(sketch, "E2348", {"start": v(-2.29, 17.1) * mm, "end": v(-2.18, 17.35) * mm});
            skLineSegment(sketch, "E2349", {"start": v(-2.18, 17.35) * mm, "end": v(-2.06, 17.6) * mm});
            skLineSegment(sketch, "E2350", {"start": v(-2.06, 17.6) * mm, "end": v(-1.94, 17.84) * mm});
            skLineSegment(sketch, "E2351", {"start": v(-1.94, 17.84) * mm, "end": v(-1.87, 17.98) * mm});
            skLineSegment(sketch, "E2352", {"start": v(-1.87, 17.98) * mm, "end": v(-1.9, 17.98) * mm});
            skLineSegment(sketch, "E2353", {"start": v(-1.9, 17.98) * mm, "end": v(-3.03, 17.88) * mm});
            skLineSegment(sketch, "E2354", {"start": v(-3.03, 17.88) * mm, "end": v(-4.15, 17.7) * mm});
            skLineSegment(sketch, "E2355", {"start": v(-4.15, 17.7) * mm, "end": v(-5.26, 17.45) * mm});
            skLineSegment(sketch, "E2356", {"start": v(-5.26, 17.45) * mm, "end": v(-6.34, 17.14) * mm});
            skLineSegment(sketch, "E2357", {"start": v(-6.34, 17.14) * mm, "end": v(-7.4, 16.75) * mm});
            skLineSegment(sketch, "E2358", {"start": v(-7.4, 16.75) * mm, "end": v(-8.45, 16.3) * mm});
            skLineSegment(sketch, "E2359", {"start": v(-8.45, 16.3) * mm, "end": v(-9.45, 15.79) * mm});
            skLineSegment(sketch, "E2360", {"start": v(-9.45, 15.79) * mm, "end": v(-10.43, 15.21) * mm});
            skLineSegment(sketch, "E2361", {"start": v(-10.43, 15.21) * mm, "end": v(-11.37, 14.58) * mm});
            skLineSegment(sketch, "E2362", {"start": v(-11.37, 14.58) * mm, "end": v(-12.26, 13.88) * mm});
            skLineSegment(sketch, "E2363", {"start": v(-12.26, 13.88) * mm, "end": v(-13.1, 13.13) * mm});
            skLineSegment(sketch, "E2364", {"start": v(-13.1, 13.13) * mm, "end": v(-13.9, 12.33) * mm});
            skLineSegment(sketch, "E2365", {"start": v(-13.9, 12.33) * mm, "end": v(-14.66, 11.49) * mm});
            skLineSegment(sketch, "E2366", {"start": v(-14.66, 11.49) * mm, "end": v(-15.35, 10.6) * mm});
            skLineSegment(sketch, "E2367", {"start": v(-15.35, 10.6) * mm, "end": v(-15.99, 9.65) * mm});
            skLineSegment(sketch, "E2368", {"start": v(-15.99, 9.65) * mm, "end": v(-16.56, 8.68) * mm});
            skLineSegment(sketch, "E2369", {"start": v(-16.56, 8.68) * mm, "end": v(-17.08, 7.67) * mm});
            skLineSegment(sketch, "E2370", {"start": v(-17.08, 7.67) * mm, "end": v(-17.53, 6.63) * mm});
            skLineSegment(sketch, "E2371", {"start": v(-17.53, 6.63) * mm, "end": v(-17.91, 5.57) * mm});
            skLineSegment(sketch, "E2372", {"start": v(-17.91, 5.57) * mm, "end": v(-18.23, 4.48) * mm});
            skLineSegment(sketch, "E2373", {"start": v(-18.23, 4.48) * mm, "end": v(-18.47, 3.38) * mm});
            skLineSegment(sketch, "E2374", {"start": v(-18.47, 3.38) * mm, "end": v(-18.65, 2.26) * mm});
            skLineSegment(sketch, "E2375", {"start": v(-18.65, 2.26) * mm, "end": v(-18.75, 1.24) * mm});
            skLineSegment(sketch, "E2376", {"start": v(-18.75, 1.24) * mm, "end": v(-18.61, 1.3) * mm});
            skLineSegment(sketch, "E2377", {"start": v(17.2, 1.13) * mm, "end": v(17.1, 2.26) * mm});
            skLineSegment(sketch, "E2378", {"start": v(17.1, 2.26) * mm, "end": v(16.93, 3.38) * mm});
            skLineSegment(sketch, "E2379", {"start": v(16.93, 3.38) * mm, "end": v(16.68, 4.48) * mm});
            skLineSegment(sketch, "E2380", {"start": v(16.68, 4.48) * mm, "end": v(16.36, 5.57) * mm});
            skLineSegment(sketch, "E2381", {"start": v(16.36, 5.57) * mm, "end": v(15.98, 6.63) * mm});
            skLineSegment(sketch, "E2382", {"start": v(15.98, 6.63) * mm, "end": v(15.53, 7.67) * mm});
            skLineSegment(sketch, "E2383", {"start": v(15.53, 7.67) * mm, "end": v(15.02, 8.68) * mm});
            skLineSegment(sketch, "E2384", {"start": v(15.02, 8.68) * mm, "end": v(14.44, 9.65) * mm});
            skLineSegment(sketch, "E2385", {"start": v(14.44, 9.65) * mm, "end": v(13.8, 10.6) * mm});
            skLineSegment(sketch, "E2386", {"start": v(13.8, 10.6) * mm, "end": v(13.1, 11.49) * mm});
            skLineSegment(sketch, "E2387", {"start": v(13.1, 11.49) * mm, "end": v(12.36, 12.33) * mm});
            skLineSegment(sketch, "E2388", {"start": v(12.36, 12.33) * mm, "end": v(11.56, 13.13) * mm});
            skLineSegment(sketch, "E2389", {"start": v(11.56, 13.13) * mm, "end": v(10.71, 13.88) * mm});
            skLineSegment(sketch, "E2390", {"start": v(10.71, 13.88) * mm, "end": v(9.82, 14.58) * mm});
            skLineSegment(sketch, "E2391", {"start": v(9.82, 14.58) * mm, "end": v(8.88, 15.21) * mm});
            skLineSegment(sketch, "E2392", {"start": v(8.88, 15.21) * mm, "end": v(7.9, 15.79) * mm});
            skLineSegment(sketch, "E2393", {"start": v(7.9, 15.79) * mm, "end": v(6.9, 16.3) * mm});
            skLineSegment(sketch, "E2394", {"start": v(6.9, 16.3) * mm, "end": v(5.86, 16.75) * mm});
            skLineSegment(sketch, "E2395", {"start": v(5.86, 16.75) * mm, "end": v(4.8, 17.14) * mm});
            skLineSegment(sketch, "E2396", {"start": v(4.8, 17.14) * mm, "end": v(3.7, 17.45) * mm});
            skLineSegment(sketch, "E2397", {"start": v(3.7, 17.45) * mm, "end": v(2.6, 17.7) * mm});
            skLineSegment(sketch, "E2398", {"start": v(2.6, 17.7) * mm, "end": v(1.48, 17.88) * mm});
            skLineSegment(sketch, "E2399", {"start": v(1.48, 17.88) * mm, "end": v(0.47, 17.97) * mm});
            skLineSegment(sketch, "E2400", {"start": v(0.47, 17.97) * mm, "end": v(0.52, 17.84) * mm});
            skLineSegment(sketch, "E2401", {"start": v(0.52, 17.84) * mm, "end": v(0.63, 17.6) * mm});
            skLineSegment(sketch, "E2402", {"start": v(0.63, 17.6) * mm, "end": v(0.72, 17.35) * mm});
            skLineSegment(sketch, "E2403", {"start": v(0.72, 17.35) * mm, "end": v(0.82, 17.1) * mm});
            skLineSegment(sketch, "E2404", {"start": v(0.82, 17.1) * mm, "end": v(0.91, 16.86) * mm});
            skLineSegment(sketch, "E2405", {"start": v(0.91, 16.86) * mm, "end": v(1, 16.62) * mm});
            skLineSegment(sketch, "E2406", {"start": v(1, 16.62) * mm, "end": v(1.08, 16.38) * mm});
            skLineSegment(sketch, "E2407", {"start": v(1.08, 16.38) * mm, "end": v(1.17, 16.13) * mm});
            skLineSegment(sketch, "E2408", {"start": v(1.17, 16.13) * mm, "end": v(1.24, 15.89) * mm});
            skLineSegment(sketch, "E2409", {"start": v(1.24, 15.89) * mm, "end": v(1.32, 15.64) * mm});
            skLineSegment(sketch, "E2410", {"start": v(1.32, 15.64) * mm, "end": v(1.4, 15.4) * mm});
            skLineSegment(sketch, "E2411", {"start": v(1.4, 15.4) * mm, "end": v(1.46, 15.15) * mm});
            skLineSegment(sketch, "E2412", {"start": v(1.46, 15.15) * mm, "end": v(1.52, 14.9) * mm});
            skLineSegment(sketch, "E2413", {"start": v(1.52, 14.9) * mm, "end": v(1.58, 14.66) * mm});
            skLineSegment(sketch, "E2414", {"start": v(1.58, 14.66) * mm, "end": v(1.64, 14.42) * mm});
            skLineSegment(sketch, "E2415", {"start": v(1.64, 14.42) * mm, "end": v(1.7, 14.17) * mm});
            skLineSegment(sketch, "E2416", {"start": v(1.7, 14.17) * mm, "end": v(1.75, 13.92) * mm});
            skLineSegment(sketch, "E2417", {"start": v(1.75, 13.92) * mm, "end": v(1.8, 13.68) * mm});
            skLineSegment(sketch, "E2418", {"start": v(1.8, 13.68) * mm, "end": v(1.84, 13.43) * mm});
            skLineSegment(sketch, "E2419", {"start": v(1.84, 13.43) * mm, "end": v(1.88, 13.18) * mm});
            skLineSegment(sketch, "E2420", {"start": v(1.88, 13.18) * mm, "end": v(1.91, 12.94) * mm});
            skLineSegment(sketch, "E2421", {"start": v(1.91, 12.94) * mm, "end": v(1.95, 12.69) * mm});
            skLineSegment(sketch, "E2422", {"start": v(1.95, 12.69) * mm, "end": v(1.98, 12.44) * mm});
            skLineSegment(sketch, "E2423", {"start": v(1.98, 12.44) * mm, "end": v(2, 12.2) * mm});
            skLineSegment(sketch, "E2424", {"start": v(2, 12.2) * mm, "end": v(2.03, 11.94) * mm});
            skLineSegment(sketch, "E2425", {"start": v(2.03, 11.94) * mm, "end": v(2.05, 11.7) * mm});
            skLineSegment(sketch, "E2426", {"start": v(2.05, 11.7) * mm, "end": v(2.06, 11.45) * mm});
            skLineSegment(sketch, "E2427", {"start": v(2.06, 11.45) * mm, "end": v(2.07, 11.2) * mm});
            skLineSegment(sketch, "E2428", {"start": v(2.07, 11.2) * mm, "end": v(2.08, 10.95) * mm});
            skLineSegment(sketch, "E2429", {"start": v(2.08, 10.95) * mm, "end": v(2.09, 10.7) * mm});
            skLineSegment(sketch, "E2430", {"start": v(2.09, 10.7) * mm, "end": v(2.09, 10.45) * mm});
            skLineSegment(sketch, "E2431", {"start": v(2.09, 10.45) * mm, "end": v(2.09, 10.2) * mm});
            skLineSegment(sketch, "E2432", {"start": v(2.09, 10.2) * mm, "end": v(2.08, 9.96) * mm});
            skLineSegment(sketch, "E2433", {"start": v(2.08, 9.96) * mm, "end": v(2.07, 9.71) * mm});
            skLineSegment(sketch, "E2434", {"start": v(2.07, 9.71) * mm, "end": v(2.06, 9.47) * mm});
            skLineSegment(sketch, "E2435", {"start": v(2.06, 9.47) * mm, "end": v(2.05, 9.22) * mm});
            skLineSegment(sketch, "E2436", {"start": v(2.05, 9.22) * mm, "end": v(2.03, 8.98) * mm});
            skLineSegment(sketch, "E2437", {"start": v(2.03, 8.98) * mm, "end": v(2, 8.73) * mm});
            skLineSegment(sketch, "E2438", {"start": v(2, 8.73) * mm, "end": v(1.98, 8.49) * mm});
            skLineSegment(sketch, "E2439", {"start": v(1.98, 8.49) * mm, "end": v(1.95, 8.24) * mm});
            skLineSegment(sketch, "E2440", {"start": v(1.95, 8.24) * mm, "end": v(1.92, 8) * mm});
            skLineSegment(sketch, "E2441", {"start": v(1.92, 8) * mm, "end": v(1.88, 7.76) * mm});
            skLineSegment(sketch, "E2442", {"start": v(1.88, 7.76) * mm, "end": v(1.84, 7.51) * mm});
            skLineSegment(sketch, "E2443", {"start": v(1.84, 7.51) * mm, "end": v(1.8, 7.27) * mm});
            skLineSegment(sketch, "E2444", {"start": v(1.8, 7.27) * mm, "end": v(1.76, 7.03) * mm});
            skLineSegment(sketch, "E2445", {"start": v(1.76, 7.03) * mm, "end": v(1.7, 6.78) * mm});
            skLineSegment(sketch, "E2446", {"start": v(1.7, 6.78) * mm, "end": v(1.65, 6.54) * mm});
            skLineSegment(sketch, "E2447", {"start": v(1.65, 6.54) * mm, "end": v(1.6, 6.3) * mm});
            skLineSegment(sketch, "E2448", {"start": v(1.6, 6.3) * mm, "end": v(1.54, 6.06) * mm});
            skLineSegment(sketch, "E2449", {"start": v(1.54, 6.06) * mm, "end": v(1.48, 5.81) * mm});
            skLineSegment(sketch, "E2450", {"start": v(1.48, 5.81) * mm, "end": v(1.4, 5.57) * mm});
            skLineSegment(sketch, "E2451", {"start": v(1.4, 5.57) * mm, "end": v(1.34, 5.33) * mm});
            skLineSegment(sketch, "E2452", {"start": v(1.34, 5.33) * mm, "end": v(1.27, 5.09) * mm});
            skLineSegment(sketch, "E2453", {"start": v(1.27, 5.09) * mm, "end": v(1.2, 4.85) * mm});
            skLineSegment(sketch, "E2454", {"start": v(1.2, 4.85) * mm, "end": v(1.11, 4.6) * mm});
            skLineSegment(sketch, "E2455", {"start": v(1.11, 4.6) * mm, "end": v(1.03, 4.37) * mm});
            skLineSegment(sketch, "E2456", {"start": v(1.03, 4.37) * mm, "end": v(0.94, 4.13) * mm});
            skLineSegment(sketch, "E2457", {"start": v(0.94, 4.13) * mm, "end": v(0.86, 3.89) * mm});
            skLineSegment(sketch, "E2458", {"start": v(0.86, 3.89) * mm, "end": v(0.76, 3.65) * mm});
            skLineSegment(sketch, "E2459", {"start": v(0.76, 3.65) * mm, "end": v(0.67, 3.4) * mm});
            skLineSegment(sketch, "E2460", {"start": v(0.67, 3.4) * mm, "end": v(0.57, 3.17) * mm});
            skLineSegment(sketch, "E2461", {"start": v(0.57, 3.17) * mm, "end": v(0.47, 2.95) * mm});
            skLineSegment(sketch, "E2462", {"start": v(0.47, 2.95) * mm, "end": v(0.59, 2.9) * mm});
            skLineSegment(sketch, "E2463", {"start": v(0.59, 2.9) * mm, "end": v(0.77, 2.8) * mm});
            skLineSegment(sketch, "E2464", {"start": v(0.77, 2.8) * mm, "end": v(0.94, 2.7) * mm});
            skLineSegment(sketch, "E2465", {"start": v(0.94, 2.7) * mm, "end": v(1.1, 2.6) * mm});
            skLineSegment(sketch, "E2466", {"start": v(1.1, 2.6) * mm, "end": v(1.27, 2.47) * mm});
            skLineSegment(sketch, "E2467", {"start": v(1.27, 2.47) * mm, "end": v(1.42, 2.33) * mm});
            skLineSegment(sketch, "E2468", {"start": v(1.42, 2.33) * mm, "end": v(1.56, 2.2) * mm});
            skLineSegment(sketch, "E2469", {"start": v(1.56, 2.2) * mm, "end": v(1.7, 2.04) * mm});
            skLineSegment(sketch, "E2470", {"start": v(1.7, 2.04) * mm, "end": v(1.82, 1.88) * mm});
            skLineSegment(sketch, "E2471", {"start": v(1.82, 1.88) * mm, "end": v(1.93, 1.72) * mm});
            skLineSegment(sketch, "E2472", {"start": v(1.93, 1.72) * mm, "end": v(2.03, 1.54) * mm});
            skLineSegment(sketch, "E2473", {"start": v(2.03, 1.54) * mm, "end": v(2.12, 1.36) * mm});
            skLineSegment(sketch, "E2474", {"start": v(2.12, 1.36) * mm, "end": v(2.2, 1.18) * mm});
            skLineSegment(sketch, "E2475", {"start": v(2.2, 1.18) * mm, "end": v(2.22, 1.13) * mm});
            skLineSegment(sketch, "E2476", {"start": v(2.22, 1.13) * mm, "end": v(2.4, 1.22) * mm});
            skLineSegment(sketch, "E2477", {"start": v(2.4, 1.22) * mm, "end": v(2.63, 1.33) * mm});
            skLineSegment(sketch, "E2478", {"start": v(2.63, 1.33) * mm, "end": v(2.87, 1.45) * mm});
            skLineSegment(sketch, "E2479", {"start": v(2.87, 1.45) * mm, "end": v(3.11, 1.55) * mm});
            skLineSegment(sketch, "E2480", {"start": v(3.11, 1.55) * mm, "end": v(3.35, 1.66) * mm});
            skLineSegment(sketch, "E2481", {"start": v(3.35, 1.66) * mm, "end": v(3.6, 1.76) * mm});
            skLineSegment(sketch, "E2482", {"start": v(3.6, 1.76) * mm, "end": v(3.83, 1.85) * mm});
            skLineSegment(sketch, "E2483", {"start": v(3.83, 1.85) * mm, "end": v(4.07, 1.95) * mm});
            skLineSegment(sketch, "E2484", {"start": v(4.07, 1.95) * mm, "end": v(4.32, 2.03) * mm});
            skLineSegment(sketch, "E2485", {"start": v(4.32, 2.03) * mm, "end": v(4.56, 2.12) * mm});
            skLineSegment(sketch, "E2486", {"start": v(4.56, 2.12) * mm, "end": v(4.8, 2.2) * mm});
            skLineSegment(sketch, "E2487", {"start": v(4.8, 2.2) * mm, "end": v(5.04, 2.28) * mm});
            skLineSegment(sketch, "E2488", {"start": v(5.04, 2.28) * mm, "end": v(5.28, 2.35) * mm});
            skLineSegment(sketch, "E2489", {"start": v(5.28, 2.35) * mm, "end": v(5.52, 2.42) * mm});
            skLineSegment(sketch, "E2490", {"start": v(5.52, 2.42) * mm, "end": v(5.77, 2.48) * mm});
            skLineSegment(sketch, "E2491", {"start": v(5.77, 2.48) * mm, "end": v(6, 2.54) * mm});
            skLineSegment(sketch, "E2492", {"start": v(6, 2.54) * mm, "end": v(6.25, 2.6) * mm});
            skLineSegment(sketch, "E2493", {"start": v(6.25, 2.6) * mm, "end": v(6.5, 2.65) * mm});
            skLineSegment(sketch, "E2494", {"start": v(6.5, 2.65) * mm, "end": v(6.74, 2.7) * mm});
            skLineSegment(sketch, "E2495", {"start": v(6.74, 2.7) * mm, "end": v(6.98, 2.75) * mm});
            skLineSegment(sketch, "E2496", {"start": v(6.98, 2.75) * mm, "end": v(7.23, 2.8) * mm});
            skLineSegment(sketch, "E2497", {"start": v(7.23, 2.8) * mm, "end": v(7.47, 2.83) * mm});
            skLineSegment(sketch, "E2498", {"start": v(7.47, 2.83) * mm, "end": v(7.71, 2.86) * mm});
            skLineSegment(sketch, "E2499", {"start": v(7.71, 2.86) * mm, "end": v(7.96, 2.9) * mm});
            skLineSegment(sketch, "E2500", {"start": v(7.96, 2.9) * mm, "end": v(8.2, 2.92) * mm});
            skLineSegment(sketch, "E2501", {"start": v(8.2, 2.92) * mm, "end": v(8.45, 2.94) * mm});
            skLineSegment(sketch, "E2502", {"start": v(8.45, 2.94) * mm, "end": v(8.7, 2.96) * mm});
            skLineSegment(sketch, "E2503", {"start": v(8.7, 2.96) * mm, "end": v(8.94, 2.97) * mm});
            skLineSegment(sketch, "E2504", {"start": v(8.94, 2.97) * mm, "end": v(9.19, 2.98) * mm});
            skLineSegment(sketch, "E2505", {"start": v(9.19, 2.98) * mm, "end": v(9.43, 2.99) * mm});
            skLineSegment(sketch, "E2506", {"start": v(9.43, 2.99) * mm, "end": v(9.68, 3) * mm});
            skLineSegment(sketch, "E2507", {"start": v(9.68, 3) * mm, "end": v(9.93, 2.99) * mm});
            skLineSegment(sketch, "E2508", {"start": v(9.93, 2.99) * mm, "end": v(10.18, 2.98) * mm});
            skLineSegment(sketch, "E2509", {"start": v(10.18, 2.98) * mm, "end": v(10.42, 2.97) * mm});
            skLineSegment(sketch, "E2510", {"start": v(10.42, 2.97) * mm, "end": v(10.67, 2.96) * mm});
            skLineSegment(sketch, "E2511", {"start": v(10.67, 2.96) * mm, "end": v(10.92, 2.94) * mm});
            skLineSegment(sketch, "E2512", {"start": v(10.92, 2.94) * mm, "end": v(11.17, 2.92) * mm});
            skLineSegment(sketch, "E2513", {"start": v(11.17, 2.92) * mm, "end": v(11.42, 2.89) * mm});
            skLineSegment(sketch, "E2514", {"start": v(11.42, 2.89) * mm, "end": v(11.67, 2.86) * mm});
            skLineSegment(sketch, "E2515", {"start": v(11.67, 2.86) * mm, "end": v(11.91, 2.82) * mm});
            skLineSegment(sketch, "E2516", {"start": v(11.91, 2.82) * mm, "end": v(12.16, 2.79) * mm});
            skLineSegment(sketch, "E2517", {"start": v(12.16, 2.79) * mm, "end": v(12.4, 2.74) * mm});
            skLineSegment(sketch, "E2518", {"start": v(12.4, 2.74) * mm, "end": v(12.66, 2.7) * mm});
            skLineSegment(sketch, "E2519", {"start": v(12.66, 2.7) * mm, "end": v(12.9, 2.64) * mm});
            skLineSegment(sketch, "E2520", {"start": v(12.9, 2.64) * mm, "end": v(13.15, 2.59) * mm});
            skLineSegment(sketch, "E2521", {"start": v(13.15, 2.59) * mm, "end": v(13.4, 2.53) * mm});
            skLineSegment(sketch, "E2522", {"start": v(13.4, 2.53) * mm, "end": v(13.64, 2.47) * mm});
            skLineSegment(sketch, "E2523", {"start": v(13.64, 2.47) * mm, "end": v(13.89, 2.4) * mm});
            skLineSegment(sketch, "E2524", {"start": v(13.89, 2.4) * mm, "end": v(14.13, 2.33) * mm});
            skLineSegment(sketch, "E2525", {"start": v(14.13, 2.33) * mm, "end": v(14.38, 2.25) * mm});
            skLineSegment(sketch, "E2526", {"start": v(14.38, 2.25) * mm, "end": v(14.62, 2.18) * mm});
            skLineSegment(sketch, "E2527", {"start": v(14.62, 2.18) * mm, "end": v(14.87, 2.1) * mm});
            skLineSegment(sketch, "E2528", {"start": v(14.87, 2.1) * mm, "end": v(15.11, 2) * mm});
            skLineSegment(sketch, "E2529", {"start": v(15.11, 2) * mm, "end": v(15.36, 1.92) * mm});
            skLineSegment(sketch, "E2530", {"start": v(15.36, 1.92) * mm, "end": v(15.6, 1.82) * mm});
            skLineSegment(sketch, "E2531", {"start": v(15.6, 1.82) * mm, "end": v(15.85, 1.72) * mm});
            skLineSegment(sketch, "E2532", {"start": v(15.85, 1.72) * mm, "end": v(16.09, 1.62) * mm});
            skLineSegment(sketch, "E2533", {"start": v(16.09, 1.62) * mm, "end": v(16.33, 1.51) * mm});
            skLineSegment(sketch, "E2534", {"start": v(16.33, 1.51) * mm, "end": v(16.58, 1.4) * mm});
            skLineSegment(sketch, "E2535", {"start": v(16.58, 1.4) * mm, "end": v(16.82, 1.29) * mm});
            skLineSegment(sketch, "E2536", {"start": v(16.82, 1.29) * mm, "end": v(17.06, 1.17) * mm});
            skLineSegment(sketch, "E2537", {"start": v(17.06, 1.17) * mm, "end": v(17.21, 1.1) * mm});
            skLineSegment(sketch, "E2538", {"start": v(17.21, 1.1) * mm, "end": v(17.2, 1.13) * mm});
            skLineSegment(sketch, "E2539", {"start": v(-0.38, 6.62) * mm, "end": v(-0.32, 6.75) * mm});
            skLineSegment(sketch, "E2540", {"start": v(-0.32, 6.75) * mm, "end": v(-0.26, 6.88) * mm});
            skLineSegment(sketch, "E2541", {"start": v(-0.26, 6.88) * mm, "end": v(-0.21, 7) * mm});
            skLineSegment(sketch, "E2542", {"start": v(-0.21, 7) * mm, "end": v(-0.16, 7.13) * mm});
            skLineSegment(sketch, "E2543", {"start": v(-0.16, 7.13) * mm, "end": v(-0.11, 7.26) * mm});
            skLineSegment(sketch, "E2544", {"start": v(-0.11, 7.26) * mm, "end": v(-0.06, 7.39) * mm});
            skLineSegment(sketch, "E2545", {"start": v(-0.06, 7.39) * mm, "end": v(-0.02, 7.52) * mm});
            skLineSegment(sketch, "E2546", {"start": v(-0.02, 7.52) * mm, "end": v(0.03, 7.65) * mm});
            skLineSegment(sketch, "E2547", {"start": v(0.03, 7.65) * mm, "end": v(0.07, 7.78) * mm});
            skLineSegment(sketch, "E2548", {"start": v(0.07, 7.78) * mm, "end": v(0.1, 7.9) * mm});
            skLineSegment(sketch, "E2549", {"start": v(0.1, 7.9) * mm, "end": v(0.14, 8.03) * mm});
            skLineSegment(sketch, "E2550", {"start": v(0.14, 8.03) * mm, "end": v(0.18, 8.16) * mm});
            skLineSegment(sketch, "E2551", {"start": v(0.18, 8.16) * mm, "end": v(0.21, 8.3) * mm});
            skLineSegment(sketch, "E2552", {"start": v(0.21, 8.3) * mm, "end": v(0.25, 8.42) * mm});
            skLineSegment(sketch, "E2553", {"start": v(0.25, 8.42) * mm, "end": v(0.28, 8.55) * mm});
            skLineSegment(sketch, "E2554", {"start": v(0.28, 8.55) * mm, "end": v(0.3, 8.68) * mm});
            skLineSegment(sketch, "E2555", {"start": v(0.3, 8.68) * mm, "end": v(0.33, 8.8) * mm});
            skLineSegment(sketch, "E2556", {"start": v(0.33, 8.8) * mm, "end": v(0.35, 8.94) * mm});
            skLineSegment(sketch, "E2557", {"start": v(0.35, 8.94) * mm, "end": v(0.38, 9.07) * mm});
            skLineSegment(sketch, "E2558", {"start": v(0.38, 9.07) * mm, "end": v(0.4, 9.2) * mm});
            skLineSegment(sketch, "E2559", {"start": v(0.4, 9.2) * mm, "end": v(0.42, 9.32) * mm});
            skLineSegment(sketch, "E2560", {"start": v(0.42, 9.32) * mm, "end": v(0.43, 9.45) * mm});
            skLineSegment(sketch, "E2561", {"start": v(0.43, 9.45) * mm, "end": v(0.45, 9.58) * mm});
            skLineSegment(sketch, "E2562", {"start": v(0.45, 9.58) * mm, "end": v(0.46, 9.71) * mm});
            skLineSegment(sketch, "E2563", {"start": v(0.46, 9.71) * mm, "end": v(0.47, 9.84) * mm});
            skLineSegment(sketch, "E2564", {"start": v(0.47, 9.84) * mm, "end": v(0.48, 9.97) * mm});
            skLineSegment(sketch, "E2565", {"start": v(0.48, 9.97) * mm, "end": v(0.49, 10.1) * mm});
            skLineSegment(sketch, "E2566", {"start": v(0.49, 10.1) * mm, "end": v(0.5, 10.23) * mm});
            skLineSegment(sketch, "E2567", {"start": v(0.5, 10.23) * mm, "end": v(0.5, 10.36) * mm});
            skLineSegment(sketch, "E2568", {"start": v(0.5, 10.36) * mm, "end": v(0.5, 10.5) * mm});
            skLineSegment(sketch, "E2569", {"start": v(0.5, 10.5) * mm, "end": v(0.5, 10.63) * mm});
            skLineSegment(sketch, "E2570", {"start": v(0.5, 10.63) * mm, "end": v(0.5, 10.76) * mm});
            skLineSegment(sketch, "E2571", {"start": v(0.5, 10.76) * mm, "end": v(0.49, 10.9) * mm});
            skLineSegment(sketch, "E2572", {"start": v(0.49, 10.9) * mm, "end": v(0.48, 11.02) * mm});
            skLineSegment(sketch, "E2573", {"start": v(0.48, 11.02) * mm, "end": v(0.47, 11.15) * mm});
            skLineSegment(sketch, "E2574", {"start": v(0.47, 11.15) * mm, "end": v(0.46, 11.29) * mm});
            skLineSegment(sketch, "E2575", {"start": v(0.46, 11.29) * mm, "end": v(0.45, 11.42) * mm});
            skLineSegment(sketch, "E2576", {"start": v(0.45, 11.42) * mm, "end": v(0.43, 11.55) * mm});
            skLineSegment(sketch, "E2577", {"start": v(0.43, 11.55) * mm, "end": v(0.41, 11.68) * mm});
            skLineSegment(sketch, "E2578", {"start": v(0.41, 11.68) * mm, "end": v(0.4, 11.81) * mm});
            skLineSegment(sketch, "E2579", {"start": v(0.4, 11.81) * mm, "end": v(0.37, 11.94) * mm});
            skLineSegment(sketch, "E2580", {"start": v(0.37, 11.94) * mm, "end": v(0.35, 12.08) * mm});
            skLineSegment(sketch, "E2581", {"start": v(0.35, 12.08) * mm, "end": v(0.33, 12.2) * mm});
            skLineSegment(sketch, "E2582", {"start": v(0.33, 12.2) * mm, "end": v(0.3, 12.34) * mm});
            skLineSegment(sketch, "E2583", {"start": v(0.3, 12.34) * mm, "end": v(0.27, 12.47) * mm});
            skLineSegment(sketch, "E2584", {"start": v(0.27, 12.47) * mm, "end": v(0.24, 12.6) * mm});
            skLineSegment(sketch, "E2585", {"start": v(0.24, 12.6) * mm, "end": v(0.2, 12.73) * mm});
            skLineSegment(sketch, "E2586", {"start": v(0.2, 12.73) * mm, "end": v(0.17, 12.86) * mm});
            skLineSegment(sketch, "E2587", {"start": v(0.17, 12.86) * mm, "end": v(0.13, 13) * mm});
            skLineSegment(sketch, "E2588", {"start": v(0.13, 13) * mm, "end": v(0.1, 13.12) * mm});
            skLineSegment(sketch, "E2589", {"start": v(0.1, 13.12) * mm, "end": v(0.05, 13.25) * mm});
            skLineSegment(sketch, "E2590", {"start": v(0.05, 13.25) * mm, "end": v(0.01, 13.38) * mm});
            skLineSegment(sketch, "E2591", {"start": v(0.01, 13.38) * mm, "end": v(-0.03, 13.51) * mm});
            skLineSegment(sketch, "E2592", {"start": v(-0.03, 13.51) * mm, "end": v(-0.08, 13.64) * mm});
            skLineSegment(sketch, "E2593", {"start": v(-0.08, 13.64) * mm, "end": v(-0.13, 13.77) * mm});
            skLineSegment(sketch, "E2594", {"start": v(-0.13, 13.77) * mm, "end": v(-0.18, 13.9) * mm});
            skLineSegment(sketch, "E2595", {"start": v(-0.18, 13.9) * mm, "end": v(-0.23, 14.03) * mm});
            skLineSegment(sketch, "E2596", {"start": v(-0.23, 14.03) * mm, "end": v(-0.29, 14.16) * mm});
            skLineSegment(sketch, "E2597", {"start": v(-0.29, 14.16) * mm, "end": v(-0.34, 14.3) * mm});
            skLineSegment(sketch, "E2598", {"start": v(-0.34, 14.3) * mm, "end": v(-0.4, 14.42) * mm});
            skLineSegment(sketch, "E2599", {"start": v(-0.4, 14.42) * mm, "end": v(-0.4, 14.44) * mm});
            skLineSegment(sketch, "E2600", {"start": v(-0.4, 14.44) * mm, "end": v(-1.04, 14.44) * mm});
            skLineSegment(sketch, "E2601", {"start": v(-1.04, 14.44) * mm, "end": v(-1.06, 14.4) * mm});
            skLineSegment(sketch, "E2602", {"start": v(-1.06, 14.4) * mm, "end": v(-1.13, 14.27) * mm});
            skLineSegment(sketch, "E2603", {"start": v(-1.13, 14.27) * mm, "end": v(-1.2, 14.14) * mm});
            skLineSegment(sketch, "E2604", {"start": v(-1.2, 14.14) * mm, "end": v(-1.26, 14.01) * mm});
            skLineSegment(sketch, "E2605", {"start": v(-1.26, 14.01) * mm, "end": v(-1.32, 13.88) * mm});
            skLineSegment(sketch, "E2606", {"start": v(-1.32, 13.88) * mm, "end": v(-1.38, 13.75) * mm});
            skLineSegment(sketch, "E2607", {"start": v(-1.38, 13.75) * mm, "end": v(-1.43, 13.62) * mm});
            skLineSegment(sketch, "E2608", {"start": v(-1.43, 13.62) * mm, "end": v(-1.49, 13.5) * mm});
            skLineSegment(sketch, "E2609", {"start": v(-1.49, 13.5) * mm, "end": v(-1.54, 13.36) * mm});
            skLineSegment(sketch, "E2610", {"start": v(-1.54, 13.36) * mm, "end": v(-1.59, 13.23) * mm});
            skLineSegment(sketch, "E2611", {"start": v(-1.59, 13.23) * mm, "end": v(-1.64, 13.1) * mm});
            skLineSegment(sketch, "E2612", {"start": v(-1.64, 13.1) * mm, "end": v(-1.68, 12.97) * mm});
            skLineSegment(sketch, "E2613", {"start": v(-1.68, 12.97) * mm, "end": v(-1.72, 12.84) * mm});
            skLineSegment(sketch, "E2614", {"start": v(-1.72, 12.84) * mm, "end": v(-1.76, 12.71) * mm});
            skLineSegment(sketch, "E2615", {"start": v(-1.76, 12.71) * mm, "end": v(-1.8, 12.58) * mm});
            skLineSegment(sketch, "E2616", {"start": v(-1.8, 12.58) * mm, "end": v(-1.84, 12.45) * mm});
            skLineSegment(sketch, "E2617", {"start": v(-1.84, 12.45) * mm, "end": v(-1.87, 12.32) * mm});
            skLineSegment(sketch, "E2618", {"start": v(-1.87, 12.32) * mm, "end": v(-1.9, 12.2) * mm});
            skLineSegment(sketch, "E2619", {"start": v(-1.9, 12.2) * mm, "end": v(-1.93, 12.06) * mm});
            skLineSegment(sketch, "E2620", {"start": v(-1.93, 12.06) * mm, "end": v(-1.96, 11.93) * mm});
            skLineSegment(sketch, "E2621", {"start": v(-1.96, 11.93) * mm, "end": v(-1.98, 11.8) * mm});
            skLineSegment(sketch, "E2622", {"start": v(-1.98, 11.8) * mm, "end": v(-2, 11.67) * mm});
            skLineSegment(sketch, "E2623", {"start": v(-2, 11.67) * mm, "end": v(-2.02, 11.54) * mm});
            skLineSegment(sketch, "E2624", {"start": v(-2.02, 11.54) * mm, "end": v(-2.04, 11.41) * mm});
            skLineSegment(sketch, "E2625", {"start": v(-2.04, 11.41) * mm, "end": v(-2.06, 11.28) * mm});
            skLineSegment(sketch, "E2626", {"start": v(-2.06, 11.28) * mm, "end": v(-2.07, 11.15) * mm});
            skLineSegment(sketch, "E2627", {"start": v(-2.07, 11.15) * mm, "end": v(-2.08, 11.02) * mm});
            skLineSegment(sketch, "E2628", {"start": v(-2.08, 11.02) * mm, "end": v(-2.09, 10.89) * mm});
            skLineSegment(sketch, "E2629", {"start": v(-2.09, 10.89) * mm, "end": v(-2.1, 10.76) * mm});
            skLineSegment(sketch, "E2630", {"start": v(-2.1, 10.76) * mm, "end": v(-2.1, 10.63) * mm});
            skLineSegment(sketch, "E2631", {"start": v(-2.1, 10.63) * mm, "end": v(-2.1, 10.5) * mm});
            skLineSegment(sketch, "E2632", {"start": v(-2.1, 10.5) * mm, "end": v(-2.1, 10.36) * mm});
            skLineSegment(sketch, "E2633", {"start": v(-2.1, 10.36) * mm, "end": v(-2.1, 10.24) * mm});
            skLineSegment(sketch, "E2634", {"start": v(-2.1, 10.24) * mm, "end": v(-2.09, 10.1) * mm});
            skLineSegment(sketch, "E2635", {"start": v(-2.09, 10.1) * mm, "end": v(-2.08, 9.98) * mm});
            skLineSegment(sketch, "E2636", {"start": v(-2.08, 9.98) * mm, "end": v(-2.07, 9.85) * mm});
            skLineSegment(sketch, "E2637", {"start": v(-2.07, 9.85) * mm, "end": v(-2.06, 9.72) * mm});
            skLineSegment(sketch, "E2638", {"start": v(-2.06, 9.72) * mm, "end": v(-2.04, 9.6) * mm});
            skLineSegment(sketch, "E2639", {"start": v(-2.04, 9.6) * mm, "end": v(-2.03, 9.46) * mm});
            skLineSegment(sketch, "E2640", {"start": v(-2.03, 9.46) * mm, "end": v(-2, 9.33) * mm});
            skLineSegment(sketch, "E2641", {"start": v(-2, 9.33) * mm, "end": v(-1.99, 9.2) * mm});
            skLineSegment(sketch, "E2642", {"start": v(-1.99, 9.2) * mm, "end": v(-1.96, 9.08) * mm});
            skLineSegment(sketch, "E2643", {"start": v(-1.96, 9.08) * mm, "end": v(-1.94, 8.95) * mm});
            skLineSegment(sketch, "E2644", {"start": v(-1.94, 8.95) * mm, "end": v(-1.9, 8.82) * mm});
            skLineSegment(sketch, "E2645", {"start": v(-1.9, 8.82) * mm, "end": v(-1.88, 8.69) * mm});
            skLineSegment(sketch, "E2646", {"start": v(-1.88, 8.69) * mm, "end": v(-1.85, 8.56) * mm});
            skLineSegment(sketch, "E2647", {"start": v(-1.85, 8.56) * mm, "end": v(-1.81, 8.43) * mm});
            skLineSegment(sketch, "E2648", {"start": v(-1.81, 8.43) * mm, "end": v(-1.77, 8.3) * mm});
            skLineSegment(sketch, "E2649", {"start": v(-1.77, 8.3) * mm, "end": v(-1.73, 8.18) * mm});
            skLineSegment(sketch, "E2650", {"start": v(-1.73, 8.18) * mm, "end": v(-1.7, 8.05) * mm});
            skLineSegment(sketch, "E2651", {"start": v(-1.7, 8.05) * mm, "end": v(-1.65, 7.92) * mm});
            skLineSegment(sketch, "E2652", {"start": v(-1.65, 7.92) * mm, "end": v(-1.6, 7.8) * mm});
            skLineSegment(sketch, "E2653", {"start": v(-1.6, 7.8) * mm, "end": v(-1.55, 7.66) * mm});
            skLineSegment(sketch, "E2654", {"start": v(-1.55, 7.66) * mm, "end": v(-1.5, 7.54) * mm});
            skLineSegment(sketch, "E2655", {"start": v(-1.5, 7.54) * mm, "end": v(-1.45, 7.4) * mm});
            skLineSegment(sketch, "E2656", {"start": v(-1.45, 7.4) * mm, "end": v(-1.4, 7.28) * mm});
            skLineSegment(sketch, "E2657", {"start": v(-1.4, 7.28) * mm, "end": v(-1.34, 7.15) * mm});
            skLineSegment(sketch, "E2658", {"start": v(-1.34, 7.15) * mm, "end": v(-1.28, 7.03) * mm});
            skLineSegment(sketch, "E2659", {"start": v(-1.28, 7.03) * mm, "end": v(-1.22, 6.9) * mm});
            skLineSegment(sketch, "E2660", {"start": v(-1.22, 6.9) * mm, "end": v(-1.16, 6.77) * mm});
            skLineSegment(sketch, "E2661", {"start": v(-1.16, 6.77) * mm, "end": v(-1.09, 6.64) * mm});
            skLineSegment(sketch, "E2662", {"start": v(-1.09, 6.64) * mm, "end": v(-1.07, 6.61) * mm});
            skLineSegment(sketch, "E2663", {"start": v(-1.07, 6.61) * mm, "end": v(-0.38, 6.61) * mm});
            skLineSegment(sketch, "E2664", {"start": v(-0.38, 6.61) * mm, "end": v(-0.38, 6.62) * mm});
            skLineSegment(sketch, "E2665", {"start": v(9.85, -1.27) * mm, "end": v(9.99, -1.27) * mm});
            skLineSegment(sketch, "E2666", {"start": v(9.99, -1.27) * mm, "end": v(10.12, -1.26) * mm});
            skLineSegment(sketch, "E2667", {"start": v(10.12, -1.26) * mm, "end": v(10.25, -1.25) * mm});
            skLineSegment(sketch, "E2668", {"start": v(10.25, -1.25) * mm, "end": v(10.38, -1.24) * mm});
            skLineSegment(sketch, "E2669", {"start": v(10.38, -1.24) * mm, "end": v(10.51, -1.23) * mm});
            skLineSegment(sketch, "E2670", {"start": v(10.51, -1.23) * mm, "end": v(10.64, -1.22) * mm});
            skLineSegment(sketch, "E2671", {"start": v(10.64, -1.22) * mm, "end": v(10.78, -1.2) * mm});
            skLineSegment(sketch, "E2672", {"start": v(10.78, -1.2) * mm, "end": v(10.9, -1.19) * mm});
            skLineSegment(sketch, "E2673", {"start": v(10.9, -1.19) * mm, "end": v(11.04, -1.17) * mm});
            skLineSegment(sketch, "E2674", {"start": v(11.04, -1.17) * mm, "end": v(11.17, -1.15) * mm});
            skLineSegment(sketch, "E2675", {"start": v(11.17, -1.15) * mm, "end": v(11.3, -1.13) * mm});
            skLineSegment(sketch, "E2676", {"start": v(11.3, -1.13) * mm, "end": v(11.43, -1.1) * mm});
            skLineSegment(sketch, "E2677", {"start": v(11.43, -1.1) * mm, "end": v(11.56, -1.07) * mm});
            skLineSegment(sketch, "E2678", {"start": v(11.56, -1.07) * mm, "end": v(11.7, -1.04) * mm});
            skLineSegment(sketch, "E2679", {"start": v(11.7, -1.04) * mm, "end": v(11.83, -1.01) * mm});
            skLineSegment(sketch, "E2680", {"start": v(11.83, -1.01) * mm, "end": v(11.96, -0.98) * mm});
            skLineSegment(sketch, "E2681", {"start": v(11.96, -0.98) * mm, "end": v(12.09, -0.95) * mm});
            skLineSegment(sketch, "E2682", {"start": v(12.09, -0.95) * mm, "end": v(12.22, -0.9) * mm});
            skLineSegment(sketch, "E2683", {"start": v(12.22, -0.9) * mm, "end": v(12.35, -0.87) * mm});
            skLineSegment(sketch, "E2684", {"start": v(12.35, -0.87) * mm, "end": v(12.48, -0.83) * mm});
            skLineSegment(sketch, "E2685", {"start": v(12.48, -0.83) * mm, "end": v(12.6, -0.79) * mm});
            skLineSegment(sketch, "E2686", {"start": v(12.6, -0.79) * mm, "end": v(12.74, -0.74) * mm});
            skLineSegment(sketch, "E2687", {"start": v(12.74, -0.74) * mm, "end": v(12.87, -0.7) * mm});
            skLineSegment(sketch, "E2688", {"start": v(12.87, -0.7) * mm, "end": v(13, -0.65) * mm});
            skLineSegment(sketch, "E2689", {"start": v(13, -0.65) * mm, "end": v(13.13, -0.6) * mm});
            skLineSegment(sketch, "E2690", {"start": v(13.13, -0.6) * mm, "end": v(13.26, -0.54) * mm});
            skLineSegment(sketch, "E2691", {"start": v(13.26, -0.54) * mm, "end": v(13.39, -0.49) * mm});
            skLineSegment(sketch, "E2692", {"start": v(13.39, -0.49) * mm, "end": v(13.52, -0.43) * mm});
            skLineSegment(sketch, "E2693", {"start": v(13.52, -0.43) * mm, "end": v(13.65, -0.37) * mm});
            skLineSegment(sketch, "E2694", {"start": v(13.65, -0.37) * mm, "end": v(13.66, -0.37) * mm});
            skLineSegment(sketch, "E2695", {"start": v(13.66, -0.37) * mm, "end": v(13.66, 0.27) * mm});
            skLineSegment(sketch, "E2696", {"start": v(13.66, 0.27) * mm, "end": v(13.63, 0.29) * mm});
            skLineSegment(sketch, "E2697", {"start": v(13.63, 0.29) * mm, "end": v(13.5, 0.35) * mm});
            skLineSegment(sketch, "E2698", {"start": v(13.5, 0.35) * mm, "end": v(13.37, 0.42) * mm});
            skLineSegment(sketch, "E2699", {"start": v(13.37, 0.42) * mm, "end": v(13.24, 0.48) * mm});
            skLineSegment(sketch, "E2700", {"start": v(13.24, 0.48) * mm, "end": v(13.1, 0.54) * mm});
            skLineSegment(sketch, "E2701", {"start": v(13.1, 0.54) * mm, "end": v(12.98, 0.6) * mm});
            skLineSegment(sketch, "E2702", {"start": v(12.98, 0.6) * mm, "end": v(12.85, 0.66) * mm});
            skLineSegment(sketch, "E2703", {"start": v(12.85, 0.66) * mm, "end": v(12.72, 0.71) * mm});
            skLineSegment(sketch, "E2704", {"start": v(12.72, 0.71) * mm, "end": v(12.6, 0.76) * mm});
            skLineSegment(sketch, "E2705", {"start": v(12.6, 0.76) * mm, "end": v(12.46, 0.81) * mm});
            skLineSegment(sketch, "E2706", {"start": v(12.46, 0.81) * mm, "end": v(12.33, 0.86) * mm});
            skLineSegment(sketch, "E2707", {"start": v(12.33, 0.86) * mm, "end": v(12.2, 0.9) * mm});
            skLineSegment(sketch, "E2708", {"start": v(12.2, 0.9) * mm, "end": v(12.07, 0.95) * mm});
            skLineSegment(sketch, "E2709", {"start": v(12.07, 0.95) * mm, "end": v(11.94, 0.99) * mm});
            skLineSegment(sketch, "E2710", {"start": v(11.94, 0.99) * mm, "end": v(11.81, 1.03) * mm});
            skLineSegment(sketch, "E2711", {"start": v(11.81, 1.03) * mm, "end": v(11.68, 1.06) * mm});
            skLineSegment(sketch, "E2712", {"start": v(11.68, 1.06) * mm, "end": v(11.55, 1.1) * mm});
            skLineSegment(sketch, "E2713", {"start": v(11.55, 1.1) * mm, "end": v(11.42, 1.13) * mm});
            skLineSegment(sketch, "E2714", {"start": v(11.42, 1.13) * mm, "end": v(11.3, 1.16) * mm});
            skLineSegment(sketch, "E2715", {"start": v(11.3, 1.16) * mm, "end": v(11.16, 1.18) * mm});
            skLineSegment(sketch, "E2716", {"start": v(11.16, 1.18) * mm, "end": v(11.03, 1.2) * mm});
            skLineSegment(sketch, "E2717", {"start": v(11.03, 1.2) * mm, "end": v(10.9, 1.23) * mm});
            skLineSegment(sketch, "E2718", {"start": v(10.9, 1.23) * mm, "end": v(10.77, 1.25) * mm});
            skLineSegment(sketch, "E2719", {"start": v(10.77, 1.25) * mm, "end": v(10.64, 1.27) * mm});
            skLineSegment(sketch, "E2720", {"start": v(10.64, 1.27) * mm, "end": v(10.5, 1.28) * mm});
            skLineSegment(sketch, "E2721", {"start": v(10.5, 1.28) * mm, "end": v(10.38, 1.3) * mm});
            skLineSegment(sketch, "E2722", {"start": v(10.38, 1.3) * mm, "end": v(10.25, 1.3) * mm});
            skLineSegment(sketch, "E2723", {"start": v(10.25, 1.3) * mm, "end": v(10.11, 1.31) * mm});
            skLineSegment(sketch, "E2724", {"start": v(10.11, 1.31) * mm, "end": v(9.98, 1.32) * mm});
            skLineSegment(sketch, "E2725", {"start": v(9.98, 1.32) * mm, "end": v(9.85, 1.32) * mm});
            skLineSegment(sketch, "E2726", {"start": v(9.85, 1.32) * mm, "end": v(9.72, 1.32) * mm});
            skLineSegment(sketch, "E2727", {"start": v(9.72, 1.32) * mm, "end": v(9.6, 1.32) * mm});
            skLineSegment(sketch, "E2728", {"start": v(9.6, 1.32) * mm, "end": v(9.46, 1.32) * mm});
            skLineSegment(sketch, "E2729", {"start": v(9.46, 1.32) * mm, "end": v(9.33, 1.31) * mm});
            skLineSegment(sketch, "E2730", {"start": v(9.33, 1.31) * mm, "end": v(9.2, 1.3) * mm});
            skLineSegment(sketch, "E2731", {"start": v(9.2, 1.3) * mm, "end": v(9.07, 1.3) * mm});
            skLineSegment(sketch, "E2732", {"start": v(9.07, 1.3) * mm, "end": v(8.95, 1.28) * mm});
            skLineSegment(sketch, "E2733", {"start": v(8.95, 1.28) * mm, "end": v(8.82, 1.27) * mm});
            skLineSegment(sketch, "E2734", {"start": v(8.82, 1.27) * mm, "end": v(8.69, 1.25) * mm});
            skLineSegment(sketch, "E2735", {"start": v(8.69, 1.25) * mm, "end": v(8.56, 1.23) * mm});
            skLineSegment(sketch, "E2736", {"start": v(8.56, 1.23) * mm, "end": v(8.43, 1.21) * mm});
            skLineSegment(sketch, "E2737", {"start": v(8.43, 1.21) * mm, "end": v(8.3, 1.19) * mm});
            skLineSegment(sketch, "E2738", {"start": v(8.3, 1.19) * mm, "end": v(8.17, 1.16) * mm});
            skLineSegment(sketch, "E2739", {"start": v(8.17, 1.16) * mm, "end": v(8.04, 1.13) * mm});
            skLineSegment(sketch, "E2740", {"start": v(8.04, 1.13) * mm, "end": v(7.92, 1.1) * mm});
            skLineSegment(sketch, "E2741", {"start": v(7.92, 1.1) * mm, "end": v(7.79, 1.07) * mm});
            skLineSegment(sketch, "E2742", {"start": v(7.79, 1.07) * mm, "end": v(7.66, 1.04) * mm});
            skLineSegment(sketch, "E2743", {"start": v(7.66, 1.04) * mm, "end": v(7.53, 1) * mm});
            skLineSegment(sketch, "E2744", {"start": v(7.53, 1) * mm, "end": v(7.4, 0.96) * mm});
            skLineSegment(sketch, "E2745", {"start": v(7.4, 0.96) * mm, "end": v(7.28, 0.92) * mm});
            skLineSegment(sketch, "E2746", {"start": v(7.28, 0.92) * mm, "end": v(7.15, 0.87) * mm});
            skLineSegment(sketch, "E2747", {"start": v(7.15, 0.87) * mm, "end": v(7.02, 0.83) * mm});
            skLineSegment(sketch, "E2748", {"start": v(7.02, 0.83) * mm, "end": v(6.9, 0.78) * mm});
            skLineSegment(sketch, "E2749", {"start": v(6.9, 0.78) * mm, "end": v(6.76, 0.73) * mm});
            skLineSegment(sketch, "E2750", {"start": v(6.76, 0.73) * mm, "end": v(6.64, 0.68) * mm});
            skLineSegment(sketch, "E2751", {"start": v(6.64, 0.68) * mm, "end": v(6.5, 0.62) * mm});
            skLineSegment(sketch, "E2752", {"start": v(6.5, 0.62) * mm, "end": v(6.38, 0.57) * mm});
            skLineSegment(sketch, "E2753", {"start": v(6.38, 0.57) * mm, "end": v(6.25, 0.5) * mm});
            skLineSegment(sketch, "E2754", {"start": v(6.25, 0.5) * mm, "end": v(6.12, 0.44) * mm});
            skLineSegment(sketch, "E2755", {"start": v(6.12, 0.44) * mm, "end": v(6, 0.38) * mm});
            skLineSegment(sketch, "E2756", {"start": v(6, 0.38) * mm, "end": v(5.87, 0.31) * mm});
            skLineSegment(sketch, "E2757", {"start": v(5.87, 0.31) * mm, "end": v(5.84, 0.3) * mm});
            skLineSegment(sketch, "E2758", {"start": v(5.84, 0.3) * mm, "end": v(5.84, -0.4) * mm});
            skLineSegment(sketch, "E2759", {"start": v(5.84, -0.4) * mm, "end": v(5.85, -0.4) * mm});
            skLineSegment(sketch, "E2760", {"start": v(5.85, -0.4) * mm, "end": v(5.98, -0.45) * mm});
            skLineSegment(sketch, "E2761", {"start": v(5.98, -0.45) * mm, "end": v(6.1, -0.5) * mm});
            skLineSegment(sketch, "E2762", {"start": v(6.1, -0.5) * mm, "end": v(6.23, -0.56) * mm});
            skLineSegment(sketch, "E2763", {"start": v(6.23, -0.56) * mm, "end": v(6.36, -0.61) * mm});
            skLineSegment(sketch, "E2764", {"start": v(6.36, -0.61) * mm, "end": v(6.49, -0.66) * mm});
            skLineSegment(sketch, "E2765", {"start": v(6.49, -0.66) * mm, "end": v(6.62, -0.71) * mm});
            skLineSegment(sketch, "E2766", {"start": v(6.62, -0.71) * mm, "end": v(6.74, -0.76) * mm});
            skLineSegment(sketch, "E2767", {"start": v(6.74, -0.76) * mm, "end": v(6.87, -0.8) * mm});
            skLineSegment(sketch, "E2768", {"start": v(6.87, -0.8) * mm, "end": v(7, -0.84) * mm});
            skLineSegment(sketch, "E2769", {"start": v(7, -0.84) * mm, "end": v(7.13, -0.88) * mm});
            skLineSegment(sketch, "E2770", {"start": v(7.13, -0.88) * mm, "end": v(7.26, -0.92) * mm});
            skLineSegment(sketch, "E2771", {"start": v(7.26, -0.92) * mm, "end": v(7.39, -0.95) * mm});
            skLineSegment(sketch, "E2772", {"start": v(7.39, -0.95) * mm, "end": v(7.52, -0.99) * mm});
            skLineSegment(sketch, "E2773", {"start": v(7.52, -0.99) * mm, "end": v(7.65, -1.02) * mm});
            skLineSegment(sketch, "E2774", {"start": v(7.65, -1.02) * mm, "end": v(7.77, -1.05) * mm});
            skLineSegment(sketch, "E2775", {"start": v(7.77, -1.05) * mm, "end": v(7.9, -1.08) * mm});
            skLineSegment(sketch, "E2776", {"start": v(7.9, -1.08) * mm, "end": v(8.03, -1.1) * mm});
            skLineSegment(sketch, "E2777", {"start": v(8.03, -1.1) * mm, "end": v(8.16, -1.13) * mm});
            skLineSegment(sketch, "E2778", {"start": v(8.16, -1.13) * mm, "end": v(8.3, -1.15) * mm});
            skLineSegment(sketch, "E2779", {"start": v(8.3, -1.15) * mm, "end": v(8.42, -1.17) * mm});
            skLineSegment(sketch, "E2780", {"start": v(8.42, -1.17) * mm, "end": v(8.55, -1.2) * mm});
            skLineSegment(sketch, "E2781", {"start": v(8.55, -1.2) * mm, "end": v(8.68, -1.2) * mm});
            skLineSegment(sketch, "E2782", {"start": v(8.68, -1.2) * mm, "end": v(8.8, -1.22) * mm});
            skLineSegment(sketch, "E2783", {"start": v(8.8, -1.22) * mm, "end": v(8.94, -1.23) * mm});
            skLineSegment(sketch, "E2784", {"start": v(8.94, -1.23) * mm, "end": v(9.07, -1.25) * mm});
            skLineSegment(sketch, "E2785", {"start": v(9.07, -1.25) * mm, "end": v(9.2, -1.25) * mm});
            skLineSegment(sketch, "E2786", {"start": v(9.2, -1.25) * mm, "end": v(9.33, -1.26) * mm});
            skLineSegment(sketch, "E2787", {"start": v(9.33, -1.26) * mm, "end": v(9.46, -1.27) * mm});
            skLineSegment(sketch, "E2788", {"start": v(9.46, -1.27) * mm, "end": v(9.6, -1.27) * mm});
            skLineSegment(sketch, "E2789", {"start": v(9.6, -1.27) * mm, "end": v(9.72, -1.27) * mm});
            skLineSegment(sketch, "E2790", {"start": v(9.72, -1.27) * mm, "end": v(9.85, -1.27) * mm});
            skLineSegment(sketch, "E2791", {"start": v(-11.14, -1.32) * mm, "end": v(-11.01, -1.32) * mm});
            skLineSegment(sketch, "E2792", {"start": v(-11.01, -1.32) * mm, "end": v(-10.88, -1.32) * mm});
            skLineSegment(sketch, "E2793", {"start": v(-10.88, -1.32) * mm, "end": v(-10.75, -1.3) * mm});
            skLineSegment(sketch, "E2794", {"start": v(-10.75, -1.3) * mm, "end": v(-10.62, -1.3) * mm});
            skLineSegment(sketch, "E2795", {"start": v(-10.62, -1.3) * mm, "end": v(-10.5, -1.28) * mm});
            skLineSegment(sketch, "E2796", {"start": v(-10.5, -1.28) * mm, "end": v(-10.36, -1.27) * mm});
            skLineSegment(sketch, "E2797", {"start": v(-10.36, -1.27) * mm, "end": v(-10.24, -1.25) * mm});
            skLineSegment(sketch, "E2798", {"start": v(-10.24, -1.25) * mm, "end": v(-10.1, -1.23) * mm});
            skLineSegment(sketch, "E2799", {"start": v(-10.1, -1.23) * mm, "end": v(-9.98, -1.21) * mm});
            skLineSegment(sketch, "E2800", {"start": v(-9.98, -1.21) * mm, "end": v(-9.85, -1.19) * mm});
            skLineSegment(sketch, "E2801", {"start": v(-9.85, -1.19) * mm, "end": v(-9.72, -1.16) * mm});
            skLineSegment(sketch, "E2802", {"start": v(-9.72, -1.16) * mm, "end": v(-9.6, -1.13) * mm});
            skLineSegment(sketch, "E2803", {"start": v(-9.6, -1.13) * mm, "end": v(-9.46, -1.1) * mm});
            skLineSegment(sketch, "E2804", {"start": v(-9.46, -1.1) * mm, "end": v(-9.34, -1.07) * mm});
            skLineSegment(sketch, "E2805", {"start": v(-9.34, -1.07) * mm, "end": v(-9.2, -1.04) * mm});
            skLineSegment(sketch, "E2806", {"start": v(-9.2, -1.04) * mm, "end": v(-9.08, -1) * mm});
            skLineSegment(sketch, "E2807", {"start": v(-9.08, -1) * mm, "end": v(-8.95, -0.96) * mm});
            skLineSegment(sketch, "E2808", {"start": v(-8.95, -0.96) * mm, "end": v(-8.82, -0.92) * mm});
            skLineSegment(sketch, "E2809", {"start": v(-8.82, -0.92) * mm, "end": v(-8.7, -0.88) * mm});
            skLineSegment(sketch, "E2810", {"start": v(-8.7, -0.88) * mm, "end": v(-8.57, -0.83) * mm});
            skLineSegment(sketch, "E2811", {"start": v(-8.57, -0.83) * mm, "end": v(-8.44, -0.78) * mm});
            skLineSegment(sketch, "E2812", {"start": v(-8.44, -0.78) * mm, "end": v(-8.31, -0.73) * mm});
            skLineSegment(sketch, "E2813", {"start": v(-8.31, -0.73) * mm, "end": v(-8.18, -0.68) * mm});
            skLineSegment(sketch, "E2814", {"start": v(-8.18, -0.68) * mm, "end": v(-8.06, -0.62) * mm});
            skLineSegment(sketch, "E2815", {"start": v(-8.06, -0.62) * mm, "end": v(-7.93, -0.57) * mm});
            skLineSegment(sketch, "E2816", {"start": v(-7.93, -0.57) * mm, "end": v(-7.8, -0.5) * mm});
            skLineSegment(sketch, "E2817", {"start": v(-7.8, -0.5) * mm, "end": v(-7.67, -0.45) * mm});
            skLineSegment(sketch, "E2818", {"start": v(-7.67, -0.45) * mm, "end": v(-7.54, -0.38) * mm});
            skLineSegment(sketch, "E2819", {"start": v(-7.54, -0.38) * mm, "end": v(-7.42, -0.32) * mm});
            skLineSegment(sketch, "E2820", {"start": v(-7.42, -0.32) * mm, "end": v(-7.39, -0.3) * mm});
            skLineSegment(sketch, "E2821", {"start": v(-7.39, -0.3) * mm, "end": v(-7.39, 0.4) * mm});
            skLineSegment(sketch, "E2822", {"start": v(-7.39, 0.4) * mm, "end": v(-7.4, 0.4) * mm});
            skLineSegment(sketch, "E2823", {"start": v(-7.4, 0.4) * mm, "end": v(-7.52, 0.45) * mm});
            skLineSegment(sketch, "E2824", {"start": v(-7.52, 0.45) * mm, "end": v(-7.65, 0.5) * mm});
            skLineSegment(sketch, "E2825", {"start": v(-7.65, 0.5) * mm, "end": v(-7.78, 0.56) * mm});
            skLineSegment(sketch, "E2826", {"start": v(-7.78, 0.56) * mm, "end": v(-7.9, 0.61) * mm});
            skLineSegment(sketch, "E2827", {"start": v(-7.9, 0.61) * mm, "end": v(-8.04, 0.66) * mm});
            skLineSegment(sketch, "E2828", {"start": v(-8.04, 0.66) * mm, "end": v(-8.16, 0.7) * mm});
            skLineSegment(sketch, "E2829", {"start": v(-8.16, 0.7) * mm, "end": v(-8.3, 0.76) * mm});
            skLineSegment(sketch, "E2830", {"start": v(-8.3, 0.76) * mm, "end": v(-8.42, 0.8) * mm});
            skLineSegment(sketch, "E2831", {"start": v(-8.42, 0.8) * mm, "end": v(-8.55, 0.84) * mm});
            skLineSegment(sketch, "E2832", {"start": v(-8.55, 0.84) * mm, "end": v(-8.68, 0.88) * mm});
            skLineSegment(sketch, "E2833", {"start": v(-8.68, 0.88) * mm, "end": v(-8.8, 0.92) * mm});
            skLineSegment(sketch, "E2834", {"start": v(-8.8, 0.92) * mm, "end": v(-8.94, 0.95) * mm});
            skLineSegment(sketch, "E2835", {"start": v(-8.94, 0.95) * mm, "end": v(-9.06, 0.99) * mm});
            skLineSegment(sketch, "E2836", {"start": v(-9.06, 0.99) * mm, "end": v(-9.2, 1.02) * mm});
            skLineSegment(sketch, "E2837", {"start": v(-9.2, 1.02) * mm, "end": v(-9.32, 1.05) * mm});
            skLineSegment(sketch, "E2838", {"start": v(-9.32, 1.05) * mm, "end": v(-9.45, 1.08) * mm});
            skLineSegment(sketch, "E2839", {"start": v(-9.45, 1.08) * mm, "end": v(-9.58, 1.1) * mm});
            skLineSegment(sketch, "E2840", {"start": v(-9.58, 1.1) * mm, "end": v(-9.71, 1.13) * mm});
            skLineSegment(sketch, "E2841", {"start": v(-9.71, 1.13) * mm, "end": v(-9.84, 1.15) * mm});
            skLineSegment(sketch, "E2842", {"start": v(-9.84, 1.15) * mm, "end": v(-9.97, 1.17) * mm});
            skLineSegment(sketch, "E2843", {"start": v(-9.97, 1.17) * mm, "end": v(-10.1, 1.19) * mm});
            skLineSegment(sketch, "E2844", {"start": v(-10.1, 1.19) * mm, "end": v(-10.23, 1.2) * mm});
            skLineSegment(sketch, "E2845", {"start": v(-10.23, 1.2) * mm, "end": v(-10.36, 1.22) * mm});
            skLineSegment(sketch, "E2846", {"start": v(-10.36, 1.22) * mm, "end": v(-10.49, 1.23) * mm});
            skLineSegment(sketch, "E2847", {"start": v(-10.49, 1.23) * mm, "end": v(-10.62, 1.24) * mm});
            skLineSegment(sketch, "E2848", {"start": v(-10.62, 1.24) * mm, "end": v(-10.75, 1.25) * mm});
            skLineSegment(sketch, "E2849", {"start": v(-10.75, 1.25) * mm, "end": v(-10.88, 1.26) * mm});
            skLineSegment(sketch, "E2850", {"start": v(-10.88, 1.26) * mm, "end": v(-11, 1.27) * mm});
            skLineSegment(sketch, "E2851", {"start": v(-11, 1.27) * mm, "end": v(-11.14, 1.27) * mm});
            skLineSegment(sketch, "E2852", {"start": v(-11.14, 1.27) * mm, "end": v(-11.27, 1.27) * mm});
            skLineSegment(sketch, "E2853", {"start": v(-11.27, 1.27) * mm, "end": v(-11.4, 1.27) * mm});
            skLineSegment(sketch, "E2854", {"start": v(-11.4, 1.27) * mm, "end": v(-11.53, 1.26) * mm});
            skLineSegment(sketch, "E2855", {"start": v(-11.53, 1.26) * mm, "end": v(-11.67, 1.26) * mm});
            skLineSegment(sketch, "E2856", {"start": v(-11.67, 1.26) * mm, "end": v(-11.8, 1.25) * mm});
            skLineSegment(sketch, "E2857", {"start": v(-11.8, 1.25) * mm, "end": v(-11.93, 1.24) * mm});
            skLineSegment(sketch, "E2858", {"start": v(-11.93, 1.24) * mm, "end": v(-12.06, 1.23) * mm});
            skLineSegment(sketch, "E2859", {"start": v(-12.06, 1.23) * mm, "end": v(-12.2, 1.22) * mm});
            skLineSegment(sketch, "E2860", {"start": v(-12.2, 1.22) * mm, "end": v(-12.32, 1.2) * mm});
            skLineSegment(sketch, "E2861", {"start": v(-12.32, 1.2) * mm, "end": v(-12.46, 1.19) * mm});
            skLineSegment(sketch, "E2862", {"start": v(-12.46, 1.19) * mm, "end": v(-12.59, 1.17) * mm});
            skLineSegment(sketch, "E2863", {"start": v(-12.59, 1.17) * mm, "end": v(-12.72, 1.15) * mm});
            skLineSegment(sketch, "E2864", {"start": v(-12.72, 1.15) * mm, "end": v(-12.85, 1.12) * mm});
            skLineSegment(sketch, "E2865", {"start": v(-12.85, 1.12) * mm, "end": v(-12.98, 1.1) * mm});
            skLineSegment(sketch, "E2866", {"start": v(-12.98, 1.1) * mm, "end": v(-13.11, 1.07) * mm});
            skLineSegment(sketch, "E2867", {"start": v(-13.11, 1.07) * mm, "end": v(-13.24, 1.04) * mm});
            skLineSegment(sketch, "E2868", {"start": v(-13.24, 1.04) * mm, "end": v(-13.37, 1.01) * mm});
            skLineSegment(sketch, "E2869", {"start": v(-13.37, 1.01) * mm, "end": v(-13.5, 0.98) * mm});
            skLineSegment(sketch, "E2870", {"start": v(-13.5, 0.98) * mm, "end": v(-13.63, 0.94) * mm});
            skLineSegment(sketch, "E2871", {"start": v(-13.63, 0.94) * mm, "end": v(-13.77, 0.9) * mm});
            skLineSegment(sketch, "E2872", {"start": v(-13.77, 0.9) * mm, "end": v(-13.9, 0.87) * mm});
            skLineSegment(sketch, "E2873", {"start": v(-13.9, 0.87) * mm, "end": v(-14.03, 0.83) * mm});
            skLineSegment(sketch, "E2874", {"start": v(-14.03, 0.83) * mm, "end": v(-14.16, 0.79) * mm});
            skLineSegment(sketch, "E2875", {"start": v(-14.16, 0.79) * mm, "end": v(-14.29, 0.74) * mm});
            skLineSegment(sketch, "E2876", {"start": v(-14.29, 0.74) * mm, "end": v(-14.42, 0.7) * mm});
            skLineSegment(sketch, "E2877", {"start": v(-14.42, 0.7) * mm, "end": v(-14.55, 0.65) * mm});
            skLineSegment(sketch, "E2878", {"start": v(-14.55, 0.65) * mm, "end": v(-14.68, 0.6) * mm});
            skLineSegment(sketch, "E2879", {"start": v(-14.68, 0.6) * mm, "end": v(-14.8, 0.54) * mm});
            skLineSegment(sketch, "E2880", {"start": v(-14.8, 0.54) * mm, "end": v(-14.94, 0.49) * mm});
            skLineSegment(sketch, "E2881", {"start": v(-14.94, 0.49) * mm, "end": v(-15.07, 0.43) * mm});
            skLineSegment(sketch, "E2882", {"start": v(-15.07, 0.43) * mm, "end": v(-15.2, 0.37) * mm});
            skLineSegment(sketch, "E2883", {"start": v(-15.2, 0.37) * mm, "end": v(-15.21, 0.36) * mm});
            skLineSegment(sketch, "E2884", {"start": v(-15.21, 0.36) * mm, "end": v(-15.21, -0.27) * mm});
            skLineSegment(sketch, "E2885", {"start": v(-15.21, -0.27) * mm, "end": v(-15.18, -0.29) * mm});
            skLineSegment(sketch, "E2886", {"start": v(-15.18, -0.29) * mm, "end": v(-15.05, -0.35) * mm});
            skLineSegment(sketch, "E2887", {"start": v(-15.05, -0.35) * mm, "end": v(-14.92, -0.42) * mm});
            skLineSegment(sketch, "E2888", {"start": v(-14.92, -0.42) * mm, "end": v(-14.79, -0.48) * mm});
            skLineSegment(sketch, "E2889", {"start": v(-14.79, -0.48) * mm, "end": v(-14.66, -0.54) * mm});
            skLineSegment(sketch, "E2890", {"start": v(-14.66, -0.54) * mm, "end": v(-14.53, -0.6) * mm});
            skLineSegment(sketch, "E2891", {"start": v(-14.53, -0.6) * mm, "end": v(-14.4, -0.66) * mm});
            skLineSegment(sketch, "E2892", {"start": v(-14.4, -0.66) * mm, "end": v(-14.27, -0.71) * mm});
            skLineSegment(sketch, "E2893", {"start": v(-14.27, -0.71) * mm, "end": v(-14.14, -0.77) * mm});
            skLineSegment(sketch, "E2894", {"start": v(-14.14, -0.77) * mm, "end": v(-14, -0.82) * mm});
            skLineSegment(sketch, "E2895", {"start": v(-14, -0.82) * mm, "end": v(-13.88, -0.86) * mm});
            skLineSegment(sketch, "E2896", {"start": v(-13.88, -0.86) * mm, "end": v(-13.75, -0.9) * mm});
            skLineSegment(sketch, "E2897", {"start": v(-13.75, -0.9) * mm, "end": v(-13.62, -0.95) * mm});
            skLineSegment(sketch, "E2898", {"start": v(-13.62, -0.95) * mm, "end": v(-13.49, -1) * mm});
            skLineSegment(sketch, "E2899", {"start": v(-13.49, -1) * mm, "end": v(-13.36, -1.03) * mm});
            skLineSegment(sketch, "E2900", {"start": v(-13.36, -1.03) * mm, "end": v(-13.23, -1.06) * mm});
            skLineSegment(sketch, "E2901", {"start": v(-13.23, -1.06) * mm, "end": v(-13.1, -1.1) * mm});
            skLineSegment(sketch, "E2902", {"start": v(-13.1, -1.1) * mm, "end": v(-12.97, -1.13) * mm});
            skLineSegment(sketch, "E2903", {"start": v(-12.97, -1.13) * mm, "end": v(-12.84, -1.16) * mm});
            skLineSegment(sketch, "E2904", {"start": v(-12.84, -1.16) * mm, "end": v(-12.7, -1.19) * mm});
            skLineSegment(sketch, "E2905", {"start": v(-12.7, -1.19) * mm, "end": v(-12.58, -1.2) * mm});
            skLineSegment(sketch, "E2906", {"start": v(-12.58, -1.2) * mm, "end": v(-12.45, -1.23) * mm});
            skLineSegment(sketch, "E2907", {"start": v(-12.45, -1.23) * mm, "end": v(-12.32, -1.25) * mm});
            skLineSegment(sketch, "E2908", {"start": v(-12.32, -1.25) * mm, "end": v(-12.19, -1.27) * mm});
            skLineSegment(sketch, "E2909", {"start": v(-12.19, -1.27) * mm, "end": v(-12.06, -1.28) * mm});
            skLineSegment(sketch, "E2910", {"start": v(-12.06, -1.28) * mm, "end": v(-11.92, -1.3) * mm});
            skLineSegment(sketch, "E2911", {"start": v(-11.92, -1.3) * mm, "end": v(-11.8, -1.3) * mm});
            skLineSegment(sketch, "E2912", {"start": v(-11.8, -1.3) * mm, "end": v(-11.66, -1.31) * mm});
            skLineSegment(sketch, "E2913", {"start": v(-11.66, -1.31) * mm, "end": v(-11.53, -1.32) * mm});
            skLineSegment(sketch, "E2914", {"start": v(-11.53, -1.32) * mm, "end": v(-11.4, -1.32) * mm});
            skLineSegment(sketch, "E2915", {"start": v(-11.4, -1.32) * mm, "end": v(-11.27, -1.33) * mm});
            skLineSegment(sketch, "E2916", {"start": v(-11.27, -1.33) * mm, "end": v(-11.14, -1.32) * mm});
            skLineSegment(sketch, "E2917", {"start": v(-2.07, -17.84) * mm, "end": v(-2.17, -17.6) * mm});
            skLineSegment(sketch, "E2918", {"start": v(-2.17, -17.6) * mm, "end": v(-2.27, -17.35) * mm});
            skLineSegment(sketch, "E2919", {"start": v(-2.27, -17.35) * mm, "end": v(-2.37, -17.1) * mm});
            skLineSegment(sketch, "E2920", {"start": v(-2.37, -17.1) * mm, "end": v(-2.46, -16.86) * mm});
            skLineSegment(sketch, "E2921", {"start": v(-2.46, -16.86) * mm, "end": v(-2.55, -16.62) * mm});
            skLineSegment(sketch, "E2922", {"start": v(-2.55, -16.62) * mm, "end": v(-2.63, -16.38) * mm});
            skLineSegment(sketch, "E2923", {"start": v(-2.63, -16.38) * mm, "end": v(-2.71, -16.13) * mm});
            skLineSegment(sketch, "E2924", {"start": v(-2.71, -16.13) * mm, "end": v(-2.8, -15.89) * mm});
            skLineSegment(sketch, "E2925", {"start": v(-2.8, -15.89) * mm, "end": v(-2.87, -15.64) * mm});
            skLineSegment(sketch, "E2926", {"start": v(-2.87, -15.64) * mm, "end": v(-2.94, -15.4) * mm});
            skLineSegment(sketch, "E2927", {"start": v(-2.94, -15.4) * mm, "end": v(-3, -15.15) * mm});
            skLineSegment(sketch, "E2928", {"start": v(-3, -15.15) * mm, "end": v(-3.07, -14.9) * mm});
            skLineSegment(sketch, "E2929", {"start": v(-3.07, -14.9) * mm, "end": v(-3.13, -14.66) * mm});
            skLineSegment(sketch, "E2930", {"start": v(-3.13, -14.66) * mm, "end": v(-3.19, -14.42) * mm});
            skLineSegment(sketch, "E2931", {"start": v(-3.19, -14.42) * mm, "end": v(-3.24, -14.17) * mm});
            skLineSegment(sketch, "E2932", {"start": v(-3.24, -14.17) * mm, "end": v(-3.3, -13.92) * mm});
            skLineSegment(sketch, "E2933", {"start": v(-3.3, -13.92) * mm, "end": v(-3.34, -13.68) * mm});
            skLineSegment(sketch, "E2934", {"start": v(-3.34, -13.68) * mm, "end": v(-3.38, -13.43) * mm});
            skLineSegment(sketch, "E2935", {"start": v(-3.38, -13.43) * mm, "end": v(-3.42, -13.18) * mm});
            skLineSegment(sketch, "E2936", {"start": v(-3.42, -13.18) * mm, "end": v(-3.46, -12.94) * mm});
            skLineSegment(sketch, "E2937", {"start": v(-3.46, -12.94) * mm, "end": v(-3.5, -12.69) * mm});
            skLineSegment(sketch, "E2938", {"start": v(-3.5, -12.69) * mm, "end": v(-3.52, -12.44) * mm});
            skLineSegment(sketch, "E2939", {"start": v(-3.52, -12.44) * mm, "end": v(-3.55, -12.2) * mm});
            skLineSegment(sketch, "E2940", {"start": v(-3.55, -12.2) * mm, "end": v(-3.57, -11.94) * mm});
            skLineSegment(sketch, "E2941", {"start": v(-3.57, -11.94) * mm, "end": v(-3.6, -11.7) * mm});
            skLineSegment(sketch, "E2942", {"start": v(-3.6, -11.7) * mm, "end": v(-3.6, -11.45) * mm});
            skLineSegment(sketch, "E2943", {"start": v(-3.6, -11.45) * mm, "end": v(-3.62, -11.2) * mm});
            skLineSegment(sketch, "E2944", {"start": v(-3.62, -11.2) * mm, "end": v(-3.63, -10.95) * mm});
            skLineSegment(sketch, "E2945", {"start": v(-3.63, -10.95) * mm, "end": v(-3.64, -10.7) * mm});
            skLineSegment(sketch, "E2946", {"start": v(-3.64, -10.7) * mm, "end": v(-3.64, -10.45) * mm});
            skLineSegment(sketch, "E2947", {"start": v(-3.64, -10.45) * mm, "end": v(-3.64, -10.2) * mm});
            skLineSegment(sketch, "E2948", {"start": v(-3.64, -10.2) * mm, "end": v(-3.63, -9.96) * mm});
            skLineSegment(sketch, "E2949", {"start": v(-3.63, -9.96) * mm, "end": v(-3.62, -9.71) * mm});
            skLineSegment(sketch, "E2950", {"start": v(-3.62, -9.71) * mm, "end": v(-3.61, -9.47) * mm});
            skLineSegment(sketch, "E2951", {"start": v(-3.61, -9.47) * mm, "end": v(-3.6, -9.22) * mm});
            skLineSegment(sketch, "E2952", {"start": v(-3.6, -9.22) * mm, "end": v(-3.58, -8.98) * mm});
            skLineSegment(sketch, "E2953", {"start": v(-3.58, -8.98) * mm, "end": v(-3.55, -8.73) * mm});
            skLineSegment(sketch, "E2954", {"start": v(-3.55, -8.73) * mm, "end": v(-3.53, -8.49) * mm});
            skLineSegment(sketch, "E2955", {"start": v(-3.53, -8.49) * mm, "end": v(-3.5, -8.24) * mm});
            skLineSegment(sketch, "E2956", {"start": v(-3.5, -8.24) * mm, "end": v(-3.47, -8) * mm});
            skLineSegment(sketch, "E2957", {"start": v(-3.47, -8) * mm, "end": v(-3.43, -7.76) * mm});
            skLineSegment(sketch, "E2958", {"start": v(-3.43, -7.76) * mm, "end": v(-3.4, -7.51) * mm});
            skLineSegment(sketch, "E2959", {"start": v(-3.4, -7.51) * mm, "end": v(-3.35, -7.27) * mm});
            skLineSegment(sketch, "E2960", {"start": v(-3.35, -7.27) * mm, "end": v(-3.3, -7.03) * mm});
            skLineSegment(sketch, "E2961", {"start": v(-3.3, -7.03) * mm, "end": v(-3.25, -6.78) * mm});
            skLineSegment(sketch, "E2962", {"start": v(-3.25, -6.78) * mm, "end": v(-3.2, -6.54) * mm});
            skLineSegment(sketch, "E2963", {"start": v(-3.2, -6.54) * mm, "end": v(-3.15, -6.3) * mm});
            skLineSegment(sketch, "E2964", {"start": v(-3.15, -6.3) * mm, "end": v(-3.09, -6.06) * mm});
            skLineSegment(sketch, "E2965", {"start": v(-3.09, -6.06) * mm, "end": v(-3.02, -5.81) * mm});
            skLineSegment(sketch, "E2966", {"start": v(-3.02, -5.81) * mm, "end": v(-2.96, -5.57) * mm});
            skLineSegment(sketch, "E2967", {"start": v(-2.96, -5.57) * mm, "end": v(-2.89, -5.33) * mm});
            skLineSegment(sketch, "E2968", {"start": v(-2.89, -5.33) * mm, "end": v(-2.82, -5.09) * mm});
            skLineSegment(sketch, "E2969", {"start": v(-2.82, -5.09) * mm, "end": v(-2.74, -4.85) * mm});
            skLineSegment(sketch, "E2970", {"start": v(-2.74, -4.85) * mm, "end": v(-2.66, -4.6) * mm});
            skLineSegment(sketch, "E2971", {"start": v(-2.66, -4.6) * mm, "end": v(-2.58, -4.37) * mm});
            skLineSegment(sketch, "E2972", {"start": v(-2.58, -4.37) * mm, "end": v(-2.5, -4.13) * mm});
            skLineSegment(sketch, "E2973", {"start": v(-2.5, -4.13) * mm, "end": v(-2.4, -3.89) * mm});
            skLineSegment(sketch, "E2974", {"start": v(-2.4, -3.89) * mm, "end": v(-2.31, -3.65) * mm});
            skLineSegment(sketch, "E2975", {"start": v(-2.31, -3.65) * mm, "end": v(-2.22, -3.4) * mm});
            skLineSegment(sketch, "E2976", {"start": v(-2.22, -3.4) * mm, "end": v(-2.12, -3.17) * mm});
            skLineSegment(sketch, "E2977", {"start": v(-2.12, -3.17) * mm, "end": v(-2.02, -2.95) * mm});
            skLineSegment(sketch, "E2978", {"start": v(-2.02, -2.95) * mm, "end": v(-2.14, -2.9) * mm});
            skLineSegment(sketch, "E2979", {"start": v(-2.14, -2.9) * mm, "end": v(-2.32, -2.8) * mm});
            skLineSegment(sketch, "E2980", {"start": v(-2.32, -2.8) * mm, "end": v(-2.49, -2.7) * mm});
            skLineSegment(sketch, "E2981", {"start": v(-2.49, -2.7) * mm, "end": v(-2.66, -2.6) * mm});
            skLineSegment(sketch, "E2982", {"start": v(-2.66, -2.6) * mm, "end": v(-2.82, -2.47) * mm});
            skLineSegment(sketch, "E2983", {"start": v(-2.82, -2.47) * mm, "end": v(-2.97, -2.33) * mm});
            skLineSegment(sketch, "E2984", {"start": v(-2.97, -2.33) * mm, "end": v(-3.1, -2.2) * mm});
            skLineSegment(sketch, "E2985", {"start": v(-3.1, -2.2) * mm, "end": v(-3.24, -2.04) * mm});
            skLineSegment(sketch, "E2986", {"start": v(-3.24, -2.04) * mm, "end": v(-3.36, -1.88) * mm});
            skLineSegment(sketch, "E2987", {"start": v(-3.36, -1.88) * mm, "end": v(-3.48, -1.72) * mm});
            skLineSegment(sketch, "E2988", {"start": v(-3.48, -1.72) * mm, "end": v(-3.58, -1.54) * mm});
            skLineSegment(sketch, "E2989", {"start": v(-3.58, -1.54) * mm, "end": v(-3.67, -1.36) * mm});
            skLineSegment(sketch, "E2990", {"start": v(-3.67, -1.36) * mm, "end": v(-3.75, -1.18) * mm});
            skLineSegment(sketch, "E2991", {"start": v(-3.75, -1.18) * mm, "end": v(-3.77, -1.13) * mm});
            skLineSegment(sketch, "E2992", {"start": v(-3.77, -1.13) * mm, "end": v(-3.94, -1.22) * mm});
            skLineSegment(sketch, "E2993", {"start": v(-3.94, -1.22) * mm, "end": v(-4.18, -1.34) * mm});
            skLineSegment(sketch, "E2994", {"start": v(-4.18, -1.34) * mm, "end": v(-4.42, -1.45) * mm});
            skLineSegment(sketch, "E2995", {"start": v(-4.42, -1.45) * mm, "end": v(-4.66, -1.55) * mm});
            skLineSegment(sketch, "E2996", {"start": v(-4.66, -1.55) * mm, "end": v(-4.9, -1.66) * mm});
            skLineSegment(sketch, "E2997", {"start": v(-4.9, -1.66) * mm, "end": v(-5.14, -1.76) * mm});
            skLineSegment(sketch, "E2998", {"start": v(-5.14, -1.76) * mm, "end": v(-5.38, -1.85) * mm});
            skLineSegment(sketch, "E2999", {"start": v(-5.38, -1.85) * mm, "end": v(-5.62, -1.95) * mm});
            skLineSegment(sketch, "E3000", {"start": v(-5.62, -1.95) * mm, "end": v(-5.86, -2.03) * mm});
            skLineSegment(sketch, "E3001", {"start": v(-5.86, -2.03) * mm, "end": v(-6.1, -2.12) * mm});
            skLineSegment(sketch, "E3002", {"start": v(-6.1, -2.12) * mm, "end": v(-6.35, -2.2) * mm});
            skLineSegment(sketch, "E3003", {"start": v(-6.35, -2.2) * mm, "end": v(-6.59, -2.28) * mm});
            skLineSegment(sketch, "E3004", {"start": v(-6.59, -2.28) * mm, "end": v(-6.83, -2.35) * mm});
            skLineSegment(sketch, "E3005", {"start": v(-6.83, -2.35) * mm, "end": v(-7.07, -2.42) * mm});
            skLineSegment(sketch, "E3006", {"start": v(-7.07, -2.42) * mm, "end": v(-7.31, -2.48) * mm});
            skLineSegment(sketch, "E3007", {"start": v(-7.31, -2.48) * mm, "end": v(-7.56, -2.54) * mm});
            skLineSegment(sketch, "E3008", {"start": v(-7.56, -2.54) * mm, "end": v(-7.8, -2.6) * mm});
            skLineSegment(sketch, "E3009", {"start": v(-7.8, -2.6) * mm, "end": v(-8.04, -2.66) * mm});
            skLineSegment(sketch, "E3010", {"start": v(-8.04, -2.66) * mm, "end": v(-8.29, -2.7) * mm});
            skLineSegment(sketch, "E3011", {"start": v(-8.29, -2.7) * mm, "end": v(-8.53, -2.75) * mm});
            skLineSegment(sketch, "E3012", {"start": v(-8.53, -2.75) * mm, "end": v(-8.77, -2.8) * mm});
            skLineSegment(sketch, "E3013", {"start": v(-8.77, -2.8) * mm, "end": v(-9.02, -2.83) * mm});
            skLineSegment(sketch, "E3014", {"start": v(-9.02, -2.83) * mm, "end": v(-9.26, -2.86) * mm});
            skLineSegment(sketch, "E3015", {"start": v(-9.26, -2.86) * mm, "end": v(-9.5, -2.9) * mm});
            skLineSegment(sketch, "E3016", {"start": v(-9.5, -2.9) * mm, "end": v(-9.75, -2.92) * mm});
            skLineSegment(sketch, "E3017", {"start": v(-9.75, -2.92) * mm, "end": v(-10, -2.94) * mm});
            skLineSegment(sketch, "E3018", {"start": v(-10, -2.94) * mm, "end": v(-10.24, -2.96) * mm});
            skLineSegment(sketch, "E3019", {"start": v(-10.24, -2.96) * mm, "end": v(-10.49, -2.97) * mm});
            skLineSegment(sketch, "E3020", {"start": v(-10.49, -2.97) * mm, "end": v(-10.73, -2.98) * mm});
            skLineSegment(sketch, "E3021", {"start": v(-10.73, -2.98) * mm, "end": v(-10.98, -2.99) * mm});
            skLineSegment(sketch, "E3022", {"start": v(-10.98, -2.99) * mm, "end": v(-11.22, -3) * mm});
            skLineSegment(sketch, "E3023", {"start": v(-11.22, -3) * mm, "end": v(-11.47, -2.99) * mm});
            skLineSegment(sketch, "E3024", {"start": v(-11.47, -2.99) * mm, "end": v(-11.72, -2.98) * mm});
            skLineSegment(sketch, "E3025", {"start": v(-11.72, -2.98) * mm, "end": v(-11.97, -2.97) * mm});
            skLineSegment(sketch, "E3026", {"start": v(-11.97, -2.97) * mm, "end": v(-12.22, -2.96) * mm});
            skLineSegment(sketch, "E3027", {"start": v(-12.22, -2.96) * mm, "end": v(-12.47, -2.94) * mm});
            skLineSegment(sketch, "E3028", {"start": v(-12.47, -2.94) * mm, "end": v(-12.72, -2.92) * mm});
            skLineSegment(sketch, "E3029", {"start": v(-12.72, -2.92) * mm, "end": v(-12.97, -2.9) * mm});
            skLineSegment(sketch, "E3030", {"start": v(-12.97, -2.9) * mm, "end": v(-13.21, -2.86) * mm});
            skLineSegment(sketch, "E3031", {"start": v(-13.21, -2.86) * mm, "end": v(-13.46, -2.83) * mm});
            skLineSegment(sketch, "E3032", {"start": v(-13.46, -2.83) * mm, "end": v(-13.7, -2.79) * mm});
            skLineSegment(sketch, "E3033", {"start": v(-13.7, -2.79) * mm, "end": v(-13.96, -2.74) * mm});
            skLineSegment(sketch, "E3034", {"start": v(-13.96, -2.74) * mm, "end": v(-14.2, -2.7) * mm});
            skLineSegment(sketch, "E3035", {"start": v(-14.2, -2.7) * mm, "end": v(-14.45, -2.65) * mm});
            skLineSegment(sketch, "E3036", {"start": v(-14.45, -2.65) * mm, "end": v(-14.7, -2.6) * mm});
            skLineSegment(sketch, "E3037", {"start": v(-14.7, -2.6) * mm, "end": v(-14.94, -2.53) * mm});
            skLineSegment(sketch, "E3038", {"start": v(-14.94, -2.53) * mm, "end": v(-15.2, -2.47) * mm});
            skLineSegment(sketch, "E3039", {"start": v(-15.2, -2.47) * mm, "end": v(-15.44, -2.4) * mm});
            skLineSegment(sketch, "E3040", {"start": v(-15.44, -2.4) * mm, "end": v(-15.68, -2.33) * mm});
            skLineSegment(sketch, "E3041", {"start": v(-15.68, -2.33) * mm, "end": v(-15.93, -2.26) * mm});
            skLineSegment(sketch, "E3042", {"start": v(-15.93, -2.26) * mm, "end": v(-16.17, -2.18) * mm});
            skLineSegment(sketch, "E3043", {"start": v(-16.17, -2.18) * mm, "end": v(-16.42, -2.1) * mm});
            skLineSegment(sketch, "E3044", {"start": v(-16.42, -2.1) * mm, "end": v(-16.66, -2) * mm});
            skLineSegment(sketch, "E3045", {"start": v(-16.66, -2) * mm, "end": v(-16.9, -1.92) * mm});
            skLineSegment(sketch, "E3046", {"start": v(-16.9, -1.92) * mm, "end": v(-17.15, -1.82) * mm});
            skLineSegment(sketch, "E3047", {"start": v(-17.15, -1.82) * mm, "end": v(-17.4, -1.72) * mm});
            skLineSegment(sketch, "E3048", {"start": v(-17.4, -1.72) * mm, "end": v(-17.64, -1.62) * mm});
            skLineSegment(sketch, "E3049", {"start": v(-17.64, -1.62) * mm, "end": v(-17.88, -1.51) * mm});
            skLineSegment(sketch, "E3050", {"start": v(-17.88, -1.51) * mm, "end": v(-18.12, -1.4) * mm});
            skLineSegment(sketch, "E3051", {"start": v(-18.12, -1.4) * mm, "end": v(-18.37, -1.29) * mm});
            skLineSegment(sketch, "E3052", {"start": v(-18.37, -1.29) * mm, "end": v(-18.61, -1.17) * mm});
            skLineSegment(sketch, "E3053", {"start": v(-18.61, -1.17) * mm, "end": v(-18.76, -1.1) * mm});
            skLineSegment(sketch, "E3054", {"start": v(-18.76, -1.1) * mm, "end": v(-18.76, -1.13) * mm});
            skLineSegment(sketch, "E3055", {"start": v(-18.76, -1.13) * mm, "end": v(-18.65, -2.26) * mm});
            skLineSegment(sketch, "E3056", {"start": v(-18.65, -2.26) * mm, "end": v(-18.47, -3.38) * mm});
            skLineSegment(sketch, "E3057", {"start": v(-18.47, -3.38) * mm, "end": v(-18.23, -4.48) * mm});
            skLineSegment(sketch, "E3058", {"start": v(-18.23, -4.48) * mm, "end": v(-17.91, -5.57) * mm});
            skLineSegment(sketch, "E3059", {"start": v(-17.91, -5.57) * mm, "end": v(-17.53, -6.63) * mm});
            skLineSegment(sketch, "E3060", {"start": v(-17.53, -6.63) * mm, "end": v(-17.08, -7.67) * mm});
            skLineSegment(sketch, "E3061", {"start": v(-17.08, -7.67) * mm, "end": v(-16.56, -8.68) * mm});
            skLineSegment(sketch, "E3062", {"start": v(-16.56, -8.68) * mm, "end": v(-15.99, -9.66) * mm});
            skLineSegment(sketch, "E3063", {"start": v(-15.99, -9.66) * mm, "end": v(-15.35, -10.6) * mm});
            skLineSegment(sketch, "E3064", {"start": v(-15.35, -10.6) * mm, "end": v(-14.66, -11.49) * mm});
            skLineSegment(sketch, "E3065", {"start": v(-14.66, -11.49) * mm, "end": v(-13.9, -12.34) * mm});
            skLineSegment(sketch, "E3066", {"start": v(-13.9, -12.34) * mm, "end": v(-13.1, -13.14) * mm});
            skLineSegment(sketch, "E3067", {"start": v(-13.1, -13.14) * mm, "end": v(-12.26, -13.88) * mm});
            skLineSegment(sketch, "E3068", {"start": v(-12.26, -13.88) * mm, "end": v(-11.37, -14.58) * mm});
            skLineSegment(sketch, "E3069", {"start": v(-11.37, -14.58) * mm, "end": v(-10.43, -15.21) * mm});
            skLineSegment(sketch, "E3070", {"start": v(-10.43, -15.21) * mm, "end": v(-9.45, -15.8) * mm});
            skLineSegment(sketch, "E3071", {"start": v(-9.45, -15.8) * mm, "end": v(-8.45, -16.3) * mm});
            skLineSegment(sketch, "E3072", {"start": v(-8.45, -16.3) * mm, "end": v(-7.4, -16.75) * mm});
            skLineSegment(sketch, "E3073", {"start": v(-7.4, -16.75) * mm, "end": v(-6.34, -17.14) * mm});
            skLineSegment(sketch, "E3074", {"start": v(-6.34, -17.14) * mm, "end": v(-5.26, -17.45) * mm});
            skLineSegment(sketch, "E3075", {"start": v(-5.26, -17.45) * mm, "end": v(-4.15, -17.7) * mm});
            skLineSegment(sketch, "E3076", {"start": v(-4.15, -17.7) * mm, "end": v(-3.03, -17.88) * mm});
            skLineSegment(sketch, "E3077", {"start": v(-3.03, -17.88) * mm, "end": v(-2.01, -17.97) * mm});
            skLineSegment(sketch, "E3078", {"start": v(-2.01, -17.97) * mm, "end": v(-2.07, -17.84) * mm});
            skLineSegment(sketch, "E3079", {"start": v(0.36, -17.98) * mm, "end": v(1.48, -17.88) * mm});
            skLineSegment(sketch, "E3080", {"start": v(1.48, -17.88) * mm, "end": v(2.6, -17.7) * mm});
            skLineSegment(sketch, "E3081", {"start": v(2.6, -17.7) * mm, "end": v(3.7, -17.45) * mm});
            skLineSegment(sketch, "E3082", {"start": v(3.7, -17.45) * mm, "end": v(4.8, -17.14) * mm});
            skLineSegment(sketch, "E3083", {"start": v(4.8, -17.14) * mm, "end": v(5.86, -16.75) * mm});
            skLineSegment(sketch, "E3084", {"start": v(5.86, -16.75) * mm, "end": v(6.9, -16.3) * mm});
            skLineSegment(sketch, "E3085", {"start": v(6.9, -16.3) * mm, "end": v(7.9, -15.8) * mm});
            skLineSegment(sketch, "E3086", {"start": v(7.9, -15.8) * mm, "end": v(8.88, -15.21) * mm});
            skLineSegment(sketch, "E3087", {"start": v(8.88, -15.21) * mm, "end": v(9.82, -14.58) * mm});
            skLineSegment(sketch, "E3088", {"start": v(9.82, -14.58) * mm, "end": v(10.71, -13.88) * mm});
            skLineSegment(sketch, "E3089", {"start": v(10.71, -13.88) * mm, "end": v(11.56, -13.14) * mm});
            skLineSegment(sketch, "E3090", {"start": v(11.56, -13.14) * mm, "end": v(12.36, -12.34) * mm});
            skLineSegment(sketch, "E3091", {"start": v(12.36, -12.34) * mm, "end": v(13.1, -11.49) * mm});
            skLineSegment(sketch, "E3092", {"start": v(13.1, -11.49) * mm, "end": v(13.8, -10.6) * mm});
            skLineSegment(sketch, "E3093", {"start": v(13.8, -10.6) * mm, "end": v(14.44, -9.66) * mm});
            skLineSegment(sketch, "E3094", {"start": v(14.44, -9.66) * mm, "end": v(15.02, -8.68) * mm});
            skLineSegment(sketch, "E3095", {"start": v(15.02, -8.68) * mm, "end": v(15.53, -7.67) * mm});
            skLineSegment(sketch, "E3096", {"start": v(15.53, -7.67) * mm, "end": v(15.98, -6.63) * mm});
            skLineSegment(sketch, "E3097", {"start": v(15.98, -6.63) * mm, "end": v(16.36, -5.57) * mm});
            skLineSegment(sketch, "E3098", {"start": v(16.36, -5.57) * mm, "end": v(16.68, -4.48) * mm});
            skLineSegment(sketch, "E3099", {"start": v(16.68, -4.48) * mm, "end": v(16.93, -3.38) * mm});
            skLineSegment(sketch, "E3100", {"start": v(16.93, -3.38) * mm, "end": v(17.1, -2.26) * mm});
            skLineSegment(sketch, "E3101", {"start": v(17.1, -2.26) * mm, "end": v(17.2, -1.24) * mm});
            skLineSegment(sketch, "E3102", {"start": v(17.2, -1.24) * mm, "end": v(17.06, -1.3) * mm});
            skLineSegment(sketch, "E3103", {"start": v(17.06, -1.3) * mm, "end": v(16.82, -1.4) * mm});
            skLineSegment(sketch, "E3104", {"start": v(16.82, -1.4) * mm, "end": v(16.58, -1.5) * mm});
            skLineSegment(sketch, "E3105", {"start": v(16.58, -1.5) * mm, "end": v(16.33, -1.6) * mm});
            skLineSegment(sketch, "E3106", {"start": v(16.33, -1.6) * mm, "end": v(16.09, -1.69) * mm});
            skLineSegment(sketch, "E3107", {"start": v(16.09, -1.69) * mm, "end": v(15.85, -1.77) * mm});
            skLineSegment(sketch, "E3108", {"start": v(15.85, -1.77) * mm, "end": v(15.6, -1.86) * mm});
            skLineSegment(sketch, "E3109", {"start": v(15.6, -1.86) * mm, "end": v(15.36, -1.94) * mm});
            skLineSegment(sketch, "E3110", {"start": v(15.36, -1.94) * mm, "end": v(15.11, -2.02) * mm});
            skLineSegment(sketch, "E3111", {"start": v(15.11, -2.02) * mm, "end": v(14.87, -2.1) * mm});
            skLineSegment(sketch, "E3112", {"start": v(14.87, -2.1) * mm, "end": v(14.62, -2.16) * mm});
            skLineSegment(sketch, "E3113", {"start": v(14.62, -2.16) * mm, "end": v(14.38, -2.23) * mm});
            skLineSegment(sketch, "E3114", {"start": v(14.38, -2.23) * mm, "end": v(14.13, -2.3) * mm});
            skLineSegment(sketch, "E3115", {"start": v(14.13, -2.3) * mm, "end": v(13.89, -2.36) * mm});
            skLineSegment(sketch, "E3116", {"start": v(13.89, -2.36) * mm, "end": v(13.64, -2.42) * mm});
            skLineSegment(sketch, "E3117", {"start": v(13.64, -2.42) * mm, "end": v(13.4, -2.47) * mm});
            skLineSegment(sketch, "E3118", {"start": v(13.4, -2.47) * mm, "end": v(13.15, -2.52) * mm});
            skLineSegment(sketch, "E3119", {"start": v(13.15, -2.52) * mm, "end": v(12.9, -2.57) * mm});
            skLineSegment(sketch, "E3120", {"start": v(12.9, -2.57) * mm, "end": v(12.66, -2.61) * mm});
            skLineSegment(sketch, "E3121", {"start": v(12.66, -2.61) * mm, "end": v(12.4, -2.65) * mm});
            skLineSegment(sketch, "E3122", {"start": v(12.4, -2.65) * mm, "end": v(12.16, -2.69) * mm});
            skLineSegment(sketch, "E3123", {"start": v(12.16, -2.69) * mm, "end": v(11.91, -2.72) * mm});
            skLineSegment(sketch, "E3124", {"start": v(11.91, -2.72) * mm, "end": v(11.67, -2.75) * mm});
            skLineSegment(sketch, "E3125", {"start": v(11.67, -2.75) * mm, "end": v(11.42, -2.78) * mm});
            skLineSegment(sketch, "E3126", {"start": v(11.42, -2.78) * mm, "end": v(11.17, -2.8) * mm});
            skLineSegment(sketch, "E3127", {"start": v(11.17, -2.8) * mm, "end": v(10.92, -2.82) * mm});
            skLineSegment(sketch, "E3128", {"start": v(10.92, -2.82) * mm, "end": v(10.67, -2.84) * mm});
            skLineSegment(sketch, "E3129", {"start": v(10.67, -2.84) * mm, "end": v(10.42, -2.85) * mm});
            skLineSegment(sketch, "E3130", {"start": v(10.42, -2.85) * mm, "end": v(10.18, -2.86) * mm});
            skLineSegment(sketch, "E3131", {"start": v(10.18, -2.86) * mm, "end": v(9.93, -2.86) * mm});
            skLineSegment(sketch, "E3132", {"start": v(9.93, -2.86) * mm, "end": v(9.68, -2.86) * mm});
            skLineSegment(sketch, "E3133", {"start": v(9.68, -2.86) * mm, "end": v(9.43, -2.86) * mm});
            skLineSegment(sketch, "E3134", {"start": v(9.43, -2.86) * mm, "end": v(9.19, -2.86) * mm});
            skLineSegment(sketch, "E3135", {"start": v(9.19, -2.86) * mm, "end": v(8.94, -2.85) * mm});
            skLineSegment(sketch, "E3136", {"start": v(8.94, -2.85) * mm, "end": v(8.7, -2.84) * mm});
            skLineSegment(sketch, "E3137", {"start": v(8.7, -2.84) * mm, "end": v(8.45, -2.82) * mm});
            skLineSegment(sketch, "E3138", {"start": v(8.45, -2.82) * mm, "end": v(8.2, -2.8) * mm});
            skLineSegment(sketch, "E3139", {"start": v(8.2, -2.8) * mm, "end": v(7.96, -2.78) * mm});
            skLineSegment(sketch, "E3140", {"start": v(7.96, -2.78) * mm, "end": v(7.71, -2.75) * mm});
            skLineSegment(sketch, "E3141", {"start": v(7.71, -2.75) * mm, "end": v(7.47, -2.73) * mm});
            skLineSegment(sketch, "E3142", {"start": v(7.47, -2.73) * mm, "end": v(7.23, -2.7) * mm});
            skLineSegment(sketch, "E3143", {"start": v(7.23, -2.7) * mm, "end": v(6.98, -2.66) * mm});
            skLineSegment(sketch, "E3144", {"start": v(6.98, -2.66) * mm, "end": v(6.74, -2.62) * mm});
            skLineSegment(sketch, "E3145", {"start": v(6.74, -2.62) * mm, "end": v(6.5, -2.58) * mm});
            skLineSegment(sketch, "E3146", {"start": v(6.5, -2.58) * mm, "end": v(6.25, -2.53) * mm});
            skLineSegment(sketch, "E3147", {"start": v(6.25, -2.53) * mm, "end": v(6, -2.48) * mm});
            skLineSegment(sketch, "E3148", {"start": v(6, -2.48) * mm, "end": v(5.77, -2.43) * mm});
            skLineSegment(sketch, "E3149", {"start": v(5.77, -2.43) * mm, "end": v(5.52, -2.37) * mm});
            skLineSegment(sketch, "E3150", {"start": v(5.52, -2.37) * mm, "end": v(5.28, -2.31) * mm});
            skLineSegment(sketch, "E3151", {"start": v(5.28, -2.31) * mm, "end": v(5.04, -2.25) * mm});
            skLineSegment(sketch, "E3152", {"start": v(5.04, -2.25) * mm, "end": v(4.8, -2.18) * mm});
            skLineSegment(sketch, "E3153", {"start": v(4.8, -2.18) * mm, "end": v(4.56, -2.11) * mm});
            skLineSegment(sketch, "E3154", {"start": v(4.56, -2.11) * mm, "end": v(4.32, -2.04) * mm});
            skLineSegment(sketch, "E3155", {"start": v(4.32, -2.04) * mm, "end": v(4.07, -1.97) * mm});
            skLineSegment(sketch, "E3156", {"start": v(4.07, -1.97) * mm, "end": v(3.83, -1.89) * mm});
            skLineSegment(sketch, "E3157", {"start": v(3.83, -1.89) * mm, "end": v(3.6, -1.8) * mm});
            skLineSegment(sketch, "E3158", {"start": v(3.6, -1.8) * mm, "end": v(3.35, -1.72) * mm});
            skLineSegment(sketch, "E3159", {"start": v(3.35, -1.72) * mm, "end": v(3.11, -1.63) * mm});
            skLineSegment(sketch, "E3160", {"start": v(3.11, -1.63) * mm, "end": v(2.87, -1.54) * mm});
            skLineSegment(sketch, "E3161", {"start": v(2.87, -1.54) * mm, "end": v(2.63, -1.44) * mm});
            skLineSegment(sketch, "E3162", {"start": v(2.63, -1.44) * mm, "end": v(2.4, -1.34) * mm});
            skLineSegment(sketch, "E3163", {"start": v(2.4, -1.34) * mm, "end": v(2.17, -1.25) * mm});
            skLineSegment(sketch, "E3164", {"start": v(2.17, -1.25) * mm, "end": v(2.12, -1.36) * mm});
            skLineSegment(sketch, "E3165", {"start": v(2.12, -1.36) * mm, "end": v(2.03, -1.54) * mm});
            skLineSegment(sketch, "E3166", {"start": v(2.03, -1.54) * mm, "end": v(1.93, -1.72) * mm});
            skLineSegment(sketch, "E3167", {"start": v(1.93, -1.72) * mm, "end": v(1.82, -1.88) * mm});
            skLineSegment(sketch, "E3168", {"start": v(1.82, -1.88) * mm, "end": v(1.7, -2.04) * mm});
            skLineSegment(sketch, "E3169", {"start": v(1.7, -2.04) * mm, "end": v(1.56, -2.2) * mm});
            skLineSegment(sketch, "E3170", {"start": v(1.56, -2.2) * mm, "end": v(1.42, -2.33) * mm});
            skLineSegment(sketch, "E3171", {"start": v(1.42, -2.33) * mm, "end": v(1.27, -2.47) * mm});
            skLineSegment(sketch, "E3172", {"start": v(1.27, -2.47) * mm, "end": v(1.1, -2.6) * mm});
            skLineSegment(sketch, "E3173", {"start": v(1.1, -2.6) * mm, "end": v(0.94, -2.7) * mm});
            skLineSegment(sketch, "E3174", {"start": v(0.94, -2.7) * mm, "end": v(0.77, -2.8) * mm});
            skLineSegment(sketch, "E3175", {"start": v(0.77, -2.8) * mm, "end": v(0.59, -2.9) * mm});
            skLineSegment(sketch, "E3176", {"start": v(0.59, -2.9) * mm, "end": v(0.4, -2.98) * mm});
            skLineSegment(sketch, "E3177", {"start": v(0.4, -2.98) * mm, "end": v(0.36, -3) * mm});
            skLineSegment(sketch, "E3178", {"start": v(0.36, -3) * mm, "end": v(0.45, -3.17) * mm});
            skLineSegment(sketch, "E3179", {"start": v(0.45, -3.17) * mm, "end": v(0.56, -3.4) * mm});
            skLineSegment(sketch, "E3180", {"start": v(0.56, -3.4) * mm, "end": v(0.67, -3.65) * mm});
            skLineSegment(sketch, "E3181", {"start": v(0.67, -3.65) * mm, "end": v(0.78, -3.89) * mm});
            skLineSegment(sketch, "E3182", {"start": v(0.78, -3.89) * mm, "end": v(0.88, -4.13) * mm});
            skLineSegment(sketch, "E3183", {"start": v(0.88, -4.13) * mm, "end": v(0.98, -4.37) * mm});
            skLineSegment(sketch, "E3184", {"start": v(0.98, -4.37) * mm, "end": v(1.08, -4.6) * mm});
            skLineSegment(sketch, "E3185", {"start": v(1.08, -4.6) * mm, "end": v(1.17, -4.85) * mm});
            skLineSegment(sketch, "E3186", {"start": v(1.17, -4.85) * mm, "end": v(1.26, -5.09) * mm});
            skLineSegment(sketch, "E3187", {"start": v(1.26, -5.09) * mm, "end": v(1.34, -5.33) * mm});
            skLineSegment(sketch, "E3188", {"start": v(1.34, -5.33) * mm, "end": v(1.42, -5.57) * mm});
            skLineSegment(sketch, "E3189", {"start": v(1.42, -5.57) * mm, "end": v(1.5, -5.81) * mm});
            skLineSegment(sketch, "E3190", {"start": v(1.5, -5.81) * mm, "end": v(1.57, -6.06) * mm});
            skLineSegment(sketch, "E3191", {"start": v(1.57, -6.06) * mm, "end": v(1.64, -6.3) * mm});
            skLineSegment(sketch, "E3192", {"start": v(1.64, -6.3) * mm, "end": v(1.7, -6.54) * mm});
            skLineSegment(sketch, "E3193", {"start": v(1.7, -6.54) * mm, "end": v(1.77, -6.78) * mm});
            skLineSegment(sketch, "E3194", {"start": v(1.77, -6.78) * mm, "end": v(1.83, -7.03) * mm});
            skLineSegment(sketch, "E3195", {"start": v(1.83, -7.03) * mm, "end": v(1.88, -7.27) * mm});
            skLineSegment(sketch, "E3196", {"start": v(1.88, -7.27) * mm, "end": v(1.93, -7.51) * mm});
            skLineSegment(sketch, "E3197", {"start": v(1.93, -7.51) * mm, "end": v(1.98, -7.76) * mm});
            skLineSegment(sketch, "E3198", {"start": v(1.98, -7.76) * mm, "end": v(2.02, -8) * mm});
            skLineSegment(sketch, "E3199", {"start": v(2.02, -8) * mm, "end": v(2.06, -8.24) * mm});
            skLineSegment(sketch, "E3200", {"start": v(2.06, -8.24) * mm, "end": v(2.09, -8.49) * mm});
            skLineSegment(sketch, "E3201", {"start": v(2.09, -8.49) * mm, "end": v(2.12, -8.73) * mm});
            skLineSegment(sketch, "E3202", {"start": v(2.12, -8.73) * mm, "end": v(2.14, -8.98) * mm});
            skLineSegment(sketch, "E3203", {"start": v(2.14, -8.98) * mm, "end": v(2.17, -9.22) * mm});
            skLineSegment(sketch, "E3204", {"start": v(2.17, -9.22) * mm, "end": v(2.18, -9.47) * mm});
            skLineSegment(sketch, "E3205", {"start": v(2.18, -9.47) * mm, "end": v(2.2, -9.71) * mm});
            skLineSegment(sketch, "E3206", {"start": v(2.2, -9.71) * mm, "end": v(2.2, -9.96) * mm});
            skLineSegment(sketch, "E3207", {"start": v(2.2, -9.96) * mm, "end": v(2.21, -10.2) * mm});
            skLineSegment(sketch, "E3208", {"start": v(2.21, -10.2) * mm, "end": v(2.22, -10.45) * mm});
            skLineSegment(sketch, "E3209", {"start": v(2.22, -10.45) * mm, "end": v(2.21, -10.7) * mm});
            skLineSegment(sketch, "E3210", {"start": v(2.21, -10.7) * mm, "end": v(2.2, -10.95) * mm});
            skLineSegment(sketch, "E3211", {"start": v(2.2, -10.95) * mm, "end": v(2.2, -11.2) * mm});
            skLineSegment(sketch, "E3212", {"start": v(2.2, -11.2) * mm, "end": v(2.18, -11.45) * mm});
            skLineSegment(sketch, "E3213", {"start": v(2.18, -11.45) * mm, "end": v(2.17, -11.7) * mm});
            skLineSegment(sketch, "E3214", {"start": v(2.17, -11.7) * mm, "end": v(2.14, -11.94) * mm});
            skLineSegment(sketch, "E3215", {"start": v(2.14, -11.94) * mm, "end": v(2.12, -12.2) * mm});
            skLineSegment(sketch, "E3216", {"start": v(2.12, -12.2) * mm, "end": v(2.09, -12.44) * mm});
            skLineSegment(sketch, "E3217", {"start": v(2.09, -12.44) * mm, "end": v(2.05, -12.69) * mm});
            skLineSegment(sketch, "E3218", {"start": v(2.05, -12.69) * mm, "end": v(2.01, -12.94) * mm});
            skLineSegment(sketch, "E3219", {"start": v(2.01, -12.94) * mm, "end": v(1.97, -13.18) * mm});
            skLineSegment(sketch, "E3220", {"start": v(1.97, -13.18) * mm, "end": v(1.92, -13.43) * mm});
            skLineSegment(sketch, "E3221", {"start": v(1.92, -13.43) * mm, "end": v(1.87, -13.68) * mm});
            skLineSegment(sketch, "E3222", {"start": v(1.87, -13.68) * mm, "end": v(1.82, -13.92) * mm});
            skLineSegment(sketch, "E3223", {"start": v(1.82, -13.92) * mm, "end": v(1.76, -14.17) * mm});
            skLineSegment(sketch, "E3224", {"start": v(1.76, -14.17) * mm, "end": v(1.7, -14.42) * mm});
            skLineSegment(sketch, "E3225", {"start": v(1.7, -14.42) * mm, "end": v(1.63, -14.66) * mm});
            skLineSegment(sketch, "E3226", {"start": v(1.63, -14.66) * mm, "end": v(1.56, -14.9) * mm});
            skLineSegment(sketch, "E3227", {"start": v(1.56, -14.9) * mm, "end": v(1.48, -15.15) * mm});
            skLineSegment(sketch, "E3228", {"start": v(1.48, -15.15) * mm, "end": v(1.4, -15.4) * mm});
            skLineSegment(sketch, "E3229", {"start": v(1.4, -15.4) * mm, "end": v(1.32, -15.64) * mm});
            skLineSegment(sketch, "E3230", {"start": v(1.32, -15.64) * mm, "end": v(1.23, -15.89) * mm});
            skLineSegment(sketch, "E3231", {"start": v(1.23, -15.89) * mm, "end": v(1.14, -16.13) * mm});
            skLineSegment(sketch, "E3232", {"start": v(1.14, -16.13) * mm, "end": v(1.05, -16.38) * mm});
            skLineSegment(sketch, "E3233", {"start": v(1.05, -16.38) * mm, "end": v(0.95, -16.62) * mm});
            skLineSegment(sketch, "E3234", {"start": v(0.95, -16.62) * mm, "end": v(0.85, -16.86) * mm});
            skLineSegment(sketch, "E3235", {"start": v(0.85, -16.86) * mm, "end": v(0.74, -17.1) * mm});
            skLineSegment(sketch, "E3236", {"start": v(0.74, -17.1) * mm, "end": v(0.63, -17.35) * mm});
            skLineSegment(sketch, "E3237", {"start": v(0.63, -17.35) * mm, "end": v(0.51, -17.6) * mm});
            skLineSegment(sketch, "E3238", {"start": v(0.51, -17.6) * mm, "end": v(0.4, -17.84) * mm});
            skLineSegment(sketch, "E3239", {"start": v(0.4, -17.84) * mm, "end": v(0.32, -17.99) * mm});
            skLineSegment(sketch, "E3240", {"start": v(0.32, -17.99) * mm, "end": v(0.36, -17.98) * mm});
            skLineSegment(sketch, "E3241", {"start": v(-0.49, -14.4) * mm, "end": v(-0.42, -14.27) * mm});
            skLineSegment(sketch, "E3242", {"start": v(-0.42, -14.27) * mm, "end": v(-0.35, -14.14) * mm});
            skLineSegment(sketch, "E3243", {"start": v(-0.35, -14.14) * mm, "end": v(-0.3, -14.01) * mm});
            skLineSegment(sketch, "E3244", {"start": v(-0.3, -14.01) * mm, "end": v(-0.23, -13.88) * mm});
            skLineSegment(sketch, "E3245", {"start": v(-0.23, -13.88) * mm, "end": v(-0.17, -13.75) * mm});
            skLineSegment(sketch, "E3246", {"start": v(-0.17, -13.75) * mm, "end": v(-0.11, -13.62) * mm});
            skLineSegment(sketch, "E3247", {"start": v(-0.11, -13.62) * mm, "end": v(-0.06, -13.5) * mm});
            skLineSegment(sketch, "E3248", {"start": v(-0.06, -13.5) * mm, "end": v(0, -13.37) * mm});
            skLineSegment(sketch, "E3249", {"start": v(0, -13.37) * mm, "end": v(0.04, -13.24) * mm});
            skLineSegment(sketch, "E3250", {"start": v(0.04, -13.24) * mm, "end": v(0.09, -13.1) * mm});
            skLineSegment(sketch, "E3251", {"start": v(0.09, -13.1) * mm, "end": v(0.13, -12.98) * mm});
            skLineSegment(sketch, "E3252", {"start": v(0.13, -12.98) * mm, "end": v(0.18, -12.85) * mm});
            skLineSegment(sketch, "E3253", {"start": v(0.18, -12.85) * mm, "end": v(0.22, -12.72) * mm});
            skLineSegment(sketch, "E3254", {"start": v(0.22, -12.72) * mm, "end": v(0.25, -12.59) * mm});
            skLineSegment(sketch, "E3255", {"start": v(0.25, -12.59) * mm, "end": v(0.3, -12.46) * mm});
            skLineSegment(sketch, "E3256", {"start": v(0.3, -12.46) * mm, "end": v(0.32, -12.33) * mm});
            skLineSegment(sketch, "E3257", {"start": v(0.32, -12.33) * mm, "end": v(0.36, -12.2) * mm});
            skLineSegment(sketch, "E3258", {"start": v(0.36, -12.2) * mm, "end": v(0.38, -12.07) * mm});
            skLineSegment(sketch, "E3259", {"start": v(0.38, -12.07) * mm, "end": v(0.41, -11.93) * mm});
            skLineSegment(sketch, "E3260", {"start": v(0.41, -11.93) * mm, "end": v(0.43, -11.8) * mm});
            skLineSegment(sketch, "E3261", {"start": v(0.43, -11.8) * mm, "end": v(0.46, -11.67) * mm});
            skLineSegment(sketch, "E3262", {"start": v(0.46, -11.67) * mm, "end": v(0.48, -11.54) * mm});
            skLineSegment(sketch, "E3263", {"start": v(0.48, -11.54) * mm, "end": v(0.5, -11.41) * mm});
            skLineSegment(sketch, "E3264", {"start": v(0.5, -11.41) * mm, "end": v(0.5, -11.28) * mm});
            skLineSegment(sketch, "E3265", {"start": v(0.5, -11.28) * mm, "end": v(0.52, -11.15) * mm});
            skLineSegment(sketch, "E3266", {"start": v(0.52, -11.15) * mm, "end": v(0.53, -11.02) * mm});
            skLineSegment(sketch, "E3267", {"start": v(0.53, -11.02) * mm, "end": v(0.54, -10.89) * mm});
            skLineSegment(sketch, "E3268", {"start": v(0.54, -10.89) * mm, "end": v(0.55, -10.76) * mm});
            skLineSegment(sketch, "E3269", {"start": v(0.55, -10.76) * mm, "end": v(0.55, -10.63) * mm});
            skLineSegment(sketch, "E3270", {"start": v(0.55, -10.63) * mm, "end": v(0.55, -10.5) * mm});
            skLineSegment(sketch, "E3271", {"start": v(0.55, -10.5) * mm, "end": v(0.55, -10.37) * mm});
            skLineSegment(sketch, "E3272", {"start": v(0.55, -10.37) * mm, "end": v(0.55, -10.24) * mm});
            skLineSegment(sketch, "E3273", {"start": v(0.55, -10.24) * mm, "end": v(0.54, -10.1) * mm});
            skLineSegment(sketch, "E3274", {"start": v(0.54, -10.1) * mm, "end": v(0.53, -9.98) * mm});
            skLineSegment(sketch, "E3275", {"start": v(0.53, -9.98) * mm, "end": v(0.52, -9.85) * mm});
            skLineSegment(sketch, "E3276", {"start": v(0.52, -9.85) * mm, "end": v(0.51, -9.72) * mm});
            skLineSegment(sketch, "E3277", {"start": v(0.51, -9.72) * mm, "end": v(0.5, -9.6) * mm});
            skLineSegment(sketch, "E3278", {"start": v(0.5, -9.6) * mm, "end": v(0.48, -9.46) * mm});
            skLineSegment(sketch, "E3279", {"start": v(0.48, -9.46) * mm, "end": v(0.46, -9.33) * mm});
            skLineSegment(sketch, "E3280", {"start": v(0.46, -9.33) * mm, "end": v(0.44, -9.2) * mm});
            skLineSegment(sketch, "E3281", {"start": v(0.44, -9.2) * mm, "end": v(0.41, -9.08) * mm});
            skLineSegment(sketch, "E3282", {"start": v(0.41, -9.08) * mm, "end": v(0.39, -8.95) * mm});
            skLineSegment(sketch, "E3283", {"start": v(0.39, -8.95) * mm, "end": v(0.36, -8.82) * mm});
            skLineSegment(sketch, "E3284", {"start": v(0.36, -8.82) * mm, "end": v(0.33, -8.7) * mm});
            skLineSegment(sketch, "E3285", {"start": v(0.33, -8.7) * mm, "end": v(0.3, -8.56) * mm});
            skLineSegment(sketch, "E3286", {"start": v(0.3, -8.56) * mm, "end": v(0.26, -8.43) * mm});
            skLineSegment(sketch, "E3287", {"start": v(0.26, -8.43) * mm, "end": v(0.23, -8.3) * mm});
            skLineSegment(sketch, "E3288", {"start": v(0.23, -8.3) * mm, "end": v(0.19, -8.18) * mm});
            skLineSegment(sketch, "E3289", {"start": v(0.19, -8.18) * mm, "end": v(0.14, -8.05) * mm});
            skLineSegment(sketch, "E3290", {"start": v(0.14, -8.05) * mm, "end": v(0.1, -7.92) * mm});
            skLineSegment(sketch, "E3291", {"start": v(0.1, -7.92) * mm, "end": v(0.06, -7.8) * mm});
            skLineSegment(sketch, "E3292", {"start": v(0.06, -7.8) * mm, "end": v(0, -7.67) * mm});
            skLineSegment(sketch, "E3293", {"start": v(0, -7.67) * mm, "end": v(-0.04, -7.54) * mm});
            skLineSegment(sketch, "E3294", {"start": v(-0.04, -7.54) * mm, "end": v(-0.1, -7.4) * mm});
            skLineSegment(sketch, "E3295", {"start": v(-0.1, -7.4) * mm, "end": v(-0.15, -7.28) * mm});
            skLineSegment(sketch, "E3296", {"start": v(-0.15, -7.28) * mm, "end": v(-0.2, -7.15) * mm});
            skLineSegment(sketch, "E3297", {"start": v(-0.2, -7.15) * mm, "end": v(-0.27, -7.03) * mm});
            skLineSegment(sketch, "E3298", {"start": v(-0.27, -7.03) * mm, "end": v(-0.33, -6.9) * mm});
            skLineSegment(sketch, "E3299", {"start": v(-0.33, -6.9) * mm, "end": v(-0.4, -6.77) * mm});
            skLineSegment(sketch, "E3300", {"start": v(-0.4, -6.77) * mm, "end": v(-0.46, -6.64) * mm});
            skLineSegment(sketch, "E3301", {"start": v(-0.46, -6.64) * mm, "end": v(-0.48, -6.61) * mm});
            skLineSegment(sketch, "E3302", {"start": v(-0.48, -6.61) * mm, "end": v(-1.17, -6.61) * mm});
            skLineSegment(sketch, "E3303", {"start": v(-1.17, -6.61) * mm, "end": v(-1.17, -6.62) * mm});
            skLineSegment(sketch, "E3304", {"start": v(-1.17, -6.62) * mm, "end": v(-1.23, -6.75) * mm});
            skLineSegment(sketch, "E3305", {"start": v(-1.23, -6.75) * mm, "end": v(-1.28, -6.88) * mm});
            skLineSegment(sketch, "E3306", {"start": v(-1.28, -6.88) * mm, "end": v(-1.34, -7) * mm});
            skLineSegment(sketch, "E3307", {"start": v(-1.34, -7) * mm, "end": v(-1.39, -7.13) * mm});
            skLineSegment(sketch, "E3308", {"start": v(-1.39, -7.13) * mm, "end": v(-1.44, -7.26) * mm});
            skLineSegment(sketch, "E3309", {"start": v(-1.44, -7.26) * mm, "end": v(-1.48, -7.4) * mm});
            skLineSegment(sketch, "E3310", {"start": v(-1.48, -7.4) * mm, "end": v(-1.53, -7.52) * mm});
            skLineSegment(sketch, "E3311", {"start": v(-1.53, -7.52) * mm, "end": v(-1.57, -7.65) * mm});
            skLineSegment(sketch, "E3312", {"start": v(-1.57, -7.65) * mm, "end": v(-1.61, -7.78) * mm});
            skLineSegment(sketch, "E3313", {"start": v(-1.61, -7.78) * mm, "end": v(-1.65, -7.9) * mm});
            skLineSegment(sketch, "E3314", {"start": v(-1.65, -7.9) * mm, "end": v(-1.7, -8.03) * mm});
            skLineSegment(sketch, "E3315", {"start": v(-1.7, -8.03) * mm, "end": v(-1.73, -8.16) * mm});
            skLineSegment(sketch, "E3316", {"start": v(-1.73, -8.16) * mm, "end": v(-1.76, -8.3) * mm});
            skLineSegment(sketch, "E3317", {"start": v(-1.76, -8.3) * mm, "end": v(-1.8, -8.42) * mm});
            skLineSegment(sketch, "E3318", {"start": v(-1.8, -8.42) * mm, "end": v(-1.82, -8.55) * mm});
            skLineSegment(sketch, "E3319", {"start": v(-1.82, -8.55) * mm, "end": v(-1.85, -8.68) * mm});
            skLineSegment(sketch, "E3320", {"start": v(-1.85, -8.68) * mm, "end": v(-1.88, -8.8) * mm});
            skLineSegment(sketch, "E3321", {"start": v(-1.88, -8.8) * mm, "end": v(-1.9, -8.94) * mm});
            skLineSegment(sketch, "E3322", {"start": v(-1.9, -8.94) * mm, "end": v(-1.93, -9.07) * mm});
            skLineSegment(sketch, "E3323", {"start": v(-1.93, -9.07) * mm, "end": v(-1.95, -9.2) * mm});
            skLineSegment(sketch, "E3324", {"start": v(-1.95, -9.2) * mm, "end": v(-1.96, -9.33) * mm});
            skLineSegment(sketch, "E3325", {"start": v(-1.96, -9.33) * mm, "end": v(-1.98, -9.45) * mm});
            skLineSegment(sketch, "E3326", {"start": v(-1.98, -9.45) * mm, "end": v(-2, -9.58) * mm});
            skLineSegment(sketch, "E3327", {"start": v(-2, -9.58) * mm, "end": v(-2, -9.71) * mm});
            skLineSegment(sketch, "E3328", {"start": v(-2, -9.71) * mm, "end": v(-2.02, -9.84) * mm});
            skLineSegment(sketch, "E3329", {"start": v(-2.02, -9.84) * mm, "end": v(-2.03, -9.97) * mm});
            skLineSegment(sketch, "E3330", {"start": v(-2.03, -9.97) * mm, "end": v(-2.03, -10.1) * mm});
            skLineSegment(sketch, "E3331", {"start": v(-2.03, -10.1) * mm, "end": v(-2.04, -10.23) * mm});
            skLineSegment(sketch, "E3332", {"start": v(-2.04, -10.23) * mm, "end": v(-2.04, -10.36) * mm});
            skLineSegment(sketch, "E3333", {"start": v(-2.04, -10.36) * mm, "end": v(-2.04, -10.5) * mm});
            skLineSegment(sketch, "E3334", {"start": v(-2.04, -10.5) * mm, "end": v(-2.04, -10.63) * mm});
            skLineSegment(sketch, "E3335", {"start": v(-2.04, -10.63) * mm, "end": v(-2.04, -10.76) * mm});
            skLineSegment(sketch, "E3336", {"start": v(-2.04, -10.76) * mm, "end": v(-2.03, -10.9) * mm});
            skLineSegment(sketch, "E3337", {"start": v(-2.03, -10.9) * mm, "end": v(-2.03, -11.02) * mm});
            skLineSegment(sketch, "E3338", {"start": v(-2.03, -11.02) * mm, "end": v(-2.02, -11.16) * mm});
            skLineSegment(sketch, "E3339", {"start": v(-2.02, -11.16) * mm, "end": v(-2, -11.29) * mm});
            skLineSegment(sketch, "E3340", {"start": v(-2, -11.29) * mm, "end": v(-2, -11.42) * mm});
            skLineSegment(sketch, "E3341", {"start": v(-2, -11.42) * mm, "end": v(-1.98, -11.55) * mm});
            skLineSegment(sketch, "E3342", {"start": v(-1.98, -11.55) * mm, "end": v(-1.96, -11.68) * mm});
            skLineSegment(sketch, "E3343", {"start": v(-1.96, -11.68) * mm, "end": v(-1.94, -11.81) * mm});
            skLineSegment(sketch, "E3344", {"start": v(-1.94, -11.81) * mm, "end": v(-1.92, -11.94) * mm});
            skLineSegment(sketch, "E3345", {"start": v(-1.92, -11.94) * mm, "end": v(-1.9, -12.08) * mm});
            skLineSegment(sketch, "E3346", {"start": v(-1.9, -12.08) * mm, "end": v(-1.87, -12.2) * mm});
            skLineSegment(sketch, "E3347", {"start": v(-1.87, -12.2) * mm, "end": v(-1.85, -12.34) * mm});
            skLineSegment(sketch, "E3348", {"start": v(-1.85, -12.34) * mm, "end": v(-1.82, -12.47) * mm});
            skLineSegment(sketch, "E3349", {"start": v(-1.82, -12.47) * mm, "end": v(-1.79, -12.6) * mm});
            skLineSegment(sketch, "E3350", {"start": v(-1.79, -12.6) * mm, "end": v(-1.75, -12.73) * mm});
            skLineSegment(sketch, "E3351", {"start": v(-1.75, -12.73) * mm, "end": v(-1.72, -12.86) * mm});
            skLineSegment(sketch, "E3352", {"start": v(-1.72, -12.86) * mm, "end": v(-1.68, -13) * mm});
            skLineSegment(sketch, "E3353", {"start": v(-1.68, -13) * mm, "end": v(-1.64, -13.12) * mm});
            skLineSegment(sketch, "E3354", {"start": v(-1.64, -13.12) * mm, "end": v(-1.6, -13.25) * mm});
            skLineSegment(sketch, "E3355", {"start": v(-1.6, -13.25) * mm, "end": v(-1.56, -13.38) * mm});
            skLineSegment(sketch, "E3356", {"start": v(-1.56, -13.38) * mm, "end": v(-1.51, -13.51) * mm});
            skLineSegment(sketch, "E3357", {"start": v(-1.51, -13.51) * mm, "end": v(-1.47, -13.64) * mm});
            skLineSegment(sketch, "E3358", {"start": v(-1.47, -13.64) * mm, "end": v(-1.42, -13.77) * mm});
            skLineSegment(sketch, "E3359", {"start": v(-1.42, -13.77) * mm, "end": v(-1.37, -13.9) * mm});
            skLineSegment(sketch, "E3360", {"start": v(-1.37, -13.9) * mm, "end": v(-1.32, -14.03) * mm});
            skLineSegment(sketch, "E3361", {"start": v(-1.32, -14.03) * mm, "end": v(-1.26, -14.16) * mm});
            skLineSegment(sketch, "E3362", {"start": v(-1.26, -14.16) * mm, "end": v(-1.2, -14.3) * mm});
            skLineSegment(sketch, "E3363", {"start": v(-1.2, -14.3) * mm, "end": v(-1.15, -14.42) * mm});
            skLineSegment(sketch, "E3364", {"start": v(-1.15, -14.42) * mm, "end": v(-1.14, -14.44) * mm});
            skLineSegment(sketch, "E3365", {"start": v(-1.14, -14.44) * mm, "end": v(-0.5, -14.44) * mm});
            skLineSegment(sketch, "E3366", {"start": v(-0.5, -14.44) * mm, "end": v(-0.49, -14.4) * mm});
            skCircle(sketch, "E3367", {"center": v(-0.77, 0) * mm, "radius": 1 * mm});
            skSolve(sketch);
        }
        {
            var Q0;
            Q0=makeQuery(id+"F0.imprint","IMPRINT",FACE,{"disambiguationData":[TD([[makeQuery(id+"F0.imprint","IMPRINT",EDGE,{"derivedFrom":sQuery(id+"F0.wireOp",EDGE,"E0")}),1.0]])]});
            extrude(context, id + "F1", {"entities" : qUnion([Q0]), "depth" : 5 * mm});
        }
    });
